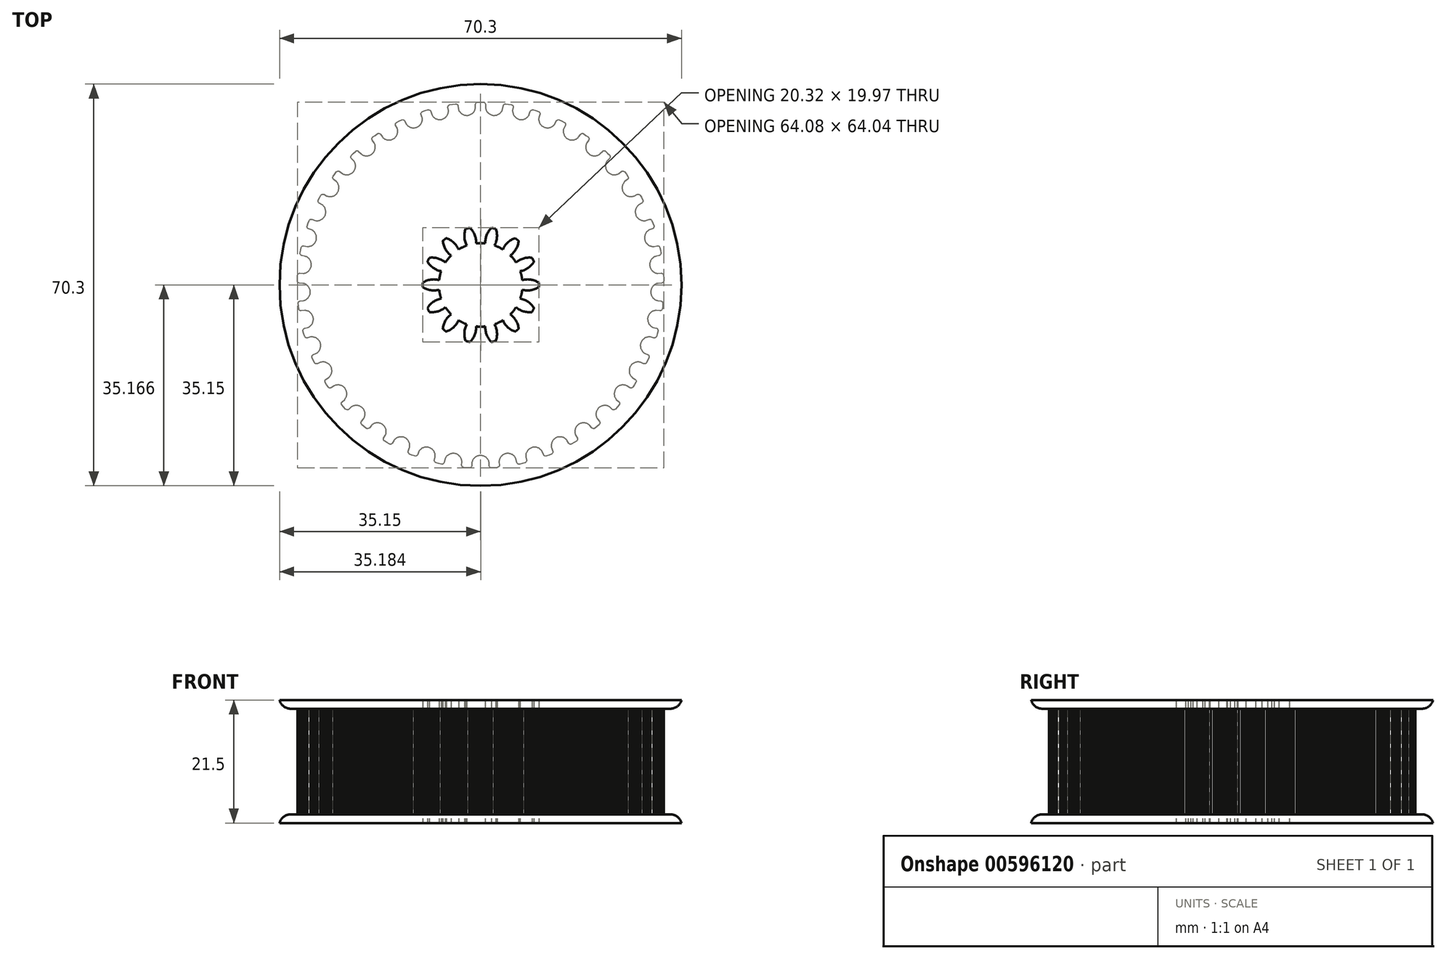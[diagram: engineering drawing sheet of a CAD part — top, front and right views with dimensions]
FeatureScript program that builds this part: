
annotation { "Feature Type Name" : "Feature", "Feature Type Description" : "" }
export const myFeature = defineFeature(function(context is Context, id is Id, definition is map)
    precondition{}
    {
        {
            assignVariable(context, id + "F0", {"name" : "totalThick", "anyValue" : 21.5});
        }
        {
            assignVariable(context, id + "F1", {"name" : "idlerThick", "anyValue" : 1.5});
        }
        {
            assignVariable(context, id + "F2", {"name" : "filletSize", "anyValue" : 2});
        }
        {
            var Q0;
            Q0=qCreatedBy(makeId("Top.planeOp"),FACE);
            var sketch = newSketch(context, id + "F3", { "sketchPlane" : qUnion([Q0])});
            skLineSegment(sketch, "E0", {"start": v(2.45, -32) * mm, "end": v(2.94, -31.95) * mm});
            skLineSegment(sketch, "E1", {"start": v(2.94, -31.95) * mm, "end": v(3.07, -31.9) * mm});
            skLineSegment(sketch, "E2", {"start": v(3.07, -31.9) * mm, "end": v(3.19, -31.81) * mm});
            skLineSegment(sketch, "E3", {"start": v(3.19, -31.81) * mm, "end": v(3.27, -31.68) * mm});
            skLineSegment(sketch, "E4", {"start": v(3.27, -31.68) * mm, "end": v(3.3, -31.54) * mm});
            skLineSegment(sketch, "E5", {"start": v(3.3, -31.54) * mm, "end": v(3.25, -30.93) * mm});
            skLineSegment(sketch, "E6", {"start": v(3.25, -30.93) * mm, "end": v(3.26, -30.8) * mm});
            skLineSegment(sketch, "E7", {"start": v(3.26, -30.8) * mm, "end": v(3.28, -30.67) * mm});
            skLineSegment(sketch, "E8", {"start": v(3.28, -30.67) * mm, "end": v(3.32, -30.55) * mm});
            skLineSegment(sketch, "E9", {"start": v(3.32, -30.55) * mm, "end": v(3.36, -30.42) * mm});
            skLineSegment(sketch, "E10", {"start": v(3.36, -30.42) * mm, "end": v(3.41, -30.3) * mm});
            skLineSegment(sketch, "E11", {"start": v(3.41, -30.3) * mm, "end": v(3.48, -30.2) * mm});
            skLineSegment(sketch, "E12", {"start": v(3.48, -30.2) * mm, "end": v(3.55, -30.09) * mm});
            skLineSegment(sketch, "E13", {"start": v(3.55, -30.09) * mm, "end": v(3.63, -30) * mm});
            skLineSegment(sketch, "E14", {"start": v(3.63, -30) * mm, "end": v(3.72, -29.9) * mm});
            skLineSegment(sketch, "E15", {"start": v(3.72, -29.9) * mm, "end": v(3.82, -29.81) * mm});
            skLineSegment(sketch, "E16", {"start": v(3.82, -29.81) * mm, "end": v(3.93, -29.73) * mm});
            skLineSegment(sketch, "E17", {"start": v(3.93, -29.73) * mm, "end": v(4.04, -29.66) * mm});
            skLineSegment(sketch, "E18", {"start": v(4.04, -29.66) * mm, "end": v(4.16, -29.6) * mm});
            skLineSegment(sketch, "E19", {"start": v(4.16, -29.6) * mm, "end": v(4.28, -29.55) * mm});
            skLineSegment(sketch, "E20", {"start": v(4.28, -29.55) * mm, "end": v(4.41, -29.5) * mm});
            skLineSegment(sketch, "E21", {"start": v(4.41, -29.5) * mm, "end": v(4.55, -29.48) * mm});
            skLineSegment(sketch, "E22", {"start": v(4.55, -29.48) * mm, "end": v(4.69, -29.47) * mm});
            skLineSegment(sketch, "E23", {"start": v(4.69, -29.47) * mm, "end": v(4.82, -29.47) * mm});
            skLineSegment(sketch, "E24", {"start": v(4.82, -29.47) * mm, "end": v(4.96, -29.48) * mm});
            skLineSegment(sketch, "E25", {"start": v(4.96, -29.48) * mm, "end": v(5.09, -29.5) * mm});
            skLineSegment(sketch, "E26", {"start": v(5.09, -29.5) * mm, "end": v(5.22, -29.53) * mm});
            skLineSegment(sketch, "E27", {"start": v(5.22, -29.53) * mm, "end": v(5.34, -29.58) * mm});
            skLineSegment(sketch, "E28", {"start": v(5.34, -29.58) * mm, "end": v(5.46, -29.63) * mm});
            skLineSegment(sketch, "E29", {"start": v(5.46, -29.63) * mm, "end": v(5.57, -29.7) * mm});
            skLineSegment(sketch, "E30", {"start": v(5.57, -29.7) * mm, "end": v(5.68, -29.76) * mm});
            skLineSegment(sketch, "E31", {"start": v(5.68, -29.76) * mm, "end": v(5.78, -29.84) * mm});
            skLineSegment(sketch, "E32", {"start": v(5.78, -29.84) * mm, "end": v(5.88, -29.93) * mm});
            skLineSegment(sketch, "E33", {"start": v(5.88, -29.93) * mm, "end": v(5.97, -30.02) * mm});
            skLineSegment(sketch, "E34", {"start": v(5.97, -30.02) * mm, "end": v(6.04, -30.12) * mm});
            skLineSegment(sketch, "E35", {"start": v(6.04, -30.12) * mm, "end": v(6.11, -30.23) * mm});
            skLineSegment(sketch, "E36", {"start": v(6.11, -30.23) * mm, "end": v(6.17, -30.35) * mm});
            skLineSegment(sketch, "E37", {"start": v(6.17, -30.35) * mm, "end": v(6.22, -30.47) * mm});
            skLineSegment(sketch, "E38", {"start": v(6.22, -30.47) * mm, "end": v(6.36, -31.06) * mm});
            skLineSegment(sketch, "E39", {"start": v(6.36, -31.06) * mm, "end": v(6.43, -31.2) * mm});
            skLineSegment(sketch, "E40", {"start": v(6.43, -31.2) * mm, "end": v(6.55, -31.3) * mm});
            skLineSegment(sketch, "E41", {"start": v(6.55, -31.3) * mm, "end": v(6.7, -31.35) * mm});
            skLineSegment(sketch, "E42", {"start": v(6.7, -31.35) * mm, "end": v(6.83, -31.35) * mm});
            skLineSegment(sketch, "E43", {"start": v(6.83, -31.35) * mm, "end": v(7.3, -31.25) * mm});
            skLineSegment(sketch, "E44", {"start": v(7.3, -31.25) * mm, "end": v(7.78, -31.12) * mm});
            skLineSegment(sketch, "E45", {"start": v(7.78, -31.12) * mm, "end": v(7.9, -31.06) * mm});
            skLineSegment(sketch, "E46", {"start": v(7.9, -31.06) * mm, "end": v(8, -30.95) * mm});
            skLineSegment(sketch, "E47", {"start": v(8, -30.95) * mm, "end": v(8.06, -30.81) * mm});
            skLineSegment(sketch, "E48", {"start": v(8.06, -30.81) * mm, "end": v(8.07, -30.66) * mm});
            skLineSegment(sketch, "E49", {"start": v(8.07, -30.66) * mm, "end": v(7.93, -30.07) * mm});
            skLineSegment(sketch, "E50", {"start": v(7.93, -30.07) * mm, "end": v(7.92, -29.94) * mm});
            skLineSegment(sketch, "E51", {"start": v(7.92, -29.94) * mm, "end": v(7.92, -29.81) * mm});
            skLineSegment(sketch, "E52", {"start": v(7.92, -29.81) * mm, "end": v(7.94, -29.68) * mm});
            skLineSegment(sketch, "E53", {"start": v(7.94, -29.68) * mm, "end": v(7.96, -29.55) * mm});
            skLineSegment(sketch, "E54", {"start": v(7.96, -29.55) * mm, "end": v(8, -29.43) * mm});
            skLineSegment(sketch, "E55", {"start": v(8, -29.43) * mm, "end": v(8.04, -29.31) * mm});
            skLineSegment(sketch, "E56", {"start": v(8.04, -29.31) * mm, "end": v(8.1, -29.2) * mm});
            skLineSegment(sketch, "E57", {"start": v(8.1, -29.2) * mm, "end": v(8.16, -29.08) * mm});
            skLineSegment(sketch, "E58", {"start": v(8.16, -29.08) * mm, "end": v(8.24, -28.98) * mm});
            skLineSegment(sketch, "E59", {"start": v(8.24, -28.98) * mm, "end": v(8.32, -28.88) * mm});
            skLineSegment(sketch, "E60", {"start": v(8.32, -28.88) * mm, "end": v(8.41, -28.79) * mm});
            skLineSegment(sketch, "E61", {"start": v(8.41, -28.79) * mm, "end": v(8.52, -28.7) * mm});
            skLineSegment(sketch, "E62", {"start": v(8.52, -28.7) * mm, "end": v(8.62, -28.62) * mm});
            skLineSegment(sketch, "E63", {"start": v(8.62, -28.62) * mm, "end": v(8.74, -28.55) * mm});
            skLineSegment(sketch, "E64", {"start": v(8.74, -28.55) * mm, "end": v(8.86, -28.5) * mm});
            skLineSegment(sketch, "E65", {"start": v(8.86, -28.5) * mm, "end": v(8.99, -28.44) * mm});
            skLineSegment(sketch, "E66", {"start": v(8.99, -28.44) * mm, "end": v(9.12, -28.4) * mm});
            skLineSegment(sketch, "E67", {"start": v(9.12, -28.4) * mm, "end": v(9.26, -28.39) * mm});
            skLineSegment(sketch, "E68", {"start": v(9.26, -28.39) * mm, "end": v(9.4, -28.38) * mm});
            skLineSegment(sketch, "E69", {"start": v(9.4, -28.38) * mm, "end": v(9.53, -28.38) * mm});
            skLineSegment(sketch, "E70", {"start": v(9.53, -28.38) * mm, "end": v(9.66, -28.4) * mm});
            skLineSegment(sketch, "E71", {"start": v(9.66, -28.4) * mm, "end": v(9.79, -28.41) * mm});
            skLineSegment(sketch, "E72", {"start": v(9.79, -28.41) * mm, "end": v(9.91, -28.45) * mm});
            skLineSegment(sketch, "E73", {"start": v(9.91, -28.45) * mm, "end": v(10.04, -28.5) * mm});
            skLineSegment(sketch, "E74", {"start": v(10.04, -28.5) * mm, "end": v(10.15, -28.54) * mm});
            skLineSegment(sketch, "E75", {"start": v(10.15, -28.54) * mm, "end": v(10.27, -28.6) * mm});
            skLineSegment(sketch, "E76", {"start": v(10.27, -28.6) * mm, "end": v(10.37, -28.68) * mm});
            skLineSegment(sketch, "E77", {"start": v(10.37, -28.68) * mm, "end": v(10.47, -28.76) * mm});
            skLineSegment(sketch, "E78", {"start": v(10.47, -28.76) * mm, "end": v(10.57, -28.85) * mm});
            skLineSegment(sketch, "E79", {"start": v(10.57, -28.85) * mm, "end": v(10.65, -28.95) * mm});
            skLineSegment(sketch, "E80", {"start": v(10.65, -28.95) * mm, "end": v(10.73, -29.05) * mm});
            skLineSegment(sketch, "E81", {"start": v(10.73, -29.05) * mm, "end": v(10.8, -29.17) * mm});
            skLineSegment(sketch, "E82", {"start": v(10.8, -29.17) * mm, "end": v(11.02, -29.73) * mm});
            skLineSegment(sketch, "E83", {"start": v(11.02, -29.73) * mm, "end": v(11.11, -29.85) * mm});
            skLineSegment(sketch, "E84", {"start": v(11.11, -29.85) * mm, "end": v(11.24, -29.93) * mm});
            skLineSegment(sketch, "E85", {"start": v(11.24, -29.93) * mm, "end": v(11.4, -29.96) * mm});
            skLineSegment(sketch, "E86", {"start": v(11.4, -29.96) * mm, "end": v(11.53, -29.94) * mm});
            skLineSegment(sketch, "E87", {"start": v(11.53, -29.94) * mm, "end": v(11.98, -29.76) * mm});
            skLineSegment(sketch, "E88", {"start": v(11.98, -29.76) * mm, "end": v(12.43, -29.57) * mm});
            skLineSegment(sketch, "E89", {"start": v(12.43, -29.57) * mm, "end": v(12.54, -29.5) * mm});
            skLineSegment(sketch, "E90", {"start": v(12.54, -29.5) * mm, "end": v(12.63, -29.37) * mm});
            skLineSegment(sketch, "E91", {"start": v(12.63, -29.37) * mm, "end": v(12.67, -29.22) * mm});
            skLineSegment(sketch, "E92", {"start": v(12.67, -29.22) * mm, "end": v(12.65, -29.07) * mm});
            skLineSegment(sketch, "E93", {"start": v(12.65, -29.07) * mm, "end": v(12.42, -28.5) * mm});
            skLineSegment(sketch, "E94", {"start": v(12.42, -28.5) * mm, "end": v(12.4, -28.38) * mm});
            skLineSegment(sketch, "E95", {"start": v(12.4, -28.38) * mm, "end": v(12.37, -28.25) * mm});
            skLineSegment(sketch, "E96", {"start": v(12.37, -28.25) * mm, "end": v(12.37, -28.12) * mm});
            skLineSegment(sketch, "E97", {"start": v(12.37, -28.12) * mm, "end": v(12.37, -28) * mm});
            skLineSegment(sketch, "E98", {"start": v(12.37, -28) * mm, "end": v(12.4, -27.87) * mm});
            skLineSegment(sketch, "E99", {"start": v(12.4, -27.87) * mm, "end": v(12.42, -27.74) * mm});
            skLineSegment(sketch, "E100", {"start": v(12.42, -27.74) * mm, "end": v(12.45, -27.62) * mm});
            skLineSegment(sketch, "E101", {"start": v(12.45, -27.62) * mm, "end": v(12.5, -27.5) * mm});
            skLineSegment(sketch, "E102", {"start": v(12.5, -27.5) * mm, "end": v(12.56, -27.38) * mm});
            skLineSegment(sketch, "E103", {"start": v(12.56, -27.38) * mm, "end": v(12.63, -27.27) * mm});
            skLineSegment(sketch, "E104", {"start": v(12.63, -27.27) * mm, "end": v(12.7, -27.16) * mm});
            skLineSegment(sketch, "E105", {"start": v(12.7, -27.16) * mm, "end": v(12.8, -27.06) * mm});
            skLineSegment(sketch, "E106", {"start": v(12.8, -27.06) * mm, "end": v(12.89, -26.97) * mm});
            skLineSegment(sketch, "E107", {"start": v(12.89, -26.97) * mm, "end": v(12.99, -26.88) * mm});
            skLineSegment(sketch, "E108", {"start": v(12.99, -26.88) * mm, "end": v(13.1, -26.8) * mm});
            skLineSegment(sketch, "E109", {"start": v(13.1, -26.8) * mm, "end": v(13.22, -26.73) * mm});
            skLineSegment(sketch, "E110", {"start": v(13.22, -26.73) * mm, "end": v(13.35, -26.68) * mm});
            skLineSegment(sketch, "E111", {"start": v(13.35, -26.68) * mm, "end": v(13.48, -26.64) * mm});
            skLineSegment(sketch, "E112", {"start": v(13.48, -26.64) * mm, "end": v(13.61, -26.61) * mm});
            skLineSegment(sketch, "E113", {"start": v(13.61, -26.61) * mm, "end": v(13.74, -26.6) * mm});
            skLineSegment(sketch, "E114", {"start": v(13.74, -26.6) * mm, "end": v(13.88, -26.58) * mm});
            skLineSegment(sketch, "E115", {"start": v(13.88, -26.58) * mm, "end": v(14, -26.59) * mm});
            skLineSegment(sketch, "E116", {"start": v(14, -26.59) * mm, "end": v(14.14, -26.6) * mm});
            skLineSegment(sketch, "E117", {"start": v(14.14, -26.6) * mm, "end": v(14.26, -26.63) * mm});
            skLineSegment(sketch, "E118", {"start": v(14.26, -26.63) * mm, "end": v(14.39, -26.66) * mm});
            skLineSegment(sketch, "E119", {"start": v(14.39, -26.66) * mm, "end": v(14.5, -26.7) * mm});
            skLineSegment(sketch, "E120", {"start": v(14.5, -26.7) * mm, "end": v(14.62, -26.76) * mm});
            skLineSegment(sketch, "E121", {"start": v(14.62, -26.76) * mm, "end": v(14.74, -26.82) * mm});
            skLineSegment(sketch, "E122", {"start": v(14.74, -26.82) * mm, "end": v(14.84, -26.9) * mm});
            skLineSegment(sketch, "E123", {"start": v(14.84, -26.9) * mm, "end": v(14.94, -26.98) * mm});
            skLineSegment(sketch, "E124", {"start": v(14.94, -26.98) * mm, "end": v(15.03, -27.07) * mm});
            skLineSegment(sketch, "E125", {"start": v(15.03, -27.07) * mm, "end": v(15.12, -27.18) * mm});
            skLineSegment(sketch, "E126", {"start": v(15.12, -27.18) * mm, "end": v(15.42, -27.7) * mm});
            skLineSegment(sketch, "E127", {"start": v(15.42, -27.7) * mm, "end": v(15.53, -27.8) * mm});
            skLineSegment(sketch, "E128", {"start": v(15.53, -27.8) * mm, "end": v(15.67, -27.86) * mm});
            skLineSegment(sketch, "E129", {"start": v(15.67, -27.86) * mm, "end": v(15.83, -27.87) * mm});
            skLineSegment(sketch, "E130", {"start": v(15.83, -27.87) * mm, "end": v(15.96, -27.83) * mm});
            skLineSegment(sketch, "E131", {"start": v(15.96, -27.83) * mm, "end": v(16.38, -27.59) * mm});
            skLineSegment(sketch, "E132", {"start": v(16.38, -27.59) * mm, "end": v(16.8, -27.33) * mm});
            skLineSegment(sketch, "E133", {"start": v(16.8, -27.33) * mm, "end": v(16.9, -27.23) * mm});
            skLineSegment(sketch, "E134", {"start": v(16.9, -27.23) * mm, "end": v(16.96, -27.1) * mm});
            skLineSegment(sketch, "E135", {"start": v(16.96, -27.1) * mm, "end": v(16.98, -26.95) * mm});
            skLineSegment(sketch, "E136", {"start": v(16.98, -26.95) * mm, "end": v(16.94, -26.8) * mm});
            skLineSegment(sketch, "E137", {"start": v(16.94, -26.8) * mm, "end": v(16.62, -26.28) * mm});
            skLineSegment(sketch, "E138", {"start": v(16.62, -26.28) * mm, "end": v(16.58, -26.16) * mm});
            skLineSegment(sketch, "E139", {"start": v(16.58, -26.16) * mm, "end": v(16.54, -26.03) * mm});
            skLineSegment(sketch, "E140", {"start": v(16.54, -26.03) * mm, "end": v(16.51, -25.9) * mm});
            skLineSegment(sketch, "E141", {"start": v(16.51, -25.9) * mm, "end": v(16.5, -25.78) * mm});
            skLineSegment(sketch, "E142", {"start": v(16.5, -25.78) * mm, "end": v(16.5, -25.65) * mm});
            skLineSegment(sketch, "E143", {"start": v(16.5, -25.65) * mm, "end": v(16.5, -25.52) * mm});
            skLineSegment(sketch, "E144", {"start": v(16.5, -25.52) * mm, "end": v(16.52, -25.4) * mm});
            skLineSegment(sketch, "E145", {"start": v(16.52, -25.4) * mm, "end": v(16.55, -25.27) * mm});
            skLineSegment(sketch, "E146", {"start": v(16.55, -25.27) * mm, "end": v(16.59, -25.14) * mm});
            skLineSegment(sketch, "E147", {"start": v(16.59, -25.14) * mm, "end": v(16.64, -25.02) * mm});
            skLineSegment(sketch, "E148", {"start": v(16.64, -25.02) * mm, "end": v(16.7, -24.9) * mm});
            skLineSegment(sketch, "E149", {"start": v(16.7, -24.9) * mm, "end": v(16.77, -24.8) * mm});
            skLineSegment(sketch, "E150", {"start": v(16.77, -24.8) * mm, "end": v(16.85, -24.69) * mm});
            skLineSegment(sketch, "E151", {"start": v(16.85, -24.69) * mm, "end": v(16.94, -24.59) * mm});
            skLineSegment(sketch, "E152", {"start": v(16.94, -24.59) * mm, "end": v(17.03, -24.5) * mm});
            skLineSegment(sketch, "E153", {"start": v(17.03, -24.5) * mm, "end": v(17.14, -24.4) * mm});
            skLineSegment(sketch, "E154", {"start": v(17.14, -24.4) * mm, "end": v(17.26, -24.33) * mm});
            skLineSegment(sketch, "E155", {"start": v(17.26, -24.33) * mm, "end": v(17.38, -24.27) * mm});
            skLineSegment(sketch, "E156", {"start": v(17.38, -24.27) * mm, "end": v(17.5, -24.22) * mm});
            skLineSegment(sketch, "E157", {"start": v(17.5, -24.22) * mm, "end": v(17.64, -24.18) * mm});
            skLineSegment(sketch, "E158", {"start": v(17.64, -24.18) * mm, "end": v(17.77, -24.16) * mm});
            skLineSegment(sketch, "E159", {"start": v(17.77, -24.16) * mm, "end": v(17.9, -24.14) * mm});
            skLineSegment(sketch, "E160", {"start": v(17.9, -24.14) * mm, "end": v(18.03, -24.13) * mm});
            skLineSegment(sketch, "E161", {"start": v(18.03, -24.13) * mm, "end": v(18.16, -24.14) * mm});
            skLineSegment(sketch, "E162", {"start": v(18.16, -24.14) * mm, "end": v(18.28, -24.15) * mm});
            skLineSegment(sketch, "E163", {"start": v(18.28, -24.15) * mm, "end": v(18.4, -24.18) * mm});
            skLineSegment(sketch, "E164", {"start": v(18.4, -24.18) * mm, "end": v(18.53, -24.21) * mm});
            skLineSegment(sketch, "E165", {"start": v(18.53, -24.21) * mm, "end": v(18.65, -24.26) * mm});
            skLineSegment(sketch, "E166", {"start": v(18.65, -24.26) * mm, "end": v(18.77, -24.32) * mm});
            skLineSegment(sketch, "E167", {"start": v(18.77, -24.32) * mm, "end": v(18.88, -24.39) * mm});
            skLineSegment(sketch, "E168", {"start": v(18.88, -24.39) * mm, "end": v(18.98, -24.46) * mm});
            skLineSegment(sketch, "E169", {"start": v(18.98, -24.46) * mm, "end": v(19.08, -24.55) * mm});
            skLineSegment(sketch, "E170", {"start": v(19.08, -24.55) * mm, "end": v(19.47, -25.02) * mm});
            skLineSegment(sketch, "E171", {"start": v(19.47, -25.02) * mm, "end": v(19.6, -25.1) * mm});
            skLineSegment(sketch, "E172", {"start": v(19.6, -25.1) * mm, "end": v(19.74, -25.14) * mm});
            skLineSegment(sketch, "E173", {"start": v(19.74, -25.14) * mm, "end": v(19.9, -25.12) * mm});
            skLineSegment(sketch, "E174", {"start": v(19.9, -25.12) * mm, "end": v(20.01, -25.07) * mm});
            skLineSegment(sketch, "E175", {"start": v(20.01, -25.07) * mm, "end": v(20.4, -24.76) * mm});
            skLineSegment(sketch, "E176", {"start": v(20.4, -24.76) * mm, "end": v(20.77, -24.45) * mm});
            skLineSegment(sketch, "E177", {"start": v(20.77, -24.45) * mm, "end": v(20.85, -24.34) * mm});
            skLineSegment(sketch, "E178", {"start": v(20.85, -24.34) * mm, "end": v(20.9, -24.2) * mm});
            skLineSegment(sketch, "E179", {"start": v(20.9, -24.2) * mm, "end": v(20.88, -24.04) * mm});
            skLineSegment(sketch, "E180", {"start": v(20.88, -24.04) * mm, "end": v(20.83, -23.9) * mm});
            skLineSegment(sketch, "E181", {"start": v(20.83, -23.9) * mm, "end": v(20.44, -23.43) * mm});
            skLineSegment(sketch, "E182", {"start": v(20.44, -23.43) * mm, "end": v(20.37, -23.32) * mm});
            skLineSegment(sketch, "E183", {"start": v(20.37, -23.32) * mm, "end": v(20.31, -23.2) * mm});
            skLineSegment(sketch, "E184", {"start": v(20.31, -23.2) * mm, "end": v(20.27, -23.08) * mm});
            skLineSegment(sketch, "E185", {"start": v(20.27, -23.08) * mm, "end": v(20.23, -22.96) * mm});
            skLineSegment(sketch, "E186", {"start": v(20.23, -22.96) * mm, "end": v(20.21, -22.83) * mm});
            skLineSegment(sketch, "E187", {"start": v(20.21, -22.83) * mm, "end": v(20.2, -22.7) * mm});
            skLineSegment(sketch, "E188", {"start": v(20.2, -22.7) * mm, "end": v(20.2, -22.57) * mm});
            skLineSegment(sketch, "E189", {"start": v(20.2, -22.57) * mm, "end": v(20.2, -22.45) * mm});
            skLineSegment(sketch, "E190", {"start": v(20.2, -22.45) * mm, "end": v(20.23, -22.32) * mm});
            skLineSegment(sketch, "E191", {"start": v(20.23, -22.32) * mm, "end": v(20.26, -22.2) * mm});
            skLineSegment(sketch, "E192", {"start": v(20.26, -22.2) * mm, "end": v(20.3, -22.07) * mm});
            skLineSegment(sketch, "E193", {"start": v(20.3, -22.07) * mm, "end": v(20.35, -21.94) * mm});
            skLineSegment(sketch, "E194", {"start": v(20.35, -21.94) * mm, "end": v(20.41, -21.83) * mm});
            skLineSegment(sketch, "E195", {"start": v(20.41, -21.83) * mm, "end": v(20.49, -21.71) * mm});
            skLineSegment(sketch, "E196", {"start": v(20.49, -21.71) * mm, "end": v(20.57, -21.6) * mm});
            skLineSegment(sketch, "E197", {"start": v(20.57, -21.6) * mm, "end": v(20.66, -21.5) * mm});
            skLineSegment(sketch, "E198", {"start": v(20.66, -21.5) * mm, "end": v(20.77, -21.41) * mm});
            skLineSegment(sketch, "E199", {"start": v(20.77, -21.41) * mm, "end": v(20.88, -21.33) * mm});
            skLineSegment(sketch, "E200", {"start": v(20.88, -21.33) * mm, "end": v(21, -21.27) * mm});
            skLineSegment(sketch, "E201", {"start": v(21, -21.27) * mm, "end": v(21.12, -21.2) * mm});
            skLineSegment(sketch, "E202", {"start": v(21.12, -21.2) * mm, "end": v(21.24, -21.16) * mm});
            skLineSegment(sketch, "E203", {"start": v(21.24, -21.16) * mm, "end": v(21.37, -21.12) * mm});
            skLineSegment(sketch, "E204", {"start": v(21.37, -21.12) * mm, "end": v(21.5, -21.1) * mm});
            skLineSegment(sketch, "E205", {"start": v(21.5, -21.1) * mm, "end": v(21.62, -21.08) * mm});
            skLineSegment(sketch, "E206", {"start": v(21.62, -21.08) * mm, "end": v(21.75, -21.08) * mm});
            skLineSegment(sketch, "E207", {"start": v(21.75, -21.08) * mm, "end": v(21.88, -21.08) * mm});
            skLineSegment(sketch, "E208", {"start": v(21.88, -21.08) * mm, "end": v(22, -21.1) * mm});
            skLineSegment(sketch, "E209", {"start": v(22, -21.1) * mm, "end": v(22.13, -21.13) * mm});
            skLineSegment(sketch, "E210", {"start": v(22.13, -21.13) * mm, "end": v(22.26, -21.17) * mm});
            skLineSegment(sketch, "E211", {"start": v(22.26, -21.17) * mm, "end": v(22.38, -21.22) * mm});
            skLineSegment(sketch, "E212", {"start": v(22.38, -21.22) * mm, "end": v(22.5, -21.28) * mm});
            skLineSegment(sketch, "E213", {"start": v(22.5, -21.28) * mm, "end": v(22.6, -21.35) * mm});
            skLineSegment(sketch, "E214", {"start": v(22.6, -21.35) * mm, "end": v(23.05, -21.76) * mm});
            skLineSegment(sketch, "E215", {"start": v(23.05, -21.76) * mm, "end": v(23.19, -21.82) * mm});
            skLineSegment(sketch, "E216", {"start": v(23.19, -21.82) * mm, "end": v(23.34, -21.83) * mm});
            skLineSegment(sketch, "E217", {"start": v(23.34, -21.83) * mm, "end": v(23.49, -21.8) * mm});
            skLineSegment(sketch, "E218", {"start": v(23.49, -21.8) * mm, "end": v(23.6, -21.72) * mm});
            skLineSegment(sketch, "E219", {"start": v(23.6, -21.72) * mm, "end": v(23.93, -21.36) * mm});
            skLineSegment(sketch, "E220", {"start": v(23.93, -21.36) * mm, "end": v(24.25, -20.99) * mm});
            skLineSegment(sketch, "E221", {"start": v(24.25, -20.99) * mm, "end": v(24.31, -20.87) * mm});
            skLineSegment(sketch, "E222", {"start": v(24.31, -20.87) * mm, "end": v(24.33, -20.72) * mm});
            skLineSegment(sketch, "E223", {"start": v(24.33, -20.72) * mm, "end": v(24.3, -20.57) * mm});
            skLineSegment(sketch, "E224", {"start": v(24.3, -20.57) * mm, "end": v(24.22, -20.44) * mm});
            skLineSegment(sketch, "E225", {"start": v(24.22, -20.44) * mm, "end": v(23.77, -20.04) * mm});
            skLineSegment(sketch, "E226", {"start": v(23.77, -20.04) * mm, "end": v(23.68, -19.94) * mm});
            skLineSegment(sketch, "E227", {"start": v(23.68, -19.94) * mm, "end": v(23.61, -19.83) * mm});
            skLineSegment(sketch, "E228", {"start": v(23.61, -19.83) * mm, "end": v(23.55, -19.72) * mm});
            skLineSegment(sketch, "E229", {"start": v(23.55, -19.72) * mm, "end": v(23.5, -19.6) * mm});
            skLineSegment(sketch, "E230", {"start": v(23.5, -19.6) * mm, "end": v(23.45, -19.48) * mm});
            skLineSegment(sketch, "E231", {"start": v(23.45, -19.48) * mm, "end": v(23.42, -19.35) * mm});
            skLineSegment(sketch, "E232", {"start": v(23.42, -19.35) * mm, "end": v(23.4, -19.23) * mm});
            skLineSegment(sketch, "E233", {"start": v(23.4, -19.23) * mm, "end": v(23.4, -19.1) * mm});
            skLineSegment(sketch, "E234", {"start": v(23.4, -19.1) * mm, "end": v(23.4, -18.97) * mm});
            skLineSegment(sketch, "E235", {"start": v(23.4, -18.97) * mm, "end": v(23.4, -18.84) * mm});
            skLineSegment(sketch, "E236", {"start": v(23.4, -18.84) * mm, "end": v(23.42, -18.7) * mm});
            skLineSegment(sketch, "E237", {"start": v(23.42, -18.7) * mm, "end": v(23.46, -18.58) * mm});
            skLineSegment(sketch, "E238", {"start": v(23.46, -18.58) * mm, "end": v(23.5, -18.46) * mm});
            skLineSegment(sketch, "E239", {"start": v(23.5, -18.46) * mm, "end": v(23.55, -18.33) * mm});
            skLineSegment(sketch, "E240", {"start": v(23.55, -18.33) * mm, "end": v(23.62, -18.21) * mm});
            skLineSegment(sketch, "E241", {"start": v(23.62, -18.21) * mm, "end": v(23.7, -18.1) * mm});
            skLineSegment(sketch, "E242", {"start": v(23.7, -18.1) * mm, "end": v(23.79, -18) * mm});
            skLineSegment(sketch, "E243", {"start": v(23.79, -18) * mm, "end": v(23.89, -17.9) * mm});
            skLineSegment(sketch, "E244", {"start": v(23.89, -17.9) * mm, "end": v(24, -17.81) * mm});
            skLineSegment(sketch, "E245", {"start": v(24, -17.81) * mm, "end": v(24.1, -17.74) * mm});
            skLineSegment(sketch, "E246", {"start": v(24.1, -17.74) * mm, "end": v(24.22, -17.67) * mm});
            skLineSegment(sketch, "E247", {"start": v(24.22, -17.67) * mm, "end": v(24.33, -17.62) * mm});
            skLineSegment(sketch, "E248", {"start": v(24.33, -17.62) * mm, "end": v(24.46, -17.57) * mm});
            skLineSegment(sketch, "E249", {"start": v(24.46, -17.57) * mm, "end": v(24.58, -17.54) * mm});
            skLineSegment(sketch, "E250", {"start": v(24.58, -17.54) * mm, "end": v(24.7, -17.51) * mm});
            skLineSegment(sketch, "E251", {"start": v(24.7, -17.51) * mm, "end": v(24.84, -17.5) * mm});
            skLineSegment(sketch, "E252", {"start": v(24.84, -17.5) * mm, "end": v(24.97, -17.5) * mm});
            skLineSegment(sketch, "E253", {"start": v(24.97, -17.5) * mm, "end": v(25.1, -17.5) * mm});
            skLineSegment(sketch, "E254", {"start": v(25.1, -17.5) * mm, "end": v(25.22, -17.52) * mm});
            skLineSegment(sketch, "E255", {"start": v(25.22, -17.52) * mm, "end": v(25.35, -17.55) * mm});
            skLineSegment(sketch, "E256", {"start": v(25.35, -17.55) * mm, "end": v(25.47, -17.6) * mm});
            skLineSegment(sketch, "E257", {"start": v(25.47, -17.6) * mm, "end": v(25.6, -17.65) * mm});
            skLineSegment(sketch, "E258", {"start": v(25.6, -17.65) * mm, "end": v(26.1, -17.98) * mm});
            skLineSegment(sketch, "E259", {"start": v(26.1, -17.98) * mm, "end": v(26.24, -18.03) * mm});
            skLineSegment(sketch, "E260", {"start": v(26.24, -18.03) * mm, "end": v(26.4, -18.02) * mm});
            skLineSegment(sketch, "E261", {"start": v(26.4, -18.02) * mm, "end": v(26.53, -17.95) * mm});
            skLineSegment(sketch, "E262", {"start": v(26.53, -17.95) * mm, "end": v(26.63, -17.86) * mm});
            skLineSegment(sketch, "E263", {"start": v(26.63, -17.86) * mm, "end": v(26.9, -17.46) * mm});
            skLineSegment(sketch, "E264", {"start": v(26.9, -17.46) * mm, "end": v(27.16, -17.04) * mm});
            skLineSegment(sketch, "E265", {"start": v(27.16, -17.04) * mm, "end": v(27.2, -16.91) * mm});
            skLineSegment(sketch, "E266", {"start": v(27.2, -16.91) * mm, "end": v(27.2, -16.76) * mm});
            skLineSegment(sketch, "E267", {"start": v(27.2, -16.76) * mm, "end": v(27.16, -16.62) * mm});
            skLineSegment(sketch, "E268", {"start": v(27.16, -16.62) * mm, "end": v(27.06, -16.5) * mm});
            skLineSegment(sketch, "E269", {"start": v(27.06, -16.5) * mm, "end": v(26.54, -16.18) * mm});
            skLineSegment(sketch, "E270", {"start": v(26.54, -16.18) * mm, "end": v(26.45, -16.09) * mm});
            skLineSegment(sketch, "E271", {"start": v(26.45, -16.09) * mm, "end": v(26.36, -16) * mm});
            skLineSegment(sketch, "E272", {"start": v(26.36, -16) * mm, "end": v(26.28, -15.9) * mm});
            skLineSegment(sketch, "E273", {"start": v(26.28, -15.9) * mm, "end": v(26.2, -15.78) * mm});
            skLineSegment(sketch, "E274", {"start": v(26.2, -15.78) * mm, "end": v(26.15, -15.67) * mm});
            skLineSegment(sketch, "E275", {"start": v(26.15, -15.67) * mm, "end": v(26.1, -15.55) * mm});
            skLineSegment(sketch, "E276", {"start": v(26.1, -15.55) * mm, "end": v(26.06, -15.43) * mm});
            skLineSegment(sketch, "E277", {"start": v(26.06, -15.43) * mm, "end": v(26.03, -15.3) * mm});
            skLineSegment(sketch, "E278", {"start": v(26.03, -15.3) * mm, "end": v(26, -15.18) * mm});
            skLineSegment(sketch, "E279", {"start": v(26, -15.18) * mm, "end": v(26, -15.05) * mm});
            skLineSegment(sketch, "E280", {"start": v(26, -15.05) * mm, "end": v(26, -14.91) * mm});
            skLineSegment(sketch, "E281", {"start": v(26, -14.91) * mm, "end": v(26.01, -14.78) * mm});
            skLineSegment(sketch, "E282", {"start": v(26.01, -14.78) * mm, "end": v(26.04, -14.65) * mm});
            skLineSegment(sketch, "E283", {"start": v(26.04, -14.65) * mm, "end": v(26.07, -14.52) * mm});
            skLineSegment(sketch, "E284", {"start": v(26.07, -14.52) * mm, "end": v(26.12, -14.4) * mm});
            skLineSegment(sketch, "E285", {"start": v(26.12, -14.4) * mm, "end": v(26.18, -14.27) * mm});
            skLineSegment(sketch, "E286", {"start": v(26.18, -14.27) * mm, "end": v(26.25, -14.15) * mm});
            skLineSegment(sketch, "E287", {"start": v(26.25, -14.15) * mm, "end": v(26.33, -14.04) * mm});
            skLineSegment(sketch, "E288", {"start": v(26.33, -14.04) * mm, "end": v(26.42, -13.94) * mm});
            skLineSegment(sketch, "E289", {"start": v(26.42, -13.94) * mm, "end": v(26.52, -13.85) * mm});
            skLineSegment(sketch, "E290", {"start": v(26.52, -13.85) * mm, "end": v(26.62, -13.77) * mm});
            skLineSegment(sketch, "E291", {"start": v(26.62, -13.77) * mm, "end": v(26.73, -13.7) * mm});
            skLineSegment(sketch, "E292", {"start": v(26.73, -13.7) * mm, "end": v(26.85, -13.63) * mm});
            skLineSegment(sketch, "E293", {"start": v(26.85, -13.63) * mm, "end": v(26.97, -13.58) * mm});
            skLineSegment(sketch, "E294", {"start": v(26.97, -13.58) * mm, "end": v(27.09, -13.53) * mm});
            skLineSegment(sketch, "E295", {"start": v(27.09, -13.53) * mm, "end": v(27.21, -13.5) * mm});
            skLineSegment(sketch, "E296", {"start": v(27.21, -13.5) * mm, "end": v(27.34, -13.48) * mm});
            skLineSegment(sketch, "E297", {"start": v(27.34, -13.48) * mm, "end": v(27.47, -13.47) * mm});
            skLineSegment(sketch, "E298", {"start": v(27.47, -13.47) * mm, "end": v(27.6, -13.47) * mm});
            skLineSegment(sketch, "E299", {"start": v(27.6, -13.47) * mm, "end": v(27.72, -13.48) * mm});
            skLineSegment(sketch, "E300", {"start": v(27.72, -13.48) * mm, "end": v(27.85, -13.5) * mm});
            skLineSegment(sketch, "E301", {"start": v(27.85, -13.5) * mm, "end": v(27.98, -13.54) * mm});
            skLineSegment(sketch, "E302", {"start": v(27.98, -13.54) * mm, "end": v(28.53, -13.8) * mm});
            skLineSegment(sketch, "E303", {"start": v(28.53, -13.8) * mm, "end": v(28.68, -13.8) * mm});
            skLineSegment(sketch, "E304", {"start": v(28.68, -13.8) * mm, "end": v(28.83, -13.78) * mm});
            skLineSegment(sketch, "E305", {"start": v(28.83, -13.78) * mm, "end": v(28.96, -13.7) * mm});
            skLineSegment(sketch, "E306", {"start": v(28.96, -13.7) * mm, "end": v(29.04, -13.59) * mm});
            skLineSegment(sketch, "E307", {"start": v(29.04, -13.59) * mm, "end": v(29.25, -13.15) * mm});
            skLineSegment(sketch, "E308", {"start": v(29.25, -13.15) * mm, "end": v(29.44, -12.7) * mm});
            skLineSegment(sketch, "E309", {"start": v(29.44, -12.7) * mm, "end": v(29.47, -12.56) * mm});
            skLineSegment(sketch, "E310", {"start": v(29.47, -12.56) * mm, "end": v(29.44, -12.41) * mm});
            skLineSegment(sketch, "E311", {"start": v(29.44, -12.41) * mm, "end": v(29.37, -12.28) * mm});
            skLineSegment(sketch, "E312", {"start": v(29.37, -12.28) * mm, "end": v(29.25, -12.18) * mm});
            skLineSegment(sketch, "E313", {"start": v(29.25, -12.18) * mm, "end": v(28.7, -11.94) * mm});
            skLineSegment(sketch, "E314", {"start": v(28.7, -11.94) * mm, "end": v(28.59, -11.86) * mm});
            skLineSegment(sketch, "E315", {"start": v(28.59, -11.86) * mm, "end": v(28.48, -11.78) * mm});
            skLineSegment(sketch, "E316", {"start": v(28.48, -11.78) * mm, "end": v(28.4, -11.7) * mm});
            skLineSegment(sketch, "E317", {"start": v(28.4, -11.7) * mm, "end": v(28.3, -11.6) * mm});
            skLineSegment(sketch, "E318", {"start": v(28.3, -11.6) * mm, "end": v(28.23, -11.5) * mm});
            skLineSegment(sketch, "E319", {"start": v(28.23, -11.5) * mm, "end": v(28.16, -11.39) * mm});
            skLineSegment(sketch, "E320", {"start": v(28.16, -11.39) * mm, "end": v(28.1, -11.27) * mm});
            skLineSegment(sketch, "E321", {"start": v(28.1, -11.27) * mm, "end": v(28.05, -11.15) * mm});
            skLineSegment(sketch, "E322", {"start": v(28.05, -11.15) * mm, "end": v(28.01, -11.03) * mm});
            skLineSegment(sketch, "E323", {"start": v(28.01, -11.03) * mm, "end": v(27.99, -10.9) * mm});
            skLineSegment(sketch, "E324", {"start": v(27.99, -10.9) * mm, "end": v(27.97, -10.77) * mm});
            skLineSegment(sketch, "E325", {"start": v(27.97, -10.77) * mm, "end": v(27.96, -10.64) * mm});
            skLineSegment(sketch, "E326", {"start": v(27.96, -10.64) * mm, "end": v(27.96, -10.5) * mm});
            skLineSegment(sketch, "E327", {"start": v(27.96, -10.5) * mm, "end": v(27.98, -10.37) * mm});
            skLineSegment(sketch, "E328", {"start": v(27.98, -10.37) * mm, "end": v(28, -10.24) * mm});
            skLineSegment(sketch, "E329", {"start": v(28, -10.24) * mm, "end": v(28.04, -10.1) * mm});
            skLineSegment(sketch, "E330", {"start": v(28.04, -10.1) * mm, "end": v(28.1, -9.98) * mm});
            skLineSegment(sketch, "E331", {"start": v(28.1, -9.98) * mm, "end": v(28.16, -9.86) * mm});
            skLineSegment(sketch, "E332", {"start": v(28.16, -9.86) * mm, "end": v(28.24, -9.74) * mm});
            skLineSegment(sketch, "E333", {"start": v(28.24, -9.74) * mm, "end": v(28.32, -9.64) * mm});
            skLineSegment(sketch, "E334", {"start": v(28.32, -9.64) * mm, "end": v(28.4, -9.54) * mm});
            skLineSegment(sketch, "E335", {"start": v(28.4, -9.54) * mm, "end": v(28.5, -9.45) * mm});
            skLineSegment(sketch, "E336", {"start": v(28.5, -9.45) * mm, "end": v(28.6, -9.37) * mm});
            skLineSegment(sketch, "E337", {"start": v(28.6, -9.37) * mm, "end": v(28.72, -9.3) * mm});
            skLineSegment(sketch, "E338", {"start": v(28.72, -9.3) * mm, "end": v(28.83, -9.24) * mm});
            skLineSegment(sketch, "E339", {"start": v(28.83, -9.24) * mm, "end": v(28.95, -9.2) * mm});
            skLineSegment(sketch, "E340", {"start": v(28.95, -9.2) * mm, "end": v(29.07, -9.15) * mm});
            skLineSegment(sketch, "E341", {"start": v(29.07, -9.15) * mm, "end": v(29.2, -9.12) * mm});
            skLineSegment(sketch, "E342", {"start": v(29.2, -9.12) * mm, "end": v(29.32, -9.1) * mm});
            skLineSegment(sketch, "E343", {"start": v(29.32, -9.1) * mm, "end": v(29.45, -9.09) * mm});
            skLineSegment(sketch, "E344", {"start": v(29.45, -9.09) * mm, "end": v(29.58, -9.1) * mm});
            skLineSegment(sketch, "E345", {"start": v(29.58, -9.1) * mm, "end": v(29.71, -9.1) * mm});
            skLineSegment(sketch, "E346", {"start": v(29.71, -9.1) * mm, "end": v(30.3, -9.27) * mm});
            skLineSegment(sketch, "E347", {"start": v(30.3, -9.27) * mm, "end": v(30.45, -9.27) * mm});
            skLineSegment(sketch, "E348", {"start": v(30.45, -9.27) * mm, "end": v(30.59, -9.21) * mm});
            skLineSegment(sketch, "E349", {"start": v(30.59, -9.21) * mm, "end": v(30.7, -9.11) * mm});
            skLineSegment(sketch, "E350", {"start": v(30.7, -9.11) * mm, "end": v(30.77, -9) * mm});
            skLineSegment(sketch, "E351", {"start": v(30.77, -9) * mm, "end": v(30.9, -8.53) * mm});
            skLineSegment(sketch, "E352", {"start": v(30.9, -8.53) * mm, "end": v(31.03, -8.05) * mm});
            skLineSegment(sketch, "E353", {"start": v(31.03, -8.05) * mm, "end": v(31.03, -7.92) * mm});
            skLineSegment(sketch, "E354", {"start": v(31.03, -7.92) * mm, "end": v(30.99, -7.77) * mm});
            skLineSegment(sketch, "E355", {"start": v(30.99, -7.77) * mm, "end": v(30.9, -7.65) * mm});
            skLineSegment(sketch, "E356", {"start": v(30.9, -7.65) * mm, "end": v(30.77, -7.57) * mm});
            skLineSegment(sketch, "E357", {"start": v(30.77, -7.57) * mm, "end": v(30.18, -7.42) * mm});
            skLineSegment(sketch, "E358", {"start": v(30.18, -7.42) * mm, "end": v(30.06, -7.36) * mm});
            skLineSegment(sketch, "E359", {"start": v(30.06, -7.36) * mm, "end": v(29.94, -7.3) * mm});
            skLineSegment(sketch, "E360", {"start": v(29.94, -7.3) * mm, "end": v(29.84, -7.22) * mm});
            skLineSegment(sketch, "E361", {"start": v(29.84, -7.22) * mm, "end": v(29.74, -7.14) * mm});
            skLineSegment(sketch, "E362", {"start": v(29.74, -7.14) * mm, "end": v(29.65, -7.05) * mm});
            skLineSegment(sketch, "E363", {"start": v(29.65, -7.05) * mm, "end": v(29.56, -6.95) * mm});
            skLineSegment(sketch, "E364", {"start": v(29.56, -6.95) * mm, "end": v(29.49, -6.85) * mm});
            skLineSegment(sketch, "E365", {"start": v(29.49, -6.85) * mm, "end": v(29.42, -6.74) * mm});
            skLineSegment(sketch, "E366", {"start": v(29.42, -6.74) * mm, "end": v(29.36, -6.62) * mm});
            skLineSegment(sketch, "E367", {"start": v(29.36, -6.62) * mm, "end": v(29.32, -6.5) * mm});
            skLineSegment(sketch, "E368", {"start": v(29.32, -6.5) * mm, "end": v(29.28, -6.38) * mm});
            skLineSegment(sketch, "E369", {"start": v(29.28, -6.38) * mm, "end": v(29.25, -6.25) * mm});
            skLineSegment(sketch, "E370", {"start": v(29.25, -6.25) * mm, "end": v(29.23, -6.11) * mm});
            skLineSegment(sketch, "E371", {"start": v(29.23, -6.11) * mm, "end": v(29.23, -5.98) * mm});
            skLineSegment(sketch, "E372", {"start": v(29.23, -5.98) * mm, "end": v(29.23, -5.84) * mm});
            skLineSegment(sketch, "E373", {"start": v(29.23, -5.84) * mm, "end": v(29.25, -5.7) * mm});
            skLineSegment(sketch, "E374", {"start": v(29.25, -5.7) * mm, "end": v(29.29, -5.57) * mm});
            skLineSegment(sketch, "E375", {"start": v(29.29, -5.57) * mm, "end": v(29.33, -5.44) * mm});
            skLineSegment(sketch, "E376", {"start": v(29.33, -5.44) * mm, "end": v(29.39, -5.32) * mm});
            skLineSegment(sketch, "E377", {"start": v(29.39, -5.32) * mm, "end": v(29.45, -5.2) * mm});
            skLineSegment(sketch, "E378", {"start": v(29.45, -5.2) * mm, "end": v(29.53, -5.1) * mm});
            skLineSegment(sketch, "E379", {"start": v(29.53, -5.1) * mm, "end": v(29.6, -5) * mm});
            skLineSegment(sketch, "E380", {"start": v(29.6, -5) * mm, "end": v(29.7, -4.9) * mm});
            skLineSegment(sketch, "E381", {"start": v(29.7, -4.9) * mm, "end": v(29.8, -4.81) * mm});
            skLineSegment(sketch, "E382", {"start": v(29.8, -4.81) * mm, "end": v(29.9, -4.73) * mm});
            skLineSegment(sketch, "E383", {"start": v(29.9, -4.73) * mm, "end": v(30, -4.66) * mm});
            skLineSegment(sketch, "E384", {"start": v(30, -4.66) * mm, "end": v(30.12, -4.6) * mm});
            skLineSegment(sketch, "E385", {"start": v(30.12, -4.6) * mm, "end": v(30.24, -4.56) * mm});
            skLineSegment(sketch, "E386", {"start": v(30.24, -4.56) * mm, "end": v(30.36, -4.52) * mm});
            skLineSegment(sketch, "E387", {"start": v(30.36, -4.52) * mm, "end": v(30.49, -4.49) * mm});
            skLineSegment(sketch, "E388", {"start": v(30.49, -4.49) * mm, "end": v(30.62, -4.47) * mm});
            skLineSegment(sketch, "E389", {"start": v(30.62, -4.47) * mm, "end": v(30.75, -4.47) * mm});
            skLineSegment(sketch, "E390", {"start": v(30.75, -4.47) * mm, "end": v(31.35, -4.54) * mm});
            skLineSegment(sketch, "E391", {"start": v(31.35, -4.54) * mm, "end": v(31.5, -4.51) * mm});
            skLineSegment(sketch, "E392", {"start": v(31.5, -4.51) * mm, "end": v(31.63, -4.44) * mm});
            skLineSegment(sketch, "E393", {"start": v(31.63, -4.44) * mm, "end": v(31.73, -4.32) * mm});
            skLineSegment(sketch, "E394", {"start": v(31.73, -4.32) * mm, "end": v(31.78, -4.2) * mm});
            skLineSegment(sketch, "E395", {"start": v(31.78, -4.2) * mm, "end": v(31.84, -3.7) * mm});
            skLineSegment(sketch, "E396", {"start": v(31.84, -3.7) * mm, "end": v(31.9, -3.22) * mm});
            skLineSegment(sketch, "E397", {"start": v(31.9, -3.22) * mm, "end": v(31.87, -3.09) * mm});
            skLineSegment(sketch, "E398", {"start": v(31.87, -3.09) * mm, "end": v(31.8, -2.95) * mm});
            skLineSegment(sketch, "E399", {"start": v(31.8, -2.95) * mm, "end": v(31.7, -2.85) * mm});
            skLineSegment(sketch, "E400", {"start": v(31.7, -2.85) * mm, "end": v(31.56, -2.79) * mm});
            skLineSegment(sketch, "E401", {"start": v(31.56, -2.79) * mm, "end": v(30.95, -2.72) * mm});
            skLineSegment(sketch, "E402", {"start": v(30.95, -2.72) * mm, "end": v(30.82, -2.69) * mm});
            skLineSegment(sketch, "E403", {"start": v(30.82, -2.69) * mm, "end": v(30.7, -2.64) * mm});
            skLineSegment(sketch, "E404", {"start": v(30.7, -2.64) * mm, "end": v(30.59, -2.59) * mm});
            skLineSegment(sketch, "E405", {"start": v(30.59, -2.59) * mm, "end": v(30.48, -2.52) * mm});
            skLineSegment(sketch, "E406", {"start": v(30.48, -2.52) * mm, "end": v(30.37, -2.44) * mm});
            skLineSegment(sketch, "E407", {"start": v(30.37, -2.44) * mm, "end": v(30.27, -2.36) * mm});
            skLineSegment(sketch, "E408", {"start": v(30.27, -2.36) * mm, "end": v(30.18, -2.27) * mm});
            skLineSegment(sketch, "E409", {"start": v(30.18, -2.27) * mm, "end": v(30.1, -2.17) * mm});
            skLineSegment(sketch, "E410", {"start": v(30.1, -2.17) * mm, "end": v(30.03, -2.06) * mm});
            skLineSegment(sketch, "E411", {"start": v(30.03, -2.06) * mm, "end": v(29.96, -1.95) * mm});
            skLineSegment(sketch, "E412", {"start": v(29.96, -1.95) * mm, "end": v(29.9, -1.83) * mm});
            skLineSegment(sketch, "E413", {"start": v(29.9, -1.83) * mm, "end": v(29.86, -1.7) * mm});
            skLineSegment(sketch, "E414", {"start": v(29.86, -1.7) * mm, "end": v(29.82, -1.58) * mm});
            skLineSegment(sketch, "E415", {"start": v(29.82, -1.58) * mm, "end": v(29.8, -1.45) * mm});
            skLineSegment(sketch, "E416", {"start": v(29.8, -1.45) * mm, "end": v(29.78, -1.31) * mm});
            skLineSegment(sketch, "E417", {"start": v(29.78, -1.31) * mm, "end": v(29.77, -1.17) * mm});
            skLineSegment(sketch, "E418", {"start": v(29.77, -1.17) * mm, "end": v(29.79, -1.04) * mm});
            skLineSegment(sketch, "E419", {"start": v(29.79, -1.04) * mm, "end": v(29.81, -0.9) * mm});
            skLineSegment(sketch, "E420", {"start": v(29.81, -0.9) * mm, "end": v(29.85, -0.77) * mm});
            skLineSegment(sketch, "E421", {"start": v(29.85, -0.77) * mm, "end": v(29.9, -0.65) * mm});
            skLineSegment(sketch, "E422", {"start": v(29.9, -0.65) * mm, "end": v(29.95, -0.53) * mm});
            skLineSegment(sketch, "E423", {"start": v(29.95, -0.53) * mm, "end": v(30.02, -0.41) * mm});
            skLineSegment(sketch, "E424", {"start": v(30.02, -0.41) * mm, "end": v(30.1, -0.3) * mm});
            skLineSegment(sketch, "E425", {"start": v(30.1, -0.3) * mm, "end": v(30.18, -0.2) * mm});
            skLineSegment(sketch, "E426", {"start": v(30.18, -0.2) * mm, "end": v(30.27, -0.11) * mm});
            skLineSegment(sketch, "E427", {"start": v(30.27, -0.11) * mm, "end": v(30.36, -0.03) * mm});
            skLineSegment(sketch, "E428", {"start": v(30.36, -0.03) * mm, "end": v(30.47, 0.05) * mm});
            skLineSegment(sketch, "E429", {"start": v(30.47, 0.05) * mm, "end": v(30.58, 0.11) * mm});
            skLineSegment(sketch, "E430", {"start": v(30.58, 0.11) * mm, "end": v(30.7, 0.17) * mm});
            skLineSegment(sketch, "E431", {"start": v(30.7, 0.17) * mm, "end": v(30.81, 0.22) * mm});
            skLineSegment(sketch, "E432", {"start": v(30.81, 0.22) * mm, "end": v(30.94, 0.25) * mm});
            skLineSegment(sketch, "E433", {"start": v(30.94, 0.25) * mm, "end": v(31.07, 0.28) * mm});
            skLineSegment(sketch, "E434", {"start": v(31.07, 0.28) * mm, "end": v(31.67, 0.3) * mm});
            skLineSegment(sketch, "E435", {"start": v(31.67, 0.3) * mm, "end": v(31.82, 0.35) * mm});
            skLineSegment(sketch, "E436", {"start": v(31.82, 0.35) * mm, "end": v(31.93, 0.44) * mm});
            skLineSegment(sketch, "E437", {"start": v(31.93, 0.44) * mm, "end": v(32.01, 0.57) * mm});
            skLineSegment(sketch, "E438", {"start": v(32.01, 0.57) * mm, "end": v(32.04, 0.7) * mm});
            skLineSegment(sketch, "E439", {"start": v(32.04, 0.7) * mm, "end": v(32.03, 1.2) * mm});
            skLineSegment(sketch, "E440", {"start": v(32.03, 1.2) * mm, "end": v(32, 1.68) * mm});
            skLineSegment(sketch, "E441", {"start": v(32, 1.68) * mm, "end": v(31.97, 1.81) * mm});
            skLineSegment(sketch, "E442", {"start": v(31.97, 1.81) * mm, "end": v(31.88, 1.94) * mm});
            skLineSegment(sketch, "E443", {"start": v(31.88, 1.94) * mm, "end": v(31.75, 2.02) * mm});
            skLineSegment(sketch, "E444", {"start": v(31.75, 2.02) * mm, "end": v(31.6, 2.06) * mm});
            skLineSegment(sketch, "E445", {"start": v(31.6, 2.06) * mm, "end": v(31, 2.03) * mm});
            skLineSegment(sketch, "E446", {"start": v(31, 2.03) * mm, "end": v(30.87, 2.05) * mm});
            skLineSegment(sketch, "E447", {"start": v(30.87, 2.05) * mm, "end": v(30.74, 2.08) * mm});
            skLineSegment(sketch, "E448", {"start": v(30.74, 2.08) * mm, "end": v(30.62, 2.11) * mm});
            skLineSegment(sketch, "E449", {"start": v(30.62, 2.11) * mm, "end": v(30.5, 2.16) * mm});
            skLineSegment(sketch, "E450", {"start": v(30.5, 2.16) * mm, "end": v(30.38, 2.22) * mm});
            skLineSegment(sketch, "E451", {"start": v(30.38, 2.22) * mm, "end": v(30.27, 2.29) * mm});
            skLineSegment(sketch, "E452", {"start": v(30.27, 2.29) * mm, "end": v(30.17, 2.36) * mm});
            skLineSegment(sketch, "E453", {"start": v(30.17, 2.36) * mm, "end": v(30.07, 2.45) * mm});
            skLineSegment(sketch, "E454", {"start": v(30.07, 2.45) * mm, "end": v(29.98, 2.54) * mm});
            skLineSegment(sketch, "E455", {"start": v(29.98, 2.54) * mm, "end": v(29.9, 2.65) * mm});
            skLineSegment(sketch, "E456", {"start": v(29.9, 2.65) * mm, "end": v(29.83, 2.75) * mm});
            skLineSegment(sketch, "E457", {"start": v(29.83, 2.75) * mm, "end": v(29.76, 2.87) * mm});
            skLineSegment(sketch, "E458", {"start": v(29.76, 2.87) * mm, "end": v(29.7, 2.99) * mm});
            skLineSegment(sketch, "E459", {"start": v(29.7, 2.99) * mm, "end": v(29.66, 3.12) * mm});
            skLineSegment(sketch, "E460", {"start": v(29.66, 3.12) * mm, "end": v(29.62, 3.25) * mm});
            skLineSegment(sketch, "E461", {"start": v(29.62, 3.25) * mm, "end": v(29.6, 3.38) * mm});
            skLineSegment(sketch, "E462", {"start": v(29.6, 3.38) * mm, "end": v(29.6, 3.52) * mm});
            skLineSegment(sketch, "E463", {"start": v(29.6, 3.52) * mm, "end": v(29.6, 3.66) * mm});
            skLineSegment(sketch, "E464", {"start": v(29.6, 3.66) * mm, "end": v(29.61, 3.8) * mm});
            skLineSegment(sketch, "E465", {"start": v(29.61, 3.8) * mm, "end": v(29.64, 3.92) * mm});
            skLineSegment(sketch, "E466", {"start": v(29.64, 3.92) * mm, "end": v(29.68, 4.05) * mm});
            skLineSegment(sketch, "E467", {"start": v(29.68, 4.05) * mm, "end": v(29.73, 4.17) * mm});
            skLineSegment(sketch, "E468", {"start": v(29.73, 4.17) * mm, "end": v(29.78, 4.3) * mm});
            skLineSegment(sketch, "E469", {"start": v(29.78, 4.3) * mm, "end": v(29.85, 4.4) * mm});
            skLineSegment(sketch, "E470", {"start": v(29.85, 4.4) * mm, "end": v(29.92, 4.5) * mm});
            skLineSegment(sketch, "E471", {"start": v(29.92, 4.5) * mm, "end": v(30, 4.6) * mm});
            skLineSegment(sketch, "E472", {"start": v(30, 4.6) * mm, "end": v(30.1, 4.7) * mm});
            skLineSegment(sketch, "E473", {"start": v(30.1, 4.7) * mm, "end": v(30.2, 4.78) * mm});
            skLineSegment(sketch, "E474", {"start": v(30.2, 4.78) * mm, "end": v(30.3, 4.85) * mm});
            skLineSegment(sketch, "E475", {"start": v(30.3, 4.85) * mm, "end": v(30.41, 4.92) * mm});
            skLineSegment(sketch, "E476", {"start": v(30.41, 4.92) * mm, "end": v(30.53, 4.97) * mm});
            skLineSegment(sketch, "E477", {"start": v(30.53, 4.97) * mm, "end": v(30.66, 5.02) * mm});
            skLineSegment(sketch, "E478", {"start": v(30.66, 5.02) * mm, "end": v(31.25, 5.13) * mm});
            skLineSegment(sketch, "E479", {"start": v(31.25, 5.13) * mm, "end": v(31.39, 5.2) * mm});
            skLineSegment(sketch, "E480", {"start": v(31.39, 5.2) * mm, "end": v(31.49, 5.31) * mm});
            skLineSegment(sketch, "E481", {"start": v(31.49, 5.31) * mm, "end": v(31.55, 5.45) * mm});
            skLineSegment(sketch, "E482", {"start": v(31.55, 5.45) * mm, "end": v(31.55, 5.59) * mm});
            skLineSegment(sketch, "E483", {"start": v(31.55, 5.59) * mm, "end": v(31.47, 6.07) * mm});
            skLineSegment(sketch, "E484", {"start": v(31.47, 6.07) * mm, "end": v(31.37, 6.55) * mm});
            skLineSegment(sketch, "E485", {"start": v(31.37, 6.55) * mm, "end": v(31.3, 6.67) * mm});
            skLineSegment(sketch, "E486", {"start": v(31.3, 6.67) * mm, "end": v(31.2, 6.78) * mm});
            skLineSegment(sketch, "E487", {"start": v(31.2, 6.78) * mm, "end": v(31.07, 6.85) * mm});
            skLineSegment(sketch, "E488", {"start": v(31.07, 6.85) * mm, "end": v(30.92, 6.86) * mm});
            skLineSegment(sketch, "E489", {"start": v(30.92, 6.86) * mm, "end": v(30.32, 6.74) * mm});
            skLineSegment(sketch, "E490", {"start": v(30.32, 6.74) * mm, "end": v(30.19, 6.74) * mm});
            skLineSegment(sketch, "E491", {"start": v(30.19, 6.74) * mm, "end": v(30.06, 6.74) * mm});
            skLineSegment(sketch, "E492", {"start": v(30.06, 6.74) * mm, "end": v(29.93, 6.76) * mm});
            skLineSegment(sketch, "E493", {"start": v(29.93, 6.76) * mm, "end": v(29.8, 6.8) * mm});
            skLineSegment(sketch, "E494", {"start": v(29.8, 6.8) * mm, "end": v(29.68, 6.83) * mm});
            skLineSegment(sketch, "E495", {"start": v(29.68, 6.83) * mm, "end": v(29.56, 6.88) * mm});
            skLineSegment(sketch, "E496", {"start": v(29.56, 6.88) * mm, "end": v(29.45, 6.94) * mm});
            skLineSegment(sketch, "E497", {"start": v(29.45, 6.94) * mm, "end": v(29.34, 7.01) * mm});
            skLineSegment(sketch, "E498", {"start": v(29.34, 7.01) * mm, "end": v(29.24, 7.1) * mm});
            skLineSegment(sketch, "E499", {"start": v(29.24, 7.1) * mm, "end": v(29.14, 7.18) * mm});
            skLineSegment(sketch, "E500", {"start": v(29.14, 7.18) * mm, "end": v(29.05, 7.27) * mm});
            skLineSegment(sketch, "E501", {"start": v(29.05, 7.27) * mm, "end": v(28.97, 7.38) * mm});
            skLineSegment(sketch, "E502", {"start": v(28.97, 7.38) * mm, "end": v(28.9, 7.49) * mm});
            skLineSegment(sketch, "E503", {"start": v(28.9, 7.49) * mm, "end": v(28.83, 7.6) * mm});
            skLineSegment(sketch, "E504", {"start": v(28.83, 7.6) * mm, "end": v(28.78, 7.73) * mm});
            skLineSegment(sketch, "E505", {"start": v(28.78, 7.73) * mm, "end": v(28.73, 7.86) * mm});
            skLineSegment(sketch, "E506", {"start": v(28.73, 7.86) * mm, "end": v(28.7, 8) * mm});
            skLineSegment(sketch, "E507", {"start": v(28.7, 8) * mm, "end": v(28.69, 8.13) * mm});
            skLineSegment(sketch, "E508", {"start": v(28.69, 8.13) * mm, "end": v(28.68, 8.27) * mm});
            skLineSegment(sketch, "E509", {"start": v(28.68, 8.27) * mm, "end": v(28.7, 8.4) * mm});
            skLineSegment(sketch, "E510", {"start": v(28.7, 8.4) * mm, "end": v(28.7, 8.53) * mm});
            skLineSegment(sketch, "E511", {"start": v(28.7, 8.53) * mm, "end": v(28.74, 8.66) * mm});
            skLineSegment(sketch, "E512", {"start": v(28.74, 8.66) * mm, "end": v(28.77, 8.79) * mm});
            skLineSegment(sketch, "E513", {"start": v(28.77, 8.79) * mm, "end": v(28.82, 8.9) * mm});
            skLineSegment(sketch, "E514", {"start": v(28.82, 8.9) * mm, "end": v(28.88, 9.02) * mm});
            skLineSegment(sketch, "E515", {"start": v(28.88, 9.02) * mm, "end": v(28.95, 9.13) * mm});
            skLineSegment(sketch, "E516", {"start": v(28.95, 9.13) * mm, "end": v(29.02, 9.24) * mm});
            skLineSegment(sketch, "E517", {"start": v(29.02, 9.24) * mm, "end": v(29.1, 9.33) * mm});
            skLineSegment(sketch, "E518", {"start": v(29.1, 9.33) * mm, "end": v(29.2, 9.42) * mm});
            skLineSegment(sketch, "E519", {"start": v(29.2, 9.42) * mm, "end": v(29.3, 9.5) * mm});
            skLineSegment(sketch, "E520", {"start": v(29.3, 9.5) * mm, "end": v(29.4, 9.58) * mm});
            skLineSegment(sketch, "E521", {"start": v(29.4, 9.58) * mm, "end": v(29.52, 9.64) * mm});
            skLineSegment(sketch, "E522", {"start": v(29.52, 9.64) * mm, "end": v(30.1, 9.84) * mm});
            skLineSegment(sketch, "E523", {"start": v(30.1, 9.84) * mm, "end": v(30.22, 9.93) * mm});
            skLineSegment(sketch, "E524", {"start": v(30.22, 9.93) * mm, "end": v(30.3, 10.06) * mm});
            skLineSegment(sketch, "E525", {"start": v(30.3, 10.06) * mm, "end": v(30.34, 10.2) * mm});
            skLineSegment(sketch, "E526", {"start": v(30.34, 10.2) * mm, "end": v(30.32, 10.34) * mm});
            skLineSegment(sketch, "E527", {"start": v(30.32, 10.34) * mm, "end": v(30.17, 10.8) * mm});
            skLineSegment(sketch, "E528", {"start": v(30.17, 10.8) * mm, "end": v(30, 11.26) * mm});
            skLineSegment(sketch, "E529", {"start": v(30, 11.26) * mm, "end": v(29.92, 11.37) * mm});
            skLineSegment(sketch, "E530", {"start": v(29.92, 11.37) * mm, "end": v(29.8, 11.46) * mm});
            skLineSegment(sketch, "E531", {"start": v(29.8, 11.46) * mm, "end": v(29.65, 11.5) * mm});
            skLineSegment(sketch, "E532", {"start": v(29.65, 11.5) * mm, "end": v(29.5, 11.5) * mm});
            skLineSegment(sketch, "E533", {"start": v(29.5, 11.5) * mm, "end": v(28.93, 11.3) * mm});
            skLineSegment(sketch, "E534", {"start": v(28.93, 11.3) * mm, "end": v(28.8, 11.27) * mm});
            skLineSegment(sketch, "E535", {"start": v(28.8, 11.27) * mm, "end": v(28.67, 11.25) * mm});
            skLineSegment(sketch, "E536", {"start": v(28.67, 11.25) * mm, "end": v(28.54, 11.25) * mm});
            skLineSegment(sketch, "E537", {"start": v(28.54, 11.25) * mm, "end": v(28.41, 11.26) * mm});
            skLineSegment(sketch, "E538", {"start": v(28.41, 11.26) * mm, "end": v(28.29, 11.28) * mm});
            skLineSegment(sketch, "E539", {"start": v(28.29, 11.28) * mm, "end": v(28.16, 11.31) * mm});
            skLineSegment(sketch, "E540", {"start": v(28.16, 11.31) * mm, "end": v(28.04, 11.36) * mm});
            skLineSegment(sketch, "E541", {"start": v(28.04, 11.36) * mm, "end": v(27.92, 11.4) * mm});
            skLineSegment(sketch, "E542", {"start": v(27.92, 11.4) * mm, "end": v(27.8, 11.47) * mm});
            skLineSegment(sketch, "E543", {"start": v(27.8, 11.47) * mm, "end": v(27.7, 11.54) * mm});
            skLineSegment(sketch, "E544", {"start": v(27.7, 11.54) * mm, "end": v(27.6, 11.62) * mm});
            skLineSegment(sketch, "E545", {"start": v(27.6, 11.62) * mm, "end": v(27.5, 11.71) * mm});
            skLineSegment(sketch, "E546", {"start": v(27.5, 11.71) * mm, "end": v(27.41, 11.81) * mm});
            skLineSegment(sketch, "E547", {"start": v(27.41, 11.81) * mm, "end": v(27.33, 11.92) * mm});
            skLineSegment(sketch, "E548", {"start": v(27.33, 11.92) * mm, "end": v(27.25, 12.03) * mm});
            skLineSegment(sketch, "E549", {"start": v(27.25, 12.03) * mm, "end": v(27.19, 12.16) * mm});
            skLineSegment(sketch, "E550", {"start": v(27.19, 12.16) * mm, "end": v(27.14, 12.29) * mm});
            skLineSegment(sketch, "E551", {"start": v(27.14, 12.29) * mm, "end": v(27.1, 12.42) * mm});
            skLineSegment(sketch, "E552", {"start": v(27.1, 12.42) * mm, "end": v(27.08, 12.55) * mm});
            skLineSegment(sketch, "E553", {"start": v(27.08, 12.55) * mm, "end": v(27.07, 12.68) * mm});
            skLineSegment(sketch, "E554", {"start": v(27.07, 12.68) * mm, "end": v(27.06, 12.82) * mm});
            skLineSegment(sketch, "E555", {"start": v(27.06, 12.82) * mm, "end": v(27.07, 12.95) * mm});
            skLineSegment(sketch, "E556", {"start": v(27.07, 12.95) * mm, "end": v(27.1, 13.07) * mm});
            skLineSegment(sketch, "E557", {"start": v(27.1, 13.07) * mm, "end": v(27.12, 13.2) * mm});
            skLineSegment(sketch, "E558", {"start": v(27.12, 13.2) * mm, "end": v(27.16, 13.32) * mm});
            skLineSegment(sketch, "E559", {"start": v(27.16, 13.32) * mm, "end": v(27.2, 13.44) * mm});
            skLineSegment(sketch, "E560", {"start": v(27.2, 13.44) * mm, "end": v(27.27, 13.56) * mm});
            skLineSegment(sketch, "E561", {"start": v(27.27, 13.56) * mm, "end": v(27.34, 13.67) * mm});
            skLineSegment(sketch, "E562", {"start": v(27.34, 13.67) * mm, "end": v(27.41, 13.77) * mm});
            skLineSegment(sketch, "E563", {"start": v(27.41, 13.77) * mm, "end": v(27.5, 13.86) * mm});
            skLineSegment(sketch, "E564", {"start": v(27.5, 13.86) * mm, "end": v(27.6, 13.95) * mm});
            skLineSegment(sketch, "E565", {"start": v(27.6, 13.95) * mm, "end": v(27.7, 14.03) * mm});
            skLineSegment(sketch, "E566", {"start": v(27.7, 14.03) * mm, "end": v(28.24, 14.32) * mm});
            skLineSegment(sketch, "E567", {"start": v(28.24, 14.32) * mm, "end": v(28.35, 14.43) * mm});
            skLineSegment(sketch, "E568", {"start": v(28.35, 14.43) * mm, "end": v(28.4, 14.56) * mm});
            skLineSegment(sketch, "E569", {"start": v(28.4, 14.56) * mm, "end": v(28.42, 14.72) * mm});
            skLineSegment(sketch, "E570", {"start": v(28.42, 14.72) * mm, "end": v(28.39, 14.85) * mm});
            skLineSegment(sketch, "E571", {"start": v(28.39, 14.85) * mm, "end": v(28.16, 15.28) * mm});
            skLineSegment(sketch, "E572", {"start": v(28.16, 15.28) * mm, "end": v(27.92, 15.7) * mm});
            skLineSegment(sketch, "E573", {"start": v(27.92, 15.7) * mm, "end": v(27.83, 15.8) * mm});
            skLineSegment(sketch, "E574", {"start": v(27.83, 15.8) * mm, "end": v(27.7, 15.88) * mm});
            skLineSegment(sketch, "E575", {"start": v(27.7, 15.88) * mm, "end": v(27.54, 15.9) * mm});
            skLineSegment(sketch, "E576", {"start": v(27.54, 15.9) * mm, "end": v(27.4, 15.87) * mm});
            skLineSegment(sketch, "E577", {"start": v(27.4, 15.87) * mm, "end": v(26.86, 15.57) * mm});
            skLineSegment(sketch, "E578", {"start": v(26.86, 15.57) * mm, "end": v(26.74, 15.53) * mm});
            skLineSegment(sketch, "E579", {"start": v(26.74, 15.53) * mm, "end": v(26.61, 15.5) * mm});
            skLineSegment(sketch, "E580", {"start": v(26.61, 15.5) * mm, "end": v(26.49, 15.48) * mm});
            skLineSegment(sketch, "E581", {"start": v(26.49, 15.48) * mm, "end": v(26.36, 15.47) * mm});
            skLineSegment(sketch, "E582", {"start": v(26.36, 15.47) * mm, "end": v(26.23, 15.47) * mm});
            skLineSegment(sketch, "E583", {"start": v(26.23, 15.47) * mm, "end": v(26.1, 15.48) * mm});
            skLineSegment(sketch, "E584", {"start": v(26.1, 15.48) * mm, "end": v(25.97, 15.5) * mm});
            skLineSegment(sketch, "E585", {"start": v(25.97, 15.5) * mm, "end": v(25.85, 15.54) * mm});
            skLineSegment(sketch, "E586", {"start": v(25.85, 15.54) * mm, "end": v(25.73, 15.58) * mm});
            skLineSegment(sketch, "E587", {"start": v(25.73, 15.58) * mm, "end": v(25.6, 15.64) * mm});
            skLineSegment(sketch, "E588", {"start": v(25.6, 15.64) * mm, "end": v(25.5, 15.7) * mm});
            skLineSegment(sketch, "E589", {"start": v(25.5, 15.7) * mm, "end": v(25.39, 15.77) * mm});
            skLineSegment(sketch, "E590", {"start": v(25.39, 15.77) * mm, "end": v(25.28, 15.86) * mm});
            skLineSegment(sketch, "E591", {"start": v(25.28, 15.86) * mm, "end": v(25.18, 15.95) * mm});
            skLineSegment(sketch, "E592", {"start": v(25.18, 15.95) * mm, "end": v(25.1, 16.05) * mm});
            skLineSegment(sketch, "E593", {"start": v(25.1, 16.05) * mm, "end": v(25, 16.16) * mm});
            skLineSegment(sketch, "E594", {"start": v(25, 16.16) * mm, "end": v(24.94, 16.28) * mm});
            skLineSegment(sketch, "E595", {"start": v(24.94, 16.28) * mm, "end": v(24.89, 16.4) * mm});
            skLineSegment(sketch, "E596", {"start": v(24.89, 16.4) * mm, "end": v(24.84, 16.54) * mm});
            skLineSegment(sketch, "E597", {"start": v(24.84, 16.54) * mm, "end": v(24.8, 16.67) * mm});
            skLineSegment(sketch, "E598", {"start": v(24.8, 16.67) * mm, "end": v(24.79, 16.8) * mm});
            skLineSegment(sketch, "E599", {"start": v(24.79, 16.8) * mm, "end": v(24.77, 16.93) * mm});
            skLineSegment(sketch, "E600", {"start": v(24.77, 16.93) * mm, "end": v(24.77, 17.06) * mm});
            skLineSegment(sketch, "E601", {"start": v(24.77, 17.06) * mm, "end": v(24.78, 17.19) * mm});
            skLineSegment(sketch, "E602", {"start": v(24.78, 17.19) * mm, "end": v(24.8, 17.31) * mm});
            skLineSegment(sketch, "E603", {"start": v(24.8, 17.31) * mm, "end": v(24.83, 17.44) * mm});
            skLineSegment(sketch, "E604", {"start": v(24.83, 17.44) * mm, "end": v(24.87, 17.56) * mm});
            skLineSegment(sketch, "E605", {"start": v(24.87, 17.56) * mm, "end": v(24.92, 17.68) * mm});
            skLineSegment(sketch, "E606", {"start": v(24.92, 17.68) * mm, "end": v(24.99, 17.8) * mm});
            skLineSegment(sketch, "E607", {"start": v(24.99, 17.8) * mm, "end": v(25.06, 17.9) * mm});
            skLineSegment(sketch, "E608", {"start": v(25.06, 17.9) * mm, "end": v(25.14, 18) * mm});
            skLineSegment(sketch, "E609", {"start": v(25.14, 18) * mm, "end": v(25.23, 18.1) * mm});
            skLineSegment(sketch, "E610", {"start": v(25.23, 18.1) * mm, "end": v(25.72, 18.46) * mm});
            skLineSegment(sketch, "E611", {"start": v(25.72, 18.46) * mm, "end": v(25.8, 18.58) * mm});
            skLineSegment(sketch, "E612", {"start": v(25.8, 18.58) * mm, "end": v(25.85, 18.73) * mm});
            skLineSegment(sketch, "E613", {"start": v(25.85, 18.73) * mm, "end": v(25.84, 18.88) * mm});
            skLineSegment(sketch, "E614", {"start": v(25.84, 18.88) * mm, "end": v(25.78, 19) * mm});
            skLineSegment(sketch, "E615", {"start": v(25.78, 19) * mm, "end": v(25.5, 19.4) * mm});
            skLineSegment(sketch, "E616", {"start": v(25.5, 19.4) * mm, "end": v(25.19, 19.78) * mm});
            skLineSegment(sketch, "E617", {"start": v(25.19, 19.78) * mm, "end": v(25.08, 19.87) * mm});
            skLineSegment(sketch, "E618", {"start": v(25.08, 19.87) * mm, "end": v(24.94, 19.92) * mm});
            skLineSegment(sketch, "E619", {"start": v(24.94, 19.92) * mm, "end": v(24.79, 19.92) * mm});
            skLineSegment(sketch, "E620", {"start": v(24.79, 19.92) * mm, "end": v(24.65, 19.86) * mm});
            skLineSegment(sketch, "E621", {"start": v(24.65, 19.86) * mm, "end": v(24.17, 19.5) * mm});
            skLineSegment(sketch, "E622", {"start": v(24.17, 19.5) * mm, "end": v(24.05, 19.43) * mm});
            skLineSegment(sketch, "E623", {"start": v(24.05, 19.43) * mm, "end": v(23.93, 19.38) * mm});
            skLineSegment(sketch, "E624", {"start": v(23.93, 19.38) * mm, "end": v(23.8, 19.34) * mm});
            skLineSegment(sketch, "E625", {"start": v(23.8, 19.34) * mm, "end": v(23.68, 19.3) * mm});
            skLineSegment(sketch, "E626", {"start": v(23.68, 19.3) * mm, "end": v(23.56, 19.29) * mm});
            skLineSegment(sketch, "E627", {"start": v(23.56, 19.29) * mm, "end": v(23.43, 19.28) * mm});
            skLineSegment(sketch, "E628", {"start": v(23.43, 19.28) * mm, "end": v(23.3, 19.29) * mm});
            skLineSegment(sketch, "E629", {"start": v(23.3, 19.29) * mm, "end": v(23.17, 19.3) * mm});
            skLineSegment(sketch, "E630", {"start": v(23.17, 19.3) * mm, "end": v(23.04, 19.33) * mm});
            skLineSegment(sketch, "E631", {"start": v(23.04, 19.33) * mm, "end": v(22.92, 19.36) * mm});
            skLineSegment(sketch, "E632", {"start": v(22.92, 19.36) * mm, "end": v(22.8, 19.4) * mm});
            skLineSegment(sketch, "E633", {"start": v(22.8, 19.4) * mm, "end": v(22.68, 19.46) * mm});
            skLineSegment(sketch, "E634", {"start": v(22.68, 19.46) * mm, "end": v(22.56, 19.53) * mm});
            skLineSegment(sketch, "E635", {"start": v(22.56, 19.53) * mm, "end": v(22.45, 19.6) * mm});
            skLineSegment(sketch, "E636", {"start": v(22.45, 19.6) * mm, "end": v(22.34, 19.7) * mm});
            skLineSegment(sketch, "E637", {"start": v(22.34, 19.7) * mm, "end": v(22.24, 19.8) * mm});
            skLineSegment(sketch, "E638", {"start": v(22.24, 19.8) * mm, "end": v(22.16, 19.9) * mm});
            skLineSegment(sketch, "E639", {"start": v(22.16, 19.9) * mm, "end": v(22.08, 20.01) * mm});
            skLineSegment(sketch, "E640", {"start": v(22.08, 20.01) * mm, "end": v(22.02, 20.13) * mm});
            skLineSegment(sketch, "E641", {"start": v(22.02, 20.13) * mm, "end": v(21.97, 20.26) * mm});
            skLineSegment(sketch, "E642", {"start": v(21.97, 20.26) * mm, "end": v(21.93, 20.38) * mm});
            skLineSegment(sketch, "E643", {"start": v(21.93, 20.38) * mm, "end": v(21.9, 20.5) * mm});
            skLineSegment(sketch, "E644", {"start": v(21.9, 20.5) * mm, "end": v(21.87, 20.64) * mm});
            skLineSegment(sketch, "E645", {"start": v(21.87, 20.64) * mm, "end": v(21.86, 20.77) * mm});
            skLineSegment(sketch, "E646", {"start": v(21.86, 20.77) * mm, "end": v(21.86, 20.9) * mm});
            skLineSegment(sketch, "E647", {"start": v(21.86, 20.9) * mm, "end": v(21.87, 21.02) * mm});
            skLineSegment(sketch, "E648", {"start": v(21.87, 21.02) * mm, "end": v(21.9, 21.15) * mm});
            skLineSegment(sketch, "E649", {"start": v(21.9, 21.15) * mm, "end": v(21.93, 21.28) * mm});
            skLineSegment(sketch, "E650", {"start": v(21.93, 21.28) * mm, "end": v(21.97, 21.4) * mm});
            skLineSegment(sketch, "E651", {"start": v(21.97, 21.4) * mm, "end": v(22.03, 21.51) * mm});
            skLineSegment(sketch, "E652", {"start": v(22.03, 21.51) * mm, "end": v(22.1, 21.63) * mm});
            skLineSegment(sketch, "E653", {"start": v(22.1, 21.63) * mm, "end": v(22.17, 21.74) * mm});
            skLineSegment(sketch, "E654", {"start": v(22.17, 21.74) * mm, "end": v(22.6, 22.17) * mm});
            skLineSegment(sketch, "E655", {"start": v(22.6, 22.17) * mm, "end": v(22.66, 22.3) * mm});
            skLineSegment(sketch, "E656", {"start": v(22.66, 22.3) * mm, "end": v(22.68, 22.45) * mm});
            skLineSegment(sketch, "E657", {"start": v(22.68, 22.45) * mm, "end": v(22.65, 22.6) * mm});
            skLineSegment(sketch, "E658", {"start": v(22.65, 22.6) * mm, "end": v(22.57, 22.72) * mm});
            skLineSegment(sketch, "E659", {"start": v(22.57, 22.72) * mm, "end": v(22.23, 23.06) * mm});
            skLineSegment(sketch, "E660", {"start": v(22.23, 23.06) * mm, "end": v(21.87, 23.4) * mm});
            skLineSegment(sketch, "E661", {"start": v(21.87, 23.4) * mm, "end": v(21.75, 23.46) * mm});
            skLineSegment(sketch, "E662", {"start": v(21.75, 23.46) * mm, "end": v(21.6, 23.5) * mm});
            skLineSegment(sketch, "E663", {"start": v(21.6, 23.5) * mm, "end": v(21.45, 23.47) * mm});
            skLineSegment(sketch, "E664", {"start": v(21.45, 23.47) * mm, "end": v(21.32, 23.4) * mm});
            skLineSegment(sketch, "E665", {"start": v(21.32, 23.4) * mm, "end": v(20.9, 22.95) * mm});
            skLineSegment(sketch, "E666", {"start": v(20.9, 22.95) * mm, "end": v(20.8, 22.87) * mm});
            skLineSegment(sketch, "E667", {"start": v(20.8, 22.87) * mm, "end": v(20.69, 22.8) * mm});
            skLineSegment(sketch, "E668", {"start": v(20.69, 22.8) * mm, "end": v(20.57, 22.74) * mm});
            skLineSegment(sketch, "E669", {"start": v(20.57, 22.74) * mm, "end": v(20.45, 22.7) * mm});
            skLineSegment(sketch, "E670", {"start": v(20.45, 22.7) * mm, "end": v(20.33, 22.66) * mm});
            skLineSegment(sketch, "E671", {"start": v(20.33, 22.66) * mm, "end": v(20.2, 22.63) * mm});
            skLineSegment(sketch, "E672", {"start": v(20.2, 22.63) * mm, "end": v(20.08, 22.62) * mm});
            skLineSegment(sketch, "E673", {"start": v(20.08, 22.62) * mm, "end": v(19.95, 22.61) * mm});
            skLineSegment(sketch, "E674", {"start": v(19.95, 22.61) * mm, "end": v(19.82, 22.62) * mm});
            skLineSegment(sketch, "E675", {"start": v(19.82, 22.62) * mm, "end": v(19.69, 22.63) * mm});
            skLineSegment(sketch, "E676", {"start": v(19.69, 22.63) * mm, "end": v(19.56, 22.66) * mm});
            skLineSegment(sketch, "E677", {"start": v(19.56, 22.66) * mm, "end": v(19.43, 22.7) * mm});
            skLineSegment(sketch, "E678", {"start": v(19.43, 22.7) * mm, "end": v(19.3, 22.74) * mm});
            skLineSegment(sketch, "E679", {"start": v(19.3, 22.74) * mm, "end": v(19.19, 22.8) * mm});
            skLineSegment(sketch, "E680", {"start": v(19.19, 22.8) * mm, "end": v(19.07, 22.87) * mm});
            skLineSegment(sketch, "E681", {"start": v(19.07, 22.87) * mm, "end": v(18.96, 22.95) * mm});
            skLineSegment(sketch, "E682", {"start": v(18.96, 22.95) * mm, "end": v(18.86, 23.05) * mm});
            skLineSegment(sketch, "E683", {"start": v(18.86, 23.05) * mm, "end": v(18.77, 23.15) * mm});
            skLineSegment(sketch, "E684", {"start": v(18.77, 23.15) * mm, "end": v(18.68, 23.26) * mm});
            skLineSegment(sketch, "E685", {"start": v(18.68, 23.26) * mm, "end": v(18.61, 23.37) * mm});
            skLineSegment(sketch, "E686", {"start": v(18.61, 23.37) * mm, "end": v(18.55, 23.49) * mm});
            skLineSegment(sketch, "E687", {"start": v(18.55, 23.49) * mm, "end": v(18.5, 23.61) * mm});
            skLineSegment(sketch, "E688", {"start": v(18.5, 23.61) * mm, "end": v(18.46, 23.73) * mm});
            skLineSegment(sketch, "E689", {"start": v(18.46, 23.73) * mm, "end": v(18.43, 23.86) * mm});
            skLineSegment(sketch, "E690", {"start": v(18.43, 23.86) * mm, "end": v(18.41, 23.99) * mm});
            skLineSegment(sketch, "E691", {"start": v(18.41, 23.99) * mm, "end": v(18.4, 24.12) * mm});
            skLineSegment(sketch, "E692", {"start": v(18.4, 24.12) * mm, "end": v(18.4, 24.24) * mm});
            skLineSegment(sketch, "E693", {"start": v(18.4, 24.24) * mm, "end": v(18.42, 24.37) * mm});
            skLineSegment(sketch, "E694", {"start": v(18.42, 24.37) * mm, "end": v(18.44, 24.5) * mm});
            skLineSegment(sketch, "E695", {"start": v(18.44, 24.5) * mm, "end": v(18.48, 24.62) * mm});
            skLineSegment(sketch, "E696", {"start": v(18.48, 24.62) * mm, "end": v(18.53, 24.75) * mm});
            skLineSegment(sketch, "E697", {"start": v(18.53, 24.75) * mm, "end": v(18.58, 24.86) * mm});
            skLineSegment(sketch, "E698", {"start": v(18.58, 24.86) * mm, "end": v(18.94, 25.36) * mm});
            skLineSegment(sketch, "E699", {"start": v(18.94, 25.36) * mm, "end": v(18.99, 25.5) * mm});
            skLineSegment(sketch, "E700", {"start": v(18.99, 25.5) * mm, "end": v(18.98, 25.65) * mm});
            skLineSegment(sketch, "E701", {"start": v(18.98, 25.65) * mm, "end": v(18.92, 25.8) * mm});
            skLineSegment(sketch, "E702", {"start": v(18.92, 25.8) * mm, "end": v(18.84, 25.9) * mm});
            skLineSegment(sketch, "E703", {"start": v(18.84, 25.9) * mm, "end": v(18.44, 26.19) * mm});
            skLineSegment(sketch, "E704", {"start": v(18.44, 26.19) * mm, "end": v(18.04, 26.46) * mm});
            skLineSegment(sketch, "E705", {"start": v(18.04, 26.46) * mm, "end": v(17.91, 26.5) * mm});
            skLineSegment(sketch, "E706", {"start": v(17.91, 26.5) * mm, "end": v(17.76, 26.51) * mm});
            skLineSegment(sketch, "E707", {"start": v(17.76, 26.51) * mm, "end": v(17.61, 26.47) * mm});
            skLineSegment(sketch, "E708", {"start": v(17.61, 26.47) * mm, "end": v(17.5, 26.37) * mm});
            skLineSegment(sketch, "E709", {"start": v(17.5, 26.37) * mm, "end": v(17.15, 25.87) * mm});
            skLineSegment(sketch, "E710", {"start": v(17.15, 25.87) * mm, "end": v(17.06, 25.78) * mm});
            skLineSegment(sketch, "E711", {"start": v(17.06, 25.78) * mm, "end": v(16.96, 25.7) * mm});
            skLineSegment(sketch, "E712", {"start": v(16.96, 25.7) * mm, "end": v(16.85, 25.62) * mm});
            skLineSegment(sketch, "E713", {"start": v(16.85, 25.62) * mm, "end": v(16.74, 25.55) * mm});
            skLineSegment(sketch, "E714", {"start": v(16.74, 25.55) * mm, "end": v(16.63, 25.5) * mm});
            skLineSegment(sketch, "E715", {"start": v(16.63, 25.5) * mm, "end": v(16.5, 25.45) * mm});
            skLineSegment(sketch, "E716", {"start": v(16.5, 25.45) * mm, "end": v(16.38, 25.42) * mm});
            skLineSegment(sketch, "E717", {"start": v(16.38, 25.42) * mm, "end": v(16.26, 25.4) * mm});
            skLineSegment(sketch, "E718", {"start": v(16.26, 25.4) * mm, "end": v(16.13, 25.38) * mm});
            skLineSegment(sketch, "E719", {"start": v(16.13, 25.38) * mm, "end": v(16, 25.37) * mm});
            skLineSegment(sketch, "E720", {"start": v(16, 25.37) * mm, "end": v(15.87, 25.38) * mm});
            skLineSegment(sketch, "E721", {"start": v(15.87, 25.38) * mm, "end": v(15.74, 25.4) * mm});
            skLineSegment(sketch, "E722", {"start": v(15.74, 25.4) * mm, "end": v(15.6, 25.43) * mm});
            skLineSegment(sketch, "E723", {"start": v(15.6, 25.43) * mm, "end": v(15.48, 25.46) * mm});
            skLineSegment(sketch, "E724", {"start": v(15.48, 25.46) * mm, "end": v(15.35, 25.52) * mm});
            skLineSegment(sketch, "E725", {"start": v(15.35, 25.52) * mm, "end": v(15.23, 25.58) * mm});
            skLineSegment(sketch, "E726", {"start": v(15.23, 25.58) * mm, "end": v(15.11, 25.66) * mm});
            skLineSegment(sketch, "E727", {"start": v(15.11, 25.66) * mm, "end": v(15, 25.74) * mm});
            skLineSegment(sketch, "E728", {"start": v(15, 25.74) * mm, "end": v(14.91, 25.84) * mm});
            skLineSegment(sketch, "E729", {"start": v(14.91, 25.84) * mm, "end": v(14.82, 25.94) * mm});
            skLineSegment(sketch, "E730", {"start": v(14.82, 25.94) * mm, "end": v(14.74, 26.05) * mm});
            skLineSegment(sketch, "E731", {"start": v(14.74, 26.05) * mm, "end": v(14.68, 26.16) * mm});
            skLineSegment(sketch, "E732", {"start": v(14.68, 26.16) * mm, "end": v(14.62, 26.27) * mm});
            skLineSegment(sketch, "E733", {"start": v(14.62, 26.27) * mm, "end": v(14.57, 26.4) * mm});
            skLineSegment(sketch, "E734", {"start": v(14.57, 26.4) * mm, "end": v(14.53, 26.52) * mm});
            skLineSegment(sketch, "E735", {"start": v(14.53, 26.52) * mm, "end": v(14.5, 26.64) * mm});
            skLineSegment(sketch, "E736", {"start": v(14.5, 26.64) * mm, "end": v(14.48, 26.77) * mm});
            skLineSegment(sketch, "E737", {"start": v(14.48, 26.77) * mm, "end": v(14.48, 26.9) * mm});
            skLineSegment(sketch, "E738", {"start": v(14.48, 26.9) * mm, "end": v(14.48, 27.03) * mm});
            skLineSegment(sketch, "E739", {"start": v(14.48, 27.03) * mm, "end": v(14.5, 27.16) * mm});
            skLineSegment(sketch, "E740", {"start": v(14.5, 27.16) * mm, "end": v(14.53, 27.28) * mm});
            skLineSegment(sketch, "E741", {"start": v(14.53, 27.28) * mm, "end": v(14.57, 27.4) * mm});
            skLineSegment(sketch, "E742", {"start": v(14.57, 27.4) * mm, "end": v(14.84, 27.95) * mm});
            skLineSegment(sketch, "E743", {"start": v(14.84, 27.95) * mm, "end": v(14.87, 28.1) * mm});
            skLineSegment(sketch, "E744", {"start": v(14.87, 28.1) * mm, "end": v(14.84, 28.25) * mm});
            skLineSegment(sketch, "E745", {"start": v(14.84, 28.25) * mm, "end": v(14.76, 28.38) * mm});
            skLineSegment(sketch, "E746", {"start": v(14.76, 28.38) * mm, "end": v(14.66, 28.47) * mm});
            skLineSegment(sketch, "E747", {"start": v(14.66, 28.47) * mm, "end": v(14.22, 28.7) * mm});
            skLineSegment(sketch, "E748", {"start": v(14.22, 28.7) * mm, "end": v(13.78, 28.9) * mm});
            skLineSegment(sketch, "E749", {"start": v(13.78, 28.9) * mm, "end": v(13.65, 28.93) * mm});
            skLineSegment(sketch, "E750", {"start": v(13.65, 28.93) * mm, "end": v(13.5, 28.91) * mm});
            skLineSegment(sketch, "E751", {"start": v(13.5, 28.91) * mm, "end": v(13.36, 28.85) * mm});
            skLineSegment(sketch, "E752", {"start": v(13.36, 28.85) * mm, "end": v(13.26, 28.73) * mm});
            skLineSegment(sketch, "E753", {"start": v(13.26, 28.73) * mm, "end": v(13, 28.19) * mm});
            skLineSegment(sketch, "E754", {"start": v(13, 28.19) * mm, "end": v(12.92, 28.08) * mm});
            skLineSegment(sketch, "E755", {"start": v(12.92, 28.08) * mm, "end": v(12.83, 27.98) * mm});
            skLineSegment(sketch, "E756", {"start": v(12.83, 27.98) * mm, "end": v(12.74, 27.89) * mm});
            skLineSegment(sketch, "E757", {"start": v(12.74, 27.89) * mm, "end": v(12.64, 27.8) * mm});
            skLineSegment(sketch, "E758", {"start": v(12.64, 27.8) * mm, "end": v(12.54, 27.73) * mm});
            skLineSegment(sketch, "E759", {"start": v(12.54, 27.73) * mm, "end": v(12.42, 27.67) * mm});
            skLineSegment(sketch, "E760", {"start": v(12.42, 27.67) * mm, "end": v(12.3, 27.62) * mm});
            skLineSegment(sketch, "E761", {"start": v(12.3, 27.62) * mm, "end": v(12.19, 27.57) * mm});
            skLineSegment(sketch, "E762", {"start": v(12.19, 27.57) * mm, "end": v(12.06, 27.54) * mm});
            skLineSegment(sketch, "E763", {"start": v(12.06, 27.54) * mm, "end": v(11.93, 27.52) * mm});
            skLineSegment(sketch, "E764", {"start": v(11.93, 27.52) * mm, "end": v(11.8, 27.5) * mm});
            skLineSegment(sketch, "E765", {"start": v(11.8, 27.5) * mm, "end": v(11.67, 27.5) * mm});
            skLineSegment(sketch, "E766", {"start": v(11.67, 27.5) * mm, "end": v(11.54, 27.5) * mm});
            skLineSegment(sketch, "E767", {"start": v(11.54, 27.5) * mm, "end": v(11.4, 27.53) * mm});
            skLineSegment(sketch, "E768", {"start": v(11.4, 27.53) * mm, "end": v(11.27, 27.56) * mm});
            skLineSegment(sketch, "E769", {"start": v(11.27, 27.56) * mm, "end": v(11.14, 27.6) * mm});
            skLineSegment(sketch, "E770", {"start": v(11.14, 27.6) * mm, "end": v(11.01, 27.66) * mm});
            skLineSegment(sketch, "E771", {"start": v(11.01, 27.66) * mm, "end": v(10.9, 27.73) * mm});
            skLineSegment(sketch, "E772", {"start": v(10.9, 27.73) * mm, "end": v(10.79, 27.81) * mm});
            skLineSegment(sketch, "E773", {"start": v(10.79, 27.81) * mm, "end": v(10.68, 27.9) * mm});
            skLineSegment(sketch, "E774", {"start": v(10.68, 27.9) * mm, "end": v(10.6, 28) * mm});
            skLineSegment(sketch, "E775", {"start": v(10.6, 28) * mm, "end": v(10.5, 28.1) * mm});
            skLineSegment(sketch, "E776", {"start": v(10.5, 28.1) * mm, "end": v(10.43, 28.2) * mm});
            skLineSegment(sketch, "E777", {"start": v(10.43, 28.2) * mm, "end": v(10.36, 28.3) * mm});
            skLineSegment(sketch, "E778", {"start": v(10.36, 28.3) * mm, "end": v(10.3, 28.42) * mm});
            skLineSegment(sketch, "E779", {"start": v(10.3, 28.42) * mm, "end": v(10.26, 28.54) * mm});
            skLineSegment(sketch, "E780", {"start": v(10.26, 28.54) * mm, "end": v(10.22, 28.67) * mm});
            skLineSegment(sketch, "E781", {"start": v(10.22, 28.67) * mm, "end": v(10.2, 28.8) * mm});
            skLineSegment(sketch, "E782", {"start": v(10.2, 28.8) * mm, "end": v(10.18, 28.92) * mm});
            skLineSegment(sketch, "E783", {"start": v(10.18, 28.92) * mm, "end": v(10.18, 29.05) * mm});
            skLineSegment(sketch, "E784", {"start": v(10.18, 29.05) * mm, "end": v(10.19, 29.18) * mm});
            skLineSegment(sketch, "E785", {"start": v(10.19, 29.18) * mm, "end": v(10.2, 29.31) * mm});
            skLineSegment(sketch, "E786", {"start": v(10.2, 29.31) * mm, "end": v(10.4, 29.89) * mm});
            skLineSegment(sketch, "E787", {"start": v(10.4, 29.89) * mm, "end": v(10.4, 30.04) * mm});
            skLineSegment(sketch, "E788", {"start": v(10.4, 30.04) * mm, "end": v(10.35, 30.18) * mm});
            skLineSegment(sketch, "E789", {"start": v(10.35, 30.18) * mm, "end": v(10.25, 30.3) * mm});
            skLineSegment(sketch, "E790", {"start": v(10.25, 30.3) * mm, "end": v(10.13, 30.37) * mm});
            skLineSegment(sketch, "E791", {"start": v(10.13, 30.37) * mm, "end": v(9.67, 30.53) * mm});
            skLineSegment(sketch, "E792", {"start": v(9.67, 30.53) * mm, "end": v(9.2, 30.67) * mm});
            skLineSegment(sketch, "E793", {"start": v(9.2, 30.67) * mm, "end": v(9.07, 30.68) * mm});
            skLineSegment(sketch, "E794", {"start": v(9.07, 30.68) * mm, "end": v(8.92, 30.63) * mm});
            skLineSegment(sketch, "E795", {"start": v(8.92, 30.63) * mm, "end": v(8.8, 30.55) * mm});
            skLineSegment(sketch, "E796", {"start": v(8.8, 30.55) * mm, "end": v(8.71, 30.42) * mm});
            skLineSegment(sketch, "E797", {"start": v(8.71, 30.42) * mm, "end": v(8.53, 29.84) * mm});
            skLineSegment(sketch, "E798", {"start": v(8.53, 29.84) * mm, "end": v(8.48, 29.72) * mm});
            skLineSegment(sketch, "E799", {"start": v(8.48, 29.72) * mm, "end": v(8.4, 29.61) * mm});
            skLineSegment(sketch, "E800", {"start": v(8.4, 29.61) * mm, "end": v(8.33, 29.5) * mm});
            skLineSegment(sketch, "E801", {"start": v(8.33, 29.5) * mm, "end": v(8.24, 29.41) * mm});
            skLineSegment(sketch, "E802", {"start": v(8.24, 29.41) * mm, "end": v(8.15, 29.32) * mm});
            skLineSegment(sketch, "E803", {"start": v(8.15, 29.32) * mm, "end": v(8.05, 29.24) * mm});
            skLineSegment(sketch, "E804", {"start": v(8.05, 29.24) * mm, "end": v(7.94, 29.17) * mm});
            skLineSegment(sketch, "E805", {"start": v(7.94, 29.17) * mm, "end": v(7.83, 29.11) * mm});
            skLineSegment(sketch, "E806", {"start": v(7.83, 29.11) * mm, "end": v(7.71, 29.06) * mm});
            skLineSegment(sketch, "E807", {"start": v(7.71, 29.06) * mm, "end": v(7.59, 29.02) * mm});
            skLineSegment(sketch, "E808", {"start": v(7.59, 29.02) * mm, "end": v(7.46, 28.98) * mm});
            skLineSegment(sketch, "E809", {"start": v(7.46, 28.98) * mm, "end": v(7.33, 28.96) * mm});
            skLineSegment(sketch, "E810", {"start": v(7.33, 28.96) * mm, "end": v(7.2, 28.95) * mm});
            skLineSegment(sketch, "E811", {"start": v(7.2, 28.95) * mm, "end": v(7.06, 28.95) * mm});
            skLineSegment(sketch, "E812", {"start": v(7.06, 28.95) * mm, "end": v(6.93, 28.96) * mm});
            skLineSegment(sketch, "E813", {"start": v(6.93, 28.96) * mm, "end": v(6.79, 28.98) * mm});
            skLineSegment(sketch, "E814", {"start": v(6.79, 28.98) * mm, "end": v(6.66, 29.02) * mm});
            skLineSegment(sketch, "E815", {"start": v(6.66, 29.02) * mm, "end": v(6.53, 29.07) * mm});
            skLineSegment(sketch, "E816", {"start": v(6.53, 29.07) * mm, "end": v(6.4, 29.13) * mm});
            skLineSegment(sketch, "E817", {"start": v(6.4, 29.13) * mm, "end": v(6.3, 29.2) * mm});
            skLineSegment(sketch, "E818", {"start": v(6.3, 29.2) * mm, "end": v(6.19, 29.28) * mm});
            skLineSegment(sketch, "E819", {"start": v(6.19, 29.28) * mm, "end": v(6.09, 29.37) * mm});
            skLineSegment(sketch, "E820", {"start": v(6.09, 29.37) * mm, "end": v(6, 29.46) * mm});
            skLineSegment(sketch, "E821", {"start": v(6, 29.46) * mm, "end": v(5.92, 29.56) * mm});
            skLineSegment(sketch, "E822", {"start": v(5.92, 29.56) * mm, "end": v(5.84, 29.66) * mm});
            skLineSegment(sketch, "E823", {"start": v(5.84, 29.66) * mm, "end": v(5.78, 29.77) * mm});
            skLineSegment(sketch, "E824", {"start": v(5.78, 29.77) * mm, "end": v(5.72, 29.9) * mm});
            skLineSegment(sketch, "E825", {"start": v(5.72, 29.9) * mm, "end": v(5.68, 30.01) * mm});
            skLineSegment(sketch, "E826", {"start": v(5.68, 30.01) * mm, "end": v(5.64, 30.14) * mm});
            skLineSegment(sketch, "E827", {"start": v(5.64, 30.14) * mm, "end": v(5.62, 30.26) * mm});
            skLineSegment(sketch, "E828", {"start": v(5.62, 30.26) * mm, "end": v(5.6, 30.4) * mm});
            skLineSegment(sketch, "E829", {"start": v(5.6, 30.4) * mm, "end": v(5.6, 30.53) * mm});
            skLineSegment(sketch, "E830", {"start": v(5.6, 30.53) * mm, "end": v(5.7, 31.12) * mm});
            skLineSegment(sketch, "E831", {"start": v(5.7, 31.12) * mm, "end": v(5.68, 31.28) * mm});
            skLineSegment(sketch, "E832", {"start": v(5.68, 31.28) * mm, "end": v(5.61, 31.4) * mm});
            skLineSegment(sketch, "E833", {"start": v(5.61, 31.4) * mm, "end": v(5.5, 31.51) * mm});
            skLineSegment(sketch, "E834", {"start": v(5.5, 31.51) * mm, "end": v(5.37, 31.56) * mm});
            skLineSegment(sketch, "E835", {"start": v(5.37, 31.56) * mm, "end": v(4.9, 31.65) * mm});
            skLineSegment(sketch, "E836", {"start": v(4.9, 31.65) * mm, "end": v(4.4, 31.71) * mm});
            skLineSegment(sketch, "E837", {"start": v(4.4, 31.71) * mm, "end": v(4.27, 31.7) * mm});
            skLineSegment(sketch, "E838", {"start": v(4.27, 31.7) * mm, "end": v(4.14, 31.64) * mm});
            skLineSegment(sketch, "E839", {"start": v(4.14, 31.64) * mm, "end": v(4.03, 31.53) * mm});
            skLineSegment(sketch, "E840", {"start": v(4.03, 31.53) * mm, "end": v(3.96, 31.4) * mm});
            skLineSegment(sketch, "E841", {"start": v(3.96, 31.4) * mm, "end": v(3.87, 30.8) * mm});
            skLineSegment(sketch, "E842", {"start": v(3.87, 30.8) * mm, "end": v(3.83, 30.67) * mm});
            skLineSegment(sketch, "E843", {"start": v(3.83, 30.67) * mm, "end": v(3.78, 30.55) * mm});
            skLineSegment(sketch, "E844", {"start": v(3.78, 30.55) * mm, "end": v(3.72, 30.43) * mm});
            skLineSegment(sketch, "E845", {"start": v(3.72, 30.43) * mm, "end": v(3.65, 30.32) * mm});
            skLineSegment(sketch, "E846", {"start": v(3.65, 30.32) * mm, "end": v(3.57, 30.22) * mm});
            skLineSegment(sketch, "E847", {"start": v(3.57, 30.22) * mm, "end": v(3.49, 30.13) * mm});
            skLineSegment(sketch, "E848", {"start": v(3.49, 30.13) * mm, "end": v(3.4, 30.04) * mm});
            skLineSegment(sketch, "E849", {"start": v(3.4, 30.04) * mm, "end": v(3.29, 29.96) * mm});
            skLineSegment(sketch, "E850", {"start": v(3.29, 29.96) * mm, "end": v(3.18, 29.9) * mm});
            skLineSegment(sketch, "E851", {"start": v(3.18, 29.9) * mm, "end": v(3.06, 29.83) * mm});
            skLineSegment(sketch, "E852", {"start": v(3.06, 29.83) * mm, "end": v(2.94, 29.78) * mm});
            skLineSegment(sketch, "E853", {"start": v(2.94, 29.78) * mm, "end": v(2.82, 29.74) * mm});
            skLineSegment(sketch, "E854", {"start": v(2.82, 29.74) * mm, "end": v(2.69, 29.7) * mm});
            skLineSegment(sketch, "E855", {"start": v(2.69, 29.7) * mm, "end": v(2.56, 29.68) * mm});
            skLineSegment(sketch, "E856", {"start": v(2.56, 29.68) * mm, "end": v(2.42, 29.67) * mm});
            skLineSegment(sketch, "E857", {"start": v(2.42, 29.67) * mm, "end": v(2.28, 29.67) * mm});
            skLineSegment(sketch, "E858", {"start": v(2.28, 29.67) * mm, "end": v(2.14, 29.7) * mm});
            skLineSegment(sketch, "E859", {"start": v(2.14, 29.7) * mm, "end": v(2.01, 29.73) * mm});
            skLineSegment(sketch, "E860", {"start": v(2.01, 29.73) * mm, "end": v(1.88, 29.77) * mm});
            skLineSegment(sketch, "E861", {"start": v(1.88, 29.77) * mm, "end": v(1.76, 29.82) * mm});
            skLineSegment(sketch, "E862", {"start": v(1.76, 29.82) * mm, "end": v(1.64, 29.88) * mm});
            skLineSegment(sketch, "E863", {"start": v(1.64, 29.88) * mm, "end": v(1.53, 29.95) * mm});
            skLineSegment(sketch, "E864", {"start": v(1.53, 29.95) * mm, "end": v(1.43, 30.03) * mm});
            skLineSegment(sketch, "E865", {"start": v(1.43, 30.03) * mm, "end": v(1.33, 30.11) * mm});
            skLineSegment(sketch, "E866", {"start": v(1.33, 30.11) * mm, "end": v(1.24, 30.2) * mm});
            skLineSegment(sketch, "E867", {"start": v(1.24, 30.2) * mm, "end": v(1.16, 30.3) * mm});
            skLineSegment(sketch, "E868", {"start": v(1.16, 30.3) * mm, "end": v(1.09, 30.41) * mm});
            skLineSegment(sketch, "E869", {"start": v(1.09, 30.41) * mm, "end": v(1.02, 30.53) * mm});
            skLineSegment(sketch, "E870", {"start": v(1.02, 30.53) * mm, "end": v(0.97, 30.64) * mm});
            skLineSegment(sketch, "E871", {"start": v(0.97, 30.64) * mm, "end": v(0.93, 30.77) * mm});
            skLineSegment(sketch, "E872", {"start": v(0.93, 30.77) * mm, "end": v(0.9, 30.9) * mm});
            skLineSegment(sketch, "E873", {"start": v(0.9, 30.9) * mm, "end": v(0.88, 31.02) * mm});
            skLineSegment(sketch, "E874", {"start": v(0.88, 31.02) * mm, "end": v(0.88, 31.63) * mm});
            skLineSegment(sketch, "E875", {"start": v(0.88, 31.63) * mm, "end": v(0.84, 31.78) * mm});
            skLineSegment(sketch, "E876", {"start": v(0.84, 31.78) * mm, "end": v(0.75, 31.9) * mm});
            skLineSegment(sketch, "E877", {"start": v(0.75, 31.9) * mm, "end": v(0.62, 31.98) * mm});
            skLineSegment(sketch, "E878", {"start": v(0.62, 31.98) * mm, "end": v(0.49, 32.01) * mm});
            skLineSegment(sketch, "E879", {"start": v(0.49, 32.01) * mm, "end": v(0, 32.02) * mm});
            skLineSegment(sketch, "E880", {"start": v(0, 32.02) * mm, "end": v(-0.49, 32.01) * mm});
            skLineSegment(sketch, "E881", {"start": v(-0.49, 32.01) * mm, "end": v(-0.62, 31.98) * mm});
            skLineSegment(sketch, "E882", {"start": v(-0.62, 31.98) * mm, "end": v(-0.75, 31.9) * mm});
            skLineSegment(sketch, "E883", {"start": v(-0.75, 31.9) * mm, "end": v(-0.84, 31.78) * mm});
            skLineSegment(sketch, "E884", {"start": v(-0.84, 31.78) * mm, "end": v(-0.88, 31.63) * mm});
            skLineSegment(sketch, "E885", {"start": v(-0.88, 31.63) * mm, "end": v(-0.88, 31.02) * mm});
            skLineSegment(sketch, "E886", {"start": v(-0.88, 31.02) * mm, "end": v(-0.9, 30.9) * mm});
            skLineSegment(sketch, "E887", {"start": v(-0.9, 30.9) * mm, "end": v(-0.93, 30.77) * mm});
            skLineSegment(sketch, "E888", {"start": v(-0.93, 30.77) * mm, "end": v(-0.97, 30.64) * mm});
            skLineSegment(sketch, "E889", {"start": v(-0.97, 30.64) * mm, "end": v(-1.02, 30.53) * mm});
            skLineSegment(sketch, "E890", {"start": v(-1.02, 30.53) * mm, "end": v(-1.09, 30.41) * mm});
            skLineSegment(sketch, "E891", {"start": v(-1.09, 30.41) * mm, "end": v(-1.16, 30.3) * mm});
            skLineSegment(sketch, "E892", {"start": v(-1.16, 30.3) * mm, "end": v(-1.24, 30.2) * mm});
            skLineSegment(sketch, "E893", {"start": v(-1.24, 30.2) * mm, "end": v(-1.33, 30.11) * mm});
            skLineSegment(sketch, "E894", {"start": v(-1.33, 30.11) * mm, "end": v(-1.43, 30.03) * mm});
            skLineSegment(sketch, "E895", {"start": v(-1.43, 30.03) * mm, "end": v(-1.53, 29.95) * mm});
            skLineSegment(sketch, "E896", {"start": v(-1.53, 29.95) * mm, "end": v(-1.64, 29.88) * mm});
            skLineSegment(sketch, "E897", {"start": v(-1.64, 29.88) * mm, "end": v(-1.76, 29.82) * mm});
            skLineSegment(sketch, "E898", {"start": v(-1.76, 29.82) * mm, "end": v(-1.88, 29.77) * mm});
            skLineSegment(sketch, "E899", {"start": v(-1.88, 29.77) * mm, "end": v(-2.01, 29.73) * mm});
            skLineSegment(sketch, "E900", {"start": v(-2.01, 29.73) * mm, "end": v(-2.14, 29.7) * mm});
            skLineSegment(sketch, "E901", {"start": v(-2.14, 29.7) * mm, "end": v(-2.28, 29.67) * mm});
            skLineSegment(sketch, "E902", {"start": v(-2.28, 29.67) * mm, "end": v(-2.42, 29.67) * mm});
            skLineSegment(sketch, "E903", {"start": v(-2.42, 29.67) * mm, "end": v(-2.56, 29.68) * mm});
            skLineSegment(sketch, "E904", {"start": v(-2.56, 29.68) * mm, "end": v(-2.69, 29.7) * mm});
            skLineSegment(sketch, "E905", {"start": v(-2.69, 29.7) * mm, "end": v(-2.82, 29.74) * mm});
            skLineSegment(sketch, "E906", {"start": v(-2.82, 29.74) * mm, "end": v(-2.94, 29.78) * mm});
            skLineSegment(sketch, "E907", {"start": v(-2.94, 29.78) * mm, "end": v(-3.06, 29.83) * mm});
            skLineSegment(sketch, "E908", {"start": v(-3.06, 29.83) * mm, "end": v(-3.18, 29.9) * mm});
            skLineSegment(sketch, "E909", {"start": v(-3.18, 29.9) * mm, "end": v(-3.29, 29.96) * mm});
            skLineSegment(sketch, "E910", {"start": v(-3.29, 29.96) * mm, "end": v(-3.4, 30.04) * mm});
            skLineSegment(sketch, "E911", {"start": v(-3.4, 30.04) * mm, "end": v(-3.49, 30.13) * mm});
            skLineSegment(sketch, "E912", {"start": v(-3.49, 30.13) * mm, "end": v(-3.57, 30.22) * mm});
            skLineSegment(sketch, "E913", {"start": v(-3.57, 30.22) * mm, "end": v(-3.65, 30.32) * mm});
            skLineSegment(sketch, "E914", {"start": v(-3.65, 30.32) * mm, "end": v(-3.72, 30.43) * mm});
            skLineSegment(sketch, "E915", {"start": v(-3.72, 30.43) * mm, "end": v(-3.78, 30.55) * mm});
            skLineSegment(sketch, "E916", {"start": v(-3.78, 30.55) * mm, "end": v(-3.83, 30.67) * mm});
            skLineSegment(sketch, "E917", {"start": v(-3.83, 30.67) * mm, "end": v(-3.87, 30.8) * mm});
            skLineSegment(sketch, "E918", {"start": v(-3.87, 30.8) * mm, "end": v(-3.96, 31.4) * mm});
            skLineSegment(sketch, "E919", {"start": v(-3.96, 31.4) * mm, "end": v(-4.03, 31.53) * mm});
            skLineSegment(sketch, "E920", {"start": v(-4.03, 31.53) * mm, "end": v(-4.14, 31.64) * mm});
            skLineSegment(sketch, "E921", {"start": v(-4.14, 31.64) * mm, "end": v(-4.27, 31.7) * mm});
            skLineSegment(sketch, "E922", {"start": v(-4.27, 31.7) * mm, "end": v(-4.4, 31.71) * mm});
            skLineSegment(sketch, "E923", {"start": v(-4.4, 31.71) * mm, "end": v(-4.9, 31.65) * mm});
            skLineSegment(sketch, "E924", {"start": v(-4.9, 31.65) * mm, "end": v(-5.37, 31.56) * mm});
            skLineSegment(sketch, "E925", {"start": v(-5.37, 31.56) * mm, "end": v(-5.5, 31.51) * mm});
            skLineSegment(sketch, "E926", {"start": v(-5.5, 31.51) * mm, "end": v(-5.61, 31.4) * mm});
            skLineSegment(sketch, "E927", {"start": v(-5.61, 31.4) * mm, "end": v(-5.68, 31.28) * mm});
            skLineSegment(sketch, "E928", {"start": v(-5.68, 31.28) * mm, "end": v(-5.7, 31.12) * mm});
            skLineSegment(sketch, "E929", {"start": v(-5.7, 31.12) * mm, "end": v(-5.6, 30.53) * mm});
            skLineSegment(sketch, "E930", {"start": v(-5.6, 30.53) * mm, "end": v(-5.6, 30.4) * mm});
            skLineSegment(sketch, "E931", {"start": v(-5.6, 30.4) * mm, "end": v(-5.62, 30.26) * mm});
            skLineSegment(sketch, "E932", {"start": v(-5.62, 30.26) * mm, "end": v(-5.64, 30.14) * mm});
            skLineSegment(sketch, "E933", {"start": v(-5.64, 30.14) * mm, "end": v(-5.68, 30.01) * mm});
            skLineSegment(sketch, "E934", {"start": v(-5.68, 30.01) * mm, "end": v(-5.72, 29.9) * mm});
            skLineSegment(sketch, "E935", {"start": v(-5.72, 29.9) * mm, "end": v(-5.78, 29.78) * mm});
            skLineSegment(sketch, "E936", {"start": v(-5.78, 29.78) * mm, "end": v(-5.84, 29.66) * mm});
            skLineSegment(sketch, "E937", {"start": v(-5.84, 29.66) * mm, "end": v(-5.92, 29.56) * mm});
            skLineSegment(sketch, "E938", {"start": v(-5.92, 29.56) * mm, "end": v(-6, 29.46) * mm});
            skLineSegment(sketch, "E939", {"start": v(-6, 29.46) * mm, "end": v(-6.09, 29.37) * mm});
            skLineSegment(sketch, "E940", {"start": v(-6.09, 29.37) * mm, "end": v(-6.19, 29.28) * mm});
            skLineSegment(sketch, "E941", {"start": v(-6.19, 29.28) * mm, "end": v(-6.3, 29.2) * mm});
            skLineSegment(sketch, "E942", {"start": v(-6.3, 29.2) * mm, "end": v(-6.4, 29.13) * mm});
            skLineSegment(sketch, "E943", {"start": v(-6.4, 29.13) * mm, "end": v(-6.53, 29.07) * mm});
            skLineSegment(sketch, "E944", {"start": v(-6.53, 29.07) * mm, "end": v(-6.66, 29.02) * mm});
            skLineSegment(sketch, "E945", {"start": v(-6.66, 29.02) * mm, "end": v(-6.79, 28.98) * mm});
            skLineSegment(sketch, "E946", {"start": v(-6.79, 28.98) * mm, "end": v(-6.93, 28.96) * mm});
            skLineSegment(sketch, "E947", {"start": v(-6.93, 28.96) * mm, "end": v(-7.06, 28.95) * mm});
            skLineSegment(sketch, "E948", {"start": v(-7.06, 28.95) * mm, "end": v(-7.2, 28.95) * mm});
            skLineSegment(sketch, "E949", {"start": v(-7.2, 28.95) * mm, "end": v(-7.33, 28.96) * mm});
            skLineSegment(sketch, "E950", {"start": v(-7.33, 28.96) * mm, "end": v(-7.46, 28.98) * mm});
            skLineSegment(sketch, "E951", {"start": v(-7.46, 28.98) * mm, "end": v(-7.59, 29.01) * mm});
            skLineSegment(sketch, "E952", {"start": v(-7.59, 29.01) * mm, "end": v(-7.71, 29.06) * mm});
            skLineSegment(sketch, "E953", {"start": v(-7.71, 29.06) * mm, "end": v(-7.83, 29.11) * mm});
            skLineSegment(sketch, "E954", {"start": v(-7.83, 29.11) * mm, "end": v(-7.94, 29.17) * mm});
            skLineSegment(sketch, "E955", {"start": v(-7.94, 29.17) * mm, "end": v(-8.05, 29.24) * mm});
            skLineSegment(sketch, "E956", {"start": v(-8.05, 29.24) * mm, "end": v(-8.15, 29.32) * mm});
            skLineSegment(sketch, "E957", {"start": v(-8.15, 29.32) * mm, "end": v(-8.24, 29.41) * mm});
            skLineSegment(sketch, "E958", {"start": v(-8.24, 29.41) * mm, "end": v(-8.33, 29.5) * mm});
            skLineSegment(sketch, "E959", {"start": v(-8.33, 29.5) * mm, "end": v(-8.4, 29.61) * mm});
            skLineSegment(sketch, "E960", {"start": v(-8.4, 29.61) * mm, "end": v(-8.48, 29.72) * mm});
            skLineSegment(sketch, "E961", {"start": v(-8.48, 29.72) * mm, "end": v(-8.53, 29.84) * mm});
            skLineSegment(sketch, "E962", {"start": v(-8.53, 29.84) * mm, "end": v(-8.71, 30.42) * mm});
            skLineSegment(sketch, "E963", {"start": v(-8.71, 30.42) * mm, "end": v(-8.8, 30.55) * mm});
            skLineSegment(sketch, "E964", {"start": v(-8.8, 30.55) * mm, "end": v(-8.92, 30.63) * mm});
            skLineSegment(sketch, "E965", {"start": v(-8.92, 30.63) * mm, "end": v(-9.07, 30.68) * mm});
            skLineSegment(sketch, "E966", {"start": v(-9.07, 30.68) * mm, "end": v(-9.2, 30.67) * mm});
            skLineSegment(sketch, "E967", {"start": v(-9.2, 30.67) * mm, "end": v(-9.67, 30.53) * mm});
            skLineSegment(sketch, "E968", {"start": v(-9.67, 30.53) * mm, "end": v(-10.13, 30.37) * mm});
            skLineSegment(sketch, "E969", {"start": v(-10.13, 30.37) * mm, "end": v(-10.25, 30.3) * mm});
            skLineSegment(sketch, "E970", {"start": v(-10.25, 30.3) * mm, "end": v(-10.35, 30.18) * mm});
            skLineSegment(sketch, "E971", {"start": v(-10.35, 30.18) * mm, "end": v(-10.4, 30.04) * mm});
            skLineSegment(sketch, "E972", {"start": v(-10.4, 30.04) * mm, "end": v(-10.4, 29.89) * mm});
            skLineSegment(sketch, "E973", {"start": v(-10.4, 29.89) * mm, "end": v(-10.2, 29.31) * mm});
            skLineSegment(sketch, "E974", {"start": v(-10.2, 29.31) * mm, "end": v(-10.19, 29.18) * mm});
            skLineSegment(sketch, "E975", {"start": v(-10.19, 29.18) * mm, "end": v(-10.18, 29.05) * mm});
            skLineSegment(sketch, "E976", {"start": v(-10.18, 29.05) * mm, "end": v(-10.18, 28.92) * mm});
            skLineSegment(sketch, "E977", {"start": v(-10.18, 28.92) * mm, "end": v(-10.2, 28.8) * mm});
            skLineSegment(sketch, "E978", {"start": v(-10.2, 28.8) * mm, "end": v(-10.22, 28.67) * mm});
            skLineSegment(sketch, "E979", {"start": v(-10.22, 28.67) * mm, "end": v(-10.26, 28.54) * mm});
            skLineSegment(sketch, "E980", {"start": v(-10.26, 28.54) * mm, "end": v(-10.3, 28.42) * mm});
            skLineSegment(sketch, "E981", {"start": v(-10.3, 28.42) * mm, "end": v(-10.36, 28.3) * mm});
            skLineSegment(sketch, "E982", {"start": v(-10.36, 28.3) * mm, "end": v(-10.43, 28.2) * mm});
            skLineSegment(sketch, "E983", {"start": v(-10.43, 28.2) * mm, "end": v(-10.5, 28.1) * mm});
            skLineSegment(sketch, "E984", {"start": v(-10.5, 28.1) * mm, "end": v(-10.6, 28) * mm});
            skLineSegment(sketch, "E985", {"start": v(-10.6, 28) * mm, "end": v(-10.68, 27.9) * mm});
            skLineSegment(sketch, "E986", {"start": v(-10.68, 27.9) * mm, "end": v(-10.79, 27.81) * mm});
            skLineSegment(sketch, "E987", {"start": v(-10.79, 27.81) * mm, "end": v(-10.9, 27.73) * mm});
            skLineSegment(sketch, "E988", {"start": v(-10.9, 27.73) * mm, "end": v(-11.01, 27.66) * mm});
            skLineSegment(sketch, "E989", {"start": v(-11.01, 27.66) * mm, "end": v(-11.14, 27.6) * mm});
            skLineSegment(sketch, "E990", {"start": v(-11.14, 27.6) * mm, "end": v(-11.27, 27.56) * mm});
            skLineSegment(sketch, "E991", {"start": v(-11.27, 27.56) * mm, "end": v(-11.4, 27.53) * mm});
            skLineSegment(sketch, "E992", {"start": v(-11.4, 27.53) * mm, "end": v(-11.54, 27.5) * mm});
            skLineSegment(sketch, "E993", {"start": v(-11.54, 27.5) * mm, "end": v(-11.67, 27.5) * mm});
            skLineSegment(sketch, "E994", {"start": v(-11.67, 27.5) * mm, "end": v(-11.8, 27.5) * mm});
            skLineSegment(sketch, "E995", {"start": v(-11.8, 27.5) * mm, "end": v(-11.93, 27.52) * mm});
            skLineSegment(sketch, "E996", {"start": v(-11.93, 27.52) * mm, "end": v(-12.06, 27.54) * mm});
            skLineSegment(sketch, "E997", {"start": v(-12.06, 27.54) * mm, "end": v(-12.19, 27.57) * mm});
            skLineSegment(sketch, "E998", {"start": v(-12.19, 27.57) * mm, "end": v(-12.3, 27.62) * mm});
            skLineSegment(sketch, "E999", {"start": v(-12.3, 27.62) * mm, "end": v(-12.42, 27.67) * mm});
            skLineSegment(sketch, "E1000", {"start": v(-12.42, 27.67) * mm, "end": v(-12.54, 27.73) * mm});
            skLineSegment(sketch, "E1001", {"start": v(-12.54, 27.73) * mm, "end": v(-12.64, 27.8) * mm});
            skLineSegment(sketch, "E1002", {"start": v(-12.64, 27.8) * mm, "end": v(-12.74, 27.89) * mm});
            skLineSegment(sketch, "E1003", {"start": v(-12.74, 27.89) * mm, "end": v(-12.83, 27.98) * mm});
            skLineSegment(sketch, "E1004", {"start": v(-12.83, 27.98) * mm, "end": v(-12.92, 28.08) * mm});
            skLineSegment(sketch, "E1005", {"start": v(-12.92, 28.08) * mm, "end": v(-13, 28.19) * mm});
            skLineSegment(sketch, "E1006", {"start": v(-13, 28.19) * mm, "end": v(-13.26, 28.73) * mm});
            skLineSegment(sketch, "E1007", {"start": v(-13.26, 28.73) * mm, "end": v(-13.36, 28.85) * mm});
            skLineSegment(sketch, "E1008", {"start": v(-13.36, 28.85) * mm, "end": v(-13.5, 28.91) * mm});
            skLineSegment(sketch, "E1009", {"start": v(-13.5, 28.91) * mm, "end": v(-13.65, 28.93) * mm});
            skLineSegment(sketch, "E1010", {"start": v(-13.65, 28.93) * mm, "end": v(-13.78, 28.9) * mm});
            skLineSegment(sketch, "E1011", {"start": v(-13.78, 28.9) * mm, "end": v(-14.22, 28.7) * mm});
            skLineSegment(sketch, "E1012", {"start": v(-14.22, 28.7) * mm, "end": v(-14.66, 28.47) * mm});
            skLineSegment(sketch, "E1013", {"start": v(-14.66, 28.47) * mm, "end": v(-14.76, 28.38) * mm});
            skLineSegment(sketch, "E1014", {"start": v(-14.76, 28.38) * mm, "end": v(-14.84, 28.25) * mm});
            skLineSegment(sketch, "E1015", {"start": v(-14.84, 28.25) * mm, "end": v(-14.87, 28.1) * mm});
            skLineSegment(sketch, "E1016", {"start": v(-14.87, 28.1) * mm, "end": v(-14.84, 27.95) * mm});
            skLineSegment(sketch, "E1017", {"start": v(-14.84, 27.95) * mm, "end": v(-14.57, 27.4) * mm});
            skLineSegment(sketch, "E1018", {"start": v(-14.57, 27.4) * mm, "end": v(-14.53, 27.28) * mm});
            skLineSegment(sketch, "E1019", {"start": v(-14.53, 27.28) * mm, "end": v(-14.5, 27.16) * mm});
            skLineSegment(sketch, "E1020", {"start": v(-14.5, 27.16) * mm, "end": v(-14.48, 27.03) * mm});
            skLineSegment(sketch, "E1021", {"start": v(-14.48, 27.03) * mm, "end": v(-14.48, 26.9) * mm});
            skLineSegment(sketch, "E1022", {"start": v(-14.48, 26.9) * mm, "end": v(-14.48, 26.77) * mm});
            skLineSegment(sketch, "E1023", {"start": v(-14.48, 26.77) * mm, "end": v(-14.5, 26.64) * mm});
            skLineSegment(sketch, "E1024", {"start": v(-14.5, 26.64) * mm, "end": v(-14.53, 26.52) * mm});
            skLineSegment(sketch, "E1025", {"start": v(-14.53, 26.52) * mm, "end": v(-14.57, 26.4) * mm});
            skLineSegment(sketch, "E1026", {"start": v(-14.57, 26.4) * mm, "end": v(-14.62, 26.27) * mm});
            skLineSegment(sketch, "E1027", {"start": v(-14.62, 26.27) * mm, "end": v(-14.68, 26.16) * mm});
            skLineSegment(sketch, "E1028", {"start": v(-14.68, 26.16) * mm, "end": v(-14.74, 26.05) * mm});
            skLineSegment(sketch, "E1029", {"start": v(-14.74, 26.05) * mm, "end": v(-14.82, 25.94) * mm});
            skLineSegment(sketch, "E1030", {"start": v(-14.82, 25.94) * mm, "end": v(-14.91, 25.84) * mm});
            skLineSegment(sketch, "E1031", {"start": v(-14.91, 25.84) * mm, "end": v(-15, 25.74) * mm});
            skLineSegment(sketch, "E1032", {"start": v(-15, 25.74) * mm, "end": v(-15.11, 25.66) * mm});
            skLineSegment(sketch, "E1033", {"start": v(-15.11, 25.66) * mm, "end": v(-15.23, 25.58) * mm});
            skLineSegment(sketch, "E1034", {"start": v(-15.23, 25.58) * mm, "end": v(-15.35, 25.52) * mm});
            skLineSegment(sketch, "E1035", {"start": v(-15.35, 25.52) * mm, "end": v(-15.48, 25.46) * mm});
            skLineSegment(sketch, "E1036", {"start": v(-15.48, 25.46) * mm, "end": v(-15.6, 25.43) * mm});
            skLineSegment(sketch, "E1037", {"start": v(-15.6, 25.43) * mm, "end": v(-15.74, 25.4) * mm});
            skLineSegment(sketch, "E1038", {"start": v(-15.74, 25.4) * mm, "end": v(-15.87, 25.38) * mm});
            skLineSegment(sketch, "E1039", {"start": v(-15.87, 25.38) * mm, "end": v(-16, 25.37) * mm});
            skLineSegment(sketch, "E1040", {"start": v(-16, 25.37) * mm, "end": v(-16.13, 25.38) * mm});
            skLineSegment(sketch, "E1041", {"start": v(-16.13, 25.38) * mm, "end": v(-16.26, 25.39) * mm});
            skLineSegment(sketch, "E1042", {"start": v(-16.26, 25.39) * mm, "end": v(-16.38, 25.41) * mm});
            skLineSegment(sketch, "E1043", {"start": v(-16.38, 25.41) * mm, "end": v(-16.5, 25.45) * mm});
            skLineSegment(sketch, "E1044", {"start": v(-16.5, 25.45) * mm, "end": v(-16.63, 25.5) * mm});
            skLineSegment(sketch, "E1045", {"start": v(-16.63, 25.5) * mm, "end": v(-16.74, 25.55) * mm});
            skLineSegment(sketch, "E1046", {"start": v(-16.74, 25.55) * mm, "end": v(-16.85, 25.62) * mm});
            skLineSegment(sketch, "E1047", {"start": v(-16.85, 25.62) * mm, "end": v(-16.96, 25.7) * mm});
            skLineSegment(sketch, "E1048", {"start": v(-16.96, 25.7) * mm, "end": v(-17.06, 25.78) * mm});
            skLineSegment(sketch, "E1049", {"start": v(-17.06, 25.78) * mm, "end": v(-17.15, 25.87) * mm});
            skLineSegment(sketch, "E1050", {"start": v(-17.15, 25.87) * mm, "end": v(-17.5, 26.37) * mm});
            skLineSegment(sketch, "E1051", {"start": v(-17.5, 26.37) * mm, "end": v(-17.61, 26.47) * mm});
            skLineSegment(sketch, "E1052", {"start": v(-17.61, 26.47) * mm, "end": v(-17.76, 26.51) * mm});
            skLineSegment(sketch, "E1053", {"start": v(-17.76, 26.51) * mm, "end": v(-17.91, 26.5) * mm});
            skLineSegment(sketch, "E1054", {"start": v(-17.91, 26.5) * mm, "end": v(-18.04, 26.46) * mm});
            skLineSegment(sketch, "E1055", {"start": v(-18.04, 26.46) * mm, "end": v(-18.44, 26.19) * mm});
            skLineSegment(sketch, "E1056", {"start": v(-18.44, 26.19) * mm, "end": v(-18.84, 25.9) * mm});
            skLineSegment(sketch, "E1057", {"start": v(-18.84, 25.9) * mm, "end": v(-18.92, 25.8) * mm});
            skLineSegment(sketch, "E1058", {"start": v(-18.92, 25.8) * mm, "end": v(-18.98, 25.65) * mm});
            skLineSegment(sketch, "E1059", {"start": v(-18.98, 25.65) * mm, "end": v(-18.99, 25.5) * mm});
            skLineSegment(sketch, "E1060", {"start": v(-18.99, 25.5) * mm, "end": v(-18.94, 25.36) * mm});
            skLineSegment(sketch, "E1061", {"start": v(-18.94, 25.36) * mm, "end": v(-18.58, 24.86) * mm});
            skLineSegment(sketch, "E1062", {"start": v(-18.58, 24.86) * mm, "end": v(-18.53, 24.75) * mm});
            skLineSegment(sketch, "E1063", {"start": v(-18.53, 24.75) * mm, "end": v(-18.48, 24.62) * mm});
            skLineSegment(sketch, "E1064", {"start": v(-18.48, 24.62) * mm, "end": v(-18.44, 24.5) * mm});
            skLineSegment(sketch, "E1065", {"start": v(-18.44, 24.5) * mm, "end": v(-18.42, 24.37) * mm});
            skLineSegment(sketch, "E1066", {"start": v(-18.42, 24.37) * mm, "end": v(-18.4, 24.24) * mm});
            skLineSegment(sketch, "E1067", {"start": v(-18.4, 24.24) * mm, "end": v(-18.4, 24.12) * mm});
            skLineSegment(sketch, "E1068", {"start": v(-18.4, 24.12) * mm, "end": v(-18.41, 23.99) * mm});
            skLineSegment(sketch, "E1069", {"start": v(-18.41, 23.99) * mm, "end": v(-18.43, 23.86) * mm});
            skLineSegment(sketch, "E1070", {"start": v(-18.43, 23.86) * mm, "end": v(-18.46, 23.73) * mm});
            skLineSegment(sketch, "E1071", {"start": v(-18.46, 23.73) * mm, "end": v(-18.5, 23.61) * mm});
            skLineSegment(sketch, "E1072", {"start": v(-18.5, 23.61) * mm, "end": v(-18.55, 23.49) * mm});
            skLineSegment(sketch, "E1073", {"start": v(-18.55, 23.49) * mm, "end": v(-18.61, 23.37) * mm});
            skLineSegment(sketch, "E1074", {"start": v(-18.61, 23.37) * mm, "end": v(-18.68, 23.26) * mm});
            skLineSegment(sketch, "E1075", {"start": v(-18.68, 23.26) * mm, "end": v(-18.77, 23.15) * mm});
            skLineSegment(sketch, "E1076", {"start": v(-18.77, 23.15) * mm, "end": v(-18.86, 23.05) * mm});
            skLineSegment(sketch, "E1077", {"start": v(-18.86, 23.05) * mm, "end": v(-18.96, 22.95) * mm});
            skLineSegment(sketch, "E1078", {"start": v(-18.96, 22.95) * mm, "end": v(-19.07, 22.87) * mm});
            skLineSegment(sketch, "E1079", {"start": v(-19.07, 22.87) * mm, "end": v(-19.19, 22.8) * mm});
            skLineSegment(sketch, "E1080", {"start": v(-19.19, 22.8) * mm, "end": v(-19.3, 22.74) * mm});
            skLineSegment(sketch, "E1081", {"start": v(-19.3, 22.74) * mm, "end": v(-19.43, 22.7) * mm});
            skLineSegment(sketch, "E1082", {"start": v(-19.43, 22.7) * mm, "end": v(-19.56, 22.66) * mm});
            skLineSegment(sketch, "E1083", {"start": v(-19.56, 22.66) * mm, "end": v(-19.69, 22.63) * mm});
            skLineSegment(sketch, "E1084", {"start": v(-19.69, 22.63) * mm, "end": v(-19.82, 22.62) * mm});
            skLineSegment(sketch, "E1085", {"start": v(-19.82, 22.62) * mm, "end": v(-19.95, 22.61) * mm});
            skLineSegment(sketch, "E1086", {"start": v(-19.95, 22.61) * mm, "end": v(-20.08, 22.62) * mm});
            skLineSegment(sketch, "E1087", {"start": v(-20.08, 22.62) * mm, "end": v(-20.2, 22.63) * mm});
            skLineSegment(sketch, "E1088", {"start": v(-20.2, 22.63) * mm, "end": v(-20.33, 22.66) * mm});
            skLineSegment(sketch, "E1089", {"start": v(-20.33, 22.66) * mm, "end": v(-20.45, 22.7) * mm});
            skLineSegment(sketch, "E1090", {"start": v(-20.45, 22.7) * mm, "end": v(-20.57, 22.74) * mm});
            skLineSegment(sketch, "E1091", {"start": v(-20.57, 22.74) * mm, "end": v(-20.69, 22.8) * mm});
            skLineSegment(sketch, "E1092", {"start": v(-20.69, 22.8) * mm, "end": v(-20.8, 22.87) * mm});
            skLineSegment(sketch, "E1093", {"start": v(-20.8, 22.87) * mm, "end": v(-20.9, 22.95) * mm});
            skLineSegment(sketch, "E1094", {"start": v(-20.9, 22.95) * mm, "end": v(-21.32, 23.4) * mm});
            skLineSegment(sketch, "E1095", {"start": v(-21.32, 23.4) * mm, "end": v(-21.45, 23.47) * mm});
            skLineSegment(sketch, "E1096", {"start": v(-21.45, 23.47) * mm, "end": v(-21.6, 23.5) * mm});
            skLineSegment(sketch, "E1097", {"start": v(-21.6, 23.5) * mm, "end": v(-21.75, 23.46) * mm});
            skLineSegment(sketch, "E1098", {"start": v(-21.75, 23.46) * mm, "end": v(-21.87, 23.4) * mm});
            skLineSegment(sketch, "E1099", {"start": v(-21.87, 23.4) * mm, "end": v(-22.23, 23.06) * mm});
            skLineSegment(sketch, "E1100", {"start": v(-22.23, 23.06) * mm, "end": v(-22.57, 22.72) * mm});
            skLineSegment(sketch, "E1101", {"start": v(-22.57, 22.72) * mm, "end": v(-22.65, 22.6) * mm});
            skLineSegment(sketch, "E1102", {"start": v(-22.65, 22.6) * mm, "end": v(-22.68, 22.45) * mm});
            skLineSegment(sketch, "E1103", {"start": v(-22.68, 22.45) * mm, "end": v(-22.66, 22.3) * mm});
            skLineSegment(sketch, "E1104", {"start": v(-22.66, 22.3) * mm, "end": v(-22.6, 22.17) * mm});
            skLineSegment(sketch, "E1105", {"start": v(-22.6, 22.17) * mm, "end": v(-22.17, 21.74) * mm});
            skLineSegment(sketch, "E1106", {"start": v(-22.17, 21.74) * mm, "end": v(-22.1, 21.63) * mm});
            skLineSegment(sketch, "E1107", {"start": v(-22.1, 21.63) * mm, "end": v(-22.03, 21.51) * mm});
            skLineSegment(sketch, "E1108", {"start": v(-22.03, 21.51) * mm, "end": v(-21.97, 21.4) * mm});
            skLineSegment(sketch, "E1109", {"start": v(-21.97, 21.4) * mm, "end": v(-21.93, 21.28) * mm});
            skLineSegment(sketch, "E1110", {"start": v(-21.93, 21.28) * mm, "end": v(-21.9, 21.15) * mm});
            skLineSegment(sketch, "E1111", {"start": v(-21.9, 21.15) * mm, "end": v(-21.87, 21.02) * mm});
            skLineSegment(sketch, "E1112", {"start": v(-21.87, 21.02) * mm, "end": v(-21.86, 20.9) * mm});
            skLineSegment(sketch, "E1113", {"start": v(-21.86, 20.9) * mm, "end": v(-21.86, 20.77) * mm});
            skLineSegment(sketch, "E1114", {"start": v(-21.86, 20.77) * mm, "end": v(-21.87, 20.64) * mm});
            skLineSegment(sketch, "E1115", {"start": v(-21.87, 20.64) * mm, "end": v(-21.9, 20.5) * mm});
            skLineSegment(sketch, "E1116", {"start": v(-21.9, 20.5) * mm, "end": v(-21.93, 20.38) * mm});
            skLineSegment(sketch, "E1117", {"start": v(-21.93, 20.38) * mm, "end": v(-21.97, 20.26) * mm});
            skLineSegment(sketch, "E1118", {"start": v(-21.97, 20.26) * mm, "end": v(-22.02, 20.13) * mm});
            skLineSegment(sketch, "E1119", {"start": v(-22.02, 20.13) * mm, "end": v(-22.08, 20.02) * mm});
            skLineSegment(sketch, "E1120", {"start": v(-22.08, 20.02) * mm, "end": v(-22.16, 19.9) * mm});
            skLineSegment(sketch, "E1121", {"start": v(-22.16, 19.9) * mm, "end": v(-22.24, 19.8) * mm});
            skLineSegment(sketch, "E1122", {"start": v(-22.24, 19.8) * mm, "end": v(-22.34, 19.7) * mm});
            skLineSegment(sketch, "E1123", {"start": v(-22.34, 19.7) * mm, "end": v(-22.45, 19.6) * mm});
            skLineSegment(sketch, "E1124", {"start": v(-22.45, 19.6) * mm, "end": v(-22.56, 19.53) * mm});
            skLineSegment(sketch, "E1125", {"start": v(-22.56, 19.53) * mm, "end": v(-22.68, 19.46) * mm});
            skLineSegment(sketch, "E1126", {"start": v(-22.68, 19.46) * mm, "end": v(-22.8, 19.4) * mm});
            skLineSegment(sketch, "E1127", {"start": v(-22.8, 19.4) * mm, "end": v(-22.92, 19.36) * mm});
            skLineSegment(sketch, "E1128", {"start": v(-22.92, 19.36) * mm, "end": v(-23.04, 19.33) * mm});
            skLineSegment(sketch, "E1129", {"start": v(-23.04, 19.33) * mm, "end": v(-23.17, 19.3) * mm});
            skLineSegment(sketch, "E1130", {"start": v(-23.17, 19.3) * mm, "end": v(-23.3, 19.29) * mm});
            skLineSegment(sketch, "E1131", {"start": v(-23.3, 19.29) * mm, "end": v(-23.43, 19.28) * mm});
            skLineSegment(sketch, "E1132", {"start": v(-23.43, 19.28) * mm, "end": v(-23.56, 19.29) * mm});
            skLineSegment(sketch, "E1133", {"start": v(-23.56, 19.29) * mm, "end": v(-23.68, 19.3) * mm});
            skLineSegment(sketch, "E1134", {"start": v(-23.68, 19.3) * mm, "end": v(-23.8, 19.34) * mm});
            skLineSegment(sketch, "E1135", {"start": v(-23.8, 19.34) * mm, "end": v(-23.93, 19.38) * mm});
            skLineSegment(sketch, "E1136", {"start": v(-23.93, 19.38) * mm, "end": v(-24.05, 19.43) * mm});
            skLineSegment(sketch, "E1137", {"start": v(-24.05, 19.43) * mm, "end": v(-24.17, 19.5) * mm});
            skLineSegment(sketch, "E1138", {"start": v(-24.17, 19.5) * mm, "end": v(-24.65, 19.86) * mm});
            skLineSegment(sketch, "E1139", {"start": v(-24.65, 19.86) * mm, "end": v(-24.79, 19.92) * mm});
            skLineSegment(sketch, "E1140", {"start": v(-24.79, 19.92) * mm, "end": v(-24.94, 19.92) * mm});
            skLineSegment(sketch, "E1141", {"start": v(-24.94, 19.92) * mm, "end": v(-25.08, 19.87) * mm});
            skLineSegment(sketch, "E1142", {"start": v(-25.08, 19.87) * mm, "end": v(-25.19, 19.78) * mm});
            skLineSegment(sketch, "E1143", {"start": v(-25.19, 19.78) * mm, "end": v(-25.5, 19.4) * mm});
            skLineSegment(sketch, "E1144", {"start": v(-25.5, 19.4) * mm, "end": v(-25.78, 19) * mm});
            skLineSegment(sketch, "E1145", {"start": v(-25.78, 19) * mm, "end": v(-25.84, 18.88) * mm});
            skLineSegment(sketch, "E1146", {"start": v(-25.84, 18.88) * mm, "end": v(-25.85, 18.73) * mm});
            skLineSegment(sketch, "E1147", {"start": v(-25.85, 18.73) * mm, "end": v(-25.8, 18.58) * mm});
            skLineSegment(sketch, "E1148", {"start": v(-25.8, 18.58) * mm, "end": v(-25.72, 18.46) * mm});
            skLineSegment(sketch, "E1149", {"start": v(-25.72, 18.46) * mm, "end": v(-25.23, 18.1) * mm});
            skLineSegment(sketch, "E1150", {"start": v(-25.23, 18.1) * mm, "end": v(-25.14, 18) * mm});
            skLineSegment(sketch, "E1151", {"start": v(-25.14, 18) * mm, "end": v(-25.06, 17.9) * mm});
            skLineSegment(sketch, "E1152", {"start": v(-25.06, 17.9) * mm, "end": v(-24.99, 17.8) * mm});
            skLineSegment(sketch, "E1153", {"start": v(-24.99, 17.8) * mm, "end": v(-24.92, 17.68) * mm});
            skLineSegment(sketch, "E1154", {"start": v(-24.92, 17.68) * mm, "end": v(-24.87, 17.56) * mm});
            skLineSegment(sketch, "E1155", {"start": v(-24.87, 17.56) * mm, "end": v(-24.83, 17.44) * mm});
            skLineSegment(sketch, "E1156", {"start": v(-24.83, 17.44) * mm, "end": v(-24.8, 17.31) * mm});
            skLineSegment(sketch, "E1157", {"start": v(-24.8, 17.31) * mm, "end": v(-24.78, 17.19) * mm});
            skLineSegment(sketch, "E1158", {"start": v(-24.78, 17.19) * mm, "end": v(-24.77, 17.06) * mm});
            skLineSegment(sketch, "E1159", {"start": v(-24.77, 17.06) * mm, "end": v(-24.77, 16.93) * mm});
            skLineSegment(sketch, "E1160", {"start": v(-24.77, 16.93) * mm, "end": v(-24.79, 16.8) * mm});
            skLineSegment(sketch, "E1161", {"start": v(-24.79, 16.8) * mm, "end": v(-24.8, 16.67) * mm});
            skLineSegment(sketch, "E1162", {"start": v(-24.8, 16.67) * mm, "end": v(-24.84, 16.54) * mm});
            skLineSegment(sketch, "E1163", {"start": v(-24.84, 16.54) * mm, "end": v(-24.89, 16.4) * mm});
            skLineSegment(sketch, "E1164", {"start": v(-24.89, 16.4) * mm, "end": v(-24.94, 16.28) * mm});
            skLineSegment(sketch, "E1165", {"start": v(-24.94, 16.28) * mm, "end": v(-25, 16.16) * mm});
            skLineSegment(sketch, "E1166", {"start": v(-25, 16.16) * mm, "end": v(-25.1, 16.05) * mm});
            skLineSegment(sketch, "E1167", {"start": v(-25.1, 16.05) * mm, "end": v(-25.18, 15.95) * mm});
            skLineSegment(sketch, "E1168", {"start": v(-25.18, 15.95) * mm, "end": v(-25.28, 15.86) * mm});
            skLineSegment(sketch, "E1169", {"start": v(-25.28, 15.86) * mm, "end": v(-25.39, 15.77) * mm});
            skLineSegment(sketch, "E1170", {"start": v(-25.39, 15.77) * mm, "end": v(-25.5, 15.7) * mm});
            skLineSegment(sketch, "E1171", {"start": v(-25.5, 15.7) * mm, "end": v(-25.6, 15.64) * mm});
            skLineSegment(sketch, "E1172", {"start": v(-25.6, 15.64) * mm, "end": v(-25.73, 15.58) * mm});
            skLineSegment(sketch, "E1173", {"start": v(-25.73, 15.58) * mm, "end": v(-25.85, 15.54) * mm});
            skLineSegment(sketch, "E1174", {"start": v(-25.85, 15.54) * mm, "end": v(-25.97, 15.5) * mm});
            skLineSegment(sketch, "E1175", {"start": v(-25.97, 15.5) * mm, "end": v(-26.1, 15.48) * mm});
            skLineSegment(sketch, "E1176", {"start": v(-26.1, 15.48) * mm, "end": v(-26.23, 15.47) * mm});
            skLineSegment(sketch, "E1177", {"start": v(-26.23, 15.47) * mm, "end": v(-26.36, 15.47) * mm});
            skLineSegment(sketch, "E1178", {"start": v(-26.36, 15.47) * mm, "end": v(-26.49, 15.48) * mm});
            skLineSegment(sketch, "E1179", {"start": v(-26.49, 15.48) * mm, "end": v(-26.61, 15.5) * mm});
            skLineSegment(sketch, "E1180", {"start": v(-26.61, 15.5) * mm, "end": v(-26.74, 15.53) * mm});
            skLineSegment(sketch, "E1181", {"start": v(-26.74, 15.53) * mm, "end": v(-26.86, 15.57) * mm});
            skLineSegment(sketch, "E1182", {"start": v(-26.86, 15.57) * mm, "end": v(-27.4, 15.87) * mm});
            skLineSegment(sketch, "E1183", {"start": v(-27.4, 15.87) * mm, "end": v(-27.54, 15.9) * mm});
            skLineSegment(sketch, "E1184", {"start": v(-27.54, 15.9) * mm, "end": v(-27.7, 15.88) * mm});
            skLineSegment(sketch, "E1185", {"start": v(-27.7, 15.88) * mm, "end": v(-27.83, 15.8) * mm});
            skLineSegment(sketch, "E1186", {"start": v(-27.83, 15.8) * mm, "end": v(-27.92, 15.7) * mm});
            skLineSegment(sketch, "E1187", {"start": v(-27.92, 15.7) * mm, "end": v(-28.16, 15.28) * mm});
            skLineSegment(sketch, "E1188", {"start": v(-28.16, 15.28) * mm, "end": v(-28.39, 14.85) * mm});
            skLineSegment(sketch, "E1189", {"start": v(-28.39, 14.85) * mm, "end": v(-28.42, 14.72) * mm});
            skLineSegment(sketch, "E1190", {"start": v(-28.42, 14.72) * mm, "end": v(-28.4, 14.56) * mm});
            skLineSegment(sketch, "E1191", {"start": v(-28.4, 14.56) * mm, "end": v(-28.35, 14.43) * mm});
            skLineSegment(sketch, "E1192", {"start": v(-28.35, 14.43) * mm, "end": v(-28.24, 14.32) * mm});
            skLineSegment(sketch, "E1193", {"start": v(-28.24, 14.32) * mm, "end": v(-27.7, 14.03) * mm});
            skLineSegment(sketch, "E1194", {"start": v(-27.7, 14.03) * mm, "end": v(-27.6, 13.95) * mm});
            skLineSegment(sketch, "E1195", {"start": v(-27.6, 13.95) * mm, "end": v(-27.5, 13.86) * mm});
            skLineSegment(sketch, "E1196", {"start": v(-27.5, 13.86) * mm, "end": v(-27.41, 13.77) * mm});
            skLineSegment(sketch, "E1197", {"start": v(-27.41, 13.77) * mm, "end": v(-27.34, 13.67) * mm});
            skLineSegment(sketch, "E1198", {"start": v(-27.34, 13.67) * mm, "end": v(-27.27, 13.56) * mm});
            skLineSegment(sketch, "E1199", {"start": v(-27.27, 13.56) * mm, "end": v(-27.2, 13.44) * mm});
            skLineSegment(sketch, "E1200", {"start": v(-27.2, 13.44) * mm, "end": v(-27.16, 13.32) * mm});
            skLineSegment(sketch, "E1201", {"start": v(-27.16, 13.32) * mm, "end": v(-27.12, 13.2) * mm});
            skLineSegment(sketch, "E1202", {"start": v(-27.12, 13.2) * mm, "end": v(-27.1, 13.07) * mm});
            skLineSegment(sketch, "E1203", {"start": v(-27.1, 13.07) * mm, "end": v(-27.07, 12.95) * mm});
            skLineSegment(sketch, "E1204", {"start": v(-27.07, 12.95) * mm, "end": v(-27.06, 12.82) * mm});
            skLineSegment(sketch, "E1205", {"start": v(-27.06, 12.82) * mm, "end": v(-27.07, 12.68) * mm});
            skLineSegment(sketch, "E1206", {"start": v(-27.07, 12.68) * mm, "end": v(-27.08, 12.55) * mm});
            skLineSegment(sketch, "E1207", {"start": v(-27.08, 12.55) * mm, "end": v(-27.1, 12.42) * mm});
            skLineSegment(sketch, "E1208", {"start": v(-27.1, 12.42) * mm, "end": v(-27.14, 12.29) * mm});
            skLineSegment(sketch, "E1209", {"start": v(-27.14, 12.29) * mm, "end": v(-27.19, 12.16) * mm});
            skLineSegment(sketch, "E1210", {"start": v(-27.19, 12.16) * mm, "end": v(-27.25, 12.03) * mm});
            skLineSegment(sketch, "E1211", {"start": v(-27.25, 12.03) * mm, "end": v(-27.33, 11.92) * mm});
            skLineSegment(sketch, "E1212", {"start": v(-27.33, 11.92) * mm, "end": v(-27.41, 11.81) * mm});
            skLineSegment(sketch, "E1213", {"start": v(-27.41, 11.81) * mm, "end": v(-27.5, 11.71) * mm});
            skLineSegment(sketch, "E1214", {"start": v(-27.5, 11.71) * mm, "end": v(-27.6, 11.62) * mm});
            skLineSegment(sketch, "E1215", {"start": v(-27.6, 11.62) * mm, "end": v(-27.7, 11.54) * mm});
            skLineSegment(sketch, "E1216", {"start": v(-27.7, 11.54) * mm, "end": v(-27.8, 11.47) * mm});
            skLineSegment(sketch, "E1217", {"start": v(-27.8, 11.47) * mm, "end": v(-27.92, 11.4) * mm});
            skLineSegment(sketch, "E1218", {"start": v(-27.92, 11.4) * mm, "end": v(-28.04, 11.36) * mm});
            skLineSegment(sketch, "E1219", {"start": v(-28.04, 11.36) * mm, "end": v(-28.16, 11.31) * mm});
            skLineSegment(sketch, "E1220", {"start": v(-28.16, 11.31) * mm, "end": v(-28.29, 11.28) * mm});
            skLineSegment(sketch, "E1221", {"start": v(-28.29, 11.28) * mm, "end": v(-28.41, 11.26) * mm});
            skLineSegment(sketch, "E1222", {"start": v(-28.41, 11.26) * mm, "end": v(-28.54, 11.25) * mm});
            skLineSegment(sketch, "E1223", {"start": v(-28.54, 11.25) * mm, "end": v(-28.67, 11.25) * mm});
            skLineSegment(sketch, "E1224", {"start": v(-28.67, 11.25) * mm, "end": v(-28.8, 11.27) * mm});
            skLineSegment(sketch, "E1225", {"start": v(-28.8, 11.27) * mm, "end": v(-28.93, 11.3) * mm});
            skLineSegment(sketch, "E1226", {"start": v(-28.93, 11.3) * mm, "end": v(-29.5, 11.5) * mm});
            skLineSegment(sketch, "E1227", {"start": v(-29.5, 11.5) * mm, "end": v(-29.65, 11.5) * mm});
            skLineSegment(sketch, "E1228", {"start": v(-29.65, 11.5) * mm, "end": v(-29.8, 11.46) * mm});
            skLineSegment(sketch, "E1229", {"start": v(-29.8, 11.46) * mm, "end": v(-29.92, 11.37) * mm});
            skLineSegment(sketch, "E1230", {"start": v(-29.92, 11.37) * mm, "end": v(-30, 11.26) * mm});
            skLineSegment(sketch, "E1231", {"start": v(-30, 11.26) * mm, "end": v(-30.17, 10.8) * mm});
            skLineSegment(sketch, "E1232", {"start": v(-30.17, 10.8) * mm, "end": v(-30.32, 10.34) * mm});
            skLineSegment(sketch, "E1233", {"start": v(-30.32, 10.34) * mm, "end": v(-30.34, 10.2) * mm});
            skLineSegment(sketch, "E1234", {"start": v(-30.34, 10.2) * mm, "end": v(-30.3, 10.06) * mm});
            skLineSegment(sketch, "E1235", {"start": v(-30.3, 10.06) * mm, "end": v(-30.22, 9.93) * mm});
            skLineSegment(sketch, "E1236", {"start": v(-30.22, 9.93) * mm, "end": v(-30.1, 9.84) * mm});
            skLineSegment(sketch, "E1237", {"start": v(-30.1, 9.84) * mm, "end": v(-29.52, 9.64) * mm});
            skLineSegment(sketch, "E1238", {"start": v(-29.52, 9.64) * mm, "end": v(-29.4, 9.58) * mm});
            skLineSegment(sketch, "E1239", {"start": v(-29.4, 9.58) * mm, "end": v(-29.3, 9.5) * mm});
            skLineSegment(sketch, "E1240", {"start": v(-29.3, 9.5) * mm, "end": v(-29.2, 9.42) * mm});
            skLineSegment(sketch, "E1241", {"start": v(-29.2, 9.42) * mm, "end": v(-29.1, 9.33) * mm});
            skLineSegment(sketch, "E1242", {"start": v(-29.1, 9.33) * mm, "end": v(-29.02, 9.24) * mm});
            skLineSegment(sketch, "E1243", {"start": v(-29.02, 9.24) * mm, "end": v(-28.95, 9.13) * mm});
            skLineSegment(sketch, "E1244", {"start": v(-28.95, 9.13) * mm, "end": v(-28.88, 9.02) * mm});
            skLineSegment(sketch, "E1245", {"start": v(-28.88, 9.02) * mm, "end": v(-28.82, 8.9) * mm});
            skLineSegment(sketch, "E1246", {"start": v(-28.82, 8.9) * mm, "end": v(-28.77, 8.79) * mm});
            skLineSegment(sketch, "E1247", {"start": v(-28.77, 8.79) * mm, "end": v(-28.74, 8.66) * mm});
            skLineSegment(sketch, "E1248", {"start": v(-28.74, 8.66) * mm, "end": v(-28.7, 8.53) * mm});
            skLineSegment(sketch, "E1249", {"start": v(-28.7, 8.53) * mm, "end": v(-28.7, 8.4) * mm});
            skLineSegment(sketch, "E1250", {"start": v(-28.7, 8.4) * mm, "end": v(-28.68, 8.27) * mm});
            skLineSegment(sketch, "E1251", {"start": v(-28.68, 8.27) * mm, "end": v(-28.69, 8.13) * mm});
            skLineSegment(sketch, "E1252", {"start": v(-28.69, 8.13) * mm, "end": v(-28.7, 8) * mm});
            skLineSegment(sketch, "E1253", {"start": v(-28.7, 8) * mm, "end": v(-28.73, 7.86) * mm});
            skLineSegment(sketch, "E1254", {"start": v(-28.73, 7.86) * mm, "end": v(-28.78, 7.73) * mm});
            skLineSegment(sketch, "E1255", {"start": v(-28.78, 7.73) * mm, "end": v(-28.83, 7.6) * mm});
            skLineSegment(sketch, "E1256", {"start": v(-28.83, 7.6) * mm, "end": v(-28.9, 7.49) * mm});
            skLineSegment(sketch, "E1257", {"start": v(-28.9, 7.49) * mm, "end": v(-28.97, 7.38) * mm});
            skLineSegment(sketch, "E1258", {"start": v(-28.97, 7.38) * mm, "end": v(-29.05, 7.27) * mm});
            skLineSegment(sketch, "E1259", {"start": v(-29.05, 7.27) * mm, "end": v(-29.14, 7.18) * mm});
            skLineSegment(sketch, "E1260", {"start": v(-29.14, 7.18) * mm, "end": v(-29.24, 7.1) * mm});
            skLineSegment(sketch, "E1261", {"start": v(-29.24, 7.1) * mm, "end": v(-29.34, 7.01) * mm});
            skLineSegment(sketch, "E1262", {"start": v(-29.34, 7.01) * mm, "end": v(-29.45, 6.94) * mm});
            skLineSegment(sketch, "E1263", {"start": v(-29.45, 6.94) * mm, "end": v(-29.56, 6.88) * mm});
            skLineSegment(sketch, "E1264", {"start": v(-29.56, 6.88) * mm, "end": v(-29.68, 6.83) * mm});
            skLineSegment(sketch, "E1265", {"start": v(-29.68, 6.83) * mm, "end": v(-29.8, 6.8) * mm});
            skLineSegment(sketch, "E1266", {"start": v(-29.8, 6.8) * mm, "end": v(-29.93, 6.76) * mm});
            skLineSegment(sketch, "E1267", {"start": v(-29.93, 6.76) * mm, "end": v(-30.06, 6.74) * mm});
            skLineSegment(sketch, "E1268", {"start": v(-30.06, 6.74) * mm, "end": v(-30.19, 6.74) * mm});
            skLineSegment(sketch, "E1269", {"start": v(-30.19, 6.74) * mm, "end": v(-30.32, 6.74) * mm});
            skLineSegment(sketch, "E1270", {"start": v(-30.32, 6.74) * mm, "end": v(-30.92, 6.86) * mm});
            skLineSegment(sketch, "E1271", {"start": v(-30.92, 6.86) * mm, "end": v(-31.07, 6.85) * mm});
            skLineSegment(sketch, "E1272", {"start": v(-31.07, 6.85) * mm, "end": v(-31.2, 6.78) * mm});
            skLineSegment(sketch, "E1273", {"start": v(-31.2, 6.78) * mm, "end": v(-31.3, 6.67) * mm});
            skLineSegment(sketch, "E1274", {"start": v(-31.3, 6.67) * mm, "end": v(-31.37, 6.55) * mm});
            skLineSegment(sketch, "E1275", {"start": v(-31.37, 6.55) * mm, "end": v(-31.47, 6.07) * mm});
            skLineSegment(sketch, "E1276", {"start": v(-31.47, 6.07) * mm, "end": v(-31.55, 5.59) * mm});
            skLineSegment(sketch, "E1277", {"start": v(-31.55, 5.59) * mm, "end": v(-31.55, 5.45) * mm});
            skLineSegment(sketch, "E1278", {"start": v(-31.55, 5.45) * mm, "end": v(-31.49, 5.31) * mm});
            skLineSegment(sketch, "E1279", {"start": v(-31.49, 5.31) * mm, "end": v(-31.39, 5.2) * mm});
            skLineSegment(sketch, "E1280", {"start": v(-31.39, 5.2) * mm, "end": v(-31.25, 5.13) * mm});
            skLineSegment(sketch, "E1281", {"start": v(-31.25, 5.13) * mm, "end": v(-30.66, 5.02) * mm});
            skLineSegment(sketch, "E1282", {"start": v(-30.66, 5.02) * mm, "end": v(-30.53, 4.97) * mm});
            skLineSegment(sketch, "E1283", {"start": v(-30.53, 4.97) * mm, "end": v(-30.41, 4.92) * mm});
            skLineSegment(sketch, "E1284", {"start": v(-30.41, 4.92) * mm, "end": v(-30.3, 4.85) * mm});
            skLineSegment(sketch, "E1285", {"start": v(-30.3, 4.85) * mm, "end": v(-30.2, 4.78) * mm});
            skLineSegment(sketch, "E1286", {"start": v(-30.2, 4.78) * mm, "end": v(-30.1, 4.7) * mm});
            skLineSegment(sketch, "E1287", {"start": v(-30.1, 4.7) * mm, "end": v(-30, 4.6) * mm});
            skLineSegment(sketch, "E1288", {"start": v(-30, 4.6) * mm, "end": v(-29.92, 4.5) * mm});
            skLineSegment(sketch, "E1289", {"start": v(-29.92, 4.5) * mm, "end": v(-29.85, 4.4) * mm});
            skLineSegment(sketch, "E1290", {"start": v(-29.85, 4.4) * mm, "end": v(-29.78, 4.3) * mm});
            skLineSegment(sketch, "E1291", {"start": v(-29.78, 4.3) * mm, "end": v(-29.73, 4.17) * mm});
            skLineSegment(sketch, "E1292", {"start": v(-29.73, 4.17) * mm, "end": v(-29.68, 4.05) * mm});
            skLineSegment(sketch, "E1293", {"start": v(-29.68, 4.05) * mm, "end": v(-29.64, 3.92) * mm});
            skLineSegment(sketch, "E1294", {"start": v(-29.64, 3.92) * mm, "end": v(-29.61, 3.8) * mm});
            skLineSegment(sketch, "E1295", {"start": v(-29.61, 3.8) * mm, "end": v(-29.6, 3.66) * mm});
            skLineSegment(sketch, "E1296", {"start": v(-29.6, 3.66) * mm, "end": v(-29.6, 3.52) * mm});
            skLineSegment(sketch, "E1297", {"start": v(-29.6, 3.52) * mm, "end": v(-29.6, 3.38) * mm});
            skLineSegment(sketch, "E1298", {"start": v(-29.6, 3.38) * mm, "end": v(-29.62, 3.25) * mm});
            skLineSegment(sketch, "E1299", {"start": v(-29.62, 3.25) * mm, "end": v(-29.66, 3.12) * mm});
            skLineSegment(sketch, "E1300", {"start": v(-29.66, 3.12) * mm, "end": v(-29.7, 2.99) * mm});
            skLineSegment(sketch, "E1301", {"start": v(-29.7, 2.99) * mm, "end": v(-29.76, 2.87) * mm});
            skLineSegment(sketch, "E1302", {"start": v(-29.76, 2.87) * mm, "end": v(-29.83, 2.75) * mm});
            skLineSegment(sketch, "E1303", {"start": v(-29.83, 2.75) * mm, "end": v(-29.9, 2.64) * mm});
            skLineSegment(sketch, "E1304", {"start": v(-29.9, 2.64) * mm, "end": v(-29.98, 2.54) * mm});
            skLineSegment(sketch, "E1305", {"start": v(-29.98, 2.54) * mm, "end": v(-30.07, 2.45) * mm});
            skLineSegment(sketch, "E1306", {"start": v(-30.07, 2.45) * mm, "end": v(-30.17, 2.36) * mm});
            skLineSegment(sketch, "E1307", {"start": v(-30.17, 2.36) * mm, "end": v(-30.27, 2.29) * mm});
            skLineSegment(sketch, "E1308", {"start": v(-30.27, 2.29) * mm, "end": v(-30.38, 2.22) * mm});
            skLineSegment(sketch, "E1309", {"start": v(-30.38, 2.22) * mm, "end": v(-30.5, 2.16) * mm});
            skLineSegment(sketch, "E1310", {"start": v(-30.5, 2.16) * mm, "end": v(-30.62, 2.11) * mm});
            skLineSegment(sketch, "E1311", {"start": v(-30.62, 2.11) * mm, "end": v(-30.74, 2.07) * mm});
            skLineSegment(sketch, "E1312", {"start": v(-30.74, 2.07) * mm, "end": v(-30.87, 2.05) * mm});
            skLineSegment(sketch, "E1313", {"start": v(-30.87, 2.05) * mm, "end": v(-31, 2.03) * mm});
            skLineSegment(sketch, "E1314", {"start": v(-31, 2.03) * mm, "end": v(-31.6, 2.06) * mm});
            skLineSegment(sketch, "E1315", {"start": v(-31.6, 2.06) * mm, "end": v(-31.75, 2.02) * mm});
            skLineSegment(sketch, "E1316", {"start": v(-31.75, 2.02) * mm, "end": v(-31.88, 1.94) * mm});
            skLineSegment(sketch, "E1317", {"start": v(-31.88, 1.94) * mm, "end": v(-31.97, 1.81) * mm});
            skLineSegment(sketch, "E1318", {"start": v(-31.97, 1.81) * mm, "end": v(-32, 1.68) * mm});
            skLineSegment(sketch, "E1319", {"start": v(-32, 1.68) * mm, "end": v(-32.03, 1.2) * mm});
            skLineSegment(sketch, "E1320", {"start": v(-32.03, 1.2) * mm, "end": v(-32.04, 0.7) * mm});
            skLineSegment(sketch, "E1321", {"start": v(-32.04, 0.7) * mm, "end": v(-32.01, 0.57) * mm});
            skLineSegment(sketch, "E1322", {"start": v(-32.01, 0.57) * mm, "end": v(-31.93, 0.44) * mm});
            skLineSegment(sketch, "E1323", {"start": v(-31.93, 0.44) * mm, "end": v(-31.82, 0.35) * mm});
            skLineSegment(sketch, "E1324", {"start": v(-31.82, 0.35) * mm, "end": v(-31.67, 0.3) * mm});
            skLineSegment(sketch, "E1325", {"start": v(-31.67, 0.3) * mm, "end": v(-31.07, 0.28) * mm});
            skLineSegment(sketch, "E1326", {"start": v(-31.07, 0.28) * mm, "end": v(-30.94, 0.25) * mm});
            skLineSegment(sketch, "E1327", {"start": v(-30.94, 0.25) * mm, "end": v(-30.81, 0.22) * mm});
            skLineSegment(sketch, "E1328", {"start": v(-30.81, 0.22) * mm, "end": v(-30.7, 0.17) * mm});
            skLineSegment(sketch, "E1329", {"start": v(-30.7, 0.17) * mm, "end": v(-30.58, 0.11) * mm});
            skLineSegment(sketch, "E1330", {"start": v(-30.58, 0.11) * mm, "end": v(-30.47, 0.05) * mm});
            skLineSegment(sketch, "E1331", {"start": v(-30.47, 0.05) * mm, "end": v(-30.36, -0.03) * mm});
            skLineSegment(sketch, "E1332", {"start": v(-30.36, -0.03) * mm, "end": v(-30.27, -0.11) * mm});
            skLineSegment(sketch, "E1333", {"start": v(-30.27, -0.11) * mm, "end": v(-30.18, -0.2) * mm});
            skLineSegment(sketch, "E1334", {"start": v(-30.18, -0.2) * mm, "end": v(-30.1, -0.3) * mm});
            skLineSegment(sketch, "E1335", {"start": v(-30.1, -0.3) * mm, "end": v(-30.02, -0.41) * mm});
            skLineSegment(sketch, "E1336", {"start": v(-30.02, -0.41) * mm, "end": v(-29.95, -0.53) * mm});
            skLineSegment(sketch, "E1337", {"start": v(-29.95, -0.53) * mm, "end": v(-29.9, -0.65) * mm});
            skLineSegment(sketch, "E1338", {"start": v(-29.9, -0.65) * mm, "end": v(-29.85, -0.77) * mm});
            skLineSegment(sketch, "E1339", {"start": v(-29.85, -0.77) * mm, "end": v(-29.81, -0.9) * mm});
            skLineSegment(sketch, "E1340", {"start": v(-29.81, -0.9) * mm, "end": v(-29.79, -1.04) * mm});
            skLineSegment(sketch, "E1341", {"start": v(-29.79, -1.04) * mm, "end": v(-29.77, -1.17) * mm});
            skLineSegment(sketch, "E1342", {"start": v(-29.77, -1.17) * mm, "end": v(-29.78, -1.31) * mm});
            skLineSegment(sketch, "E1343", {"start": v(-29.78, -1.31) * mm, "end": v(-29.8, -1.45) * mm});
            skLineSegment(sketch, "E1344", {"start": v(-29.8, -1.45) * mm, "end": v(-29.82, -1.58) * mm});
            skLineSegment(sketch, "E1345", {"start": v(-29.82, -1.58) * mm, "end": v(-29.86, -1.7) * mm});
            skLineSegment(sketch, "E1346", {"start": v(-29.86, -1.7) * mm, "end": v(-29.9, -1.83) * mm});
            skLineSegment(sketch, "E1347", {"start": v(-29.9, -1.83) * mm, "end": v(-29.96, -1.95) * mm});
            skLineSegment(sketch, "E1348", {"start": v(-29.96, -1.95) * mm, "end": v(-30.03, -2.06) * mm});
            skLineSegment(sketch, "E1349", {"start": v(-30.03, -2.06) * mm, "end": v(-30.1, -2.17) * mm});
            skLineSegment(sketch, "E1350", {"start": v(-30.1, -2.17) * mm, "end": v(-30.18, -2.27) * mm});
            skLineSegment(sketch, "E1351", {"start": v(-30.18, -2.27) * mm, "end": v(-30.27, -2.36) * mm});
            skLineSegment(sketch, "E1352", {"start": v(-30.27, -2.36) * mm, "end": v(-30.37, -2.44) * mm});
            skLineSegment(sketch, "E1353", {"start": v(-30.37, -2.44) * mm, "end": v(-30.47, -2.52) * mm});
            skLineSegment(sketch, "E1354", {"start": v(-30.47, -2.52) * mm, "end": v(-30.59, -2.59) * mm});
            skLineSegment(sketch, "E1355", {"start": v(-30.59, -2.59) * mm, "end": v(-30.7, -2.64) * mm});
            skLineSegment(sketch, "E1356", {"start": v(-30.7, -2.64) * mm, "end": v(-30.82, -2.69) * mm});
            skLineSegment(sketch, "E1357", {"start": v(-30.82, -2.69) * mm, "end": v(-30.95, -2.72) * mm});
            skLineSegment(sketch, "E1358", {"start": v(-30.95, -2.72) * mm, "end": v(-31.56, -2.79) * mm});
            skLineSegment(sketch, "E1359", {"start": v(-31.56, -2.79) * mm, "end": v(-31.7, -2.85) * mm});
            skLineSegment(sketch, "E1360", {"start": v(-31.7, -2.85) * mm, "end": v(-31.8, -2.95) * mm});
            skLineSegment(sketch, "E1361", {"start": v(-31.8, -2.95) * mm, "end": v(-31.87, -3.09) * mm});
            skLineSegment(sketch, "E1362", {"start": v(-31.87, -3.09) * mm, "end": v(-31.9, -3.22) * mm});
            skLineSegment(sketch, "E1363", {"start": v(-31.9, -3.22) * mm, "end": v(-31.84, -3.7) * mm});
            skLineSegment(sketch, "E1364", {"start": v(-31.84, -3.7) * mm, "end": v(-31.78, -4.2) * mm});
            skLineSegment(sketch, "E1365", {"start": v(-31.78, -4.2) * mm, "end": v(-31.73, -4.32) * mm});
            skLineSegment(sketch, "E1366", {"start": v(-31.73, -4.32) * mm, "end": v(-31.63, -4.44) * mm});
            skLineSegment(sketch, "E1367", {"start": v(-31.63, -4.44) * mm, "end": v(-31.5, -4.51) * mm});
            skLineSegment(sketch, "E1368", {"start": v(-31.5, -4.51) * mm, "end": v(-31.35, -4.54) * mm});
            skLineSegment(sketch, "E1369", {"start": v(-31.35, -4.54) * mm, "end": v(-30.75, -4.47) * mm});
            skLineSegment(sketch, "E1370", {"start": v(-30.75, -4.47) * mm, "end": v(-30.62, -4.47) * mm});
            skLineSegment(sketch, "E1371", {"start": v(-30.62, -4.47) * mm, "end": v(-30.49, -4.49) * mm});
            skLineSegment(sketch, "E1372", {"start": v(-30.49, -4.49) * mm, "end": v(-30.36, -4.52) * mm});
            skLineSegment(sketch, "E1373", {"start": v(-30.36, -4.52) * mm, "end": v(-30.24, -4.56) * mm});
            skLineSegment(sketch, "E1374", {"start": v(-30.24, -4.56) * mm, "end": v(-30.12, -4.6) * mm});
            skLineSegment(sketch, "E1375", {"start": v(-30.12, -4.6) * mm, "end": v(-30, -4.66) * mm});
            skLineSegment(sketch, "E1376", {"start": v(-30, -4.66) * mm, "end": v(-29.9, -4.73) * mm});
            skLineSegment(sketch, "E1377", {"start": v(-29.9, -4.73) * mm, "end": v(-29.8, -4.81) * mm});
            skLineSegment(sketch, "E1378", {"start": v(-29.8, -4.81) * mm, "end": v(-29.7, -4.9) * mm});
            skLineSegment(sketch, "E1379", {"start": v(-29.7, -4.9) * mm, "end": v(-29.61, -5) * mm});
            skLineSegment(sketch, "E1380", {"start": v(-29.61, -5) * mm, "end": v(-29.53, -5.1) * mm});
            skLineSegment(sketch, "E1381", {"start": v(-29.53, -5.1) * mm, "end": v(-29.45, -5.2) * mm});
            skLineSegment(sketch, "E1382", {"start": v(-29.45, -5.2) * mm, "end": v(-29.39, -5.32) * mm});
            skLineSegment(sketch, "E1383", {"start": v(-29.39, -5.32) * mm, "end": v(-29.33, -5.44) * mm});
            skLineSegment(sketch, "E1384", {"start": v(-29.33, -5.44) * mm, "end": v(-29.29, -5.57) * mm});
            skLineSegment(sketch, "E1385", {"start": v(-29.29, -5.57) * mm, "end": v(-29.25, -5.7) * mm});
            skLineSegment(sketch, "E1386", {"start": v(-29.25, -5.7) * mm, "end": v(-29.23, -5.84) * mm});
            skLineSegment(sketch, "E1387", {"start": v(-29.23, -5.84) * mm, "end": v(-29.23, -5.98) * mm});
            skLineSegment(sketch, "E1388", {"start": v(-29.23, -5.98) * mm, "end": v(-29.23, -6.11) * mm});
            skLineSegment(sketch, "E1389", {"start": v(-29.23, -6.11) * mm, "end": v(-29.25, -6.25) * mm});
            skLineSegment(sketch, "E1390", {"start": v(-29.25, -6.25) * mm, "end": v(-29.28, -6.38) * mm});
            skLineSegment(sketch, "E1391", {"start": v(-29.28, -6.38) * mm, "end": v(-29.32, -6.5) * mm});
            skLineSegment(sketch, "E1392", {"start": v(-29.32, -6.5) * mm, "end": v(-29.36, -6.62) * mm});
            skLineSegment(sketch, "E1393", {"start": v(-29.36, -6.62) * mm, "end": v(-29.42, -6.74) * mm});
            skLineSegment(sketch, "E1394", {"start": v(-29.42, -6.74) * mm, "end": v(-29.49, -6.85) * mm});
            skLineSegment(sketch, "E1395", {"start": v(-29.49, -6.85) * mm, "end": v(-29.56, -6.96) * mm});
            skLineSegment(sketch, "E1396", {"start": v(-29.56, -6.96) * mm, "end": v(-29.65, -7.05) * mm});
            skLineSegment(sketch, "E1397", {"start": v(-29.65, -7.05) * mm, "end": v(-29.74, -7.14) * mm});
            skLineSegment(sketch, "E1398", {"start": v(-29.74, -7.14) * mm, "end": v(-29.84, -7.23) * mm});
            skLineSegment(sketch, "E1399", {"start": v(-29.84, -7.23) * mm, "end": v(-29.94, -7.3) * mm});
            skLineSegment(sketch, "E1400", {"start": v(-29.94, -7.3) * mm, "end": v(-30.06, -7.36) * mm});
            skLineSegment(sketch, "E1401", {"start": v(-30.06, -7.36) * mm, "end": v(-30.18, -7.42) * mm});
            skLineSegment(sketch, "E1402", {"start": v(-30.18, -7.42) * mm, "end": v(-30.77, -7.57) * mm});
            skLineSegment(sketch, "E1403", {"start": v(-30.77, -7.57) * mm, "end": v(-30.9, -7.65) * mm});
            skLineSegment(sketch, "E1404", {"start": v(-30.9, -7.65) * mm, "end": v(-30.99, -7.77) * mm});
            skLineSegment(sketch, "E1405", {"start": v(-30.99, -7.77) * mm, "end": v(-31.03, -7.92) * mm});
            skLineSegment(sketch, "E1406", {"start": v(-31.03, -7.92) * mm, "end": v(-31.03, -8.05) * mm});
            skLineSegment(sketch, "E1407", {"start": v(-31.03, -8.05) * mm, "end": v(-30.9, -8.53) * mm});
            skLineSegment(sketch, "E1408", {"start": v(-30.9, -8.53) * mm, "end": v(-30.77, -9) * mm});
            skLineSegment(sketch, "E1409", {"start": v(-30.77, -9) * mm, "end": v(-30.7, -9.11) * mm});
            skLineSegment(sketch, "E1410", {"start": v(-30.7, -9.11) * mm, "end": v(-30.59, -9.21) * mm});
            skLineSegment(sketch, "E1411", {"start": v(-30.59, -9.21) * mm, "end": v(-30.45, -9.27) * mm});
            skLineSegment(sketch, "E1412", {"start": v(-30.45, -9.27) * mm, "end": v(-30.3, -9.27) * mm});
            skLineSegment(sketch, "E1413", {"start": v(-30.3, -9.27) * mm, "end": v(-29.71, -9.1) * mm});
            skLineSegment(sketch, "E1414", {"start": v(-29.71, -9.1) * mm, "end": v(-29.58, -9.1) * mm});
            skLineSegment(sketch, "E1415", {"start": v(-29.58, -9.1) * mm, "end": v(-29.45, -9.1) * mm});
            skLineSegment(sketch, "E1416", {"start": v(-29.45, -9.1) * mm, "end": v(-29.32, -9.1) * mm});
            skLineSegment(sketch, "E1417", {"start": v(-29.32, -9.1) * mm, "end": v(-29.2, -9.12) * mm});
            skLineSegment(sketch, "E1418", {"start": v(-29.2, -9.12) * mm, "end": v(-29.07, -9.15) * mm});
            skLineSegment(sketch, "E1419", {"start": v(-29.07, -9.15) * mm, "end": v(-28.95, -9.2) * mm});
            skLineSegment(sketch, "E1420", {"start": v(-28.95, -9.2) * mm, "end": v(-28.83, -9.24) * mm});
            skLineSegment(sketch, "E1421", {"start": v(-28.83, -9.24) * mm, "end": v(-28.72, -9.3) * mm});
            skLineSegment(sketch, "E1422", {"start": v(-28.72, -9.3) * mm, "end": v(-28.6, -9.37) * mm});
            skLineSegment(sketch, "E1423", {"start": v(-28.6, -9.37) * mm, "end": v(-28.5, -9.45) * mm});
            skLineSegment(sketch, "E1424", {"start": v(-28.5, -9.45) * mm, "end": v(-28.4, -9.54) * mm});
            skLineSegment(sketch, "E1425", {"start": v(-28.4, -9.54) * mm, "end": v(-28.32, -9.64) * mm});
            skLineSegment(sketch, "E1426", {"start": v(-28.32, -9.64) * mm, "end": v(-28.24, -9.74) * mm});
            skLineSegment(sketch, "E1427", {"start": v(-28.24, -9.74) * mm, "end": v(-28.16, -9.86) * mm});
            skLineSegment(sketch, "E1428", {"start": v(-28.16, -9.86) * mm, "end": v(-28.1, -9.98) * mm});
            skLineSegment(sketch, "E1429", {"start": v(-28.1, -9.98) * mm, "end": v(-28.04, -10.1) * mm});
            skLineSegment(sketch, "E1430", {"start": v(-28.04, -10.1) * mm, "end": v(-28, -10.24) * mm});
            skLineSegment(sketch, "E1431", {"start": v(-28, -10.24) * mm, "end": v(-27.98, -10.37) * mm});
            skLineSegment(sketch, "E1432", {"start": v(-27.98, -10.37) * mm, "end": v(-27.96, -10.5) * mm});
            skLineSegment(sketch, "E1433", {"start": v(-27.96, -10.5) * mm, "end": v(-27.96, -10.64) * mm});
            skLineSegment(sketch, "E1434", {"start": v(-27.96, -10.64) * mm, "end": v(-27.97, -10.77) * mm});
            skLineSegment(sketch, "E1435", {"start": v(-27.97, -10.77) * mm, "end": v(-27.99, -10.9) * mm});
            skLineSegment(sketch, "E1436", {"start": v(-27.99, -10.9) * mm, "end": v(-28.01, -11.03) * mm});
            skLineSegment(sketch, "E1437", {"start": v(-28.01, -11.03) * mm, "end": v(-28.05, -11.15) * mm});
            skLineSegment(sketch, "E1438", {"start": v(-28.05, -11.15) * mm, "end": v(-28.1, -11.27) * mm});
            skLineSegment(sketch, "E1439", {"start": v(-28.1, -11.27) * mm, "end": v(-28.16, -11.39) * mm});
            skLineSegment(sketch, "E1440", {"start": v(-28.16, -11.39) * mm, "end": v(-28.23, -11.5) * mm});
            skLineSegment(sketch, "E1441", {"start": v(-28.23, -11.5) * mm, "end": v(-28.3, -11.6) * mm});
            skLineSegment(sketch, "E1442", {"start": v(-28.3, -11.6) * mm, "end": v(-28.39, -11.7) * mm});
            skLineSegment(sketch, "E1443", {"start": v(-28.39, -11.7) * mm, "end": v(-28.48, -11.78) * mm});
            skLineSegment(sketch, "E1444", {"start": v(-28.48, -11.78) * mm, "end": v(-28.59, -11.86) * mm});
            skLineSegment(sketch, "E1445", {"start": v(-28.59, -11.86) * mm, "end": v(-28.7, -11.94) * mm});
            skLineSegment(sketch, "E1446", {"start": v(-28.7, -11.94) * mm, "end": v(-29.25, -12.18) * mm});
            skLineSegment(sketch, "E1447", {"start": v(-29.25, -12.18) * mm, "end": v(-29.37, -12.28) * mm});
            skLineSegment(sketch, "E1448", {"start": v(-29.37, -12.28) * mm, "end": v(-29.44, -12.41) * mm});
            skLineSegment(sketch, "E1449", {"start": v(-29.44, -12.41) * mm, "end": v(-29.47, -12.56) * mm});
            skLineSegment(sketch, "E1450", {"start": v(-29.47, -12.56) * mm, "end": v(-29.44, -12.7) * mm});
            skLineSegment(sketch, "E1451", {"start": v(-29.44, -12.7) * mm, "end": v(-29.25, -13.15) * mm});
            skLineSegment(sketch, "E1452", {"start": v(-29.25, -13.15) * mm, "end": v(-29.04, -13.59) * mm});
            skLineSegment(sketch, "E1453", {"start": v(-29.04, -13.59) * mm, "end": v(-28.96, -13.7) * mm});
            skLineSegment(sketch, "E1454", {"start": v(-28.96, -13.7) * mm, "end": v(-28.83, -13.78) * mm});
            skLineSegment(sketch, "E1455", {"start": v(-28.83, -13.78) * mm, "end": v(-28.68, -13.8) * mm});
            skLineSegment(sketch, "E1456", {"start": v(-28.68, -13.8) * mm, "end": v(-28.53, -13.8) * mm});
            skLineSegment(sketch, "E1457", {"start": v(-28.53, -13.8) * mm, "end": v(-27.98, -13.54) * mm});
            skLineSegment(sketch, "E1458", {"start": v(-27.98, -13.54) * mm, "end": v(-27.85, -13.5) * mm});
            skLineSegment(sketch, "E1459", {"start": v(-27.85, -13.5) * mm, "end": v(-27.72, -13.48) * mm});
            skLineSegment(sketch, "E1460", {"start": v(-27.72, -13.48) * mm, "end": v(-27.6, -13.47) * mm});
            skLineSegment(sketch, "E1461", {"start": v(-27.6, -13.47) * mm, "end": v(-27.47, -13.47) * mm});
            skLineSegment(sketch, "E1462", {"start": v(-27.47, -13.47) * mm, "end": v(-27.34, -13.48) * mm});
            skLineSegment(sketch, "E1463", {"start": v(-27.34, -13.48) * mm, "end": v(-27.21, -13.5) * mm});
            skLineSegment(sketch, "E1464", {"start": v(-27.21, -13.5) * mm, "end": v(-27.09, -13.54) * mm});
            skLineSegment(sketch, "E1465", {"start": v(-27.09, -13.54) * mm, "end": v(-26.97, -13.58) * mm});
            skLineSegment(sketch, "E1466", {"start": v(-26.97, -13.58) * mm, "end": v(-26.85, -13.63) * mm});
            skLineSegment(sketch, "E1467", {"start": v(-26.85, -13.63) * mm, "end": v(-26.73, -13.7) * mm});
            skLineSegment(sketch, "E1468", {"start": v(-26.73, -13.7) * mm, "end": v(-26.62, -13.77) * mm});
            skLineSegment(sketch, "E1469", {"start": v(-26.62, -13.77) * mm, "end": v(-26.52, -13.85) * mm});
            skLineSegment(sketch, "E1470", {"start": v(-26.52, -13.85) * mm, "end": v(-26.42, -13.94) * mm});
            skLineSegment(sketch, "E1471", {"start": v(-26.42, -13.94) * mm, "end": v(-26.33, -14.04) * mm});
            skLineSegment(sketch, "E1472", {"start": v(-26.33, -14.04) * mm, "end": v(-26.25, -14.15) * mm});
            skLineSegment(sketch, "E1473", {"start": v(-26.25, -14.15) * mm, "end": v(-26.18, -14.27) * mm});
            skLineSegment(sketch, "E1474", {"start": v(-26.18, -14.27) * mm, "end": v(-26.12, -14.4) * mm});
            skLineSegment(sketch, "E1475", {"start": v(-26.12, -14.4) * mm, "end": v(-26.07, -14.52) * mm});
            skLineSegment(sketch, "E1476", {"start": v(-26.07, -14.52) * mm, "end": v(-26.04, -14.65) * mm});
            skLineSegment(sketch, "E1477", {"start": v(-26.04, -14.65) * mm, "end": v(-26.01, -14.78) * mm});
            skLineSegment(sketch, "E1478", {"start": v(-26.01, -14.78) * mm, "end": v(-26, -14.91) * mm});
            skLineSegment(sketch, "E1479", {"start": v(-26, -14.91) * mm, "end": v(-26, -15.05) * mm});
            skLineSegment(sketch, "E1480", {"start": v(-26, -15.05) * mm, "end": v(-26, -15.18) * mm});
            skLineSegment(sketch, "E1481", {"start": v(-26, -15.18) * mm, "end": v(-26.03, -15.3) * mm});
            skLineSegment(sketch, "E1482", {"start": v(-26.03, -15.3) * mm, "end": v(-26.06, -15.43) * mm});
            skLineSegment(sketch, "E1483", {"start": v(-26.06, -15.43) * mm, "end": v(-26.1, -15.55) * mm});
            skLineSegment(sketch, "E1484", {"start": v(-26.1, -15.55) * mm, "end": v(-26.15, -15.67) * mm});
            skLineSegment(sketch, "E1485", {"start": v(-26.15, -15.67) * mm, "end": v(-26.2, -15.78) * mm});
            skLineSegment(sketch, "E1486", {"start": v(-26.2, -15.78) * mm, "end": v(-26.28, -15.9) * mm});
            skLineSegment(sketch, "E1487", {"start": v(-26.28, -15.9) * mm, "end": v(-26.36, -16) * mm});
            skLineSegment(sketch, "E1488", {"start": v(-26.36, -16) * mm, "end": v(-26.45, -16.09) * mm});
            skLineSegment(sketch, "E1489", {"start": v(-26.45, -16.09) * mm, "end": v(-26.54, -16.18) * mm});
            skLineSegment(sketch, "E1490", {"start": v(-26.54, -16.18) * mm, "end": v(-27.06, -16.5) * mm});
            skLineSegment(sketch, "E1491", {"start": v(-27.06, -16.5) * mm, "end": v(-27.16, -16.62) * mm});
            skLineSegment(sketch, "E1492", {"start": v(-27.16, -16.62) * mm, "end": v(-27.2, -16.76) * mm});
            skLineSegment(sketch, "E1493", {"start": v(-27.2, -16.76) * mm, "end": v(-27.2, -16.91) * mm});
            skLineSegment(sketch, "E1494", {"start": v(-27.2, -16.91) * mm, "end": v(-27.16, -17.04) * mm});
            skLineSegment(sketch, "E1495", {"start": v(-27.16, -17.04) * mm, "end": v(-26.9, -17.46) * mm});
            skLineSegment(sketch, "E1496", {"start": v(-26.9, -17.46) * mm, "end": v(-26.63, -17.86) * mm});
            skLineSegment(sketch, "E1497", {"start": v(-26.63, -17.86) * mm, "end": v(-26.53, -17.95) * mm});
            skLineSegment(sketch, "E1498", {"start": v(-26.53, -17.95) * mm, "end": v(-26.4, -18.02) * mm});
            skLineSegment(sketch, "E1499", {"start": v(-26.4, -18.02) * mm, "end": v(-26.24, -18.03) * mm});
            skLineSegment(sketch, "E1500", {"start": v(-26.24, -18.03) * mm, "end": v(-26.1, -17.98) * mm});
            skLineSegment(sketch, "E1501", {"start": v(-26.1, -17.98) * mm, "end": v(-25.6, -17.65) * mm});
            skLineSegment(sketch, "E1502", {"start": v(-25.6, -17.65) * mm, "end": v(-25.47, -17.6) * mm});
            skLineSegment(sketch, "E1503", {"start": v(-25.47, -17.6) * mm, "end": v(-25.35, -17.55) * mm});
            skLineSegment(sketch, "E1504", {"start": v(-25.35, -17.55) * mm, "end": v(-25.22, -17.52) * mm});
            skLineSegment(sketch, "E1505", {"start": v(-25.22, -17.52) * mm, "end": v(-25.1, -17.5) * mm});
            skLineSegment(sketch, "E1506", {"start": v(-25.1, -17.5) * mm, "end": v(-24.97, -17.5) * mm});
            skLineSegment(sketch, "E1507", {"start": v(-24.97, -17.5) * mm, "end": v(-24.84, -17.5) * mm});
            skLineSegment(sketch, "E1508", {"start": v(-24.84, -17.5) * mm, "end": v(-24.7, -17.51) * mm});
            skLineSegment(sketch, "E1509", {"start": v(-24.7, -17.51) * mm, "end": v(-24.58, -17.54) * mm});
            skLineSegment(sketch, "E1510", {"start": v(-24.58, -17.54) * mm, "end": v(-24.46, -17.57) * mm});
            skLineSegment(sketch, "E1511", {"start": v(-24.46, -17.57) * mm, "end": v(-24.34, -17.62) * mm});
            skLineSegment(sketch, "E1512", {"start": v(-24.34, -17.62) * mm, "end": v(-24.22, -17.67) * mm});
            skLineSegment(sketch, "E1513", {"start": v(-24.22, -17.67) * mm, "end": v(-24.1, -17.74) * mm});
            skLineSegment(sketch, "E1514", {"start": v(-24.1, -17.74) * mm, "end": v(-24, -17.81) * mm});
            skLineSegment(sketch, "E1515", {"start": v(-24, -17.81) * mm, "end": v(-23.89, -17.9) * mm});
            skLineSegment(sketch, "E1516", {"start": v(-23.89, -17.9) * mm, "end": v(-23.79, -18) * mm});
            skLineSegment(sketch, "E1517", {"start": v(-23.79, -18) * mm, "end": v(-23.7, -18.1) * mm});
            skLineSegment(sketch, "E1518", {"start": v(-23.7, -18.1) * mm, "end": v(-23.62, -18.21) * mm});
            skLineSegment(sketch, "E1519", {"start": v(-23.62, -18.21) * mm, "end": v(-23.55, -18.33) * mm});
            skLineSegment(sketch, "E1520", {"start": v(-23.55, -18.33) * mm, "end": v(-23.5, -18.46) * mm});
            skLineSegment(sketch, "E1521", {"start": v(-23.5, -18.46) * mm, "end": v(-23.46, -18.58) * mm});
            skLineSegment(sketch, "E1522", {"start": v(-23.46, -18.58) * mm, "end": v(-23.42, -18.7) * mm});
            skLineSegment(sketch, "E1523", {"start": v(-23.42, -18.7) * mm, "end": v(-23.4, -18.84) * mm});
            skLineSegment(sketch, "E1524", {"start": v(-23.4, -18.84) * mm, "end": v(-23.4, -18.97) * mm});
            skLineSegment(sketch, "E1525", {"start": v(-23.4, -18.97) * mm, "end": v(-23.4, -19.1) * mm});
            skLineSegment(sketch, "E1526", {"start": v(-23.4, -19.1) * mm, "end": v(-23.4, -19.23) * mm});
            skLineSegment(sketch, "E1527", {"start": v(-23.4, -19.23) * mm, "end": v(-23.42, -19.35) * mm});
            skLineSegment(sketch, "E1528", {"start": v(-23.42, -19.35) * mm, "end": v(-23.45, -19.48) * mm});
            skLineSegment(sketch, "E1529", {"start": v(-23.45, -19.48) * mm, "end": v(-23.5, -19.6) * mm});
            skLineSegment(sketch, "E1530", {"start": v(-23.5, -19.6) * mm, "end": v(-23.55, -19.72) * mm});
            skLineSegment(sketch, "E1531", {"start": v(-23.55, -19.72) * mm, "end": v(-23.61, -19.83) * mm});
            skLineSegment(sketch, "E1532", {"start": v(-23.61, -19.83) * mm, "end": v(-23.68, -19.94) * mm});
            skLineSegment(sketch, "E1533", {"start": v(-23.68, -19.94) * mm, "end": v(-23.77, -20.04) * mm});
            skLineSegment(sketch, "E1534", {"start": v(-23.77, -20.04) * mm, "end": v(-24.22, -20.44) * mm});
            skLineSegment(sketch, "E1535", {"start": v(-24.22, -20.44) * mm, "end": v(-24.3, -20.57) * mm});
            skLineSegment(sketch, "E1536", {"start": v(-24.3, -20.57) * mm, "end": v(-24.33, -20.72) * mm});
            skLineSegment(sketch, "E1537", {"start": v(-24.33, -20.72) * mm, "end": v(-24.31, -20.87) * mm});
            skLineSegment(sketch, "E1538", {"start": v(-24.31, -20.87) * mm, "end": v(-24.25, -20.99) * mm});
            skLineSegment(sketch, "E1539", {"start": v(-24.25, -20.99) * mm, "end": v(-23.93, -21.36) * mm});
            skLineSegment(sketch, "E1540", {"start": v(-23.93, -21.36) * mm, "end": v(-23.6, -21.72) * mm});
            skLineSegment(sketch, "E1541", {"start": v(-23.6, -21.72) * mm, "end": v(-23.49, -21.8) * mm});
            skLineSegment(sketch, "E1542", {"start": v(-23.49, -21.8) * mm, "end": v(-23.34, -21.83) * mm});
            skLineSegment(sketch, "E1543", {"start": v(-23.34, -21.83) * mm, "end": v(-23.19, -21.82) * mm});
            skLineSegment(sketch, "E1544", {"start": v(-23.19, -21.82) * mm, "end": v(-23.05, -21.76) * mm});
            skLineSegment(sketch, "E1545", {"start": v(-23.05, -21.76) * mm, "end": v(-22.6, -21.35) * mm});
            skLineSegment(sketch, "E1546", {"start": v(-22.6, -21.35) * mm, "end": v(-22.5, -21.28) * mm});
            skLineSegment(sketch, "E1547", {"start": v(-22.5, -21.28) * mm, "end": v(-22.38, -21.22) * mm});
            skLineSegment(sketch, "E1548", {"start": v(-22.38, -21.22) * mm, "end": v(-22.26, -21.17) * mm});
            skLineSegment(sketch, "E1549", {"start": v(-22.26, -21.17) * mm, "end": v(-22.13, -21.13) * mm});
            skLineSegment(sketch, "E1550", {"start": v(-22.13, -21.13) * mm, "end": v(-22, -21.1) * mm});
            skLineSegment(sketch, "E1551", {"start": v(-22, -21.1) * mm, "end": v(-21.88, -21.08) * mm});
            skLineSegment(sketch, "E1552", {"start": v(-21.88, -21.08) * mm, "end": v(-21.75, -21.08) * mm});
            skLineSegment(sketch, "E1553", {"start": v(-21.75, -21.08) * mm, "end": v(-21.62, -21.08) * mm});
            skLineSegment(sketch, "E1554", {"start": v(-21.62, -21.08) * mm, "end": v(-21.5, -21.1) * mm});
            skLineSegment(sketch, "E1555", {"start": v(-21.5, -21.1) * mm, "end": v(-21.37, -21.12) * mm});
            skLineSegment(sketch, "E1556", {"start": v(-21.37, -21.12) * mm, "end": v(-21.24, -21.16) * mm});
            skLineSegment(sketch, "E1557", {"start": v(-21.24, -21.16) * mm, "end": v(-21.12, -21.2) * mm});
            skLineSegment(sketch, "E1558", {"start": v(-21.12, -21.2) * mm, "end": v(-21, -21.27) * mm});
            skLineSegment(sketch, "E1559", {"start": v(-21, -21.27) * mm, "end": v(-20.88, -21.33) * mm});
            skLineSegment(sketch, "E1560", {"start": v(-20.88, -21.33) * mm, "end": v(-20.77, -21.41) * mm});
            skLineSegment(sketch, "E1561", {"start": v(-20.77, -21.41) * mm, "end": v(-20.66, -21.5) * mm});
            skLineSegment(sketch, "E1562", {"start": v(-20.66, -21.5) * mm, "end": v(-20.57, -21.6) * mm});
            skLineSegment(sketch, "E1563", {"start": v(-20.57, -21.6) * mm, "end": v(-20.49, -21.71) * mm});
            skLineSegment(sketch, "E1564", {"start": v(-20.49, -21.71) * mm, "end": v(-20.41, -21.83) * mm});
            skLineSegment(sketch, "E1565", {"start": v(-20.41, -21.83) * mm, "end": v(-20.35, -21.94) * mm});
            skLineSegment(sketch, "E1566", {"start": v(-20.35, -21.94) * mm, "end": v(-20.3, -22.07) * mm});
            skLineSegment(sketch, "E1567", {"start": v(-20.3, -22.07) * mm, "end": v(-20.26, -22.2) * mm});
            skLineSegment(sketch, "E1568", {"start": v(-20.26, -22.2) * mm, "end": v(-20.23, -22.32) * mm});
            skLineSegment(sketch, "E1569", {"start": v(-20.23, -22.32) * mm, "end": v(-20.2, -22.45) * mm});
            skLineSegment(sketch, "E1570", {"start": v(-20.2, -22.45) * mm, "end": v(-20.2, -22.57) * mm});
            skLineSegment(sketch, "E1571", {"start": v(-20.2, -22.57) * mm, "end": v(-20.2, -22.7) * mm});
            skLineSegment(sketch, "E1572", {"start": v(-20.2, -22.7) * mm, "end": v(-20.21, -22.83) * mm});
            skLineSegment(sketch, "E1573", {"start": v(-20.21, -22.83) * mm, "end": v(-20.23, -22.96) * mm});
            skLineSegment(sketch, "E1574", {"start": v(-20.23, -22.96) * mm, "end": v(-20.27, -23.08) * mm});
            skLineSegment(sketch, "E1575", {"start": v(-20.27, -23.08) * mm, "end": v(-20.31, -23.2) * mm});
            skLineSegment(sketch, "E1576", {"start": v(-20.31, -23.2) * mm, "end": v(-20.37, -23.32) * mm});
            skLineSegment(sketch, "E1577", {"start": v(-20.37, -23.32) * mm, "end": v(-20.44, -23.43) * mm});
            skLineSegment(sketch, "E1578", {"start": v(-20.44, -23.43) * mm, "end": v(-20.83, -23.9) * mm});
            skLineSegment(sketch, "E1579", {"start": v(-20.83, -23.9) * mm, "end": v(-20.88, -24.04) * mm});
            skLineSegment(sketch, "E1580", {"start": v(-20.88, -24.04) * mm, "end": v(-20.9, -24.2) * mm});
            skLineSegment(sketch, "E1581", {"start": v(-20.9, -24.2) * mm, "end": v(-20.85, -24.34) * mm});
            skLineSegment(sketch, "E1582", {"start": v(-20.85, -24.34) * mm, "end": v(-20.77, -24.45) * mm});
            skLineSegment(sketch, "E1583", {"start": v(-20.77, -24.45) * mm, "end": v(-20.4, -24.76) * mm});
            skLineSegment(sketch, "E1584", {"start": v(-20.4, -24.76) * mm, "end": v(-20.01, -25.07) * mm});
            skLineSegment(sketch, "E1585", {"start": v(-20.01, -25.07) * mm, "end": v(-19.9, -25.12) * mm});
            skLineSegment(sketch, "E1586", {"start": v(-19.9, -25.12) * mm, "end": v(-19.74, -25.14) * mm});
            skLineSegment(sketch, "E1587", {"start": v(-19.74, -25.14) * mm, "end": v(-19.6, -25.1) * mm});
            skLineSegment(sketch, "E1588", {"start": v(-19.6, -25.1) * mm, "end": v(-19.47, -25.02) * mm});
            skLineSegment(sketch, "E1589", {"start": v(-19.47, -25.02) * mm, "end": v(-19.08, -24.55) * mm});
            skLineSegment(sketch, "E1590", {"start": v(-19.08, -24.55) * mm, "end": v(-18.98, -24.46) * mm});
            skLineSegment(sketch, "E1591", {"start": v(-18.98, -24.46) * mm, "end": v(-18.88, -24.39) * mm});
            skLineSegment(sketch, "E1592", {"start": v(-18.88, -24.39) * mm, "end": v(-18.77, -24.32) * mm});
            skLineSegment(sketch, "E1593", {"start": v(-18.77, -24.32) * mm, "end": v(-18.65, -24.26) * mm});
            skLineSegment(sketch, "E1594", {"start": v(-18.65, -24.26) * mm, "end": v(-18.53, -24.21) * mm});
            skLineSegment(sketch, "E1595", {"start": v(-18.53, -24.21) * mm, "end": v(-18.4, -24.18) * mm});
            skLineSegment(sketch, "E1596", {"start": v(-18.4, -24.18) * mm, "end": v(-18.28, -24.15) * mm});
            skLineSegment(sketch, "E1597", {"start": v(-18.28, -24.15) * mm, "end": v(-18.16, -24.14) * mm});
            skLineSegment(sketch, "E1598", {"start": v(-18.16, -24.14) * mm, "end": v(-18.03, -24.13) * mm});
            skLineSegment(sketch, "E1599", {"start": v(-18.03, -24.13) * mm, "end": v(-17.9, -24.14) * mm});
            skLineSegment(sketch, "E1600", {"start": v(-17.9, -24.14) * mm, "end": v(-17.77, -24.16) * mm});
            skLineSegment(sketch, "E1601", {"start": v(-17.77, -24.16) * mm, "end": v(-17.64, -24.18) * mm});
            skLineSegment(sketch, "E1602", {"start": v(-17.64, -24.18) * mm, "end": v(-17.5, -24.22) * mm});
            skLineSegment(sketch, "E1603", {"start": v(-17.5, -24.22) * mm, "end": v(-17.38, -24.27) * mm});
            skLineSegment(sketch, "E1604", {"start": v(-17.38, -24.27) * mm, "end": v(-17.26, -24.33) * mm});
            skLineSegment(sketch, "E1605", {"start": v(-17.26, -24.33) * mm, "end": v(-17.14, -24.4) * mm});
            skLineSegment(sketch, "E1606", {"start": v(-17.14, -24.4) * mm, "end": v(-17.03, -24.5) * mm});
            skLineSegment(sketch, "E1607", {"start": v(-17.03, -24.5) * mm, "end": v(-16.94, -24.59) * mm});
            skLineSegment(sketch, "E1608", {"start": v(-16.94, -24.59) * mm, "end": v(-16.85, -24.69) * mm});
            skLineSegment(sketch, "E1609", {"start": v(-16.85, -24.69) * mm, "end": v(-16.77, -24.8) * mm});
            skLineSegment(sketch, "E1610", {"start": v(-16.77, -24.8) * mm, "end": v(-16.7, -24.9) * mm});
            skLineSegment(sketch, "E1611", {"start": v(-16.7, -24.9) * mm, "end": v(-16.64, -25.02) * mm});
            skLineSegment(sketch, "E1612", {"start": v(-16.64, -25.02) * mm, "end": v(-16.59, -25.14) * mm});
            skLineSegment(sketch, "E1613", {"start": v(-16.59, -25.14) * mm, "end": v(-16.55, -25.27) * mm});
            skLineSegment(sketch, "E1614", {"start": v(-16.55, -25.27) * mm, "end": v(-16.52, -25.4) * mm});
            skLineSegment(sketch, "E1615", {"start": v(-16.52, -25.4) * mm, "end": v(-16.5, -25.52) * mm});
            skLineSegment(sketch, "E1616", {"start": v(-16.5, -25.52) * mm, "end": v(-16.5, -25.65) * mm});
            skLineSegment(sketch, "E1617", {"start": v(-16.5, -25.65) * mm, "end": v(-16.5, -25.78) * mm});
            skLineSegment(sketch, "E1618", {"start": v(-16.5, -25.78) * mm, "end": v(-16.51, -25.9) * mm});
            skLineSegment(sketch, "E1619", {"start": v(-16.51, -25.9) * mm, "end": v(-16.54, -26.03) * mm});
            skLineSegment(sketch, "E1620", {"start": v(-16.54, -26.03) * mm, "end": v(-16.57, -26.16) * mm});
            skLineSegment(sketch, "E1621", {"start": v(-16.57, -26.16) * mm, "end": v(-16.62, -26.28) * mm});
            skLineSegment(sketch, "E1622", {"start": v(-16.62, -26.28) * mm, "end": v(-16.94, -26.8) * mm});
            skLineSegment(sketch, "E1623", {"start": v(-16.94, -26.8) * mm, "end": v(-16.98, -26.95) * mm});
            skLineSegment(sketch, "E1624", {"start": v(-16.98, -26.95) * mm, "end": v(-16.96, -27.1) * mm});
            skLineSegment(sketch, "E1625", {"start": v(-16.96, -27.1) * mm, "end": v(-16.9, -27.23) * mm});
            skLineSegment(sketch, "E1626", {"start": v(-16.9, -27.23) * mm, "end": v(-16.8, -27.33) * mm});
            skLineSegment(sketch, "E1627", {"start": v(-16.8, -27.33) * mm, "end": v(-16.38, -27.59) * mm});
            skLineSegment(sketch, "E1628", {"start": v(-16.38, -27.59) * mm, "end": v(-15.96, -27.83) * mm});
            skLineSegment(sketch, "E1629", {"start": v(-15.96, -27.83) * mm, "end": v(-15.83, -27.87) * mm});
            skLineSegment(sketch, "E1630", {"start": v(-15.83, -27.87) * mm, "end": v(-15.67, -27.86) * mm});
            skLineSegment(sketch, "E1631", {"start": v(-15.67, -27.86) * mm, "end": v(-15.53, -27.8) * mm});
            skLineSegment(sketch, "E1632", {"start": v(-15.53, -27.8) * mm, "end": v(-15.42, -27.7) * mm});
            skLineSegment(sketch, "E1633", {"start": v(-15.42, -27.7) * mm, "end": v(-15.12, -27.18) * mm});
            skLineSegment(sketch, "E1634", {"start": v(-15.12, -27.18) * mm, "end": v(-15.03, -27.07) * mm});
            skLineSegment(sketch, "E1635", {"start": v(-15.03, -27.07) * mm, "end": v(-14.94, -26.98) * mm});
            skLineSegment(sketch, "E1636", {"start": v(-14.94, -26.98) * mm, "end": v(-14.84, -26.9) * mm});
            skLineSegment(sketch, "E1637", {"start": v(-14.84, -26.9) * mm, "end": v(-14.74, -26.82) * mm});
            skLineSegment(sketch, "E1638", {"start": v(-14.74, -26.82) * mm, "end": v(-14.62, -26.76) * mm});
            skLineSegment(sketch, "E1639", {"start": v(-14.62, -26.76) * mm, "end": v(-14.5, -26.7) * mm});
            skLineSegment(sketch, "E1640", {"start": v(-14.5, -26.7) * mm, "end": v(-14.39, -26.66) * mm});
            skLineSegment(sketch, "E1641", {"start": v(-14.39, -26.66) * mm, "end": v(-14.26, -26.63) * mm});
            skLineSegment(sketch, "E1642", {"start": v(-14.26, -26.63) * mm, "end": v(-14.14, -26.6) * mm});
            skLineSegment(sketch, "E1643", {"start": v(-14.14, -26.6) * mm, "end": v(-14, -26.59) * mm});
            skLineSegment(sketch, "E1644", {"start": v(-14, -26.59) * mm, "end": v(-13.88, -26.59) * mm});
            skLineSegment(sketch, "E1645", {"start": v(-13.88, -26.59) * mm, "end": v(-13.74, -26.6) * mm});
            skLineSegment(sketch, "E1646", {"start": v(-13.74, -26.6) * mm, "end": v(-13.61, -26.61) * mm});
            skLineSegment(sketch, "E1647", {"start": v(-13.61, -26.61) * mm, "end": v(-13.48, -26.64) * mm});
            skLineSegment(sketch, "E1648", {"start": v(-13.48, -26.64) * mm, "end": v(-13.35, -26.68) * mm});
            skLineSegment(sketch, "E1649", {"start": v(-13.35, -26.68) * mm, "end": v(-13.22, -26.73) * mm});
            skLineSegment(sketch, "E1650", {"start": v(-13.22, -26.73) * mm, "end": v(-13.1, -26.8) * mm});
            skLineSegment(sketch, "E1651", {"start": v(-13.1, -26.8) * mm, "end": v(-12.99, -26.88) * mm});
            skLineSegment(sketch, "E1652", {"start": v(-12.99, -26.88) * mm, "end": v(-12.89, -26.97) * mm});
            skLineSegment(sketch, "E1653", {"start": v(-12.89, -26.97) * mm, "end": v(-12.8, -27.06) * mm});
            skLineSegment(sketch, "E1654", {"start": v(-12.8, -27.06) * mm, "end": v(-12.7, -27.16) * mm});
            skLineSegment(sketch, "E1655", {"start": v(-12.7, -27.16) * mm, "end": v(-12.63, -27.27) * mm});
            skLineSegment(sketch, "E1656", {"start": v(-12.63, -27.27) * mm, "end": v(-12.56, -27.38) * mm});
            skLineSegment(sketch, "E1657", {"start": v(-12.56, -27.38) * mm, "end": v(-12.5, -27.5) * mm});
            skLineSegment(sketch, "E1658", {"start": v(-12.5, -27.5) * mm, "end": v(-12.45, -27.62) * mm});
            skLineSegment(sketch, "E1659", {"start": v(-12.45, -27.62) * mm, "end": v(-12.42, -27.74) * mm});
            skLineSegment(sketch, "E1660", {"start": v(-12.42, -27.74) * mm, "end": v(-12.39, -27.87) * mm});
            skLineSegment(sketch, "E1661", {"start": v(-12.39, -27.87) * mm, "end": v(-12.37, -28) * mm});
            skLineSegment(sketch, "E1662", {"start": v(-12.37, -28) * mm, "end": v(-12.37, -28.12) * mm});
            skLineSegment(sketch, "E1663", {"start": v(-12.37, -28.12) * mm, "end": v(-12.37, -28.25) * mm});
            skLineSegment(sketch, "E1664", {"start": v(-12.37, -28.25) * mm, "end": v(-12.4, -28.38) * mm});
            skLineSegment(sketch, "E1665", {"start": v(-12.4, -28.38) * mm, "end": v(-12.42, -28.5) * mm});
            skLineSegment(sketch, "E1666", {"start": v(-12.42, -28.5) * mm, "end": v(-12.65, -29.07) * mm});
            skLineSegment(sketch, "E1667", {"start": v(-12.65, -29.07) * mm, "end": v(-12.67, -29.22) * mm});
            skLineSegment(sketch, "E1668", {"start": v(-12.67, -29.22) * mm, "end": v(-12.63, -29.37) * mm});
            skLineSegment(sketch, "E1669", {"start": v(-12.63, -29.37) * mm, "end": v(-12.54, -29.5) * mm});
            skLineSegment(sketch, "E1670", {"start": v(-12.54, -29.5) * mm, "end": v(-12.43, -29.57) * mm});
            skLineSegment(sketch, "E1671", {"start": v(-12.43, -29.57) * mm, "end": v(-11.98, -29.76) * mm});
            skLineSegment(sketch, "E1672", {"start": v(-11.98, -29.76) * mm, "end": v(-11.53, -29.94) * mm});
            skLineSegment(sketch, "E1673", {"start": v(-11.53, -29.94) * mm, "end": v(-11.4, -29.96) * mm});
            skLineSegment(sketch, "E1674", {"start": v(-11.4, -29.96) * mm, "end": v(-11.24, -29.93) * mm});
            skLineSegment(sketch, "E1675", {"start": v(-11.24, -29.93) * mm, "end": v(-11.11, -29.85) * mm});
            skLineSegment(sketch, "E1676", {"start": v(-11.11, -29.85) * mm, "end": v(-11.02, -29.73) * mm});
            skLineSegment(sketch, "E1677", {"start": v(-11.02, -29.73) * mm, "end": v(-10.8, -29.17) * mm});
            skLineSegment(sketch, "E1678", {"start": v(-10.8, -29.17) * mm, "end": v(-10.73, -29.05) * mm});
            skLineSegment(sketch, "E1679", {"start": v(-10.73, -29.05) * mm, "end": v(-10.65, -28.95) * mm});
            skLineSegment(sketch, "E1680", {"start": v(-10.65, -28.95) * mm, "end": v(-10.57, -28.85) * mm});
            skLineSegment(sketch, "E1681", {"start": v(-10.57, -28.85) * mm, "end": v(-10.47, -28.76) * mm});
            skLineSegment(sketch, "E1682", {"start": v(-10.47, -28.76) * mm, "end": v(-10.37, -28.68) * mm});
            skLineSegment(sketch, "E1683", {"start": v(-10.37, -28.68) * mm, "end": v(-10.27, -28.6) * mm});
            skLineSegment(sketch, "E1684", {"start": v(-10.27, -28.6) * mm, "end": v(-10.15, -28.54) * mm});
            skLineSegment(sketch, "E1685", {"start": v(-10.15, -28.54) * mm, "end": v(-10.04, -28.5) * mm});
            skLineSegment(sketch, "E1686", {"start": v(-10.04, -28.5) * mm, "end": v(-9.91, -28.45) * mm});
            skLineSegment(sketch, "E1687", {"start": v(-9.91, -28.45) * mm, "end": v(-9.79, -28.42) * mm});
            skLineSegment(sketch, "E1688", {"start": v(-9.79, -28.42) * mm, "end": v(-9.66, -28.4) * mm});
            skLineSegment(sketch, "E1689", {"start": v(-9.66, -28.4) * mm, "end": v(-9.53, -28.38) * mm});
            skLineSegment(sketch, "E1690", {"start": v(-9.53, -28.38) * mm, "end": v(-9.4, -28.38) * mm});
            skLineSegment(sketch, "E1691", {"start": v(-9.4, -28.38) * mm, "end": v(-9.26, -28.39) * mm});
            skLineSegment(sketch, "E1692", {"start": v(-9.26, -28.39) * mm, "end": v(-9.12, -28.4) * mm});
            skLineSegment(sketch, "E1693", {"start": v(-9.12, -28.4) * mm, "end": v(-8.99, -28.44) * mm});
            skLineSegment(sketch, "E1694", {"start": v(-8.99, -28.44) * mm, "end": v(-8.86, -28.5) * mm});
            skLineSegment(sketch, "E1695", {"start": v(-8.86, -28.5) * mm, "end": v(-8.74, -28.55) * mm});
            skLineSegment(sketch, "E1696", {"start": v(-8.74, -28.55) * mm, "end": v(-8.62, -28.62) * mm});
            skLineSegment(sketch, "E1697", {"start": v(-8.62, -28.62) * mm, "end": v(-8.51, -28.7) * mm});
            skLineSegment(sketch, "E1698", {"start": v(-8.51, -28.7) * mm, "end": v(-8.41, -28.79) * mm});
            skLineSegment(sketch, "E1699", {"start": v(-8.41, -28.79) * mm, "end": v(-8.32, -28.88) * mm});
            skLineSegment(sketch, "E1700", {"start": v(-8.32, -28.88) * mm, "end": v(-8.24, -28.98) * mm});
            skLineSegment(sketch, "E1701", {"start": v(-8.24, -28.98) * mm, "end": v(-8.16, -29.08) * mm});
            skLineSegment(sketch, "E1702", {"start": v(-8.16, -29.08) * mm, "end": v(-8.1, -29.2) * mm});
            skLineSegment(sketch, "E1703", {"start": v(-8.1, -29.2) * mm, "end": v(-8.04, -29.31) * mm});
            skLineSegment(sketch, "E1704", {"start": v(-8.04, -29.31) * mm, "end": v(-8, -29.43) * mm});
            skLineSegment(sketch, "E1705", {"start": v(-8, -29.43) * mm, "end": v(-7.96, -29.55) * mm});
            skLineSegment(sketch, "E1706", {"start": v(-7.96, -29.55) * mm, "end": v(-7.94, -29.68) * mm});
            skLineSegment(sketch, "E1707", {"start": v(-7.94, -29.68) * mm, "end": v(-7.92, -29.81) * mm});
            skLineSegment(sketch, "E1708", {"start": v(-7.92, -29.81) * mm, "end": v(-7.92, -29.94) * mm});
            skLineSegment(sketch, "E1709", {"start": v(-7.92, -29.94) * mm, "end": v(-7.93, -30.07) * mm});
            skLineSegment(sketch, "E1710", {"start": v(-7.93, -30.07) * mm, "end": v(-8.07, -30.66) * mm});
            skLineSegment(sketch, "E1711", {"start": v(-8.07, -30.66) * mm, "end": v(-8.06, -30.81) * mm});
            skLineSegment(sketch, "E1712", {"start": v(-8.06, -30.81) * mm, "end": v(-8, -30.95) * mm});
            skLineSegment(sketch, "E1713", {"start": v(-8, -30.95) * mm, "end": v(-7.9, -31.06) * mm});
            skLineSegment(sketch, "E1714", {"start": v(-7.9, -31.06) * mm, "end": v(-7.78, -31.12) * mm});
            skLineSegment(sketch, "E1715", {"start": v(-7.78, -31.12) * mm, "end": v(-7.3, -31.25) * mm});
            skLineSegment(sketch, "E1716", {"start": v(-7.3, -31.25) * mm, "end": v(-6.83, -31.35) * mm});
            skLineSegment(sketch, "E1717", {"start": v(-6.83, -31.35) * mm, "end": v(-6.7, -31.35) * mm});
            skLineSegment(sketch, "E1718", {"start": v(-6.7, -31.35) * mm, "end": v(-6.55, -31.3) * mm});
            skLineSegment(sketch, "E1719", {"start": v(-6.55, -31.3) * mm, "end": v(-6.43, -31.2) * mm});
            skLineSegment(sketch, "E1720", {"start": v(-6.43, -31.2) * mm, "end": v(-6.36, -31.06) * mm});
            skLineSegment(sketch, "E1721", {"start": v(-6.36, -31.06) * mm, "end": v(-6.22, -30.47) * mm});
            skLineSegment(sketch, "E1722", {"start": v(-6.22, -30.47) * mm, "end": v(-6.17, -30.35) * mm});
            skLineSegment(sketch, "E1723", {"start": v(-6.17, -30.35) * mm, "end": v(-6.11, -30.23) * mm});
            skLineSegment(sketch, "E1724", {"start": v(-6.11, -30.23) * mm, "end": v(-6.04, -30.12) * mm});
            skLineSegment(sketch, "E1725", {"start": v(-6.04, -30.12) * mm, "end": v(-5.97, -30.02) * mm});
            skLineSegment(sketch, "E1726", {"start": v(-5.97, -30.02) * mm, "end": v(-5.88, -29.93) * mm});
            skLineSegment(sketch, "E1727", {"start": v(-5.88, -29.93) * mm, "end": v(-5.78, -29.84) * mm});
            skLineSegment(sketch, "E1728", {"start": v(-5.78, -29.84) * mm, "end": v(-5.68, -29.76) * mm});
            skLineSegment(sketch, "E1729", {"start": v(-5.68, -29.76) * mm, "end": v(-5.57, -29.7) * mm});
            skLineSegment(sketch, "E1730", {"start": v(-5.57, -29.7) * mm, "end": v(-5.46, -29.63) * mm});
            skLineSegment(sketch, "E1731", {"start": v(-5.46, -29.63) * mm, "end": v(-5.34, -29.58) * mm});
            skLineSegment(sketch, "E1732", {"start": v(-5.34, -29.58) * mm, "end": v(-5.22, -29.53) * mm});
            skLineSegment(sketch, "E1733", {"start": v(-5.22, -29.53) * mm, "end": v(-5.09, -29.5) * mm});
            skLineSegment(sketch, "E1734", {"start": v(-5.09, -29.5) * mm, "end": v(-4.96, -29.48) * mm});
            skLineSegment(sketch, "E1735", {"start": v(-4.96, -29.48) * mm, "end": v(-4.82, -29.47) * mm});
            skLineSegment(sketch, "E1736", {"start": v(-4.82, -29.47) * mm, "end": v(-4.69, -29.47) * mm});
            skLineSegment(sketch, "E1737", {"start": v(-4.69, -29.47) * mm, "end": v(-4.55, -29.48) * mm});
            skLineSegment(sketch, "E1738", {"start": v(-4.55, -29.48) * mm, "end": v(-4.41, -29.5) * mm});
            skLineSegment(sketch, "E1739", {"start": v(-4.41, -29.5) * mm, "end": v(-4.28, -29.55) * mm});
            skLineSegment(sketch, "E1740", {"start": v(-4.28, -29.55) * mm, "end": v(-4.16, -29.6) * mm});
            skLineSegment(sketch, "E1741", {"start": v(-4.16, -29.6) * mm, "end": v(-4.04, -29.66) * mm});
            skLineSegment(sketch, "E1742", {"start": v(-4.04, -29.66) * mm, "end": v(-3.93, -29.73) * mm});
            skLineSegment(sketch, "E1743", {"start": v(-3.93, -29.73) * mm, "end": v(-3.82, -29.81) * mm});
            skLineSegment(sketch, "E1744", {"start": v(-3.82, -29.81) * mm, "end": v(-3.72, -29.9) * mm});
            skLineSegment(sketch, "E1745", {"start": v(-3.72, -29.9) * mm, "end": v(-3.63, -30) * mm});
            skLineSegment(sketch, "E1746", {"start": v(-3.63, -30) * mm, "end": v(-3.55, -30.09) * mm});
            skLineSegment(sketch, "E1747", {"start": v(-3.55, -30.09) * mm, "end": v(-3.48, -30.2) * mm});
            skLineSegment(sketch, "E1748", {"start": v(-3.48, -30.2) * mm, "end": v(-3.41, -30.3) * mm});
            skLineSegment(sketch, "E1749", {"start": v(-3.41, -30.3) * mm, "end": v(-3.36, -30.42) * mm});
            skLineSegment(sketch, "E1750", {"start": v(-3.36, -30.42) * mm, "end": v(-3.32, -30.55) * mm});
            skLineSegment(sketch, "E1751", {"start": v(-3.32, -30.55) * mm, "end": v(-3.28, -30.67) * mm});
            skLineSegment(sketch, "E1752", {"start": v(-3.28, -30.67) * mm, "end": v(-3.26, -30.8) * mm});
            skLineSegment(sketch, "E1753", {"start": v(-3.26, -30.8) * mm, "end": v(-3.25, -30.93) * mm});
            skLineSegment(sketch, "E1754", {"start": v(-3.25, -30.93) * mm, "end": v(-3.3, -31.54) * mm});
            skLineSegment(sketch, "E1755", {"start": v(-3.3, -31.54) * mm, "end": v(-3.27, -31.68) * mm});
            skLineSegment(sketch, "E1756", {"start": v(-3.27, -31.68) * mm, "end": v(-3.19, -31.81) * mm});
            skLineSegment(sketch, "E1757", {"start": v(-3.19, -31.81) * mm, "end": v(-3.07, -31.9) * mm});
            skLineSegment(sketch, "E1758", {"start": v(-3.07, -31.9) * mm, "end": v(-2.94, -31.95) * mm});
            skLineSegment(sketch, "E1759", {"start": v(-2.94, -31.95) * mm, "end": v(-2.45, -32) * mm});
            skLineSegment(sketch, "E1760", {"start": v(-2.45, -32) * mm, "end": v(-1.97, -32.02) * mm});
            skLineSegment(sketch, "E1761", {"start": v(-1.97, -32.02) * mm, "end": v(-1.83, -32) * mm});
            skLineSegment(sketch, "E1762", {"start": v(-1.83, -32) * mm, "end": v(-1.7, -31.93) * mm});
            skLineSegment(sketch, "E1763", {"start": v(-1.7, -31.93) * mm, "end": v(-1.6, -31.81) * mm});
            skLineSegment(sketch, "E1764", {"start": v(-1.6, -31.81) * mm, "end": v(-1.54, -31.67) * mm});
            skLineSegment(sketch, "E1765", {"start": v(-1.54, -31.67) * mm, "end": v(-1.5, -31.07) * mm});
            skLineSegment(sketch, "E1766", {"start": v(-1.5, -31.07) * mm, "end": v(-1.47, -30.94) * mm});
            skLineSegment(sketch, "E1767", {"start": v(-1.47, -30.94) * mm, "end": v(-1.43, -30.81) * mm});
            skLineSegment(sketch, "E1768", {"start": v(-1.43, -30.81) * mm, "end": v(-1.38, -30.7) * mm});
            skLineSegment(sketch, "E1769", {"start": v(-1.38, -30.7) * mm, "end": v(-1.32, -30.58) * mm});
            skLineSegment(sketch, "E1770", {"start": v(-1.32, -30.58) * mm, "end": v(-1.25, -30.47) * mm});
            skLineSegment(sketch, "E1771", {"start": v(-1.25, -30.47) * mm, "end": v(-1.17, -30.37) * mm});
            skLineSegment(sketch, "E1772", {"start": v(-1.17, -30.37) * mm, "end": v(-1.08, -30.28) * mm});
            skLineSegment(sketch, "E1773", {"start": v(-1.08, -30.28) * mm, "end": v(-0.98, -30.2) * mm});
            skLineSegment(sketch, "E1774", {"start": v(-0.98, -30.2) * mm, "end": v(-0.88, -30.12) * mm});
            skLineSegment(sketch, "E1775", {"start": v(-0.88, -30.12) * mm, "end": v(-0.77, -30.05) * mm});
            skLineSegment(sketch, "E1776", {"start": v(-0.77, -30.05) * mm, "end": v(-0.65, -29.98) * mm});
            skLineSegment(sketch, "E1777", {"start": v(-0.65, -29.98) * mm, "end": v(-0.53, -29.93) * mm});
            skLineSegment(sketch, "E1778", {"start": v(-0.53, -29.93) * mm, "end": v(-0.4, -29.9) * mm});
            skLineSegment(sketch, "E1779", {"start": v(-0.4, -29.9) * mm, "end": v(-0.27, -29.86) * mm});
            skLineSegment(sketch, "E1780", {"start": v(-0.27, -29.86) * mm, "end": v(-0.14, -29.84) * mm});
            skLineSegment(sketch, "E1781", {"start": v(-0.14, -29.84) * mm, "end": v(0, -29.83) * mm});
            skLineSegment(sketch, "E1782", {"start": v(0, -29.83) * mm, "end": v(0.14, -29.84) * mm});
            skLineSegment(sketch, "E1783", {"start": v(0.14, -29.84) * mm, "end": v(0.27, -29.86) * mm});
            skLineSegment(sketch, "E1784", {"start": v(0.27, -29.86) * mm, "end": v(0.4, -29.9) * mm});
            skLineSegment(sketch, "E1785", {"start": v(0.4, -29.9) * mm, "end": v(0.53, -29.93) * mm});
            skLineSegment(sketch, "E1786", {"start": v(0.53, -29.93) * mm, "end": v(0.65, -29.98) * mm});
            skLineSegment(sketch, "E1787", {"start": v(0.65, -29.98) * mm, "end": v(0.77, -30.05) * mm});
            skLineSegment(sketch, "E1788", {"start": v(0.77, -30.05) * mm, "end": v(0.88, -30.12) * mm});
            skLineSegment(sketch, "E1789", {"start": v(0.88, -30.12) * mm, "end": v(0.98, -30.2) * mm});
            skLineSegment(sketch, "E1790", {"start": v(0.98, -30.2) * mm, "end": v(1.08, -30.28) * mm});
            skLineSegment(sketch, "E1791", {"start": v(1.08, -30.28) * mm, "end": v(1.17, -30.37) * mm});
            skLineSegment(sketch, "E1792", {"start": v(1.17, -30.37) * mm, "end": v(1.25, -30.47) * mm});
            skLineSegment(sketch, "E1793", {"start": v(1.25, -30.47) * mm, "end": v(1.32, -30.58) * mm});
            skLineSegment(sketch, "E1794", {"start": v(1.32, -30.58) * mm, "end": v(1.38, -30.7) * mm});
            skLineSegment(sketch, "E1795", {"start": v(1.38, -30.7) * mm, "end": v(1.43, -30.81) * mm});
            skLineSegment(sketch, "E1796", {"start": v(1.43, -30.81) * mm, "end": v(1.47, -30.94) * mm});
            skLineSegment(sketch, "E1797", {"start": v(1.47, -30.94) * mm, "end": v(1.5, -31.07) * mm});
            skLineSegment(sketch, "E1798", {"start": v(1.5, -31.07) * mm, "end": v(1.54, -31.67) * mm});
            skLineSegment(sketch, "E1799", {"start": v(1.54, -31.67) * mm, "end": v(1.6, -31.81) * mm});
            skLineSegment(sketch, "E1800", {"start": v(1.6, -31.81) * mm, "end": v(1.7, -31.93) * mm});
            skLineSegment(sketch, "E1801", {"start": v(1.7, -31.93) * mm, "end": v(1.83, -32) * mm});
            skLineSegment(sketch, "E1802", {"start": v(1.83, -32) * mm, "end": v(1.97, -32.02) * mm});
            skLineSegment(sketch, "E1803", {"start": v(1.97, -32.02) * mm, "end": v(2.45, -32) * mm});
            skLineSegment(sketch, "E1804", {"start": v(-0.8, -2.5) * mm, "end": v(-1.53, -2.14) * mm});
            skLineSegment(sketch, "E1805", {"start": v(-1.53, -2.14) * mm, "end": v(-2.1, -1.56) * mm});
            skLineSegment(sketch, "E1806", {"start": v(-2.1, -1.56) * mm, "end": v(-2.47, -0.84) * mm});
            skLineSegment(sketch, "E1807", {"start": v(-2.47, -0.84) * mm, "end": v(-2.6, -0.03) * mm});
            skLineSegment(sketch, "E1808", {"start": v(-2.6, -0.03) * mm, "end": v(-2.47, 0.77) * mm});
            skLineSegment(sketch, "E1809", {"start": v(-2.47, 0.77) * mm, "end": v(-2.1, 1.5) * mm});
            skLineSegment(sketch, "E1810", {"start": v(-2.1, 1.5) * mm, "end": v(-1.53, 2.07) * mm});
            skLineSegment(sketch, "E1811", {"start": v(-1.53, 2.07) * mm, "end": v(-0.8, 2.44) * mm});
            skLineSegment(sketch, "E1812", {"start": v(-0.8, 2.44) * mm, "end": v(0, 2.57) * mm});
            skLineSegment(sketch, "E1813", {"start": v(0, 2.57) * mm, "end": v(0.8, 2.44) * mm});
            skLineSegment(sketch, "E1814", {"start": v(0.8, 2.44) * mm, "end": v(1.53, 2.07) * mm});
            skLineSegment(sketch, "E1815", {"start": v(1.53, 2.07) * mm, "end": v(2.1, 1.5) * mm});
            skLineSegment(sketch, "E1816", {"start": v(2.1, 1.5) * mm, "end": v(2.47, 0.77) * mm});
            skLineSegment(sketch, "E1817", {"start": v(2.47, 0.77) * mm, "end": v(2.6, -0.03) * mm});
            skLineSegment(sketch, "E1818", {"start": v(2.6, -0.03) * mm, "end": v(2.47, -0.84) * mm});
            skLineSegment(sketch, "E1819", {"start": v(2.47, -0.84) * mm, "end": v(2.1, -1.56) * mm});
            skLineSegment(sketch, "E1820", {"start": v(2.1, -1.56) * mm, "end": v(1.53, -2.14) * mm});
            skLineSegment(sketch, "E1821", {"start": v(1.53, -2.14) * mm, "end": v(0.8, -2.5) * mm});
            skLineSegment(sketch, "E1822", {"start": v(0.8, -2.5) * mm, "end": v(0, -2.63) * mm});
            skLineSegment(sketch, "E1823", {"start": v(0, -2.63) * mm, "end": v(-0.8, -2.5) * mm});
            skArc(sketch, "E1824.0.0", {"start": v(3.91, 6.22) * mm, "mid": v(4.77, 7.44) * mm, "end": v(6.06, 8.2) * mm});
            skArc(sketch, "E1824.0.1", {"start": v(6.06, 8.2) * mm, "mid": v(6.37, 7.96) * mm, "end": v(6.66, 7.71) * mm});
            skArc(sketch, "E1824.0.2", {"start": v(6.66, 7.71) * mm, "mid": v(6.21, 6.29) * mm, "end": v(5.22, 5.18) * mm});
            skArc(sketch, "E1824.0.3", {"start": v(5.22, 5.18) * mm, "mid": v(5.75, 4.58) * mm, "end": v(6.22, 3.92) * mm});
            skArc(sketch, "E1824.0.4", {"start": v(6.22, 3.92) * mm, "mid": v(7.53, 4.65) * mm, "end": v(9.01, 4.77) * mm});
            skArc(sketch, "E1824.0.5", {"start": v(9.01, 4.77) * mm, "mid": v(9.19, 4.42) * mm, "end": v(9.35, 4.07) * mm});
            skArc(sketch, "E1824.0.6", {"start": v(9.35, 4.07) * mm, "mid": v(8.32, 2.99) * mm, "end": v(6.94, 2.41) * mm});
            skArc(sketch, "E1824.0.7", {"start": v(6.94, 2.41) * mm, "mid": v(7.17, 1.64) * mm, "end": v(7.3, 0.85) * mm});
            skArc(sketch, "E1824.0.8", {"start": v(7.3, 0.85) * mm, "mid": v(8.8, 0.94) * mm, "end": v(10.19, 0.4) * mm});
            skArc(sketch, "E1824.0.9", {"start": v(10.19, 0.4) * mm, "mid": v(10.2, 0.02) * mm, "end": v(10.19, -0.37) * mm});
            skArc(sketch, "E1824.0.10", {"start": v(10.19, -0.37) * mm, "mid": v(8.8, -0.9) * mm, "end": v(7.3, -0.82) * mm});
            skArc(sketch, "E1824.0.11", {"start": v(7.3, -0.82) * mm, "mid": v(7.17, -1.61) * mm, "end": v(6.94, -2.38) * mm});
            skArc(sketch, "E1824.0.12", {"start": v(6.94, -2.38) * mm, "mid": v(8.32, -2.95) * mm, "end": v(9.35, -4.04) * mm});
            skArc(sketch, "E1824.0.13", {"start": v(9.35, -4.04) * mm, "mid": v(9.19, -4.4) * mm, "end": v(9.01, -4.74) * mm});
            skArc(sketch, "E1824.0.14", {"start": v(9.01, -4.74) * mm, "mid": v(7.53, -4.61) * mm, "end": v(6.22, -3.9) * mm});
            skArc(sketch, "E1824.0.15", {"start": v(6.22, -3.9) * mm, "mid": v(5.75, -4.55) * mm, "end": v(5.22, -5.14) * mm});
            skArc(sketch, "E1824.0.16", {"start": v(5.22, -5.14) * mm, "mid": v(6.21, -6.26) * mm, "end": v(6.66, -7.68) * mm});
            skArc(sketch, "E1824.0.17", {"start": v(6.66, -7.68) * mm, "mid": v(6.37, -7.93) * mm, "end": v(6.06, -8.16) * mm});
            skArc(sketch, "E1824.0.18", {"start": v(6.06, -8.16) * mm, "mid": v(4.77, -7.4) * mm, "end": v(3.91, -6.19) * mm});
            skArc(sketch, "E1824.0.19", {"start": v(3.91, -6.19) * mm, "mid": v(3.2, -6.58) * mm, "end": v(2.47, -6.88) * mm});
            skArc(sketch, "E1824.0.20", {"start": v(2.47, -6.88) * mm, "mid": v(2.88, -8.32) * mm, "end": v(2.67, -9.8) * mm});
            skArc(sketch, "E1824.0.21", {"start": v(2.67, -9.8) * mm, "mid": v(2.3, -9.89) * mm, "end": v(1.92, -9.97) * mm});
            skArc(sketch, "E1824.0.22", {"start": v(1.92, -9.97) * mm, "mid": v(1.08, -8.73) * mm, "end": v(0.83, -7.26) * mm});
            skArc(sketch, "E1824.0.23", {"start": v(0.83, -7.26) * mm, "mid": v(0.03, -7.3) * mm, "end": v(-0.77, -7.26) * mm});
            skArc(sketch, "E1824.0.24", {"start": v(-0.77, -7.26) * mm, "mid": v(-1.02, -8.73) * mm, "end": v(-1.85, -9.97) * mm});
            skArc(sketch, "E1824.0.25", {"start": v(-1.85, -9.97) * mm, "mid": v(-2.23, -9.89) * mm, "end": v(-2.6, -9.8) * mm});
            skArc(sketch, "E1824.0.26", {"start": v(-2.6, -9.8) * mm, "mid": v(-2.81, -8.32) * mm, "end": v(-2.4, -6.88) * mm});
            skArc(sketch, "E1824.0.27", {"start": v(-2.4, -6.88) * mm, "mid": v(-3.14, -6.58) * mm, "end": v(-3.84, -6.19) * mm});
            skArc(sketch, "E1824.0.28", {"start": v(-3.84, -6.19) * mm, "mid": v(-4.7, -7.4) * mm, "end": v(-6, -8.16) * mm});
            skArc(sketch, "E1824.0.29", {"start": v(-6, -8.16) * mm, "mid": v(-6.3, -7.93) * mm, "end": v(-6.6, -7.68) * mm});
            skArc(sketch, "E1824.0.30", {"start": v(-6.6, -7.68) * mm, "mid": v(-6.15, -6.26) * mm, "end": v(-5.15, -5.14) * mm});
            skArc(sketch, "E1824.0.31", {"start": v(-5.15, -5.14) * mm, "mid": v(-5.69, -4.55) * mm, "end": v(-6.15, -3.9) * mm});
            skArc(sketch, "E1824.0.32", {"start": v(-6.15, -3.9) * mm, "mid": v(-7.46, -4.61) * mm, "end": v(-8.95, -4.74) * mm});
            skArc(sketch, "E1824.0.33", {"start": v(-8.95, -4.74) * mm, "mid": v(-9.12, -4.4) * mm, "end": v(-9.28, -4.04) * mm});
            skArc(sketch, "E1824.0.34", {"start": v(-9.28, -4.04) * mm, "mid": v(-8.26, -2.95) * mm, "end": v(-6.88, -2.38) * mm});
            skArc(sketch, "E1824.0.35", {"start": v(-6.88, -2.38) * mm, "mid": v(-7.1, -1.61) * mm, "end": v(-7.23, -0.82) * mm});
            skArc(sketch, "E1824.0.36", {"start": v(-7.23, -0.82) * mm, "mid": v(-8.72, -0.9) * mm, "end": v(-10.12, -0.37) * mm});
            skArc(sketch, "E1824.0.37", {"start": v(-10.12, -0.37) * mm, "mid": v(-10.13, 0.02) * mm, "end": v(-10.12, 0.4) * mm});
            skArc(sketch, "E1824.0.38", {"start": v(-10.12, 0.4) * mm, "mid": v(-8.72, 0.94) * mm, "end": v(-7.23, 0.85) * mm});
            skArc(sketch, "E1824.0.39", {"start": v(-7.23, 0.85) * mm, "mid": v(-7.1, 1.64) * mm, "end": v(-6.88, 2.41) * mm});
            skArc(sketch, "E1824.0.40", {"start": v(-6.88, 2.41) * mm, "mid": v(-8.26, 2.99) * mm, "end": v(-9.28, 4.07) * mm});
            skArc(sketch, "E1824.0.41", {"start": v(-9.28, 4.07) * mm, "mid": v(-9.12, 4.42) * mm, "end": v(-8.95, 4.77) * mm});
            skArc(sketch, "E1824.0.42", {"start": v(-8.95, 4.77) * mm, "mid": v(-7.46, 4.65) * mm, "end": v(-6.15, 3.92) * mm});
            skArc(sketch, "E1824.0.43", {"start": v(-6.15, 3.92) * mm, "mid": v(-5.69, 4.58) * mm, "end": v(-5.15, 5.18) * mm});
            skArc(sketch, "E1824.0.44", {"start": v(-5.15, 5.18) * mm, "mid": v(-6.15, 6.29) * mm, "end": v(-6.6, 7.71) * mm});
            skArc(sketch, "E1824.0.45", {"start": v(-6.6, 7.71) * mm, "mid": v(-6.3, 7.96) * mm, "end": v(-6, 8.2) * mm});
            skArc(sketch, "E1824.0.46", {"start": v(-6, 8.2) * mm, "mid": v(-4.7, 7.44) * mm, "end": v(-3.84, 6.22) * mm});
            skArc(sketch, "E1824.0.47", {"start": v(-3.84, 6.22) * mm, "mid": v(-3.14, 6.6) * mm, "end": v(-2.4, 6.91) * mm});
            skArc(sketch, "E1824.0.48", {"start": v(-2.4, 6.91) * mm, "mid": v(-2.81, 8.35) * mm, "end": v(-2.6, 9.83) * mm});
            skArc(sketch, "E1824.0.49", {"start": v(-2.6, 9.83) * mm, "mid": v(-2.23, 9.92) * mm, "end": v(-1.85, 10) * mm});
            skArc(sketch, "E1824.0.50", {"start": v(-1.85, 10) * mm, "mid": v(-1.02, 8.76) * mm, "end": v(-0.77, 7.29) * mm});
            skArc(sketch, "E1824.0.51", {"start": v(-0.77, 7.29) * mm, "mid": v(0.03, 7.33) * mm, "end": v(0.83, 7.29) * mm});
            skArc(sketch, "E1824.0.52", {"start": v(0.83, 7.29) * mm, "mid": v(1.08, 8.76) * mm, "end": v(1.92, 10) * mm});
            skArc(sketch, "E1824.0.53", {"start": v(1.92, 10) * mm, "mid": v(2.3, 9.92) * mm, "end": v(2.67, 9.83) * mm});
            skArc(sketch, "E1824.0.54", {"start": v(2.67, 9.83) * mm, "mid": v(2.88, 8.35) * mm, "end": v(2.47, 6.91) * mm});
            skArc(sketch, "E1824.0.55", {"start": v(2.47, 6.91) * mm, "mid": v(3.2, 6.6) * mm, "end": v(3.91, 6.22) * mm});
            skSolve(sketch);
        }
        {
            var Q0;
            Q0=makeQuery(id+"F3.imprint","IMPRINT",FACE,{"disambiguationData":[TD([[makeQuery(id+"F3.imprint","IMPRINT",EDGE,{"derivedFrom":sQuery(id+"F3.wireOp",EDGE,"E0")}),1.0]])]});
            extrude(context, id + "F4", {"entities" : qUnion([Q0]), "depth" : (getVariable(context, 'totalThick')) * mm, "offsetDistance" : 25 * mm});
        }
        {
            var Q0;
            Q0=makeQuery(id+"F4.opExtrude","CAP_FACE",FACE,{"disambiguationData":[OSD([sQuery(id+"F3.wireOp",EDGE,"E0"),sQuery(id+"F3.wireOp",EDGE,"E1"),sQuery(id+"F3.wireOp",EDGE,"E2"),sQuery(id+"F3.wireOp",EDGE,"E3"),sQuery(id+"F3.wireOp",EDGE,"E4"),sQuery(id+"F3.wireOp",EDGE,"E5"),sQuery(id+"F3.wireOp",EDGE,"E6"),sQuery(id+"F3.wireOp",EDGE,"E7"),sQuery(id+"F3.wireOp",EDGE,"E8"),sQuery(id+"F3.wireOp",EDGE,"E9"),sQuery(id+"F3.wireOp",EDGE,"E10"),sQuery(id+"F3.wireOp",EDGE,"E11"),sQuery(id+"F3.wireOp",EDGE,"E12"),sQuery(id+"F3.wireOp",EDGE,"E13"),sQuery(id+"F3.wireOp",EDGE,"E14"),sQuery(id+"F3.wireOp",EDGE,"E15"),sQuery(id+"F3.wireOp",EDGE,"E16"),sQuery(id+"F3.wireOp",EDGE,"E17"),sQuery(id+"F3.wireOp",EDGE,"E18"),sQuery(id+"F3.wireOp",EDGE,"E19"),sQuery(id+"F3.wireOp",EDGE,"E20"),sQuery(id+"F3.wireOp",EDGE,"E21"),sQuery(id+"F3.wireOp",EDGE,"E22"),sQuery(id+"F3.wireOp",EDGE,"E23"),sQuery(id+"F3.wireOp",EDGE,"E24"),sQuery(id+"F3.wireOp",EDGE,"E25"),sQuery(id+"F3.wireOp",EDGE,"E26"),sQuery(id+"F3.wireOp",EDGE,"E27"),sQuery(id+"F3.wireOp",EDGE,"E28"),sQuery(id+"F3.wireOp",EDGE,"E29"),sQuery(id+"F3.wireOp",EDGE,"E30"),sQuery(id+"F3.wireOp",EDGE,"E31"),sQuery(id+"F3.wireOp",EDGE,"E32"),sQuery(id+"F3.wireOp",EDGE,"E33"),sQuery(id+"F3.wireOp",EDGE,"E34"),sQuery(id+"F3.wireOp",EDGE,"E35"),sQuery(id+"F3.wireOp",EDGE,"E36"),sQuery(id+"F3.wireOp",EDGE,"E37"),sQuery(id+"F3.wireOp",EDGE,"E38"),sQuery(id+"F3.wireOp",EDGE,"E39"),sQuery(id+"F3.wireOp",EDGE,"E40"),sQuery(id+"F3.wireOp",EDGE,"E41"),sQuery(id+"F3.wireOp",EDGE,"E42"),sQuery(id+"F3.wireOp",EDGE,"E43"),sQuery(id+"F3.wireOp",EDGE,"E44"),sQuery(id+"F3.wireOp",EDGE,"E45"),sQuery(id+"F3.wireOp",EDGE,"E46"),sQuery(id+"F3.wireOp",EDGE,"E47"),sQuery(id+"F3.wireOp",EDGE,"E48"),sQuery(id+"F3.wireOp",EDGE,"E49"),sQuery(id+"F3.wireOp",EDGE,"E50"),sQuery(id+"F3.wireOp",EDGE,"E51"),sQuery(id+"F3.wireOp",EDGE,"E52"),sQuery(id+"F3.wireOp",EDGE,"E53"),sQuery(id+"F3.wireOp",EDGE,"E54"),sQuery(id+"F3.wireOp",EDGE,"E55"),sQuery(id+"F3.wireOp",EDGE,"E56"),sQuery(id+"F3.wireOp",EDGE,"E57"),sQuery(id+"F3.wireOp",EDGE,"E58"),sQuery(id+"F3.wireOp",EDGE,"E59"),sQuery(id+"F3.wireOp",EDGE,"E60"),sQuery(id+"F3.wireOp",EDGE,"E61"),sQuery(id+"F3.wireOp",EDGE,"E62"),sQuery(id+"F3.wireOp",EDGE,"E63"),sQuery(id+"F3.wireOp",EDGE,"E64"),sQuery(id+"F3.wireOp",EDGE,"E65"),sQuery(id+"F3.wireOp",EDGE,"E66"),sQuery(id+"F3.wireOp",EDGE,"E67"),sQuery(id+"F3.wireOp",EDGE,"E68"),sQuery(id+"F3.wireOp",EDGE,"E69"),sQuery(id+"F3.wireOp",EDGE,"E70"),sQuery(id+"F3.wireOp",EDGE,"E71"),sQuery(id+"F3.wireOp",EDGE,"E72"),sQuery(id+"F3.wireOp",EDGE,"E73"),sQuery(id+"F3.wireOp",EDGE,"E74"),sQuery(id+"F3.wireOp",EDGE,"E75"),sQuery(id+"F3.wireOp",EDGE,"E76"),sQuery(id+"F3.wireOp",EDGE,"E77"),sQuery(id+"F3.wireOp",EDGE,"E78"),sQuery(id+"F3.wireOp",EDGE,"E79"),sQuery(id+"F3.wireOp",EDGE,"E80"),sQuery(id+"F3.wireOp",EDGE,"E81"),sQuery(id+"F3.wireOp",EDGE,"E82"),sQuery(id+"F3.wireOp",EDGE,"E83"),sQuery(id+"F3.wireOp",EDGE,"E84"),sQuery(id+"F3.wireOp",EDGE,"E85"),sQuery(id+"F3.wireOp",EDGE,"E86"),sQuery(id+"F3.wireOp",EDGE,"E87"),sQuery(id+"F3.wireOp",EDGE,"E88"),sQuery(id+"F3.wireOp",EDGE,"E89"),sQuery(id+"F3.wireOp",EDGE,"E90"),sQuery(id+"F3.wireOp",EDGE,"E91"),sQuery(id+"F3.wireOp",EDGE,"E92"),sQuery(id+"F3.wireOp",EDGE,"E93"),sQuery(id+"F3.wireOp",EDGE,"E94"),sQuery(id+"F3.wireOp",EDGE,"E95"),sQuery(id+"F3.wireOp",EDGE,"E96"),sQuery(id+"F3.wireOp",EDGE,"E97"),sQuery(id+"F3.wireOp",EDGE,"E98"),sQuery(id+"F3.wireOp",EDGE,"E99"),sQuery(id+"F3.wireOp",EDGE,"E100"),sQuery(id+"F3.wireOp",EDGE,"E101"),sQuery(id+"F3.wireOp",EDGE,"E102"),sQuery(id+"F3.wireOp",EDGE,"E103"),sQuery(id+"F3.wireOp",EDGE,"E104"),sQuery(id+"F3.wireOp",EDGE,"E105"),sQuery(id+"F3.wireOp",EDGE,"E106"),sQuery(id+"F3.wireOp",EDGE,"E107"),sQuery(id+"F3.wireOp",EDGE,"E108"),sQuery(id+"F3.wireOp",EDGE,"E109"),sQuery(id+"F3.wireOp",EDGE,"E110"),sQuery(id+"F3.wireOp",EDGE,"E111"),sQuery(id+"F3.wireOp",EDGE,"E112"),sQuery(id+"F3.wireOp",EDGE,"E113"),sQuery(id+"F3.wireOp",EDGE,"E114"),sQuery(id+"F3.wireOp",EDGE,"E115"),sQuery(id+"F3.wireOp",EDGE,"E116"),sQuery(id+"F3.wireOp",EDGE,"E117"),sQuery(id+"F3.wireOp",EDGE,"E118"),sQuery(id+"F3.wireOp",EDGE,"E119"),sQuery(id+"F3.wireOp",EDGE,"E120"),sQuery(id+"F3.wireOp",EDGE,"E121"),sQuery(id+"F3.wireOp",EDGE,"E122"),sQuery(id+"F3.wireOp",EDGE,"E123"),sQuery(id+"F3.wireOp",EDGE,"E124"),sQuery(id+"F3.wireOp",EDGE,"E125"),sQuery(id+"F3.wireOp",EDGE,"E126"),sQuery(id+"F3.wireOp",EDGE,"E127"),sQuery(id+"F3.wireOp",EDGE,"E128"),sQuery(id+"F3.wireOp",EDGE,"E129"),sQuery(id+"F3.wireOp",EDGE,"E130"),sQuery(id+"F3.wireOp",EDGE,"E131"),sQuery(id+"F3.wireOp",EDGE,"E132"),sQuery(id+"F3.wireOp",EDGE,"E133"),sQuery(id+"F3.wireOp",EDGE,"E134"),sQuery(id+"F3.wireOp",EDGE,"E135"),sQuery(id+"F3.wireOp",EDGE,"E136"),sQuery(id+"F3.wireOp",EDGE,"E137"),sQuery(id+"F3.wireOp",EDGE,"E138"),sQuery(id+"F3.wireOp",EDGE,"E139"),sQuery(id+"F3.wireOp",EDGE,"E140"),sQuery(id+"F3.wireOp",EDGE,"E141"),sQuery(id+"F3.wireOp",EDGE,"E142"),sQuery(id+"F3.wireOp",EDGE,"E143"),sQuery(id+"F3.wireOp",EDGE,"E144"),sQuery(id+"F3.wireOp",EDGE,"E145"),sQuery(id+"F3.wireOp",EDGE,"E146"),sQuery(id+"F3.wireOp",EDGE,"E147"),sQuery(id+"F3.wireOp",EDGE,"E148"),sQuery(id+"F3.wireOp",EDGE,"E149"),sQuery(id+"F3.wireOp",EDGE,"E150"),sQuery(id+"F3.wireOp",EDGE,"E151"),sQuery(id+"F3.wireOp",EDGE,"E152"),sQuery(id+"F3.wireOp",EDGE,"E153"),sQuery(id+"F3.wireOp",EDGE,"E154"),sQuery(id+"F3.wireOp",EDGE,"E155"),sQuery(id+"F3.wireOp",EDGE,"E156"),sQuery(id+"F3.wireOp",EDGE,"E157"),sQuery(id+"F3.wireOp",EDGE,"E158"),sQuery(id+"F3.wireOp",EDGE,"E159"),sQuery(id+"F3.wireOp",EDGE,"E160"),sQuery(id+"F3.wireOp",EDGE,"E161"),sQuery(id+"F3.wireOp",EDGE,"E162"),sQuery(id+"F3.wireOp",EDGE,"E163"),sQuery(id+"F3.wireOp",EDGE,"E164"),sQuery(id+"F3.wireOp",EDGE,"E165"),sQuery(id+"F3.wireOp",EDGE,"E166"),sQuery(id+"F3.wireOp",EDGE,"E167"),sQuery(id+"F3.wireOp",EDGE,"E168"),sQuery(id+"F3.wireOp",EDGE,"E169"),sQuery(id+"F3.wireOp",EDGE,"E170"),sQuery(id+"F3.wireOp",EDGE,"E171"),sQuery(id+"F3.wireOp",EDGE,"E172"),sQuery(id+"F3.wireOp",EDGE,"E173"),sQuery(id+"F3.wireOp",EDGE,"E174"),sQuery(id+"F3.wireOp",EDGE,"E175"),sQuery(id+"F3.wireOp",EDGE,"E176"),sQuery(id+"F3.wireOp",EDGE,"E177"),sQuery(id+"F3.wireOp",EDGE,"E178"),sQuery(id+"F3.wireOp",EDGE,"E179"),sQuery(id+"F3.wireOp",EDGE,"E180"),sQuery(id+"F3.wireOp",EDGE,"E181"),sQuery(id+"F3.wireOp",EDGE,"E182"),sQuery(id+"F3.wireOp",EDGE,"E183"),sQuery(id+"F3.wireOp",EDGE,"E184"),sQuery(id+"F3.wireOp",EDGE,"E185"),sQuery(id+"F3.wireOp",EDGE,"E186"),sQuery(id+"F3.wireOp",EDGE,"E187"),sQuery(id+"F3.wireOp",EDGE,"E188"),sQuery(id+"F3.wireOp",EDGE,"E189"),sQuery(id+"F3.wireOp",EDGE,"E190"),sQuery(id+"F3.wireOp",EDGE,"E191"),sQuery(id+"F3.wireOp",EDGE,"E192"),sQuery(id+"F3.wireOp",EDGE,"E193"),sQuery(id+"F3.wireOp",EDGE,"E194"),sQuery(id+"F3.wireOp",EDGE,"E195"),sQuery(id+"F3.wireOp",EDGE,"E196"),sQuery(id+"F3.wireOp",EDGE,"E197"),sQuery(id+"F3.wireOp",EDGE,"E198"),sQuery(id+"F3.wireOp",EDGE,"E199"),sQuery(id+"F3.wireOp",EDGE,"E200"),sQuery(id+"F3.wireOp",EDGE,"E201"),sQuery(id+"F3.wireOp",EDGE,"E202"),sQuery(id+"F3.wireOp",EDGE,"E203"),sQuery(id+"F3.wireOp",EDGE,"E204"),sQuery(id+"F3.wireOp",EDGE,"E205"),sQuery(id+"F3.wireOp",EDGE,"E206"),sQuery(id+"F3.wireOp",EDGE,"E207"),sQuery(id+"F3.wireOp",EDGE,"E208"),sQuery(id+"F3.wireOp",EDGE,"E209"),sQuery(id+"F3.wireOp",EDGE,"E210"),sQuery(id+"F3.wireOp",EDGE,"E211"),sQuery(id+"F3.wireOp",EDGE,"E212"),sQuery(id+"F3.wireOp",EDGE,"E213"),sQuery(id+"F3.wireOp",EDGE,"E214"),sQuery(id+"F3.wireOp",EDGE,"E215"),sQuery(id+"F3.wireOp",EDGE,"E216"),sQuery(id+"F3.wireOp",EDGE,"E217"),sQuery(id+"F3.wireOp",EDGE,"E218"),sQuery(id+"F3.wireOp",EDGE,"E219"),sQuery(id+"F3.wireOp",EDGE,"E220"),sQuery(id+"F3.wireOp",EDGE,"E221"),sQuery(id+"F3.wireOp",EDGE,"E222"),sQuery(id+"F3.wireOp",EDGE,"E223"),sQuery(id+"F3.wireOp",EDGE,"E224"),sQuery(id+"F3.wireOp",EDGE,"E225"),sQuery(id+"F3.wireOp",EDGE,"E226"),sQuery(id+"F3.wireOp",EDGE,"E227"),sQuery(id+"F3.wireOp",EDGE,"E228"),sQuery(id+"F3.wireOp",EDGE,"E229"),sQuery(id+"F3.wireOp",EDGE,"E230"),sQuery(id+"F3.wireOp",EDGE,"E231"),sQuery(id+"F3.wireOp",EDGE,"E232"),sQuery(id+"F3.wireOp",EDGE,"E233"),sQuery(id+"F3.wireOp",EDGE,"E234"),sQuery(id+"F3.wireOp",EDGE,"E235"),sQuery(id+"F3.wireOp",EDGE,"E236"),sQuery(id+"F3.wireOp",EDGE,"E237"),sQuery(id+"F3.wireOp",EDGE,"E238"),sQuery(id+"F3.wireOp",EDGE,"E239"),sQuery(id+"F3.wireOp",EDGE,"E240"),sQuery(id+"F3.wireOp",EDGE,"E241"),sQuery(id+"F3.wireOp",EDGE,"E242"),sQuery(id+"F3.wireOp",EDGE,"E243"),sQuery(id+"F3.wireOp",EDGE,"E244"),sQuery(id+"F3.wireOp",EDGE,"E245"),sQuery(id+"F3.wireOp",EDGE,"E246"),sQuery(id+"F3.wireOp",EDGE,"E247"),sQuery(id+"F3.wireOp",EDGE,"E248"),sQuery(id+"F3.wireOp",EDGE,"E249"),sQuery(id+"F3.wireOp",EDGE,"E250"),sQuery(id+"F3.wireOp",EDGE,"E251"),sQuery(id+"F3.wireOp",EDGE,"E252"),sQuery(id+"F3.wireOp",EDGE,"E253"),sQuery(id+"F3.wireOp",EDGE,"E254"),sQuery(id+"F3.wireOp",EDGE,"E255"),sQuery(id+"F3.wireOp",EDGE,"E256"),sQuery(id+"F3.wireOp",EDGE,"E257"),sQuery(id+"F3.wireOp",EDGE,"E258"),sQuery(id+"F3.wireOp",EDGE,"E259"),sQuery(id+"F3.wireOp",EDGE,"E260"),sQuery(id+"F3.wireOp",EDGE,"E261"),sQuery(id+"F3.wireOp",EDGE,"E262"),sQuery(id+"F3.wireOp",EDGE,"E263"),sQuery(id+"F3.wireOp",EDGE,"E264"),sQuery(id+"F3.wireOp",EDGE,"E265"),sQuery(id+"F3.wireOp",EDGE,"E266"),sQuery(id+"F3.wireOp",EDGE,"E267"),sQuery(id+"F3.wireOp",EDGE,"E268"),sQuery(id+"F3.wireOp",EDGE,"E269"),sQuery(id+"F3.wireOp",EDGE,"E270"),sQuery(id+"F3.wireOp",EDGE,"E271"),sQuery(id+"F3.wireOp",EDGE,"E272"),sQuery(id+"F3.wireOp",EDGE,"E273"),sQuery(id+"F3.wireOp",EDGE,"E274"),sQuery(id+"F3.wireOp",EDGE,"E275"),sQuery(id+"F3.wireOp",EDGE,"E276"),sQuery(id+"F3.wireOp",EDGE,"E277"),sQuery(id+"F3.wireOp",EDGE,"E278"),sQuery(id+"F3.wireOp",EDGE,"E279"),sQuery(id+"F3.wireOp",EDGE,"E280"),sQuery(id+"F3.wireOp",EDGE,"E281"),sQuery(id+"F3.wireOp",EDGE,"E282"),sQuery(id+"F3.wireOp",EDGE,"E283"),sQuery(id+"F3.wireOp",EDGE,"E284"),sQuery(id+"F3.wireOp",EDGE,"E285"),sQuery(id+"F3.wireOp",EDGE,"E286"),sQuery(id+"F3.wireOp",EDGE,"E287"),sQuery(id+"F3.wireOp",EDGE,"E288"),sQuery(id+"F3.wireOp",EDGE,"E289"),sQuery(id+"F3.wireOp",EDGE,"E290"),sQuery(id+"F3.wireOp",EDGE,"E291"),sQuery(id+"F3.wireOp",EDGE,"E292"),sQuery(id+"F3.wireOp",EDGE,"E293"),sQuery(id+"F3.wireOp",EDGE,"E294"),sQuery(id+"F3.wireOp",EDGE,"E295"),sQuery(id+"F3.wireOp",EDGE,"E296"),sQuery(id+"F3.wireOp",EDGE,"E297"),sQuery(id+"F3.wireOp",EDGE,"E298"),sQuery(id+"F3.wireOp",EDGE,"E299"),sQuery(id+"F3.wireOp",EDGE,"E300"),sQuery(id+"F3.wireOp",EDGE,"E301"),sQuery(id+"F3.wireOp",EDGE,"E302"),sQuery(id+"F3.wireOp",EDGE,"E303"),sQuery(id+"F3.wireOp",EDGE,"E304"),sQuery(id+"F3.wireOp",EDGE,"E305"),sQuery(id+"F3.wireOp",EDGE,"E306"),sQuery(id+"F3.wireOp",EDGE,"E307"),sQuery(id+"F3.wireOp",EDGE,"E308"),sQuery(id+"F3.wireOp",EDGE,"E309"),sQuery(id+"F3.wireOp",EDGE,"E310"),sQuery(id+"F3.wireOp",EDGE,"E311"),sQuery(id+"F3.wireOp",EDGE,"E312"),sQuery(id+"F3.wireOp",EDGE,"E313"),sQuery(id+"F3.wireOp",EDGE,"E314"),sQuery(id+"F3.wireOp",EDGE,"E315"),sQuery(id+"F3.wireOp",EDGE,"E316"),sQuery(id+"F3.wireOp",EDGE,"E317"),sQuery(id+"F3.wireOp",EDGE,"E318"),sQuery(id+"F3.wireOp",EDGE,"E319"),sQuery(id+"F3.wireOp",EDGE,"E320"),sQuery(id+"F3.wireOp",EDGE,"E321"),sQuery(id+"F3.wireOp",EDGE,"E322"),sQuery(id+"F3.wireOp",EDGE,"E323"),sQuery(id+"F3.wireOp",EDGE,"E324"),sQuery(id+"F3.wireOp",EDGE,"E325"),sQuery(id+"F3.wireOp",EDGE,"E326"),sQuery(id+"F3.wireOp",EDGE,"E327"),sQuery(id+"F3.wireOp",EDGE,"E328"),sQuery(id+"F3.wireOp",EDGE,"E329"),sQuery(id+"F3.wireOp",EDGE,"E330"),sQuery(id+"F3.wireOp",EDGE,"E331"),sQuery(id+"F3.wireOp",EDGE,"E332"),sQuery(id+"F3.wireOp",EDGE,"E333"),sQuery(id+"F3.wireOp",EDGE,"E334"),sQuery(id+"F3.wireOp",EDGE,"E335"),sQuery(id+"F3.wireOp",EDGE,"E336"),sQuery(id+"F3.wireOp",EDGE,"E337"),sQuery(id+"F3.wireOp",EDGE,"E338"),sQuery(id+"F3.wireOp",EDGE,"E339"),sQuery(id+"F3.wireOp",EDGE,"E340"),sQuery(id+"F3.wireOp",EDGE,"E341"),sQuery(id+"F3.wireOp",EDGE,"E342"),sQuery(id+"F3.wireOp",EDGE,"E343"),sQuery(id+"F3.wireOp",EDGE,"E344"),sQuery(id+"F3.wireOp",EDGE,"E345"),sQuery(id+"F3.wireOp",EDGE,"E346"),sQuery(id+"F3.wireOp",EDGE,"E347"),sQuery(id+"F3.wireOp",EDGE,"E348"),sQuery(id+"F3.wireOp",EDGE,"E349"),sQuery(id+"F3.wireOp",EDGE,"E350"),sQuery(id+"F3.wireOp",EDGE,"E351"),sQuery(id+"F3.wireOp",EDGE,"E352"),sQuery(id+"F3.wireOp",EDGE,"E353"),sQuery(id+"F3.wireOp",EDGE,"E354"),sQuery(id+"F3.wireOp",EDGE,"E355"),sQuery(id+"F3.wireOp",EDGE,"E356"),sQuery(id+"F3.wireOp",EDGE,"E357"),sQuery(id+"F3.wireOp",EDGE,"E358"),sQuery(id+"F3.wireOp",EDGE,"E359"),sQuery(id+"F3.wireOp",EDGE,"E360"),sQuery(id+"F3.wireOp",EDGE,"E361"),sQuery(id+"F3.wireOp",EDGE,"E362"),sQuery(id+"F3.wireOp",EDGE,"E363"),sQuery(id+"F3.wireOp",EDGE,"E364"),sQuery(id+"F3.wireOp",EDGE,"E365"),sQuery(id+"F3.wireOp",EDGE,"E366"),sQuery(id+"F3.wireOp",EDGE,"E367"),sQuery(id+"F3.wireOp",EDGE,"E368"),sQuery(id+"F3.wireOp",EDGE,"E369"),sQuery(id+"F3.wireOp",EDGE,"E370"),sQuery(id+"F3.wireOp",EDGE,"E371"),sQuery(id+"F3.wireOp",EDGE,"E372"),sQuery(id+"F3.wireOp",EDGE,"E373"),sQuery(id+"F3.wireOp",EDGE,"E374"),sQuery(id+"F3.wireOp",EDGE,"E375"),sQuery(id+"F3.wireOp",EDGE,"E376"),sQuery(id+"F3.wireOp",EDGE,"E377"),sQuery(id+"F3.wireOp",EDGE,"E378"),sQuery(id+"F3.wireOp",EDGE,"E379"),sQuery(id+"F3.wireOp",EDGE,"E380"),sQuery(id+"F3.wireOp",EDGE,"E381"),sQuery(id+"F3.wireOp",EDGE,"E382"),sQuery(id+"F3.wireOp",EDGE,"E383"),sQuery(id+"F3.wireOp",EDGE,"E384"),sQuery(id+"F3.wireOp",EDGE,"E385"),sQuery(id+"F3.wireOp",EDGE,"E386"),sQuery(id+"F3.wireOp",EDGE,"E387"),sQuery(id+"F3.wireOp",EDGE,"E388"),sQuery(id+"F3.wireOp",EDGE,"E389"),sQuery(id+"F3.wireOp",EDGE,"E390"),sQuery(id+"F3.wireOp",EDGE,"E391"),sQuery(id+"F3.wireOp",EDGE,"E392"),sQuery(id+"F3.wireOp",EDGE,"E393"),sQuery(id+"F3.wireOp",EDGE,"E394"),sQuery(id+"F3.wireOp",EDGE,"E395"),sQuery(id+"F3.wireOp",EDGE,"E396"),sQuery(id+"F3.wireOp",EDGE,"E397"),sQuery(id+"F3.wireOp",EDGE,"E398"),sQuery(id+"F3.wireOp",EDGE,"E399"),sQuery(id+"F3.wireOp",EDGE,"E400"),sQuery(id+"F3.wireOp",EDGE,"E401"),sQuery(id+"F3.wireOp",EDGE,"E402"),sQuery(id+"F3.wireOp",EDGE,"E403"),sQuery(id+"F3.wireOp",EDGE,"E404"),sQuery(id+"F3.wireOp",EDGE,"E405"),sQuery(id+"F3.wireOp",EDGE,"E406"),sQuery(id+"F3.wireOp",EDGE,"E407"),sQuery(id+"F3.wireOp",EDGE,"E408"),sQuery(id+"F3.wireOp",EDGE,"E409"),sQuery(id+"F3.wireOp",EDGE,"E410"),sQuery(id+"F3.wireOp",EDGE,"E411"),sQuery(id+"F3.wireOp",EDGE,"E412"),sQuery(id+"F3.wireOp",EDGE,"E413"),sQuery(id+"F3.wireOp",EDGE,"E414"),sQuery(id+"F3.wireOp",EDGE,"E415"),sQuery(id+"F3.wireOp",EDGE,"E416"),sQuery(id+"F3.wireOp",EDGE,"E417"),sQuery(id+"F3.wireOp",EDGE,"E418"),sQuery(id+"F3.wireOp",EDGE,"E419"),sQuery(id+"F3.wireOp",EDGE,"E420"),sQuery(id+"F3.wireOp",EDGE,"E421"),sQuery(id+"F3.wireOp",EDGE,"E422"),sQuery(id+"F3.wireOp",EDGE,"E423"),sQuery(id+"F3.wireOp",EDGE,"E424"),sQuery(id+"F3.wireOp",EDGE,"E425"),sQuery(id+"F3.wireOp",EDGE,"E426"),sQuery(id+"F3.wireOp",EDGE,"E427"),sQuery(id+"F3.wireOp",EDGE,"E428"),sQuery(id+"F3.wireOp",EDGE,"E429"),sQuery(id+"F3.wireOp",EDGE,"E430"),sQuery(id+"F3.wireOp",EDGE,"E431"),sQuery(id+"F3.wireOp",EDGE,"E432"),sQuery(id+"F3.wireOp",EDGE,"E433"),sQuery(id+"F3.wireOp",EDGE,"E434"),sQuery(id+"F3.wireOp",EDGE,"E435"),sQuery(id+"F3.wireOp",EDGE,"E436"),sQuery(id+"F3.wireOp",EDGE,"E437"),sQuery(id+"F3.wireOp",EDGE,"E438"),sQuery(id+"F3.wireOp",EDGE,"E439"),sQuery(id+"F3.wireOp",EDGE,"E440"),sQuery(id+"F3.wireOp",EDGE,"E441"),sQuery(id+"F3.wireOp",EDGE,"E442"),sQuery(id+"F3.wireOp",EDGE,"E443"),sQuery(id+"F3.wireOp",EDGE,"E444"),sQuery(id+"F3.wireOp",EDGE,"E445"),sQuery(id+"F3.wireOp",EDGE,"E446"),sQuery(id+"F3.wireOp",EDGE,"E447"),sQuery(id+"F3.wireOp",EDGE,"E448"),sQuery(id+"F3.wireOp",EDGE,"E449"),sQuery(id+"F3.wireOp",EDGE,"E450"),sQuery(id+"F3.wireOp",EDGE,"E451"),sQuery(id+"F3.wireOp",EDGE,"E452"),sQuery(id+"F3.wireOp",EDGE,"E453"),sQuery(id+"F3.wireOp",EDGE,"E454"),sQuery(id+"F3.wireOp",EDGE,"E455"),sQuery(id+"F3.wireOp",EDGE,"E456"),sQuery(id+"F3.wireOp",EDGE,"E457"),sQuery(id+"F3.wireOp",EDGE,"E458"),sQuery(id+"F3.wireOp",EDGE,"E459"),sQuery(id+"F3.wireOp",EDGE,"E460"),sQuery(id+"F3.wireOp",EDGE,"E461"),sQuery(id+"F3.wireOp",EDGE,"E462"),sQuery(id+"F3.wireOp",EDGE,"E463"),sQuery(id+"F3.wireOp",EDGE,"E464"),sQuery(id+"F3.wireOp",EDGE,"E465"),sQuery(id+"F3.wireOp",EDGE,"E466"),sQuery(id+"F3.wireOp",EDGE,"E467"),sQuery(id+"F3.wireOp",EDGE,"E468"),sQuery(id+"F3.wireOp",EDGE,"E469"),sQuery(id+"F3.wireOp",EDGE,"E470"),sQuery(id+"F3.wireOp",EDGE,"E471"),sQuery(id+"F3.wireOp",EDGE,"E472"),sQuery(id+"F3.wireOp",EDGE,"E473"),sQuery(id+"F3.wireOp",EDGE,"E474"),sQuery(id+"F3.wireOp",EDGE,"E475"),sQuery(id+"F3.wireOp",EDGE,"E476"),sQuery(id+"F3.wireOp",EDGE,"E477"),sQuery(id+"F3.wireOp",EDGE,"E478"),sQuery(id+"F3.wireOp",EDGE,"E479"),sQuery(id+"F3.wireOp",EDGE,"E480"),sQuery(id+"F3.wireOp",EDGE,"E481"),sQuery(id+"F3.wireOp",EDGE,"E482"),sQuery(id+"F3.wireOp",EDGE,"E483"),sQuery(id+"F3.wireOp",EDGE,"E484"),sQuery(id+"F3.wireOp",EDGE,"E485"),sQuery(id+"F3.wireOp",EDGE,"E486"),sQuery(id+"F3.wireOp",EDGE,"E487"),sQuery(id+"F3.wireOp",EDGE,"E488"),sQuery(id+"F3.wireOp",EDGE,"E489"),sQuery(id+"F3.wireOp",EDGE,"E490"),sQuery(id+"F3.wireOp",EDGE,"E491"),sQuery(id+"F3.wireOp",EDGE,"E492"),sQuery(id+"F3.wireOp",EDGE,"E493"),sQuery(id+"F3.wireOp",EDGE,"E494"),sQuery(id+"F3.wireOp",EDGE,"E495"),sQuery(id+"F3.wireOp",EDGE,"E496"),sQuery(id+"F3.wireOp",EDGE,"E497"),sQuery(id+"F3.wireOp",EDGE,"E498"),sQuery(id+"F3.wireOp",EDGE,"E499"),sQuery(id+"F3.wireOp",EDGE,"E500"),sQuery(id+"F3.wireOp",EDGE,"E501"),sQuery(id+"F3.wireOp",EDGE,"E502"),sQuery(id+"F3.wireOp",EDGE,"E503"),sQuery(id+"F3.wireOp",EDGE,"E504"),sQuery(id+"F3.wireOp",EDGE,"E505"),sQuery(id+"F3.wireOp",EDGE,"E506"),sQuery(id+"F3.wireOp",EDGE,"E507"),sQuery(id+"F3.wireOp",EDGE,"E508"),sQuery(id+"F3.wireOp",EDGE,"E509"),sQuery(id+"F3.wireOp",EDGE,"E510"),sQuery(id+"F3.wireOp",EDGE,"E511"),sQuery(id+"F3.wireOp",EDGE,"E512"),sQuery(id+"F3.wireOp",EDGE,"E513"),sQuery(id+"F3.wireOp",EDGE,"E514"),sQuery(id+"F3.wireOp",EDGE,"E515"),sQuery(id+"F3.wireOp",EDGE,"E516"),sQuery(id+"F3.wireOp",EDGE,"E517"),sQuery(id+"F3.wireOp",EDGE,"E518"),sQuery(id+"F3.wireOp",EDGE,"E519"),sQuery(id+"F3.wireOp",EDGE,"E520"),sQuery(id+"F3.wireOp",EDGE,"E521"),sQuery(id+"F3.wireOp",EDGE,"E522"),sQuery(id+"F3.wireOp",EDGE,"E523"),sQuery(id+"F3.wireOp",EDGE,"E524"),sQuery(id+"F3.wireOp",EDGE,"E525"),sQuery(id+"F3.wireOp",EDGE,"E526"),sQuery(id+"F3.wireOp",EDGE,"E527"),sQuery(id+"F3.wireOp",EDGE,"E528"),sQuery(id+"F3.wireOp",EDGE,"E529"),sQuery(id+"F3.wireOp",EDGE,"E530"),sQuery(id+"F3.wireOp",EDGE,"E531"),sQuery(id+"F3.wireOp",EDGE,"E532"),sQuery(id+"F3.wireOp",EDGE,"E533"),sQuery(id+"F3.wireOp",EDGE,"E534"),sQuery(id+"F3.wireOp",EDGE,"E535"),sQuery(id+"F3.wireOp",EDGE,"E536"),sQuery(id+"F3.wireOp",EDGE,"E537"),sQuery(id+"F3.wireOp",EDGE,"E538"),sQuery(id+"F3.wireOp",EDGE,"E539"),sQuery(id+"F3.wireOp",EDGE,"E540"),sQuery(id+"F3.wireOp",EDGE,"E541"),sQuery(id+"F3.wireOp",EDGE,"E542"),sQuery(id+"F3.wireOp",EDGE,"E543"),sQuery(id+"F3.wireOp",EDGE,"E544"),sQuery(id+"F3.wireOp",EDGE,"E545"),sQuery(id+"F3.wireOp",EDGE,"E546"),sQuery(id+"F3.wireOp",EDGE,"E547"),sQuery(id+"F3.wireOp",EDGE,"E548"),sQuery(id+"F3.wireOp",EDGE,"E549"),sQuery(id+"F3.wireOp",EDGE,"E550"),sQuery(id+"F3.wireOp",EDGE,"E551"),sQuery(id+"F3.wireOp",EDGE,"E552"),sQuery(id+"F3.wireOp",EDGE,"E553"),sQuery(id+"F3.wireOp",EDGE,"E554"),sQuery(id+"F3.wireOp",EDGE,"E555"),sQuery(id+"F3.wireOp",EDGE,"E556"),sQuery(id+"F3.wireOp",EDGE,"E557"),sQuery(id+"F3.wireOp",EDGE,"E558"),sQuery(id+"F3.wireOp",EDGE,"E559"),sQuery(id+"F3.wireOp",EDGE,"E560"),sQuery(id+"F3.wireOp",EDGE,"E561"),sQuery(id+"F3.wireOp",EDGE,"E562"),sQuery(id+"F3.wireOp",EDGE,"E563"),sQuery(id+"F3.wireOp",EDGE,"E564"),sQuery(id+"F3.wireOp",EDGE,"E565"),sQuery(id+"F3.wireOp",EDGE,"E566"),sQuery(id+"F3.wireOp",EDGE,"E567"),sQuery(id+"F3.wireOp",EDGE,"E568"),sQuery(id+"F3.wireOp",EDGE,"E569"),sQuery(id+"F3.wireOp",EDGE,"E570"),sQuery(id+"F3.wireOp",EDGE,"E571"),sQuery(id+"F3.wireOp",EDGE,"E572"),sQuery(id+"F3.wireOp",EDGE,"E573"),sQuery(id+"F3.wireOp",EDGE,"E574"),sQuery(id+"F3.wireOp",EDGE,"E575"),sQuery(id+"F3.wireOp",EDGE,"E576"),sQuery(id+"F3.wireOp",EDGE,"E577"),sQuery(id+"F3.wireOp",EDGE,"E578"),sQuery(id+"F3.wireOp",EDGE,"E579"),sQuery(id+"F3.wireOp",EDGE,"E580"),sQuery(id+"F3.wireOp",EDGE,"E581"),sQuery(id+"F3.wireOp",EDGE,"E582"),sQuery(id+"F3.wireOp",EDGE,"E583"),sQuery(id+"F3.wireOp",EDGE,"E584"),sQuery(id+"F3.wireOp",EDGE,"E585"),sQuery(id+"F3.wireOp",EDGE,"E586"),sQuery(id+"F3.wireOp",EDGE,"E587"),sQuery(id+"F3.wireOp",EDGE,"E588"),sQuery(id+"F3.wireOp",EDGE,"E589"),sQuery(id+"F3.wireOp",EDGE,"E590"),sQuery(id+"F3.wireOp",EDGE,"E591"),sQuery(id+"F3.wireOp",EDGE,"E592"),sQuery(id+"F3.wireOp",EDGE,"E593"),sQuery(id+"F3.wireOp",EDGE,"E594"),sQuery(id+"F3.wireOp",EDGE,"E595"),sQuery(id+"F3.wireOp",EDGE,"E596"),sQuery(id+"F3.wireOp",EDGE,"E597"),sQuery(id+"F3.wireOp",EDGE,"E598"),sQuery(id+"F3.wireOp",EDGE,"E599"),sQuery(id+"F3.wireOp",EDGE,"E600"),sQuery(id+"F3.wireOp",EDGE,"E601"),sQuery(id+"F3.wireOp",EDGE,"E602"),sQuery(id+"F3.wireOp",EDGE,"E603"),sQuery(id+"F3.wireOp",EDGE,"E604"),sQuery(id+"F3.wireOp",EDGE,"E605"),sQuery(id+"F3.wireOp",EDGE,"E606"),sQuery(id+"F3.wireOp",EDGE,"E607"),sQuery(id+"F3.wireOp",EDGE,"E608"),sQuery(id+"F3.wireOp",EDGE,"E609"),sQuery(id+"F3.wireOp",EDGE,"E610"),sQuery(id+"F3.wireOp",EDGE,"E611"),sQuery(id+"F3.wireOp",EDGE,"E612"),sQuery(id+"F3.wireOp",EDGE,"E613"),sQuery(id+"F3.wireOp",EDGE,"E614"),sQuery(id+"F3.wireOp",EDGE,"E615"),sQuery(id+"F3.wireOp",EDGE,"E616"),sQuery(id+"F3.wireOp",EDGE,"E617"),sQuery(id+"F3.wireOp",EDGE,"E618"),sQuery(id+"F3.wireOp",EDGE,"E619"),sQuery(id+"F3.wireOp",EDGE,"E620"),sQuery(id+"F3.wireOp",EDGE,"E621"),sQuery(id+"F3.wireOp",EDGE,"E622"),sQuery(id+"F3.wireOp",EDGE,"E623"),sQuery(id+"F3.wireOp",EDGE,"E624"),sQuery(id+"F3.wireOp",EDGE,"E625"),sQuery(id+"F3.wireOp",EDGE,"E626"),sQuery(id+"F3.wireOp",EDGE,"E627"),sQuery(id+"F3.wireOp",EDGE,"E628"),sQuery(id+"F3.wireOp",EDGE,"E629"),sQuery(id+"F3.wireOp",EDGE,"E630"),sQuery(id+"F3.wireOp",EDGE,"E631"),sQuery(id+"F3.wireOp",EDGE,"E632"),sQuery(id+"F3.wireOp",EDGE,"E633"),sQuery(id+"F3.wireOp",EDGE,"E634"),sQuery(id+"F3.wireOp",EDGE,"E635"),sQuery(id+"F3.wireOp",EDGE,"E636"),sQuery(id+"F3.wireOp",EDGE,"E637"),sQuery(id+"F3.wireOp",EDGE,"E638"),sQuery(id+"F3.wireOp",EDGE,"E639"),sQuery(id+"F3.wireOp",EDGE,"E640"),sQuery(id+"F3.wireOp",EDGE,"E641"),sQuery(id+"F3.wireOp",EDGE,"E642"),sQuery(id+"F3.wireOp",EDGE,"E643"),sQuery(id+"F3.wireOp",EDGE,"E644"),sQuery(id+"F3.wireOp",EDGE,"E645"),sQuery(id+"F3.wireOp",EDGE,"E646"),sQuery(id+"F3.wireOp",EDGE,"E647"),sQuery(id+"F3.wireOp",EDGE,"E648"),sQuery(id+"F3.wireOp",EDGE,"E649"),sQuery(id+"F3.wireOp",EDGE,"E650"),sQuery(id+"F3.wireOp",EDGE,"E651"),sQuery(id+"F3.wireOp",EDGE,"E652"),sQuery(id+"F3.wireOp",EDGE,"E653"),sQuery(id+"F3.wireOp",EDGE,"E654"),sQuery(id+"F3.wireOp",EDGE,"E655"),sQuery(id+"F3.wireOp",EDGE,"E656"),sQuery(id+"F3.wireOp",EDGE,"E657"),sQuery(id+"F3.wireOp",EDGE,"E658"),sQuery(id+"F3.wireOp",EDGE,"E659"),sQuery(id+"F3.wireOp",EDGE,"E660"),sQuery(id+"F3.wireOp",EDGE,"E661"),sQuery(id+"F3.wireOp",EDGE,"E662"),sQuery(id+"F3.wireOp",EDGE,"E663"),sQuery(id+"F3.wireOp",EDGE,"E664"),sQuery(id+"F3.wireOp",EDGE,"E665"),sQuery(id+"F3.wireOp",EDGE,"E666"),sQuery(id+"F3.wireOp",EDGE,"E667"),sQuery(id+"F3.wireOp",EDGE,"E668"),sQuery(id+"F3.wireOp",EDGE,"E669"),sQuery(id+"F3.wireOp",EDGE,"E670"),sQuery(id+"F3.wireOp",EDGE,"E671"),sQuery(id+"F3.wireOp",EDGE,"E672"),sQuery(id+"F3.wireOp",EDGE,"E673"),sQuery(id+"F3.wireOp",EDGE,"E674"),sQuery(id+"F3.wireOp",EDGE,"E675"),sQuery(id+"F3.wireOp",EDGE,"E676"),sQuery(id+"F3.wireOp",EDGE,"E677"),sQuery(id+"F3.wireOp",EDGE,"E678"),sQuery(id+"F3.wireOp",EDGE,"E679"),sQuery(id+"F3.wireOp",EDGE,"E680"),sQuery(id+"F3.wireOp",EDGE,"E681"),sQuery(id+"F3.wireOp",EDGE,"E682"),sQuery(id+"F3.wireOp",EDGE,"E683"),sQuery(id+"F3.wireOp",EDGE,"E684"),sQuery(id+"F3.wireOp",EDGE,"E685"),sQuery(id+"F3.wireOp",EDGE,"E686"),sQuery(id+"F3.wireOp",EDGE,"E687"),sQuery(id+"F3.wireOp",EDGE,"E688"),sQuery(id+"F3.wireOp",EDGE,"E689"),sQuery(id+"F3.wireOp",EDGE,"E690"),sQuery(id+"F3.wireOp",EDGE,"E691"),sQuery(id+"F3.wireOp",EDGE,"E692"),sQuery(id+"F3.wireOp",EDGE,"E693"),sQuery(id+"F3.wireOp",EDGE,"E694"),sQuery(id+"F3.wireOp",EDGE,"E695"),sQuery(id+"F3.wireOp",EDGE,"E696"),sQuery(id+"F3.wireOp",EDGE,"E697"),sQuery(id+"F3.wireOp",EDGE,"E698"),sQuery(id+"F3.wireOp",EDGE,"E699"),sQuery(id+"F3.wireOp",EDGE,"E700"),sQuery(id+"F3.wireOp",EDGE,"E701"),sQuery(id+"F3.wireOp",EDGE,"E702"),sQuery(id+"F3.wireOp",EDGE,"E703"),sQuery(id+"F3.wireOp",EDGE,"E704"),sQuery(id+"F3.wireOp",EDGE,"E705"),sQuery(id+"F3.wireOp",EDGE,"E706"),sQuery(id+"F3.wireOp",EDGE,"E707"),sQuery(id+"F3.wireOp",EDGE,"E708"),sQuery(id+"F3.wireOp",EDGE,"E709"),sQuery(id+"F3.wireOp",EDGE,"E710"),sQuery(id+"F3.wireOp",EDGE,"E711"),sQuery(id+"F3.wireOp",EDGE,"E712"),sQuery(id+"F3.wireOp",EDGE,"E713"),sQuery(id+"F3.wireOp",EDGE,"E714"),sQuery(id+"F3.wireOp",EDGE,"E715"),sQuery(id+"F3.wireOp",EDGE,"E716"),sQuery(id+"F3.wireOp",EDGE,"E717"),sQuery(id+"F3.wireOp",EDGE,"E718"),sQuery(id+"F3.wireOp",EDGE,"E719"),sQuery(id+"F3.wireOp",EDGE,"E720"),sQuery(id+"F3.wireOp",EDGE,"E721"),sQuery(id+"F3.wireOp",EDGE,"E722"),sQuery(id+"F3.wireOp",EDGE,"E723"),sQuery(id+"F3.wireOp",EDGE,"E724"),sQuery(id+"F3.wireOp",EDGE,"E725"),sQuery(id+"F3.wireOp",EDGE,"E726"),sQuery(id+"F3.wireOp",EDGE,"E727"),sQuery(id+"F3.wireOp",EDGE,"E728"),sQuery(id+"F3.wireOp",EDGE,"E729"),sQuery(id+"F3.wireOp",EDGE,"E730"),sQuery(id+"F3.wireOp",EDGE,"E731"),sQuery(id+"F3.wireOp",EDGE,"E732"),sQuery(id+"F3.wireOp",EDGE,"E733"),sQuery(id+"F3.wireOp",EDGE,"E734"),sQuery(id+"F3.wireOp",EDGE,"E735"),sQuery(id+"F3.wireOp",EDGE,"E736"),sQuery(id+"F3.wireOp",EDGE,"E737"),sQuery(id+"F3.wireOp",EDGE,"E738"),sQuery(id+"F3.wireOp",EDGE,"E739"),sQuery(id+"F3.wireOp",EDGE,"E740"),sQuery(id+"F3.wireOp",EDGE,"E741"),sQuery(id+"F3.wireOp",EDGE,"E742"),sQuery(id+"F3.wireOp",EDGE,"E743"),sQuery(id+"F3.wireOp",EDGE,"E744"),sQuery(id+"F3.wireOp",EDGE,"E745"),sQuery(id+"F3.wireOp",EDGE,"E746"),sQuery(id+"F3.wireOp",EDGE,"E747"),sQuery(id+"F3.wireOp",EDGE,"E748"),sQuery(id+"F3.wireOp",EDGE,"E749"),sQuery(id+"F3.wireOp",EDGE,"E750"),sQuery(id+"F3.wireOp",EDGE,"E751"),sQuery(id+"F3.wireOp",EDGE,"E752"),sQuery(id+"F3.wireOp",EDGE,"E753"),sQuery(id+"F3.wireOp",EDGE,"E754"),sQuery(id+"F3.wireOp",EDGE,"E755"),sQuery(id+"F3.wireOp",EDGE,"E756"),sQuery(id+"F3.wireOp",EDGE,"E757"),sQuery(id+"F3.wireOp",EDGE,"E758"),sQuery(id+"F3.wireOp",EDGE,"E759"),sQuery(id+"F3.wireOp",EDGE,"E760"),sQuery(id+"F3.wireOp",EDGE,"E761"),sQuery(id+"F3.wireOp",EDGE,"E762"),sQuery(id+"F3.wireOp",EDGE,"E763"),sQuery(id+"F3.wireOp",EDGE,"E764"),sQuery(id+"F3.wireOp",EDGE,"E765"),sQuery(id+"F3.wireOp",EDGE,"E766"),sQuery(id+"F3.wireOp",EDGE,"E767"),sQuery(id+"F3.wireOp",EDGE,"E768"),sQuery(id+"F3.wireOp",EDGE,"E769"),sQuery(id+"F3.wireOp",EDGE,"E770"),sQuery(id+"F3.wireOp",EDGE,"E771"),sQuery(id+"F3.wireOp",EDGE,"E772"),sQuery(id+"F3.wireOp",EDGE,"E773"),sQuery(id+"F3.wireOp",EDGE,"E774"),sQuery(id+"F3.wireOp",EDGE,"E775"),sQuery(id+"F3.wireOp",EDGE,"E776"),sQuery(id+"F3.wireOp",EDGE,"E777"),sQuery(id+"F3.wireOp",EDGE,"E778"),sQuery(id+"F3.wireOp",EDGE,"E779"),sQuery(id+"F3.wireOp",EDGE,"E780"),sQuery(id+"F3.wireOp",EDGE,"E781"),sQuery(id+"F3.wireOp",EDGE,"E782"),sQuery(id+"F3.wireOp",EDGE,"E783"),sQuery(id+"F3.wireOp",EDGE,"E784"),sQuery(id+"F3.wireOp",EDGE,"E785"),sQuery(id+"F3.wireOp",EDGE,"E786"),sQuery(id+"F3.wireOp",EDGE,"E787"),sQuery(id+"F3.wireOp",EDGE,"E788"),sQuery(id+"F3.wireOp",EDGE,"E789"),sQuery(id+"F3.wireOp",EDGE,"E790"),sQuery(id+"F3.wireOp",EDGE,"E791"),sQuery(id+"F3.wireOp",EDGE,"E792"),sQuery(id+"F3.wireOp",EDGE,"E793"),sQuery(id+"F3.wireOp",EDGE,"E794"),sQuery(id+"F3.wireOp",EDGE,"E795"),sQuery(id+"F3.wireOp",EDGE,"E796"),sQuery(id+"F3.wireOp",EDGE,"E797"),sQuery(id+"F3.wireOp",EDGE,"E798"),sQuery(id+"F3.wireOp",EDGE,"E799"),sQuery(id+"F3.wireOp",EDGE,"E800"),sQuery(id+"F3.wireOp",EDGE,"E801"),sQuery(id+"F3.wireOp",EDGE,"E802"),sQuery(id+"F3.wireOp",EDGE,"E803"),sQuery(id+"F3.wireOp",EDGE,"E804"),sQuery(id+"F3.wireOp",EDGE,"E805"),sQuery(id+"F3.wireOp",EDGE,"E806"),sQuery(id+"F3.wireOp",EDGE,"E807"),sQuery(id+"F3.wireOp",EDGE,"E808"),sQuery(id+"F3.wireOp",EDGE,"E809"),sQuery(id+"F3.wireOp",EDGE,"E810"),sQuery(id+"F3.wireOp",EDGE,"E811"),sQuery(id+"F3.wireOp",EDGE,"E812"),sQuery(id+"F3.wireOp",EDGE,"E813"),sQuery(id+"F3.wireOp",EDGE,"E814"),sQuery(id+"F3.wireOp",EDGE,"E815"),sQuery(id+"F3.wireOp",EDGE,"E816"),sQuery(id+"F3.wireOp",EDGE,"E817"),sQuery(id+"F3.wireOp",EDGE,"E818"),sQuery(id+"F3.wireOp",EDGE,"E819"),sQuery(id+"F3.wireOp",EDGE,"E820"),sQuery(id+"F3.wireOp",EDGE,"E821"),sQuery(id+"F3.wireOp",EDGE,"E822"),sQuery(id+"F3.wireOp",EDGE,"E823"),sQuery(id+"F3.wireOp",EDGE,"E824"),sQuery(id+"F3.wireOp",EDGE,"E825"),sQuery(id+"F3.wireOp",EDGE,"E826"),sQuery(id+"F3.wireOp",EDGE,"E827"),sQuery(id+"F3.wireOp",EDGE,"E828"),sQuery(id+"F3.wireOp",EDGE,"E829"),sQuery(id+"F3.wireOp",EDGE,"E830"),sQuery(id+"F3.wireOp",EDGE,"E831"),sQuery(id+"F3.wireOp",EDGE,"E832"),sQuery(id+"F3.wireOp",EDGE,"E833"),sQuery(id+"F3.wireOp",EDGE,"E834"),sQuery(id+"F3.wireOp",EDGE,"E835"),sQuery(id+"F3.wireOp",EDGE,"E836"),sQuery(id+"F3.wireOp",EDGE,"E837"),sQuery(id+"F3.wireOp",EDGE,"E838"),sQuery(id+"F3.wireOp",EDGE,"E839"),sQuery(id+"F3.wireOp",EDGE,"E840"),sQuery(id+"F3.wireOp",EDGE,"E841"),sQuery(id+"F3.wireOp",EDGE,"E842"),sQuery(id+"F3.wireOp",EDGE,"E843"),sQuery(id+"F3.wireOp",EDGE,"E844"),sQuery(id+"F3.wireOp",EDGE,"E845"),sQuery(id+"F3.wireOp",EDGE,"E846"),sQuery(id+"F3.wireOp",EDGE,"E847"),sQuery(id+"F3.wireOp",EDGE,"E848"),sQuery(id+"F3.wireOp",EDGE,"E849"),sQuery(id+"F3.wireOp",EDGE,"E850"),sQuery(id+"F3.wireOp",EDGE,"E851"),sQuery(id+"F3.wireOp",EDGE,"E852"),sQuery(id+"F3.wireOp",EDGE,"E853"),sQuery(id+"F3.wireOp",EDGE,"E854"),sQuery(id+"F3.wireOp",EDGE,"E855"),sQuery(id+"F3.wireOp",EDGE,"E856"),sQuery(id+"F3.wireOp",EDGE,"E857"),sQuery(id+"F3.wireOp",EDGE,"E858"),sQuery(id+"F3.wireOp",EDGE,"E859"),sQuery(id+"F3.wireOp",EDGE,"E860"),sQuery(id+"F3.wireOp",EDGE,"E861"),sQuery(id+"F3.wireOp",EDGE,"E862"),sQuery(id+"F3.wireOp",EDGE,"E863"),sQuery(id+"F3.wireOp",EDGE,"E864"),sQuery(id+"F3.wireOp",EDGE,"E865"),sQuery(id+"F3.wireOp",EDGE,"E866"),sQuery(id+"F3.wireOp",EDGE,"E867"),sQuery(id+"F3.wireOp",EDGE,"E868"),sQuery(id+"F3.wireOp",EDGE,"E869"),sQuery(id+"F3.wireOp",EDGE,"E870"),sQuery(id+"F3.wireOp",EDGE,"E871"),sQuery(id+"F3.wireOp",EDGE,"E872"),sQuery(id+"F3.wireOp",EDGE,"E873"),sQuery(id+"F3.wireOp",EDGE,"E874"),sQuery(id+"F3.wireOp",EDGE,"E875"),sQuery(id+"F3.wireOp",EDGE,"E876"),sQuery(id+"F3.wireOp",EDGE,"E877"),sQuery(id+"F3.wireOp",EDGE,"E878"),sQuery(id+"F3.wireOp",EDGE,"E879"),sQuery(id+"F3.wireOp",EDGE,"E880"),sQuery(id+"F3.wireOp",EDGE,"E881"),sQuery(id+"F3.wireOp",EDGE,"E882"),sQuery(id+"F3.wireOp",EDGE,"E883"),sQuery(id+"F3.wireOp",EDGE,"E884"),sQuery(id+"F3.wireOp",EDGE,"E885"),sQuery(id+"F3.wireOp",EDGE,"E886"),sQuery(id+"F3.wireOp",EDGE,"E887"),sQuery(id+"F3.wireOp",EDGE,"E888"),sQuery(id+"F3.wireOp",EDGE,"E889"),sQuery(id+"F3.wireOp",EDGE,"E890"),sQuery(id+"F3.wireOp",EDGE,"E891"),sQuery(id+"F3.wireOp",EDGE,"E892"),sQuery(id+"F3.wireOp",EDGE,"E893"),sQuery(id+"F3.wireOp",EDGE,"E894"),sQuery(id+"F3.wireOp",EDGE,"E895"),sQuery(id+"F3.wireOp",EDGE,"E896"),sQuery(id+"F3.wireOp",EDGE,"E897"),sQuery(id+"F3.wireOp",EDGE,"E898"),sQuery(id+"F3.wireOp",EDGE,"E899"),sQuery(id+"F3.wireOp",EDGE,"E900"),sQuery(id+"F3.wireOp",EDGE,"E901"),sQuery(id+"F3.wireOp",EDGE,"E902"),sQuery(id+"F3.wireOp",EDGE,"E903"),sQuery(id+"F3.wireOp",EDGE,"E904"),sQuery(id+"F3.wireOp",EDGE,"E905"),sQuery(id+"F3.wireOp",EDGE,"E906"),sQuery(id+"F3.wireOp",EDGE,"E907"),sQuery(id+"F3.wireOp",EDGE,"E908"),sQuery(id+"F3.wireOp",EDGE,"E909"),sQuery(id+"F3.wireOp",EDGE,"E910"),sQuery(id+"F3.wireOp",EDGE,"E911"),sQuery(id+"F3.wireOp",EDGE,"E912"),sQuery(id+"F3.wireOp",EDGE,"E913"),sQuery(id+"F3.wireOp",EDGE,"E914"),sQuery(id+"F3.wireOp",EDGE,"E915"),sQuery(id+"F3.wireOp",EDGE,"E916"),sQuery(id+"F3.wireOp",EDGE,"E917"),sQuery(id+"F3.wireOp",EDGE,"E918"),sQuery(id+"F3.wireOp",EDGE,"E919"),sQuery(id+"F3.wireOp",EDGE,"E920"),sQuery(id+"F3.wireOp",EDGE,"E921"),sQuery(id+"F3.wireOp",EDGE,"E922"),sQuery(id+"F3.wireOp",EDGE,"E923"),sQuery(id+"F3.wireOp",EDGE,"E924"),sQuery(id+"F3.wireOp",EDGE,"E925"),sQuery(id+"F3.wireOp",EDGE,"E926"),sQuery(id+"F3.wireOp",EDGE,"E927"),sQuery(id+"F3.wireOp",EDGE,"E928"),sQuery(id+"F3.wireOp",EDGE,"E929"),sQuery(id+"F3.wireOp",EDGE,"E930"),sQuery(id+"F3.wireOp",EDGE,"E931"),sQuery(id+"F3.wireOp",EDGE,"E932"),sQuery(id+"F3.wireOp",EDGE,"E933"),sQuery(id+"F3.wireOp",EDGE,"E934"),sQuery(id+"F3.wireOp",EDGE,"E935"),sQuery(id+"F3.wireOp",EDGE,"E936"),sQuery(id+"F3.wireOp",EDGE,"E937"),sQuery(id+"F3.wireOp",EDGE,"E938"),sQuery(id+"F3.wireOp",EDGE,"E939"),sQuery(id+"F3.wireOp",EDGE,"E940"),sQuery(id+"F3.wireOp",EDGE,"E941"),sQuery(id+"F3.wireOp",EDGE,"E942"),sQuery(id+"F3.wireOp",EDGE,"E943"),sQuery(id+"F3.wireOp",EDGE,"E944"),sQuery(id+"F3.wireOp",EDGE,"E945"),sQuery(id+"F3.wireOp",EDGE,"E946"),sQuery(id+"F3.wireOp",EDGE,"E947"),sQuery(id+"F3.wireOp",EDGE,"E948"),sQuery(id+"F3.wireOp",EDGE,"E949"),sQuery(id+"F3.wireOp",EDGE,"E950"),sQuery(id+"F3.wireOp",EDGE,"E951"),sQuery(id+"F3.wireOp",EDGE,"E952"),sQuery(id+"F3.wireOp",EDGE,"E953"),sQuery(id+"F3.wireOp",EDGE,"E954"),sQuery(id+"F3.wireOp",EDGE,"E955"),sQuery(id+"F3.wireOp",EDGE,"E956"),sQuery(id+"F3.wireOp",EDGE,"E957"),sQuery(id+"F3.wireOp",EDGE,"E958"),sQuery(id+"F3.wireOp",EDGE,"E959"),sQuery(id+"F3.wireOp",EDGE,"E960"),sQuery(id+"F3.wireOp",EDGE,"E961"),sQuery(id+"F3.wireOp",EDGE,"E962"),sQuery(id+"F3.wireOp",EDGE,"E963"),sQuery(id+"F3.wireOp",EDGE,"E964"),sQuery(id+"F3.wireOp",EDGE,"E965"),sQuery(id+"F3.wireOp",EDGE,"E966"),sQuery(id+"F3.wireOp",EDGE,"E967"),sQuery(id+"F3.wireOp",EDGE,"E968"),sQuery(id+"F3.wireOp",EDGE,"E969"),sQuery(id+"F3.wireOp",EDGE,"E970"),sQuery(id+"F3.wireOp",EDGE,"E971"),sQuery(id+"F3.wireOp",EDGE,"E972"),sQuery(id+"F3.wireOp",EDGE,"E973"),sQuery(id+"F3.wireOp",EDGE,"E974"),sQuery(id+"F3.wireOp",EDGE,"E975"),sQuery(id+"F3.wireOp",EDGE,"E976"),sQuery(id+"F3.wireOp",EDGE,"E977"),sQuery(id+"F3.wireOp",EDGE,"E978"),sQuery(id+"F3.wireOp",EDGE,"E979"),sQuery(id+"F3.wireOp",EDGE,"E980"),sQuery(id+"F3.wireOp",EDGE,"E981"),sQuery(id+"F3.wireOp",EDGE,"E982"),sQuery(id+"F3.wireOp",EDGE,"E983"),sQuery(id+"F3.wireOp",EDGE,"E984"),sQuery(id+"F3.wireOp",EDGE,"E985"),sQuery(id+"F3.wireOp",EDGE,"E986"),sQuery(id+"F3.wireOp",EDGE,"E987"),sQuery(id+"F3.wireOp",EDGE,"E988"),sQuery(id+"F3.wireOp",EDGE,"E989"),sQuery(id+"F3.wireOp",EDGE,"E990"),sQuery(id+"F3.wireOp",EDGE,"E991"),sQuery(id+"F3.wireOp",EDGE,"E992"),sQuery(id+"F3.wireOp",EDGE,"E993"),sQuery(id+"F3.wireOp",EDGE,"E994"),sQuery(id+"F3.wireOp",EDGE,"E995"),sQuery(id+"F3.wireOp",EDGE,"E996"),sQuery(id+"F3.wireOp",EDGE,"E997"),sQuery(id+"F3.wireOp",EDGE,"E998"),sQuery(id+"F3.wireOp",EDGE,"E999"),sQuery(id+"F3.wireOp",EDGE,"E1000"),sQuery(id+"F3.wireOp",EDGE,"E1001"),sQuery(id+"F3.wireOp",EDGE,"E1002"),sQuery(id+"F3.wireOp",EDGE,"E1003"),sQuery(id+"F3.wireOp",EDGE,"E1004"),sQuery(id+"F3.wireOp",EDGE,"E1005"),sQuery(id+"F3.wireOp",EDGE,"E1006"),sQuery(id+"F3.wireOp",EDGE,"E1007"),sQuery(id+"F3.wireOp",EDGE,"E1008"),sQuery(id+"F3.wireOp",EDGE,"E1009"),sQuery(id+"F3.wireOp",EDGE,"E1010"),sQuery(id+"F3.wireOp",EDGE,"E1011"),sQuery(id+"F3.wireOp",EDGE,"E1012"),sQuery(id+"F3.wireOp",EDGE,"E1013"),sQuery(id+"F3.wireOp",EDGE,"E1014"),sQuery(id+"F3.wireOp",EDGE,"E1015"),sQuery(id+"F3.wireOp",EDGE,"E1016"),sQuery(id+"F3.wireOp",EDGE,"E1017"),sQuery(id+"F3.wireOp",EDGE,"E1018"),sQuery(id+"F3.wireOp",EDGE,"E1019"),sQuery(id+"F3.wireOp",EDGE,"E1020"),sQuery(id+"F3.wireOp",EDGE,"E1021"),sQuery(id+"F3.wireOp",EDGE,"E1022"),sQuery(id+"F3.wireOp",EDGE,"E1023"),sQuery(id+"F3.wireOp",EDGE,"E1024"),sQuery(id+"F3.wireOp",EDGE,"E1025"),sQuery(id+"F3.wireOp",EDGE,"E1026"),sQuery(id+"F3.wireOp",EDGE,"E1027"),sQuery(id+"F3.wireOp",EDGE,"E1028"),sQuery(id+"F3.wireOp",EDGE,"E1029"),sQuery(id+"F3.wireOp",EDGE,"E1030"),sQuery(id+"F3.wireOp",EDGE,"E1031"),sQuery(id+"F3.wireOp",EDGE,"E1032"),sQuery(id+"F3.wireOp",EDGE,"E1033"),sQuery(id+"F3.wireOp",EDGE,"E1034"),sQuery(id+"F3.wireOp",EDGE,"E1035"),sQuery(id+"F3.wireOp",EDGE,"E1036"),sQuery(id+"F3.wireOp",EDGE,"E1037"),sQuery(id+"F3.wireOp",EDGE,"E1038"),sQuery(id+"F3.wireOp",EDGE,"E1039"),sQuery(id+"F3.wireOp",EDGE,"E1040"),sQuery(id+"F3.wireOp",EDGE,"E1041"),sQuery(id+"F3.wireOp",EDGE,"E1042"),sQuery(id+"F3.wireOp",EDGE,"E1043"),sQuery(id+"F3.wireOp",EDGE,"E1044"),sQuery(id+"F3.wireOp",EDGE,"E1045"),sQuery(id+"F3.wireOp",EDGE,"E1046"),sQuery(id+"F3.wireOp",EDGE,"E1047"),sQuery(id+"F3.wireOp",EDGE,"E1048"),sQuery(id+"F3.wireOp",EDGE,"E1049"),sQuery(id+"F3.wireOp",EDGE,"E1050"),sQuery(id+"F3.wireOp",EDGE,"E1051"),sQuery(id+"F3.wireOp",EDGE,"E1052"),sQuery(id+"F3.wireOp",EDGE,"E1053"),sQuery(id+"F3.wireOp",EDGE,"E1054"),sQuery(id+"F3.wireOp",EDGE,"E1055"),sQuery(id+"F3.wireOp",EDGE,"E1056"),sQuery(id+"F3.wireOp",EDGE,"E1057"),sQuery(id+"F3.wireOp",EDGE,"E1058"),sQuery(id+"F3.wireOp",EDGE,"E1059"),sQuery(id+"F3.wireOp",EDGE,"E1060"),sQuery(id+"F3.wireOp",EDGE,"E1061"),sQuery(id+"F3.wireOp",EDGE,"E1062"),sQuery(id+"F3.wireOp",EDGE,"E1063"),sQuery(id+"F3.wireOp",EDGE,"E1064"),sQuery(id+"F3.wireOp",EDGE,"E1065"),sQuery(id+"F3.wireOp",EDGE,"E1066"),sQuery(id+"F3.wireOp",EDGE,"E1067"),sQuery(id+"F3.wireOp",EDGE,"E1068"),sQuery(id+"F3.wireOp",EDGE,"E1069"),sQuery(id+"F3.wireOp",EDGE,"E1070"),sQuery(id+"F3.wireOp",EDGE,"E1071"),sQuery(id+"F3.wireOp",EDGE,"E1072"),sQuery(id+"F3.wireOp",EDGE,"E1073"),sQuery(id+"F3.wireOp",EDGE,"E1074"),sQuery(id+"F3.wireOp",EDGE,"E1075"),sQuery(id+"F3.wireOp",EDGE,"E1076"),sQuery(id+"F3.wireOp",EDGE,"E1077"),sQuery(id+"F3.wireOp",EDGE,"E1078"),sQuery(id+"F3.wireOp",EDGE,"E1079"),sQuery(id+"F3.wireOp",EDGE,"E1080"),sQuery(id+"F3.wireOp",EDGE,"E1081"),sQuery(id+"F3.wireOp",EDGE,"E1082"),sQuery(id+"F3.wireOp",EDGE,"E1083"),sQuery(id+"F3.wireOp",EDGE,"E1084"),sQuery(id+"F3.wireOp",EDGE,"E1085"),sQuery(id+"F3.wireOp",EDGE,"E1086"),sQuery(id+"F3.wireOp",EDGE,"E1087"),sQuery(id+"F3.wireOp",EDGE,"E1088"),sQuery(id+"F3.wireOp",EDGE,"E1089"),sQuery(id+"F3.wireOp",EDGE,"E1090"),sQuery(id+"F3.wireOp",EDGE,"E1091"),sQuery(id+"F3.wireOp",EDGE,"E1092"),sQuery(id+"F3.wireOp",EDGE,"E1093"),sQuery(id+"F3.wireOp",EDGE,"E1094"),sQuery(id+"F3.wireOp",EDGE,"E1095"),sQuery(id+"F3.wireOp",EDGE,"E1096"),sQuery(id+"F3.wireOp",EDGE,"E1097"),sQuery(id+"F3.wireOp",EDGE,"E1098"),sQuery(id+"F3.wireOp",EDGE,"E1099"),sQuery(id+"F3.wireOp",EDGE,"E1100"),sQuery(id+"F3.wireOp",EDGE,"E1101"),sQuery(id+"F3.wireOp",EDGE,"E1102"),sQuery(id+"F3.wireOp",EDGE,"E1103"),sQuery(id+"F3.wireOp",EDGE,"E1104"),sQuery(id+"F3.wireOp",EDGE,"E1105"),sQuery(id+"F3.wireOp",EDGE,"E1106"),sQuery(id+"F3.wireOp",EDGE,"E1107"),sQuery(id+"F3.wireOp",EDGE,"E1108"),sQuery(id+"F3.wireOp",EDGE,"E1109"),sQuery(id+"F3.wireOp",EDGE,"E1110"),sQuery(id+"F3.wireOp",EDGE,"E1111"),sQuery(id+"F3.wireOp",EDGE,"E1112"),sQuery(id+"F3.wireOp",EDGE,"E1113"),sQuery(id+"F3.wireOp",EDGE,"E1114"),sQuery(id+"F3.wireOp",EDGE,"E1115"),sQuery(id+"F3.wireOp",EDGE,"E1116"),sQuery(id+"F3.wireOp",EDGE,"E1117"),sQuery(id+"F3.wireOp",EDGE,"E1118"),sQuery(id+"F3.wireOp",EDGE,"E1119"),sQuery(id+"F3.wireOp",EDGE,"E1120"),sQuery(id+"F3.wireOp",EDGE,"E1121"),sQuery(id+"F3.wireOp",EDGE,"E1122"),sQuery(id+"F3.wireOp",EDGE,"E1123"),sQuery(id+"F3.wireOp",EDGE,"E1124"),sQuery(id+"F3.wireOp",EDGE,"E1125"),sQuery(id+"F3.wireOp",EDGE,"E1126"),sQuery(id+"F3.wireOp",EDGE,"E1127"),sQuery(id+"F3.wireOp",EDGE,"E1128"),sQuery(id+"F3.wireOp",EDGE,"E1129"),sQuery(id+"F3.wireOp",EDGE,"E1130"),sQuery(id+"F3.wireOp",EDGE,"E1131"),sQuery(id+"F3.wireOp",EDGE,"E1132"),sQuery(id+"F3.wireOp",EDGE,"E1133"),sQuery(id+"F3.wireOp",EDGE,"E1134"),sQuery(id+"F3.wireOp",EDGE,"E1135"),sQuery(id+"F3.wireOp",EDGE,"E1136"),sQuery(id+"F3.wireOp",EDGE,"E1137"),sQuery(id+"F3.wireOp",EDGE,"E1138"),sQuery(id+"F3.wireOp",EDGE,"E1139"),sQuery(id+"F3.wireOp",EDGE,"E1140"),sQuery(id+"F3.wireOp",EDGE,"E1141"),sQuery(id+"F3.wireOp",EDGE,"E1142"),sQuery(id+"F3.wireOp",EDGE,"E1143"),sQuery(id+"F3.wireOp",EDGE,"E1144"),sQuery(id+"F3.wireOp",EDGE,"E1145"),sQuery(id+"F3.wireOp",EDGE,"E1146"),sQuery(id+"F3.wireOp",EDGE,"E1147"),sQuery(id+"F3.wireOp",EDGE,"E1148"),sQuery(id+"F3.wireOp",EDGE,"E1149"),sQuery(id+"F3.wireOp",EDGE,"E1150"),sQuery(id+"F3.wireOp",EDGE,"E1151"),sQuery(id+"F3.wireOp",EDGE,"E1152"),sQuery(id+"F3.wireOp",EDGE,"E1153"),sQuery(id+"F3.wireOp",EDGE,"E1154"),sQuery(id+"F3.wireOp",EDGE,"E1155"),sQuery(id+"F3.wireOp",EDGE,"E1156"),sQuery(id+"F3.wireOp",EDGE,"E1157"),sQuery(id+"F3.wireOp",EDGE,"E1158"),sQuery(id+"F3.wireOp",EDGE,"E1159"),sQuery(id+"F3.wireOp",EDGE,"E1160"),sQuery(id+"F3.wireOp",EDGE,"E1161"),sQuery(id+"F3.wireOp",EDGE,"E1162"),sQuery(id+"F3.wireOp",EDGE,"E1163"),sQuery(id+"F3.wireOp",EDGE,"E1164"),sQuery(id+"F3.wireOp",EDGE,"E1165"),sQuery(id+"F3.wireOp",EDGE,"E1166"),sQuery(id+"F3.wireOp",EDGE,"E1167"),sQuery(id+"F3.wireOp",EDGE,"E1168"),sQuery(id+"F3.wireOp",EDGE,"E1169"),sQuery(id+"F3.wireOp",EDGE,"E1170"),sQuery(id+"F3.wireOp",EDGE,"E1171"),sQuery(id+"F3.wireOp",EDGE,"E1172"),sQuery(id+"F3.wireOp",EDGE,"E1173"),sQuery(id+"F3.wireOp",EDGE,"E1174"),sQuery(id+"F3.wireOp",EDGE,"E1175"),sQuery(id+"F3.wireOp",EDGE,"E1176"),sQuery(id+"F3.wireOp",EDGE,"E1177"),sQuery(id+"F3.wireOp",EDGE,"E1178"),sQuery(id+"F3.wireOp",EDGE,"E1179"),sQuery(id+"F3.wireOp",EDGE,"E1180"),sQuery(id+"F3.wireOp",EDGE,"E1181"),sQuery(id+"F3.wireOp",EDGE,"E1182"),sQuery(id+"F3.wireOp",EDGE,"E1183"),sQuery(id+"F3.wireOp",EDGE,"E1184"),sQuery(id+"F3.wireOp",EDGE,"E1185"),sQuery(id+"F3.wireOp",EDGE,"E1186"),sQuery(id+"F3.wireOp",EDGE,"E1187"),sQuery(id+"F3.wireOp",EDGE,"E1188"),sQuery(id+"F3.wireOp",EDGE,"E1189"),sQuery(id+"F3.wireOp",EDGE,"E1190"),sQuery(id+"F3.wireOp",EDGE,"E1191"),sQuery(id+"F3.wireOp",EDGE,"E1192"),sQuery(id+"F3.wireOp",EDGE,"E1193"),sQuery(id+"F3.wireOp",EDGE,"E1194"),sQuery(id+"F3.wireOp",EDGE,"E1195"),sQuery(id+"F3.wireOp",EDGE,"E1196"),sQuery(id+"F3.wireOp",EDGE,"E1197"),sQuery(id+"F3.wireOp",EDGE,"E1198"),sQuery(id+"F3.wireOp",EDGE,"E1199"),sQuery(id+"F3.wireOp",EDGE,"E1200"),sQuery(id+"F3.wireOp",EDGE,"E1201"),sQuery(id+"F3.wireOp",EDGE,"E1202"),sQuery(id+"F3.wireOp",EDGE,"E1203"),sQuery(id+"F3.wireOp",EDGE,"E1204"),sQuery(id+"F3.wireOp",EDGE,"E1205"),sQuery(id+"F3.wireOp",EDGE,"E1206"),sQuery(id+"F3.wireOp",EDGE,"E1207"),sQuery(id+"F3.wireOp",EDGE,"E1208"),sQuery(id+"F3.wireOp",EDGE,"E1209"),sQuery(id+"F3.wireOp",EDGE,"E1210"),sQuery(id+"F3.wireOp",EDGE,"E1211"),sQuery(id+"F3.wireOp",EDGE,"E1212"),sQuery(id+"F3.wireOp",EDGE,"E1213"),sQuery(id+"F3.wireOp",EDGE,"E1214"),sQuery(id+"F3.wireOp",EDGE,"E1215"),sQuery(id+"F3.wireOp",EDGE,"E1216"),sQuery(id+"F3.wireOp",EDGE,"E1217"),sQuery(id+"F3.wireOp",EDGE,"E1218"),sQuery(id+"F3.wireOp",EDGE,"E1219"),sQuery(id+"F3.wireOp",EDGE,"E1220"),sQuery(id+"F3.wireOp",EDGE,"E1221"),sQuery(id+"F3.wireOp",EDGE,"E1222"),sQuery(id+"F3.wireOp",EDGE,"E1223"),sQuery(id+"F3.wireOp",EDGE,"E1224"),sQuery(id+"F3.wireOp",EDGE,"E1225"),sQuery(id+"F3.wireOp",EDGE,"E1226"),sQuery(id+"F3.wireOp",EDGE,"E1227"),sQuery(id+"F3.wireOp",EDGE,"E1228"),sQuery(id+"F3.wireOp",EDGE,"E1229"),sQuery(id+"F3.wireOp",EDGE,"E1230"),sQuery(id+"F3.wireOp",EDGE,"E1231"),sQuery(id+"F3.wireOp",EDGE,"E1232"),sQuery(id+"F3.wireOp",EDGE,"E1233"),sQuery(id+"F3.wireOp",EDGE,"E1234"),sQuery(id+"F3.wireOp",EDGE,"E1235"),sQuery(id+"F3.wireOp",EDGE,"E1236"),sQuery(id+"F3.wireOp",EDGE,"E1237"),sQuery(id+"F3.wireOp",EDGE,"E1238"),sQuery(id+"F3.wireOp",EDGE,"E1239"),sQuery(id+"F3.wireOp",EDGE,"E1240"),sQuery(id+"F3.wireOp",EDGE,"E1241"),sQuery(id+"F3.wireOp",EDGE,"E1242"),sQuery(id+"F3.wireOp",EDGE,"E1243"),sQuery(id+"F3.wireOp",EDGE,"E1244"),sQuery(id+"F3.wireOp",EDGE,"E1245"),sQuery(id+"F3.wireOp",EDGE,"E1246"),sQuery(id+"F3.wireOp",EDGE,"E1247"),sQuery(id+"F3.wireOp",EDGE,"E1248"),sQuery(id+"F3.wireOp",EDGE,"E1249"),sQuery(id+"F3.wireOp",EDGE,"E1250"),sQuery(id+"F3.wireOp",EDGE,"E1251"),sQuery(id+"F3.wireOp",EDGE,"E1252"),sQuery(id+"F3.wireOp",EDGE,"E1253"),sQuery(id+"F3.wireOp",EDGE,"E1254"),sQuery(id+"F3.wireOp",EDGE,"E1255"),sQuery(id+"F3.wireOp",EDGE,"E1256"),sQuery(id+"F3.wireOp",EDGE,"E1257"),sQuery(id+"F3.wireOp",EDGE,"E1258"),sQuery(id+"F3.wireOp",EDGE,"E1259"),sQuery(id+"F3.wireOp",EDGE,"E1260"),sQuery(id+"F3.wireOp",EDGE,"E1261"),sQuery(id+"F3.wireOp",EDGE,"E1262"),sQuery(id+"F3.wireOp",EDGE,"E1263"),sQuery(id+"F3.wireOp",EDGE,"E1264"),sQuery(id+"F3.wireOp",EDGE,"E1265"),sQuery(id+"F3.wireOp",EDGE,"E1266"),sQuery(id+"F3.wireOp",EDGE,"E1267"),sQuery(id+"F3.wireOp",EDGE,"E1268"),sQuery(id+"F3.wireOp",EDGE,"E1269"),sQuery(id+"F3.wireOp",EDGE,"E1270"),sQuery(id+"F3.wireOp",EDGE,"E1271"),sQuery(id+"F3.wireOp",EDGE,"E1272"),sQuery(id+"F3.wireOp",EDGE,"E1273"),sQuery(id+"F3.wireOp",EDGE,"E1274"),sQuery(id+"F3.wireOp",EDGE,"E1275"),sQuery(id+"F3.wireOp",EDGE,"E1276"),sQuery(id+"F3.wireOp",EDGE,"E1277"),sQuery(id+"F3.wireOp",EDGE,"E1278"),sQuery(id+"F3.wireOp",EDGE,"E1279"),sQuery(id+"F3.wireOp",EDGE,"E1280"),sQuery(id+"F3.wireOp",EDGE,"E1281"),sQuery(id+"F3.wireOp",EDGE,"E1282"),sQuery(id+"F3.wireOp",EDGE,"E1283"),sQuery(id+"F3.wireOp",EDGE,"E1284"),sQuery(id+"F3.wireOp",EDGE,"E1285"),sQuery(id+"F3.wireOp",EDGE,"E1286"),sQuery(id+"F3.wireOp",EDGE,"E1287"),sQuery(id+"F3.wireOp",EDGE,"E1288"),sQuery(id+"F3.wireOp",EDGE,"E1289"),sQuery(id+"F3.wireOp",EDGE,"E1290"),sQuery(id+"F3.wireOp",EDGE,"E1291"),sQuery(id+"F3.wireOp",EDGE,"E1292"),sQuery(id+"F3.wireOp",EDGE,"E1293"),sQuery(id+"F3.wireOp",EDGE,"E1294"),sQuery(id+"F3.wireOp",EDGE,"E1295"),sQuery(id+"F3.wireOp",EDGE,"E1296"),sQuery(id+"F3.wireOp",EDGE,"E1297"),sQuery(id+"F3.wireOp",EDGE,"E1298"),sQuery(id+"F3.wireOp",EDGE,"E1299"),sQuery(id+"F3.wireOp",EDGE,"E1300"),sQuery(id+"F3.wireOp",EDGE,"E1301"),sQuery(id+"F3.wireOp",EDGE,"E1302"),sQuery(id+"F3.wireOp",EDGE,"E1303"),sQuery(id+"F3.wireOp",EDGE,"E1304"),sQuery(id+"F3.wireOp",EDGE,"E1305"),sQuery(id+"F3.wireOp",EDGE,"E1306"),sQuery(id+"F3.wireOp",EDGE,"E1307"),sQuery(id+"F3.wireOp",EDGE,"E1308"),sQuery(id+"F3.wireOp",EDGE,"E1309"),sQuery(id+"F3.wireOp",EDGE,"E1310"),sQuery(id+"F3.wireOp",EDGE,"E1311"),sQuery(id+"F3.wireOp",EDGE,"E1312"),sQuery(id+"F3.wireOp",EDGE,"E1313"),sQuery(id+"F3.wireOp",EDGE,"E1314"),sQuery(id+"F3.wireOp",EDGE,"E1315"),sQuery(id+"F3.wireOp",EDGE,"E1316"),sQuery(id+"F3.wireOp",EDGE,"E1317"),sQuery(id+"F3.wireOp",EDGE,"E1318"),sQuery(id+"F3.wireOp",EDGE,"E1319"),sQuery(id+"F3.wireOp",EDGE,"E1320"),sQuery(id+"F3.wireOp",EDGE,"E1321"),sQuery(id+"F3.wireOp",EDGE,"E1322"),sQuery(id+"F3.wireOp",EDGE,"E1323"),sQuery(id+"F3.wireOp",EDGE,"E1324"),sQuery(id+"F3.wireOp",EDGE,"E1325"),sQuery(id+"F3.wireOp",EDGE,"E1326"),sQuery(id+"F3.wireOp",EDGE,"E1327"),sQuery(id+"F3.wireOp",EDGE,"E1328"),sQuery(id+"F3.wireOp",EDGE,"E1329"),sQuery(id+"F3.wireOp",EDGE,"E1330"),sQuery(id+"F3.wireOp",EDGE,"E1331"),sQuery(id+"F3.wireOp",EDGE,"E1332"),sQuery(id+"F3.wireOp",EDGE,"E1333"),sQuery(id+"F3.wireOp",EDGE,"E1334"),sQuery(id+"F3.wireOp",EDGE,"E1335"),sQuery(id+"F3.wireOp",EDGE,"E1336"),sQuery(id+"F3.wireOp",EDGE,"E1337"),sQuery(id+"F3.wireOp",EDGE,"E1338"),sQuery(id+"F3.wireOp",EDGE,"E1339"),sQuery(id+"F3.wireOp",EDGE,"E1340"),sQuery(id+"F3.wireOp",EDGE,"E1341"),sQuery(id+"F3.wireOp",EDGE,"E1342"),sQuery(id+"F3.wireOp",EDGE,"E1343"),sQuery(id+"F3.wireOp",EDGE,"E1344"),sQuery(id+"F3.wireOp",EDGE,"E1345"),sQuery(id+"F3.wireOp",EDGE,"E1346"),sQuery(id+"F3.wireOp",EDGE,"E1347"),sQuery(id+"F3.wireOp",EDGE,"E1348"),sQuery(id+"F3.wireOp",EDGE,"E1349"),sQuery(id+"F3.wireOp",EDGE,"E1350"),sQuery(id+"F3.wireOp",EDGE,"E1351"),sQuery(id+"F3.wireOp",EDGE,"E1352"),sQuery(id+"F3.wireOp",EDGE,"E1353"),sQuery(id+"F3.wireOp",EDGE,"E1354"),sQuery(id+"F3.wireOp",EDGE,"E1355"),sQuery(id+"F3.wireOp",EDGE,"E1356"),sQuery(id+"F3.wireOp",EDGE,"E1357"),sQuery(id+"F3.wireOp",EDGE,"E1358"),sQuery(id+"F3.wireOp",EDGE,"E1359"),sQuery(id+"F3.wireOp",EDGE,"E1360"),sQuery(id+"F3.wireOp",EDGE,"E1361"),sQuery(id+"F3.wireOp",EDGE,"E1362"),sQuery(id+"F3.wireOp",EDGE,"E1363"),sQuery(id+"F3.wireOp",EDGE,"E1364"),sQuery(id+"F3.wireOp",EDGE,"E1365"),sQuery(id+"F3.wireOp",EDGE,"E1366"),sQuery(id+"F3.wireOp",EDGE,"E1367"),sQuery(id+"F3.wireOp",EDGE,"E1368"),sQuery(id+"F3.wireOp",EDGE,"E1369"),sQuery(id+"F3.wireOp",EDGE,"E1370"),sQuery(id+"F3.wireOp",EDGE,"E1371"),sQuery(id+"F3.wireOp",EDGE,"E1372"),sQuery(id+"F3.wireOp",EDGE,"E1373"),sQuery(id+"F3.wireOp",EDGE,"E1374"),sQuery(id+"F3.wireOp",EDGE,"E1375"),sQuery(id+"F3.wireOp",EDGE,"E1376"),sQuery(id+"F3.wireOp",EDGE,"E1377"),sQuery(id+"F3.wireOp",EDGE,"E1378"),sQuery(id+"F3.wireOp",EDGE,"E1379"),sQuery(id+"F3.wireOp",EDGE,"E1380"),sQuery(id+"F3.wireOp",EDGE,"E1381"),sQuery(id+"F3.wireOp",EDGE,"E1382"),sQuery(id+"F3.wireOp",EDGE,"E1383"),sQuery(id+"F3.wireOp",EDGE,"E1384"),sQuery(id+"F3.wireOp",EDGE,"E1385"),sQuery(id+"F3.wireOp",EDGE,"E1386"),sQuery(id+"F3.wireOp",EDGE,"E1387"),sQuery(id+"F3.wireOp",EDGE,"E1388"),sQuery(id+"F3.wireOp",EDGE,"E1389"),sQuery(id+"F3.wireOp",EDGE,"E1390"),sQuery(id+"F3.wireOp",EDGE,"E1391"),sQuery(id+"F3.wireOp",EDGE,"E1392"),sQuery(id+"F3.wireOp",EDGE,"E1393"),sQuery(id+"F3.wireOp",EDGE,"E1394"),sQuery(id+"F3.wireOp",EDGE,"E1395"),sQuery(id+"F3.wireOp",EDGE,"E1396"),sQuery(id+"F3.wireOp",EDGE,"E1397"),sQuery(id+"F3.wireOp",EDGE,"E1398"),sQuery(id+"F3.wireOp",EDGE,"E1399"),sQuery(id+"F3.wireOp",EDGE,"E1400"),sQuery(id+"F3.wireOp",EDGE,"E1401"),sQuery(id+"F3.wireOp",EDGE,"E1402"),sQuery(id+"F3.wireOp",EDGE,"E1403"),sQuery(id+"F3.wireOp",EDGE,"E1404"),sQuery(id+"F3.wireOp",EDGE,"E1405"),sQuery(id+"F3.wireOp",EDGE,"E1406"),sQuery(id+"F3.wireOp",EDGE,"E1407"),sQuery(id+"F3.wireOp",EDGE,"E1408"),sQuery(id+"F3.wireOp",EDGE,"E1409"),sQuery(id+"F3.wireOp",EDGE,"E1410"),sQuery(id+"F3.wireOp",EDGE,"E1411"),sQuery(id+"F3.wireOp",EDGE,"E1412"),sQuery(id+"F3.wireOp",EDGE,"E1413"),sQuery(id+"F3.wireOp",EDGE,"E1414"),sQuery(id+"F3.wireOp",EDGE,"E1415"),sQuery(id+"F3.wireOp",EDGE,"E1416"),sQuery(id+"F3.wireOp",EDGE,"E1417"),sQuery(id+"F3.wireOp",EDGE,"E1418"),sQuery(id+"F3.wireOp",EDGE,"E1419"),sQuery(id+"F3.wireOp",EDGE,"E1420"),sQuery(id+"F3.wireOp",EDGE,"E1421"),sQuery(id+"F3.wireOp",EDGE,"E1422"),sQuery(id+"F3.wireOp",EDGE,"E1423"),sQuery(id+"F3.wireOp",EDGE,"E1424"),sQuery(id+"F3.wireOp",EDGE,"E1425"),sQuery(id+"F3.wireOp",EDGE,"E1426"),sQuery(id+"F3.wireOp",EDGE,"E1427"),sQuery(id+"F3.wireOp",EDGE,"E1428"),sQuery(id+"F3.wireOp",EDGE,"E1429"),sQuery(id+"F3.wireOp",EDGE,"E1430"),sQuery(id+"F3.wireOp",EDGE,"E1431"),sQuery(id+"F3.wireOp",EDGE,"E1432"),sQuery(id+"F3.wireOp",EDGE,"E1433"),sQuery(id+"F3.wireOp",EDGE,"E1434"),sQuery(id+"F3.wireOp",EDGE,"E1435"),sQuery(id+"F3.wireOp",EDGE,"E1436"),sQuery(id+"F3.wireOp",EDGE,"E1437"),sQuery(id+"F3.wireOp",EDGE,"E1438"),sQuery(id+"F3.wireOp",EDGE,"E1439"),sQuery(id+"F3.wireOp",EDGE,"E1440"),sQuery(id+"F3.wireOp",EDGE,"E1441"),sQuery(id+"F3.wireOp",EDGE,"E1442"),sQuery(id+"F3.wireOp",EDGE,"E1443"),sQuery(id+"F3.wireOp",EDGE,"E1444"),sQuery(id+"F3.wireOp",EDGE,"E1445"),sQuery(id+"F3.wireOp",EDGE,"E1446"),sQuery(id+"F3.wireOp",EDGE,"E1447"),sQuery(id+"F3.wireOp",EDGE,"E1448"),sQuery(id+"F3.wireOp",EDGE,"E1449"),sQuery(id+"F3.wireOp",EDGE,"E1450"),sQuery(id+"F3.wireOp",EDGE,"E1451"),sQuery(id+"F3.wireOp",EDGE,"E1452"),sQuery(id+"F3.wireOp",EDGE,"E1453"),sQuery(id+"F3.wireOp",EDGE,"E1454"),sQuery(id+"F3.wireOp",EDGE,"E1455"),sQuery(id+"F3.wireOp",EDGE,"E1456"),sQuery(id+"F3.wireOp",EDGE,"E1457"),sQuery(id+"F3.wireOp",EDGE,"E1458"),sQuery(id+"F3.wireOp",EDGE,"E1459"),sQuery(id+"F3.wireOp",EDGE,"E1460"),sQuery(id+"F3.wireOp",EDGE,"E1461"),sQuery(id+"F3.wireOp",EDGE,"E1462"),sQuery(id+"F3.wireOp",EDGE,"E1463"),sQuery(id+"F3.wireOp",EDGE,"E1464"),sQuery(id+"F3.wireOp",EDGE,"E1465"),sQuery(id+"F3.wireOp",EDGE,"E1466"),sQuery(id+"F3.wireOp",EDGE,"E1467"),sQuery(id+"F3.wireOp",EDGE,"E1468"),sQuery(id+"F3.wireOp",EDGE,"E1469"),sQuery(id+"F3.wireOp",EDGE,"E1470"),sQuery(id+"F3.wireOp",EDGE,"E1471"),sQuery(id+"F3.wireOp",EDGE,"E1472"),sQuery(id+"F3.wireOp",EDGE,"E1473"),sQuery(id+"F3.wireOp",EDGE,"E1474"),sQuery(id+"F3.wireOp",EDGE,"E1475"),sQuery(id+"F3.wireOp",EDGE,"E1476"),sQuery(id+"F3.wireOp",EDGE,"E1477"),sQuery(id+"F3.wireOp",EDGE,"E1478"),sQuery(id+"F3.wireOp",EDGE,"E1479"),sQuery(id+"F3.wireOp",EDGE,"E1480"),sQuery(id+"F3.wireOp",EDGE,"E1481"),sQuery(id+"F3.wireOp",EDGE,"E1482"),sQuery(id+"F3.wireOp",EDGE,"E1483"),sQuery(id+"F3.wireOp",EDGE,"E1484"),sQuery(id+"F3.wireOp",EDGE,"E1485"),sQuery(id+"F3.wireOp",EDGE,"E1486"),sQuery(id+"F3.wireOp",EDGE,"E1487"),sQuery(id+"F3.wireOp",EDGE,"E1488"),sQuery(id+"F3.wireOp",EDGE,"E1489"),sQuery(id+"F3.wireOp",EDGE,"E1490"),sQuery(id+"F3.wireOp",EDGE,"E1491"),sQuery(id+"F3.wireOp",EDGE,"E1492"),sQuery(id+"F3.wireOp",EDGE,"E1493"),sQuery(id+"F3.wireOp",EDGE,"E1494"),sQuery(id+"F3.wireOp",EDGE,"E1495"),sQuery(id+"F3.wireOp",EDGE,"E1496"),sQuery(id+"F3.wireOp",EDGE,"E1497"),sQuery(id+"F3.wireOp",EDGE,"E1498"),sQuery(id+"F3.wireOp",EDGE,"E1499"),sQuery(id+"F3.wireOp",EDGE,"E1500"),sQuery(id+"F3.wireOp",EDGE,"E1501"),sQuery(id+"F3.wireOp",EDGE,"E1502"),sQuery(id+"F3.wireOp",EDGE,"E1503"),sQuery(id+"F3.wireOp",EDGE,"E1504"),sQuery(id+"F3.wireOp",EDGE,"E1505"),sQuery(id+"F3.wireOp",EDGE,"E1506"),sQuery(id+"F3.wireOp",EDGE,"E1507"),sQuery(id+"F3.wireOp",EDGE,"E1508"),sQuery(id+"F3.wireOp",EDGE,"E1509"),sQuery(id+"F3.wireOp",EDGE,"E1510"),sQuery(id+"F3.wireOp",EDGE,"E1511"),sQuery(id+"F3.wireOp",EDGE,"E1512"),sQuery(id+"F3.wireOp",EDGE,"E1513"),sQuery(id+"F3.wireOp",EDGE,"E1514"),sQuery(id+"F3.wireOp",EDGE,"E1515"),sQuery(id+"F3.wireOp",EDGE,"E1516"),sQuery(id+"F3.wireOp",EDGE,"E1517"),sQuery(id+"F3.wireOp",EDGE,"E1518"),sQuery(id+"F3.wireOp",EDGE,"E1519"),sQuery(id+"F3.wireOp",EDGE,"E1520"),sQuery(id+"F3.wireOp",EDGE,"E1521"),sQuery(id+"F3.wireOp",EDGE,"E1522"),sQuery(id+"F3.wireOp",EDGE,"E1523"),sQuery(id+"F3.wireOp",EDGE,"E1524"),sQuery(id+"F3.wireOp",EDGE,"E1525"),sQuery(id+"F3.wireOp",EDGE,"E1526"),sQuery(id+"F3.wireOp",EDGE,"E1527"),sQuery(id+"F3.wireOp",EDGE,"E1528"),sQuery(id+"F3.wireOp",EDGE,"E1529"),sQuery(id+"F3.wireOp",EDGE,"E1530"),sQuery(id+"F3.wireOp",EDGE,"E1531"),sQuery(id+"F3.wireOp",EDGE,"E1532"),sQuery(id+"F3.wireOp",EDGE,"E1533"),sQuery(id+"F3.wireOp",EDGE,"E1534"),sQuery(id+"F3.wireOp",EDGE,"E1535"),sQuery(id+"F3.wireOp",EDGE,"E1536"),sQuery(id+"F3.wireOp",EDGE,"E1537"),sQuery(id+"F3.wireOp",EDGE,"E1538"),sQuery(id+"F3.wireOp",EDGE,"E1539"),sQuery(id+"F3.wireOp",EDGE,"E1540"),sQuery(id+"F3.wireOp",EDGE,"E1541"),sQuery(id+"F3.wireOp",EDGE,"E1542"),sQuery(id+"F3.wireOp",EDGE,"E1543"),sQuery(id+"F3.wireOp",EDGE,"E1544"),sQuery(id+"F3.wireOp",EDGE,"E1545"),sQuery(id+"F3.wireOp",EDGE,"E1546"),sQuery(id+"F3.wireOp",EDGE,"E1547"),sQuery(id+"F3.wireOp",EDGE,"E1548"),sQuery(id+"F3.wireOp",EDGE,"E1549"),sQuery(id+"F3.wireOp",EDGE,"E1550"),sQuery(id+"F3.wireOp",EDGE,"E1551"),sQuery(id+"F3.wireOp",EDGE,"E1552"),sQuery(id+"F3.wireOp",EDGE,"E1553"),sQuery(id+"F3.wireOp",EDGE,"E1554"),sQuery(id+"F3.wireOp",EDGE,"E1555"),sQuery(id+"F3.wireOp",EDGE,"E1556"),sQuery(id+"F3.wireOp",EDGE,"E1557"),sQuery(id+"F3.wireOp",EDGE,"E1558"),sQuery(id+"F3.wireOp",EDGE,"E1559"),sQuery(id+"F3.wireOp",EDGE,"E1560"),sQuery(id+"F3.wireOp",EDGE,"E1561"),sQuery(id+"F3.wireOp",EDGE,"E1562"),sQuery(id+"F3.wireOp",EDGE,"E1563"),sQuery(id+"F3.wireOp",EDGE,"E1564"),sQuery(id+"F3.wireOp",EDGE,"E1565"),sQuery(id+"F3.wireOp",EDGE,"E1566"),sQuery(id+"F3.wireOp",EDGE,"E1567"),sQuery(id+"F3.wireOp",EDGE,"E1568"),sQuery(id+"F3.wireOp",EDGE,"E1569"),sQuery(id+"F3.wireOp",EDGE,"E1570"),sQuery(id+"F3.wireOp",EDGE,"E1571"),sQuery(id+"F3.wireOp",EDGE,"E1572"),sQuery(id+"F3.wireOp",EDGE,"E1573"),sQuery(id+"F3.wireOp",EDGE,"E1574"),sQuery(id+"F3.wireOp",EDGE,"E1575"),sQuery(id+"F3.wireOp",EDGE,"E1576"),sQuery(id+"F3.wireOp",EDGE,"E1577"),sQuery(id+"F3.wireOp",EDGE,"E1578"),sQuery(id+"F3.wireOp",EDGE,"E1579"),sQuery(id+"F3.wireOp",EDGE,"E1580"),sQuery(id+"F3.wireOp",EDGE,"E1581"),sQuery(id+"F3.wireOp",EDGE,"E1582"),sQuery(id+"F3.wireOp",EDGE,"E1583"),sQuery(id+"F3.wireOp",EDGE,"E1584"),sQuery(id+"F3.wireOp",EDGE,"E1585"),sQuery(id+"F3.wireOp",EDGE,"E1586"),sQuery(id+"F3.wireOp",EDGE,"E1587"),sQuery(id+"F3.wireOp",EDGE,"E1588"),sQuery(id+"F3.wireOp",EDGE,"E1589"),sQuery(id+"F3.wireOp",EDGE,"E1590"),sQuery(id+"F3.wireOp",EDGE,"E1591"),sQuery(id+"F3.wireOp",EDGE,"E1592"),sQuery(id+"F3.wireOp",EDGE,"E1593"),sQuery(id+"F3.wireOp",EDGE,"E1594"),sQuery(id+"F3.wireOp",EDGE,"E1595"),sQuery(id+"F3.wireOp",EDGE,"E1596"),sQuery(id+"F3.wireOp",EDGE,"E1597"),sQuery(id+"F3.wireOp",EDGE,"E1598"),sQuery(id+"F3.wireOp",EDGE,"E1599"),sQuery(id+"F3.wireOp",EDGE,"E1600"),sQuery(id+"F3.wireOp",EDGE,"E1601"),sQuery(id+"F3.wireOp",EDGE,"E1602"),sQuery(id+"F3.wireOp",EDGE,"E1603"),sQuery(id+"F3.wireOp",EDGE,"E1604"),sQuery(id+"F3.wireOp",EDGE,"E1605"),sQuery(id+"F3.wireOp",EDGE,"E1606"),sQuery(id+"F3.wireOp",EDGE,"E1607"),sQuery(id+"F3.wireOp",EDGE,"E1608"),sQuery(id+"F3.wireOp",EDGE,"E1609"),sQuery(id+"F3.wireOp",EDGE,"E1610"),sQuery(id+"F3.wireOp",EDGE,"E1611"),sQuery(id+"F3.wireOp",EDGE,"E1612"),sQuery(id+"F3.wireOp",EDGE,"E1613"),sQuery(id+"F3.wireOp",EDGE,"E1614"),sQuery(id+"F3.wireOp",EDGE,"E1615"),sQuery(id+"F3.wireOp",EDGE,"E1616"),sQuery(id+"F3.wireOp",EDGE,"E1617"),sQuery(id+"F3.wireOp",EDGE,"E1618"),sQuery(id+"F3.wireOp",EDGE,"E1619"),sQuery(id+"F3.wireOp",EDGE,"E1620"),sQuery(id+"F3.wireOp",EDGE,"E1621"),sQuery(id+"F3.wireOp",EDGE,"E1622"),sQuery(id+"F3.wireOp",EDGE,"E1623"),sQuery(id+"F3.wireOp",EDGE,"E1624"),sQuery(id+"F3.wireOp",EDGE,"E1625"),sQuery(id+"F3.wireOp",EDGE,"E1626"),sQuery(id+"F3.wireOp",EDGE,"E1627"),sQuery(id+"F3.wireOp",EDGE,"E1628"),sQuery(id+"F3.wireOp",EDGE,"E1629"),sQuery(id+"F3.wireOp",EDGE,"E1630"),sQuery(id+"F3.wireOp",EDGE,"E1631"),sQuery(id+"F3.wireOp",EDGE,"E1632"),sQuery(id+"F3.wireOp",EDGE,"E1633"),sQuery(id+"F3.wireOp",EDGE,"E1634"),sQuery(id+"F3.wireOp",EDGE,"E1635"),sQuery(id+"F3.wireOp",EDGE,"E1636"),sQuery(id+"F3.wireOp",EDGE,"E1637"),sQuery(id+"F3.wireOp",EDGE,"E1638"),sQuery(id+"F3.wireOp",EDGE,"E1639"),sQuery(id+"F3.wireOp",EDGE,"E1640"),sQuery(id+"F3.wireOp",EDGE,"E1641"),sQuery(id+"F3.wireOp",EDGE,"E1642"),sQuery(id+"F3.wireOp",EDGE,"E1643"),sQuery(id+"F3.wireOp",EDGE,"E1644"),sQuery(id+"F3.wireOp",EDGE,"E1645"),sQuery(id+"F3.wireOp",EDGE,"E1646"),sQuery(id+"F3.wireOp",EDGE,"E1647"),sQuery(id+"F3.wireOp",EDGE,"E1648"),sQuery(id+"F3.wireOp",EDGE,"E1649"),sQuery(id+"F3.wireOp",EDGE,"E1650"),sQuery(id+"F3.wireOp",EDGE,"E1651"),sQuery(id+"F3.wireOp",EDGE,"E1652"),sQuery(id+"F3.wireOp",EDGE,"E1653"),sQuery(id+"F3.wireOp",EDGE,"E1654"),sQuery(id+"F3.wireOp",EDGE,"E1655"),sQuery(id+"F3.wireOp",EDGE,"E1656"),sQuery(id+"F3.wireOp",EDGE,"E1657"),sQuery(id+"F3.wireOp",EDGE,"E1658"),sQuery(id+"F3.wireOp",EDGE,"E1659"),sQuery(id+"F3.wireOp",EDGE,"E1660"),sQuery(id+"F3.wireOp",EDGE,"E1661"),sQuery(id+"F3.wireOp",EDGE,"E1662"),sQuery(id+"F3.wireOp",EDGE,"E1663"),sQuery(id+"F3.wireOp",EDGE,"E1664"),sQuery(id+"F3.wireOp",EDGE,"E1665"),sQuery(id+"F3.wireOp",EDGE,"E1666"),sQuery(id+"F3.wireOp",EDGE,"E1667"),sQuery(id+"F3.wireOp",EDGE,"E1668"),sQuery(id+"F3.wireOp",EDGE,"E1669"),sQuery(id+"F3.wireOp",EDGE,"E1670"),sQuery(id+"F3.wireOp",EDGE,"E1671"),sQuery(id+"F3.wireOp",EDGE,"E1672"),sQuery(id+"F3.wireOp",EDGE,"E1673"),sQuery(id+"F3.wireOp",EDGE,"E1674"),sQuery(id+"F3.wireOp",EDGE,"E1675"),sQuery(id+"F3.wireOp",EDGE,"E1676"),sQuery(id+"F3.wireOp",EDGE,"E1677"),sQuery(id+"F3.wireOp",EDGE,"E1678"),sQuery(id+"F3.wireOp",EDGE,"E1679"),sQuery(id+"F3.wireOp",EDGE,"E1680"),sQuery(id+"F3.wireOp",EDGE,"E1681"),sQuery(id+"F3.wireOp",EDGE,"E1682"),sQuery(id+"F3.wireOp",EDGE,"E1683"),sQuery(id+"F3.wireOp",EDGE,"E1684"),sQuery(id+"F3.wireOp",EDGE,"E1685"),sQuery(id+"F3.wireOp",EDGE,"E1686"),sQuery(id+"F3.wireOp",EDGE,"E1687"),sQuery(id+"F3.wireOp",EDGE,"E1688"),sQuery(id+"F3.wireOp",EDGE,"E1689"),sQuery(id+"F3.wireOp",EDGE,"E1690"),sQuery(id+"F3.wireOp",EDGE,"E1691"),sQuery(id+"F3.wireOp",EDGE,"E1692"),sQuery(id+"F3.wireOp",EDGE,"E1693"),sQuery(id+"F3.wireOp",EDGE,"E1694"),sQuery(id+"F3.wireOp",EDGE,"E1695"),sQuery(id+"F3.wireOp",EDGE,"E1696"),sQuery(id+"F3.wireOp",EDGE,"E1697"),sQuery(id+"F3.wireOp",EDGE,"E1698"),sQuery(id+"F3.wireOp",EDGE,"E1699"),sQuery(id+"F3.wireOp",EDGE,"E1700"),sQuery(id+"F3.wireOp",EDGE,"E1701"),sQuery(id+"F3.wireOp",EDGE,"E1702"),sQuery(id+"F3.wireOp",EDGE,"E1703"),sQuery(id+"F3.wireOp",EDGE,"E1704"),sQuery(id+"F3.wireOp",EDGE,"E1705"),sQuery(id+"F3.wireOp",EDGE,"E1706"),sQuery(id+"F3.wireOp",EDGE,"E1707"),sQuery(id+"F3.wireOp",EDGE,"E1708"),sQuery(id+"F3.wireOp",EDGE,"E1709"),sQuery(id+"F3.wireOp",EDGE,"E1710"),sQuery(id+"F3.wireOp",EDGE,"E1711"),sQuery(id+"F3.wireOp",EDGE,"E1712"),sQuery(id+"F3.wireOp",EDGE,"E1713"),sQuery(id+"F3.wireOp",EDGE,"E1714"),sQuery(id+"F3.wireOp",EDGE,"E1715"),sQuery(id+"F3.wireOp",EDGE,"E1716"),sQuery(id+"F3.wireOp",EDGE,"E1717"),sQuery(id+"F3.wireOp",EDGE,"E1718"),sQuery(id+"F3.wireOp",EDGE,"E1719"),sQuery(id+"F3.wireOp",EDGE,"E1720"),sQuery(id+"F3.wireOp",EDGE,"E1721"),sQuery(id+"F3.wireOp",EDGE,"E1722"),sQuery(id+"F3.wireOp",EDGE,"E1723"),sQuery(id+"F3.wireOp",EDGE,"E1724"),sQuery(id+"F3.wireOp",EDGE,"E1725"),sQuery(id+"F3.wireOp",EDGE,"E1726"),sQuery(id+"F3.wireOp",EDGE,"E1727"),sQuery(id+"F3.wireOp",EDGE,"E1728"),sQuery(id+"F3.wireOp",EDGE,"E1729"),sQuery(id+"F3.wireOp",EDGE,"E1730"),sQuery(id+"F3.wireOp",EDGE,"E1731"),sQuery(id+"F3.wireOp",EDGE,"E1732"),sQuery(id+"F3.wireOp",EDGE,"E1733"),sQuery(id+"F3.wireOp",EDGE,"E1734"),sQuery(id+"F3.wireOp",EDGE,"E1735"),sQuery(id+"F3.wireOp",EDGE,"E1736"),sQuery(id+"F3.wireOp",EDGE,"E1737"),sQuery(id+"F3.wireOp",EDGE,"E1738"),sQuery(id+"F3.wireOp",EDGE,"E1739"),sQuery(id+"F3.wireOp",EDGE,"E1740"),sQuery(id+"F3.wireOp",EDGE,"E1741"),sQuery(id+"F3.wireOp",EDGE,"E1742"),sQuery(id+"F3.wireOp",EDGE,"E1743"),sQuery(id+"F3.wireOp",EDGE,"E1744"),sQuery(id+"F3.wireOp",EDGE,"E1745"),sQuery(id+"F3.wireOp",EDGE,"E1746"),sQuery(id+"F3.wireOp",EDGE,"E1747"),sQuery(id+"F3.wireOp",EDGE,"E1748"),sQuery(id+"F3.wireOp",EDGE,"E1749"),sQuery(id+"F3.wireOp",EDGE,"E1750"),sQuery(id+"F3.wireOp",EDGE,"E1751"),sQuery(id+"F3.wireOp",EDGE,"E1752"),sQuery(id+"F3.wireOp",EDGE,"E1753"),sQuery(id+"F3.wireOp",EDGE,"E1754"),sQuery(id+"F3.wireOp",EDGE,"E1755"),sQuery(id+"F3.wireOp",EDGE,"E1756"),sQuery(id+"F3.wireOp",EDGE,"E1757"),sQuery(id+"F3.wireOp",EDGE,"E1758"),sQuery(id+"F3.wireOp",EDGE,"E1759"),sQuery(id+"F3.wireOp",EDGE,"E1760"),sQuery(id+"F3.wireOp",EDGE,"E1761"),sQuery(id+"F3.wireOp",EDGE,"E1762"),sQuery(id+"F3.wireOp",EDGE,"E1763"),sQuery(id+"F3.wireOp",EDGE,"E1764"),sQuery(id+"F3.wireOp",EDGE,"E1765"),sQuery(id+"F3.wireOp",EDGE,"E1766"),sQuery(id+"F3.wireOp",EDGE,"E1767"),sQuery(id+"F3.wireOp",EDGE,"E1768"),sQuery(id+"F3.wireOp",EDGE,"E1769"),sQuery(id+"F3.wireOp",EDGE,"E1770"),sQuery(id+"F3.wireOp",EDGE,"E1771"),sQuery(id+"F3.wireOp",EDGE,"E1772"),sQuery(id+"F3.wireOp",EDGE,"E1773"),sQuery(id+"F3.wireOp",EDGE,"E1774"),sQuery(id+"F3.wireOp",EDGE,"E1775"),sQuery(id+"F3.wireOp",EDGE,"E1776"),sQuery(id+"F3.wireOp",EDGE,"E1777"),sQuery(id+"F3.wireOp",EDGE,"E1778"),sQuery(id+"F3.wireOp",EDGE,"E1779"),sQuery(id+"F3.wireOp",EDGE,"E1780"),sQuery(id+"F3.wireOp",EDGE,"E1781"),sQuery(id+"F3.wireOp",EDGE,"E1782"),sQuery(id+"F3.wireOp",EDGE,"E1783"),sQuery(id+"F3.wireOp",EDGE,"E1784"),sQuery(id+"F3.wireOp",EDGE,"E1785"),sQuery(id+"F3.wireOp",EDGE,"E1786"),sQuery(id+"F3.wireOp",EDGE,"E1787"),sQuery(id+"F3.wireOp",EDGE,"E1788"),sQuery(id+"F3.wireOp",EDGE,"E1789"),sQuery(id+"F3.wireOp",EDGE,"E1790"),sQuery(id+"F3.wireOp",EDGE,"E1791"),sQuery(id+"F3.wireOp",EDGE,"E1792"),sQuery(id+"F3.wireOp",EDGE,"E1793"),sQuery(id+"F3.wireOp",EDGE,"E1794"),sQuery(id+"F3.wireOp",EDGE,"E1795"),sQuery(id+"F3.wireOp",EDGE,"E1796"),sQuery(id+"F3.wireOp",EDGE,"E1797"),sQuery(id+"F3.wireOp",EDGE,"E1798"),sQuery(id+"F3.wireOp",EDGE,"E1799"),sQuery(id+"F3.wireOp",EDGE,"E1800"),sQuery(id+"F3.wireOp",EDGE,"E1801"),sQuery(id+"F3.wireOp",EDGE,"E1802"),sQuery(id+"F3.wireOp",EDGE,"E1803"),sQuery(id+"F3.wireOp",EDGE,"E1824.0.0"),sQuery(id+"F3.wireOp",EDGE,"E1824.0.1"),sQuery(id+"F3.wireOp",EDGE,"E1824.0.2"),sQuery(id+"F3.wireOp",EDGE,"E1824.0.3"),sQuery(id+"F3.wireOp",EDGE,"E1824.0.4"),sQuery(id+"F3.wireOp",EDGE,"E1824.0.5"),sQuery(id+"F3.wireOp",EDGE,"E1824.0.6"),sQuery(id+"F3.wireOp",EDGE,"E1824.0.7"),sQuery(id+"F3.wireOp",EDGE,"E1824.0.8"),sQuery(id+"F3.wireOp",EDGE,"E1824.0.9"),sQuery(id+"F3.wireOp",EDGE,"E1824.0.10"),sQuery(id+"F3.wireOp",EDGE,"E1824.0.11"),sQuery(id+"F3.wireOp",EDGE,"E1824.0.12"),sQuery(id+"F3.wireOp",EDGE,"E1824.0.13"),sQuery(id+"F3.wireOp",EDGE,"E1824.0.14"),sQuery(id+"F3.wireOp",EDGE,"E1824.0.15"),sQuery(id+"F3.wireOp",EDGE,"E1824.0.16"),sQuery(id+"F3.wireOp",EDGE,"E1824.0.17"),sQuery(id+"F3.wireOp",EDGE,"E1824.0.18"),sQuery(id+"F3.wireOp",EDGE,"E1824.0.19"),sQuery(id+"F3.wireOp",EDGE,"E1824.0.20"),sQuery(id+"F3.wireOp",EDGE,"E1824.0.21"),sQuery(id+"F3.wireOp",EDGE,"E1824.0.22"),sQuery(id+"F3.wireOp",EDGE,"E1824.0.23"),sQuery(id+"F3.wireOp",EDGE,"E1824.0.24"),sQuery(id+"F3.wireOp",EDGE,"E1824.0.25"),sQuery(id+"F3.wireOp",EDGE,"E1824.0.26"),sQuery(id+"F3.wireOp",EDGE,"E1824.0.27"),sQuery(id+"F3.wireOp",EDGE,"E1824.0.28"),sQuery(id+"F3.wireOp",EDGE,"E1824.0.29"),sQuery(id+"F3.wireOp",EDGE,"E1824.0.30"),sQuery(id+"F3.wireOp",EDGE,"E1824.0.31"),sQuery(id+"F3.wireOp",EDGE,"E1824.0.32"),sQuery(id+"F3.wireOp",EDGE,"E1824.0.33"),sQuery(id+"F3.wireOp",EDGE,"E1824.0.34"),sQuery(id+"F3.wireOp",EDGE,"E1824.0.35"),sQuery(id+"F3.wireOp",EDGE,"E1824.0.36"),sQuery(id+"F3.wireOp",EDGE,"E1824.0.37"),sQuery(id+"F3.wireOp",EDGE,"E1824.0.38"),sQuery(id+"F3.wireOp",EDGE,"E1824.0.39"),sQuery(id+"F3.wireOp",EDGE,"E1824.0.40"),sQuery(id+"F3.wireOp",EDGE,"E1824.0.41"),sQuery(id+"F3.wireOp",EDGE,"E1824.0.42"),sQuery(id+"F3.wireOp",EDGE,"E1824.0.43"),sQuery(id+"F3.wireOp",EDGE,"E1824.0.44"),sQuery(id+"F3.wireOp",EDGE,"E1824.0.45"),sQuery(id+"F3.wireOp",EDGE,"E1824.0.46"),sQuery(id+"F3.wireOp",EDGE,"E1824.0.47"),sQuery(id+"F3.wireOp",EDGE,"E1824.0.48"),sQuery(id+"F3.wireOp",EDGE,"E1824.0.49"),sQuery(id+"F3.wireOp",EDGE,"E1824.0.50"),sQuery(id+"F3.wireOp",EDGE,"E1824.0.51"),sQuery(id+"F3.wireOp",EDGE,"E1824.0.52"),sQuery(id+"F3.wireOp",EDGE,"E1824.0.53"),sQuery(id+"F3.wireOp",EDGE,"E1824.0.54"),sQuery(id+"F3.wireOp",EDGE,"E1824.0.55")])],"isStart":false});
            var sketch = newSketch(context, id + "F5", { "sketchPlane" : qUnion([Q0])});
            skCircle(sketch, "E1825", {"center": v(0, 0) * mm, "radius": 35.15 * mm});
            skCircle(sketch, "E1826", {"center": v(0, 0) * mm, "radius": 28.15 * mm});
            skSolve(sketch);
        }
        {
            var Q0;
            Q0=qSketchRegion(id+"F5",true);
            extrude(context, id + "F6", {"entities" : qUnion([Q0]), "operationType" : NewBodyOperationType.ADD, "oppositeDirection" : true, "depth" : (getVariable(context, 'idlerThick')) * mm, "offsetDistance" : 25 * mm});
        }
        {
            var Q0;
            Q0=makeQuery(id+"F4.opExtrude","CAP_FACE",FACE,{"disambiguationData":[OSD([sQuery(id+"F3.wireOp",EDGE,"E0"),sQuery(id+"F3.wireOp",EDGE,"E1"),sQuery(id+"F3.wireOp",EDGE,"E2"),sQuery(id+"F3.wireOp",EDGE,"E3"),sQuery(id+"F3.wireOp",EDGE,"E4"),sQuery(id+"F3.wireOp",EDGE,"E5"),sQuery(id+"F3.wireOp",EDGE,"E6"),sQuery(id+"F3.wireOp",EDGE,"E7"),sQuery(id+"F3.wireOp",EDGE,"E8"),sQuery(id+"F3.wireOp",EDGE,"E9"),sQuery(id+"F3.wireOp",EDGE,"E10"),sQuery(id+"F3.wireOp",EDGE,"E11"),sQuery(id+"F3.wireOp",EDGE,"E12"),sQuery(id+"F3.wireOp",EDGE,"E13"),sQuery(id+"F3.wireOp",EDGE,"E14"),sQuery(id+"F3.wireOp",EDGE,"E15"),sQuery(id+"F3.wireOp",EDGE,"E16"),sQuery(id+"F3.wireOp",EDGE,"E17"),sQuery(id+"F3.wireOp",EDGE,"E18"),sQuery(id+"F3.wireOp",EDGE,"E19"),sQuery(id+"F3.wireOp",EDGE,"E20"),sQuery(id+"F3.wireOp",EDGE,"E21"),sQuery(id+"F3.wireOp",EDGE,"E22"),sQuery(id+"F3.wireOp",EDGE,"E23"),sQuery(id+"F3.wireOp",EDGE,"E24"),sQuery(id+"F3.wireOp",EDGE,"E25"),sQuery(id+"F3.wireOp",EDGE,"E26"),sQuery(id+"F3.wireOp",EDGE,"E27"),sQuery(id+"F3.wireOp",EDGE,"E28"),sQuery(id+"F3.wireOp",EDGE,"E29"),sQuery(id+"F3.wireOp",EDGE,"E30"),sQuery(id+"F3.wireOp",EDGE,"E31"),sQuery(id+"F3.wireOp",EDGE,"E32"),sQuery(id+"F3.wireOp",EDGE,"E33"),sQuery(id+"F3.wireOp",EDGE,"E34"),sQuery(id+"F3.wireOp",EDGE,"E35"),sQuery(id+"F3.wireOp",EDGE,"E36"),sQuery(id+"F3.wireOp",EDGE,"E37"),sQuery(id+"F3.wireOp",EDGE,"E38"),sQuery(id+"F3.wireOp",EDGE,"E39"),sQuery(id+"F3.wireOp",EDGE,"E40"),sQuery(id+"F3.wireOp",EDGE,"E41"),sQuery(id+"F3.wireOp",EDGE,"E42"),sQuery(id+"F3.wireOp",EDGE,"E43"),sQuery(id+"F3.wireOp",EDGE,"E44"),sQuery(id+"F3.wireOp",EDGE,"E45"),sQuery(id+"F3.wireOp",EDGE,"E46"),sQuery(id+"F3.wireOp",EDGE,"E47"),sQuery(id+"F3.wireOp",EDGE,"E48"),sQuery(id+"F3.wireOp",EDGE,"E49"),sQuery(id+"F3.wireOp",EDGE,"E50"),sQuery(id+"F3.wireOp",EDGE,"E51"),sQuery(id+"F3.wireOp",EDGE,"E52"),sQuery(id+"F3.wireOp",EDGE,"E53"),sQuery(id+"F3.wireOp",EDGE,"E54"),sQuery(id+"F3.wireOp",EDGE,"E55"),sQuery(id+"F3.wireOp",EDGE,"E56"),sQuery(id+"F3.wireOp",EDGE,"E57"),sQuery(id+"F3.wireOp",EDGE,"E58"),sQuery(id+"F3.wireOp",EDGE,"E59"),sQuery(id+"F3.wireOp",EDGE,"E60"),sQuery(id+"F3.wireOp",EDGE,"E61"),sQuery(id+"F3.wireOp",EDGE,"E62"),sQuery(id+"F3.wireOp",EDGE,"E63"),sQuery(id+"F3.wireOp",EDGE,"E64"),sQuery(id+"F3.wireOp",EDGE,"E65"),sQuery(id+"F3.wireOp",EDGE,"E66"),sQuery(id+"F3.wireOp",EDGE,"E67"),sQuery(id+"F3.wireOp",EDGE,"E68"),sQuery(id+"F3.wireOp",EDGE,"E69"),sQuery(id+"F3.wireOp",EDGE,"E70"),sQuery(id+"F3.wireOp",EDGE,"E71"),sQuery(id+"F3.wireOp",EDGE,"E72"),sQuery(id+"F3.wireOp",EDGE,"E73"),sQuery(id+"F3.wireOp",EDGE,"E74"),sQuery(id+"F3.wireOp",EDGE,"E75"),sQuery(id+"F3.wireOp",EDGE,"E76"),sQuery(id+"F3.wireOp",EDGE,"E77"),sQuery(id+"F3.wireOp",EDGE,"E78"),sQuery(id+"F3.wireOp",EDGE,"E79"),sQuery(id+"F3.wireOp",EDGE,"E80"),sQuery(id+"F3.wireOp",EDGE,"E81"),sQuery(id+"F3.wireOp",EDGE,"E82"),sQuery(id+"F3.wireOp",EDGE,"E83"),sQuery(id+"F3.wireOp",EDGE,"E84"),sQuery(id+"F3.wireOp",EDGE,"E85"),sQuery(id+"F3.wireOp",EDGE,"E86"),sQuery(id+"F3.wireOp",EDGE,"E87"),sQuery(id+"F3.wireOp",EDGE,"E88"),sQuery(id+"F3.wireOp",EDGE,"E89"),sQuery(id+"F3.wireOp",EDGE,"E90"),sQuery(id+"F3.wireOp",EDGE,"E91"),sQuery(id+"F3.wireOp",EDGE,"E92"),sQuery(id+"F3.wireOp",EDGE,"E93"),sQuery(id+"F3.wireOp",EDGE,"E94"),sQuery(id+"F3.wireOp",EDGE,"E95"),sQuery(id+"F3.wireOp",EDGE,"E96"),sQuery(id+"F3.wireOp",EDGE,"E97"),sQuery(id+"F3.wireOp",EDGE,"E98"),sQuery(id+"F3.wireOp",EDGE,"E99"),sQuery(id+"F3.wireOp",EDGE,"E100"),sQuery(id+"F3.wireOp",EDGE,"E101"),sQuery(id+"F3.wireOp",EDGE,"E102"),sQuery(id+"F3.wireOp",EDGE,"E103"),sQuery(id+"F3.wireOp",EDGE,"E104"),sQuery(id+"F3.wireOp",EDGE,"E105"),sQuery(id+"F3.wireOp",EDGE,"E106"),sQuery(id+"F3.wireOp",EDGE,"E107"),sQuery(id+"F3.wireOp",EDGE,"E108"),sQuery(id+"F3.wireOp",EDGE,"E109"),sQuery(id+"F3.wireOp",EDGE,"E110"),sQuery(id+"F3.wireOp",EDGE,"E111"),sQuery(id+"F3.wireOp",EDGE,"E112"),sQuery(id+"F3.wireOp",EDGE,"E113"),sQuery(id+"F3.wireOp",EDGE,"E114"),sQuery(id+"F3.wireOp",EDGE,"E115"),sQuery(id+"F3.wireOp",EDGE,"E116"),sQuery(id+"F3.wireOp",EDGE,"E117"),sQuery(id+"F3.wireOp",EDGE,"E118"),sQuery(id+"F3.wireOp",EDGE,"E119"),sQuery(id+"F3.wireOp",EDGE,"E120"),sQuery(id+"F3.wireOp",EDGE,"E121"),sQuery(id+"F3.wireOp",EDGE,"E122"),sQuery(id+"F3.wireOp",EDGE,"E123"),sQuery(id+"F3.wireOp",EDGE,"E124"),sQuery(id+"F3.wireOp",EDGE,"E125"),sQuery(id+"F3.wireOp",EDGE,"E126"),sQuery(id+"F3.wireOp",EDGE,"E127"),sQuery(id+"F3.wireOp",EDGE,"E128"),sQuery(id+"F3.wireOp",EDGE,"E129"),sQuery(id+"F3.wireOp",EDGE,"E130"),sQuery(id+"F3.wireOp",EDGE,"E131"),sQuery(id+"F3.wireOp",EDGE,"E132"),sQuery(id+"F3.wireOp",EDGE,"E133"),sQuery(id+"F3.wireOp",EDGE,"E134"),sQuery(id+"F3.wireOp",EDGE,"E135"),sQuery(id+"F3.wireOp",EDGE,"E136"),sQuery(id+"F3.wireOp",EDGE,"E137"),sQuery(id+"F3.wireOp",EDGE,"E138"),sQuery(id+"F3.wireOp",EDGE,"E139"),sQuery(id+"F3.wireOp",EDGE,"E140"),sQuery(id+"F3.wireOp",EDGE,"E141"),sQuery(id+"F3.wireOp",EDGE,"E142"),sQuery(id+"F3.wireOp",EDGE,"E143"),sQuery(id+"F3.wireOp",EDGE,"E144"),sQuery(id+"F3.wireOp",EDGE,"E145"),sQuery(id+"F3.wireOp",EDGE,"E146"),sQuery(id+"F3.wireOp",EDGE,"E147"),sQuery(id+"F3.wireOp",EDGE,"E148"),sQuery(id+"F3.wireOp",EDGE,"E149"),sQuery(id+"F3.wireOp",EDGE,"E150"),sQuery(id+"F3.wireOp",EDGE,"E151"),sQuery(id+"F3.wireOp",EDGE,"E152"),sQuery(id+"F3.wireOp",EDGE,"E153"),sQuery(id+"F3.wireOp",EDGE,"E154"),sQuery(id+"F3.wireOp",EDGE,"E155"),sQuery(id+"F3.wireOp",EDGE,"E156"),sQuery(id+"F3.wireOp",EDGE,"E157"),sQuery(id+"F3.wireOp",EDGE,"E158"),sQuery(id+"F3.wireOp",EDGE,"E159"),sQuery(id+"F3.wireOp",EDGE,"E160"),sQuery(id+"F3.wireOp",EDGE,"E161"),sQuery(id+"F3.wireOp",EDGE,"E162"),sQuery(id+"F3.wireOp",EDGE,"E163"),sQuery(id+"F3.wireOp",EDGE,"E164"),sQuery(id+"F3.wireOp",EDGE,"E165"),sQuery(id+"F3.wireOp",EDGE,"E166"),sQuery(id+"F3.wireOp",EDGE,"E167"),sQuery(id+"F3.wireOp",EDGE,"E168"),sQuery(id+"F3.wireOp",EDGE,"E169"),sQuery(id+"F3.wireOp",EDGE,"E170"),sQuery(id+"F3.wireOp",EDGE,"E171"),sQuery(id+"F3.wireOp",EDGE,"E172"),sQuery(id+"F3.wireOp",EDGE,"E173"),sQuery(id+"F3.wireOp",EDGE,"E174"),sQuery(id+"F3.wireOp",EDGE,"E175"),sQuery(id+"F3.wireOp",EDGE,"E176"),sQuery(id+"F3.wireOp",EDGE,"E177"),sQuery(id+"F3.wireOp",EDGE,"E178"),sQuery(id+"F3.wireOp",EDGE,"E179"),sQuery(id+"F3.wireOp",EDGE,"E180"),sQuery(id+"F3.wireOp",EDGE,"E181"),sQuery(id+"F3.wireOp",EDGE,"E182"),sQuery(id+"F3.wireOp",EDGE,"E183"),sQuery(id+"F3.wireOp",EDGE,"E184"),sQuery(id+"F3.wireOp",EDGE,"E185"),sQuery(id+"F3.wireOp",EDGE,"E186"),sQuery(id+"F3.wireOp",EDGE,"E187"),sQuery(id+"F3.wireOp",EDGE,"E188"),sQuery(id+"F3.wireOp",EDGE,"E189"),sQuery(id+"F3.wireOp",EDGE,"E190"),sQuery(id+"F3.wireOp",EDGE,"E191"),sQuery(id+"F3.wireOp",EDGE,"E192"),sQuery(id+"F3.wireOp",EDGE,"E193"),sQuery(id+"F3.wireOp",EDGE,"E194"),sQuery(id+"F3.wireOp",EDGE,"E195"),sQuery(id+"F3.wireOp",EDGE,"E196"),sQuery(id+"F3.wireOp",EDGE,"E197"),sQuery(id+"F3.wireOp",EDGE,"E198"),sQuery(id+"F3.wireOp",EDGE,"E199"),sQuery(id+"F3.wireOp",EDGE,"E200"),sQuery(id+"F3.wireOp",EDGE,"E201"),sQuery(id+"F3.wireOp",EDGE,"E202"),sQuery(id+"F3.wireOp",EDGE,"E203"),sQuery(id+"F3.wireOp",EDGE,"E204"),sQuery(id+"F3.wireOp",EDGE,"E205"),sQuery(id+"F3.wireOp",EDGE,"E206"),sQuery(id+"F3.wireOp",EDGE,"E207"),sQuery(id+"F3.wireOp",EDGE,"E208"),sQuery(id+"F3.wireOp",EDGE,"E209"),sQuery(id+"F3.wireOp",EDGE,"E210"),sQuery(id+"F3.wireOp",EDGE,"E211"),sQuery(id+"F3.wireOp",EDGE,"E212"),sQuery(id+"F3.wireOp",EDGE,"E213"),sQuery(id+"F3.wireOp",EDGE,"E214"),sQuery(id+"F3.wireOp",EDGE,"E215"),sQuery(id+"F3.wireOp",EDGE,"E216"),sQuery(id+"F3.wireOp",EDGE,"E217"),sQuery(id+"F3.wireOp",EDGE,"E218"),sQuery(id+"F3.wireOp",EDGE,"E219"),sQuery(id+"F3.wireOp",EDGE,"E220"),sQuery(id+"F3.wireOp",EDGE,"E221"),sQuery(id+"F3.wireOp",EDGE,"E222"),sQuery(id+"F3.wireOp",EDGE,"E223"),sQuery(id+"F3.wireOp",EDGE,"E224"),sQuery(id+"F3.wireOp",EDGE,"E225"),sQuery(id+"F3.wireOp",EDGE,"E226"),sQuery(id+"F3.wireOp",EDGE,"E227"),sQuery(id+"F3.wireOp",EDGE,"E228"),sQuery(id+"F3.wireOp",EDGE,"E229"),sQuery(id+"F3.wireOp",EDGE,"E230"),sQuery(id+"F3.wireOp",EDGE,"E231"),sQuery(id+"F3.wireOp",EDGE,"E232"),sQuery(id+"F3.wireOp",EDGE,"E233"),sQuery(id+"F3.wireOp",EDGE,"E234"),sQuery(id+"F3.wireOp",EDGE,"E235"),sQuery(id+"F3.wireOp",EDGE,"E236"),sQuery(id+"F3.wireOp",EDGE,"E237"),sQuery(id+"F3.wireOp",EDGE,"E238"),sQuery(id+"F3.wireOp",EDGE,"E239"),sQuery(id+"F3.wireOp",EDGE,"E240"),sQuery(id+"F3.wireOp",EDGE,"E241"),sQuery(id+"F3.wireOp",EDGE,"E242"),sQuery(id+"F3.wireOp",EDGE,"E243"),sQuery(id+"F3.wireOp",EDGE,"E244"),sQuery(id+"F3.wireOp",EDGE,"E245"),sQuery(id+"F3.wireOp",EDGE,"E246"),sQuery(id+"F3.wireOp",EDGE,"E247"),sQuery(id+"F3.wireOp",EDGE,"E248"),sQuery(id+"F3.wireOp",EDGE,"E249"),sQuery(id+"F3.wireOp",EDGE,"E250"),sQuery(id+"F3.wireOp",EDGE,"E251"),sQuery(id+"F3.wireOp",EDGE,"E252"),sQuery(id+"F3.wireOp",EDGE,"E253"),sQuery(id+"F3.wireOp",EDGE,"E254"),sQuery(id+"F3.wireOp",EDGE,"E255"),sQuery(id+"F3.wireOp",EDGE,"E256"),sQuery(id+"F3.wireOp",EDGE,"E257"),sQuery(id+"F3.wireOp",EDGE,"E258"),sQuery(id+"F3.wireOp",EDGE,"E259"),sQuery(id+"F3.wireOp",EDGE,"E260"),sQuery(id+"F3.wireOp",EDGE,"E261"),sQuery(id+"F3.wireOp",EDGE,"E262"),sQuery(id+"F3.wireOp",EDGE,"E263"),sQuery(id+"F3.wireOp",EDGE,"E264"),sQuery(id+"F3.wireOp",EDGE,"E265"),sQuery(id+"F3.wireOp",EDGE,"E266"),sQuery(id+"F3.wireOp",EDGE,"E267"),sQuery(id+"F3.wireOp",EDGE,"E268"),sQuery(id+"F3.wireOp",EDGE,"E269"),sQuery(id+"F3.wireOp",EDGE,"E270"),sQuery(id+"F3.wireOp",EDGE,"E271"),sQuery(id+"F3.wireOp",EDGE,"E272"),sQuery(id+"F3.wireOp",EDGE,"E273"),sQuery(id+"F3.wireOp",EDGE,"E274"),sQuery(id+"F3.wireOp",EDGE,"E275"),sQuery(id+"F3.wireOp",EDGE,"E276"),sQuery(id+"F3.wireOp",EDGE,"E277"),sQuery(id+"F3.wireOp",EDGE,"E278"),sQuery(id+"F3.wireOp",EDGE,"E279"),sQuery(id+"F3.wireOp",EDGE,"E280"),sQuery(id+"F3.wireOp",EDGE,"E281"),sQuery(id+"F3.wireOp",EDGE,"E282"),sQuery(id+"F3.wireOp",EDGE,"E283"),sQuery(id+"F3.wireOp",EDGE,"E284"),sQuery(id+"F3.wireOp",EDGE,"E285"),sQuery(id+"F3.wireOp",EDGE,"E286"),sQuery(id+"F3.wireOp",EDGE,"E287"),sQuery(id+"F3.wireOp",EDGE,"E288"),sQuery(id+"F3.wireOp",EDGE,"E289"),sQuery(id+"F3.wireOp",EDGE,"E290"),sQuery(id+"F3.wireOp",EDGE,"E291"),sQuery(id+"F3.wireOp",EDGE,"E292"),sQuery(id+"F3.wireOp",EDGE,"E293"),sQuery(id+"F3.wireOp",EDGE,"E294"),sQuery(id+"F3.wireOp",EDGE,"E295"),sQuery(id+"F3.wireOp",EDGE,"E296"),sQuery(id+"F3.wireOp",EDGE,"E297"),sQuery(id+"F3.wireOp",EDGE,"E298"),sQuery(id+"F3.wireOp",EDGE,"E299"),sQuery(id+"F3.wireOp",EDGE,"E300"),sQuery(id+"F3.wireOp",EDGE,"E301"),sQuery(id+"F3.wireOp",EDGE,"E302"),sQuery(id+"F3.wireOp",EDGE,"E303"),sQuery(id+"F3.wireOp",EDGE,"E304"),sQuery(id+"F3.wireOp",EDGE,"E305"),sQuery(id+"F3.wireOp",EDGE,"E306"),sQuery(id+"F3.wireOp",EDGE,"E307"),sQuery(id+"F3.wireOp",EDGE,"E308"),sQuery(id+"F3.wireOp",EDGE,"E309"),sQuery(id+"F3.wireOp",EDGE,"E310"),sQuery(id+"F3.wireOp",EDGE,"E311"),sQuery(id+"F3.wireOp",EDGE,"E312"),sQuery(id+"F3.wireOp",EDGE,"E313"),sQuery(id+"F3.wireOp",EDGE,"E314"),sQuery(id+"F3.wireOp",EDGE,"E315"),sQuery(id+"F3.wireOp",EDGE,"E316"),sQuery(id+"F3.wireOp",EDGE,"E317"),sQuery(id+"F3.wireOp",EDGE,"E318"),sQuery(id+"F3.wireOp",EDGE,"E319"),sQuery(id+"F3.wireOp",EDGE,"E320"),sQuery(id+"F3.wireOp",EDGE,"E321"),sQuery(id+"F3.wireOp",EDGE,"E322"),sQuery(id+"F3.wireOp",EDGE,"E323"),sQuery(id+"F3.wireOp",EDGE,"E324"),sQuery(id+"F3.wireOp",EDGE,"E325"),sQuery(id+"F3.wireOp",EDGE,"E326"),sQuery(id+"F3.wireOp",EDGE,"E327"),sQuery(id+"F3.wireOp",EDGE,"E328"),sQuery(id+"F3.wireOp",EDGE,"E329"),sQuery(id+"F3.wireOp",EDGE,"E330"),sQuery(id+"F3.wireOp",EDGE,"E331"),sQuery(id+"F3.wireOp",EDGE,"E332"),sQuery(id+"F3.wireOp",EDGE,"E333"),sQuery(id+"F3.wireOp",EDGE,"E334"),sQuery(id+"F3.wireOp",EDGE,"E335"),sQuery(id+"F3.wireOp",EDGE,"E336"),sQuery(id+"F3.wireOp",EDGE,"E337"),sQuery(id+"F3.wireOp",EDGE,"E338"),sQuery(id+"F3.wireOp",EDGE,"E339"),sQuery(id+"F3.wireOp",EDGE,"E340"),sQuery(id+"F3.wireOp",EDGE,"E341"),sQuery(id+"F3.wireOp",EDGE,"E342"),sQuery(id+"F3.wireOp",EDGE,"E343"),sQuery(id+"F3.wireOp",EDGE,"E344"),sQuery(id+"F3.wireOp",EDGE,"E345"),sQuery(id+"F3.wireOp",EDGE,"E346"),sQuery(id+"F3.wireOp",EDGE,"E347"),sQuery(id+"F3.wireOp",EDGE,"E348"),sQuery(id+"F3.wireOp",EDGE,"E349"),sQuery(id+"F3.wireOp",EDGE,"E350"),sQuery(id+"F3.wireOp",EDGE,"E351"),sQuery(id+"F3.wireOp",EDGE,"E352"),sQuery(id+"F3.wireOp",EDGE,"E353"),sQuery(id+"F3.wireOp",EDGE,"E354"),sQuery(id+"F3.wireOp",EDGE,"E355"),sQuery(id+"F3.wireOp",EDGE,"E356"),sQuery(id+"F3.wireOp",EDGE,"E357"),sQuery(id+"F3.wireOp",EDGE,"E358"),sQuery(id+"F3.wireOp",EDGE,"E359"),sQuery(id+"F3.wireOp",EDGE,"E360"),sQuery(id+"F3.wireOp",EDGE,"E361"),sQuery(id+"F3.wireOp",EDGE,"E362"),sQuery(id+"F3.wireOp",EDGE,"E363"),sQuery(id+"F3.wireOp",EDGE,"E364"),sQuery(id+"F3.wireOp",EDGE,"E365"),sQuery(id+"F3.wireOp",EDGE,"E366"),sQuery(id+"F3.wireOp",EDGE,"E367"),sQuery(id+"F3.wireOp",EDGE,"E368"),sQuery(id+"F3.wireOp",EDGE,"E369"),sQuery(id+"F3.wireOp",EDGE,"E370"),sQuery(id+"F3.wireOp",EDGE,"E371"),sQuery(id+"F3.wireOp",EDGE,"E372"),sQuery(id+"F3.wireOp",EDGE,"E373"),sQuery(id+"F3.wireOp",EDGE,"E374"),sQuery(id+"F3.wireOp",EDGE,"E375"),sQuery(id+"F3.wireOp",EDGE,"E376"),sQuery(id+"F3.wireOp",EDGE,"E377"),sQuery(id+"F3.wireOp",EDGE,"E378"),sQuery(id+"F3.wireOp",EDGE,"E379"),sQuery(id+"F3.wireOp",EDGE,"E380"),sQuery(id+"F3.wireOp",EDGE,"E381"),sQuery(id+"F3.wireOp",EDGE,"E382"),sQuery(id+"F3.wireOp",EDGE,"E383"),sQuery(id+"F3.wireOp",EDGE,"E384"),sQuery(id+"F3.wireOp",EDGE,"E385"),sQuery(id+"F3.wireOp",EDGE,"E386"),sQuery(id+"F3.wireOp",EDGE,"E387"),sQuery(id+"F3.wireOp",EDGE,"E388"),sQuery(id+"F3.wireOp",EDGE,"E389"),sQuery(id+"F3.wireOp",EDGE,"E390"),sQuery(id+"F3.wireOp",EDGE,"E391"),sQuery(id+"F3.wireOp",EDGE,"E392"),sQuery(id+"F3.wireOp",EDGE,"E393"),sQuery(id+"F3.wireOp",EDGE,"E394"),sQuery(id+"F3.wireOp",EDGE,"E395"),sQuery(id+"F3.wireOp",EDGE,"E396"),sQuery(id+"F3.wireOp",EDGE,"E397"),sQuery(id+"F3.wireOp",EDGE,"E398"),sQuery(id+"F3.wireOp",EDGE,"E399"),sQuery(id+"F3.wireOp",EDGE,"E400"),sQuery(id+"F3.wireOp",EDGE,"E401"),sQuery(id+"F3.wireOp",EDGE,"E402"),sQuery(id+"F3.wireOp",EDGE,"E403"),sQuery(id+"F3.wireOp",EDGE,"E404"),sQuery(id+"F3.wireOp",EDGE,"E405"),sQuery(id+"F3.wireOp",EDGE,"E406"),sQuery(id+"F3.wireOp",EDGE,"E407"),sQuery(id+"F3.wireOp",EDGE,"E408"),sQuery(id+"F3.wireOp",EDGE,"E409"),sQuery(id+"F3.wireOp",EDGE,"E410"),sQuery(id+"F3.wireOp",EDGE,"E411"),sQuery(id+"F3.wireOp",EDGE,"E412"),sQuery(id+"F3.wireOp",EDGE,"E413"),sQuery(id+"F3.wireOp",EDGE,"E414"),sQuery(id+"F3.wireOp",EDGE,"E415"),sQuery(id+"F3.wireOp",EDGE,"E416"),sQuery(id+"F3.wireOp",EDGE,"E417"),sQuery(id+"F3.wireOp",EDGE,"E418"),sQuery(id+"F3.wireOp",EDGE,"E419"),sQuery(id+"F3.wireOp",EDGE,"E420"),sQuery(id+"F3.wireOp",EDGE,"E421"),sQuery(id+"F3.wireOp",EDGE,"E422"),sQuery(id+"F3.wireOp",EDGE,"E423"),sQuery(id+"F3.wireOp",EDGE,"E424"),sQuery(id+"F3.wireOp",EDGE,"E425"),sQuery(id+"F3.wireOp",EDGE,"E426"),sQuery(id+"F3.wireOp",EDGE,"E427"),sQuery(id+"F3.wireOp",EDGE,"E428"),sQuery(id+"F3.wireOp",EDGE,"E429"),sQuery(id+"F3.wireOp",EDGE,"E430"),sQuery(id+"F3.wireOp",EDGE,"E431"),sQuery(id+"F3.wireOp",EDGE,"E432"),sQuery(id+"F3.wireOp",EDGE,"E433"),sQuery(id+"F3.wireOp",EDGE,"E434"),sQuery(id+"F3.wireOp",EDGE,"E435"),sQuery(id+"F3.wireOp",EDGE,"E436"),sQuery(id+"F3.wireOp",EDGE,"E437"),sQuery(id+"F3.wireOp",EDGE,"E438"),sQuery(id+"F3.wireOp",EDGE,"E439"),sQuery(id+"F3.wireOp",EDGE,"E440"),sQuery(id+"F3.wireOp",EDGE,"E441"),sQuery(id+"F3.wireOp",EDGE,"E442"),sQuery(id+"F3.wireOp",EDGE,"E443"),sQuery(id+"F3.wireOp",EDGE,"E444"),sQuery(id+"F3.wireOp",EDGE,"E445"),sQuery(id+"F3.wireOp",EDGE,"E446"),sQuery(id+"F3.wireOp",EDGE,"E447"),sQuery(id+"F3.wireOp",EDGE,"E448"),sQuery(id+"F3.wireOp",EDGE,"E449"),sQuery(id+"F3.wireOp",EDGE,"E450"),sQuery(id+"F3.wireOp",EDGE,"E451"),sQuery(id+"F3.wireOp",EDGE,"E452"),sQuery(id+"F3.wireOp",EDGE,"E453"),sQuery(id+"F3.wireOp",EDGE,"E454"),sQuery(id+"F3.wireOp",EDGE,"E455"),sQuery(id+"F3.wireOp",EDGE,"E456"),sQuery(id+"F3.wireOp",EDGE,"E457"),sQuery(id+"F3.wireOp",EDGE,"E458"),sQuery(id+"F3.wireOp",EDGE,"E459"),sQuery(id+"F3.wireOp",EDGE,"E460"),sQuery(id+"F3.wireOp",EDGE,"E461"),sQuery(id+"F3.wireOp",EDGE,"E462"),sQuery(id+"F3.wireOp",EDGE,"E463"),sQuery(id+"F3.wireOp",EDGE,"E464"),sQuery(id+"F3.wireOp",EDGE,"E465"),sQuery(id+"F3.wireOp",EDGE,"E466"),sQuery(id+"F3.wireOp",EDGE,"E467"),sQuery(id+"F3.wireOp",EDGE,"E468"),sQuery(id+"F3.wireOp",EDGE,"E469"),sQuery(id+"F3.wireOp",EDGE,"E470"),sQuery(id+"F3.wireOp",EDGE,"E471"),sQuery(id+"F3.wireOp",EDGE,"E472"),sQuery(id+"F3.wireOp",EDGE,"E473"),sQuery(id+"F3.wireOp",EDGE,"E474"),sQuery(id+"F3.wireOp",EDGE,"E475"),sQuery(id+"F3.wireOp",EDGE,"E476"),sQuery(id+"F3.wireOp",EDGE,"E477"),sQuery(id+"F3.wireOp",EDGE,"E478"),sQuery(id+"F3.wireOp",EDGE,"E479"),sQuery(id+"F3.wireOp",EDGE,"E480"),sQuery(id+"F3.wireOp",EDGE,"E481"),sQuery(id+"F3.wireOp",EDGE,"E482"),sQuery(id+"F3.wireOp",EDGE,"E483"),sQuery(id+"F3.wireOp",EDGE,"E484"),sQuery(id+"F3.wireOp",EDGE,"E485"),sQuery(id+"F3.wireOp",EDGE,"E486"),sQuery(id+"F3.wireOp",EDGE,"E487"),sQuery(id+"F3.wireOp",EDGE,"E488"),sQuery(id+"F3.wireOp",EDGE,"E489"),sQuery(id+"F3.wireOp",EDGE,"E490"),sQuery(id+"F3.wireOp",EDGE,"E491"),sQuery(id+"F3.wireOp",EDGE,"E492"),sQuery(id+"F3.wireOp",EDGE,"E493"),sQuery(id+"F3.wireOp",EDGE,"E494"),sQuery(id+"F3.wireOp",EDGE,"E495"),sQuery(id+"F3.wireOp",EDGE,"E496"),sQuery(id+"F3.wireOp",EDGE,"E497"),sQuery(id+"F3.wireOp",EDGE,"E498"),sQuery(id+"F3.wireOp",EDGE,"E499"),sQuery(id+"F3.wireOp",EDGE,"E500"),sQuery(id+"F3.wireOp",EDGE,"E501"),sQuery(id+"F3.wireOp",EDGE,"E502"),sQuery(id+"F3.wireOp",EDGE,"E503"),sQuery(id+"F3.wireOp",EDGE,"E504"),sQuery(id+"F3.wireOp",EDGE,"E505"),sQuery(id+"F3.wireOp",EDGE,"E506"),sQuery(id+"F3.wireOp",EDGE,"E507"),sQuery(id+"F3.wireOp",EDGE,"E508"),sQuery(id+"F3.wireOp",EDGE,"E509"),sQuery(id+"F3.wireOp",EDGE,"E510"),sQuery(id+"F3.wireOp",EDGE,"E511"),sQuery(id+"F3.wireOp",EDGE,"E512"),sQuery(id+"F3.wireOp",EDGE,"E513"),sQuery(id+"F3.wireOp",EDGE,"E514"),sQuery(id+"F3.wireOp",EDGE,"E515"),sQuery(id+"F3.wireOp",EDGE,"E516"),sQuery(id+"F3.wireOp",EDGE,"E517"),sQuery(id+"F3.wireOp",EDGE,"E518"),sQuery(id+"F3.wireOp",EDGE,"E519"),sQuery(id+"F3.wireOp",EDGE,"E520"),sQuery(id+"F3.wireOp",EDGE,"E521"),sQuery(id+"F3.wireOp",EDGE,"E522"),sQuery(id+"F3.wireOp",EDGE,"E523"),sQuery(id+"F3.wireOp",EDGE,"E524"),sQuery(id+"F3.wireOp",EDGE,"E525"),sQuery(id+"F3.wireOp",EDGE,"E526"),sQuery(id+"F3.wireOp",EDGE,"E527"),sQuery(id+"F3.wireOp",EDGE,"E528"),sQuery(id+"F3.wireOp",EDGE,"E529"),sQuery(id+"F3.wireOp",EDGE,"E530"),sQuery(id+"F3.wireOp",EDGE,"E531"),sQuery(id+"F3.wireOp",EDGE,"E532"),sQuery(id+"F3.wireOp",EDGE,"E533"),sQuery(id+"F3.wireOp",EDGE,"E534"),sQuery(id+"F3.wireOp",EDGE,"E535"),sQuery(id+"F3.wireOp",EDGE,"E536"),sQuery(id+"F3.wireOp",EDGE,"E537"),sQuery(id+"F3.wireOp",EDGE,"E538"),sQuery(id+"F3.wireOp",EDGE,"E539"),sQuery(id+"F3.wireOp",EDGE,"E540"),sQuery(id+"F3.wireOp",EDGE,"E541"),sQuery(id+"F3.wireOp",EDGE,"E542"),sQuery(id+"F3.wireOp",EDGE,"E543"),sQuery(id+"F3.wireOp",EDGE,"E544"),sQuery(id+"F3.wireOp",EDGE,"E545"),sQuery(id+"F3.wireOp",EDGE,"E546"),sQuery(id+"F3.wireOp",EDGE,"E547"),sQuery(id+"F3.wireOp",EDGE,"E548"),sQuery(id+"F3.wireOp",EDGE,"E549"),sQuery(id+"F3.wireOp",EDGE,"E550"),sQuery(id+"F3.wireOp",EDGE,"E551"),sQuery(id+"F3.wireOp",EDGE,"E552"),sQuery(id+"F3.wireOp",EDGE,"E553"),sQuery(id+"F3.wireOp",EDGE,"E554"),sQuery(id+"F3.wireOp",EDGE,"E555"),sQuery(id+"F3.wireOp",EDGE,"E556"),sQuery(id+"F3.wireOp",EDGE,"E557"),sQuery(id+"F3.wireOp",EDGE,"E558"),sQuery(id+"F3.wireOp",EDGE,"E559"),sQuery(id+"F3.wireOp",EDGE,"E560"),sQuery(id+"F3.wireOp",EDGE,"E561"),sQuery(id+"F3.wireOp",EDGE,"E562"),sQuery(id+"F3.wireOp",EDGE,"E563"),sQuery(id+"F3.wireOp",EDGE,"E564"),sQuery(id+"F3.wireOp",EDGE,"E565"),sQuery(id+"F3.wireOp",EDGE,"E566"),sQuery(id+"F3.wireOp",EDGE,"E567"),sQuery(id+"F3.wireOp",EDGE,"E568"),sQuery(id+"F3.wireOp",EDGE,"E569"),sQuery(id+"F3.wireOp",EDGE,"E570"),sQuery(id+"F3.wireOp",EDGE,"E571"),sQuery(id+"F3.wireOp",EDGE,"E572"),sQuery(id+"F3.wireOp",EDGE,"E573"),sQuery(id+"F3.wireOp",EDGE,"E574"),sQuery(id+"F3.wireOp",EDGE,"E575"),sQuery(id+"F3.wireOp",EDGE,"E576"),sQuery(id+"F3.wireOp",EDGE,"E577"),sQuery(id+"F3.wireOp",EDGE,"E578"),sQuery(id+"F3.wireOp",EDGE,"E579"),sQuery(id+"F3.wireOp",EDGE,"E580"),sQuery(id+"F3.wireOp",EDGE,"E581"),sQuery(id+"F3.wireOp",EDGE,"E582"),sQuery(id+"F3.wireOp",EDGE,"E583"),sQuery(id+"F3.wireOp",EDGE,"E584"),sQuery(id+"F3.wireOp",EDGE,"E585"),sQuery(id+"F3.wireOp",EDGE,"E586"),sQuery(id+"F3.wireOp",EDGE,"E587"),sQuery(id+"F3.wireOp",EDGE,"E588"),sQuery(id+"F3.wireOp",EDGE,"E589"),sQuery(id+"F3.wireOp",EDGE,"E590"),sQuery(id+"F3.wireOp",EDGE,"E591"),sQuery(id+"F3.wireOp",EDGE,"E592"),sQuery(id+"F3.wireOp",EDGE,"E593"),sQuery(id+"F3.wireOp",EDGE,"E594"),sQuery(id+"F3.wireOp",EDGE,"E595"),sQuery(id+"F3.wireOp",EDGE,"E596"),sQuery(id+"F3.wireOp",EDGE,"E597"),sQuery(id+"F3.wireOp",EDGE,"E598"),sQuery(id+"F3.wireOp",EDGE,"E599"),sQuery(id+"F3.wireOp",EDGE,"E600"),sQuery(id+"F3.wireOp",EDGE,"E601"),sQuery(id+"F3.wireOp",EDGE,"E602"),sQuery(id+"F3.wireOp",EDGE,"E603"),sQuery(id+"F3.wireOp",EDGE,"E604"),sQuery(id+"F3.wireOp",EDGE,"E605"),sQuery(id+"F3.wireOp",EDGE,"E606"),sQuery(id+"F3.wireOp",EDGE,"E607"),sQuery(id+"F3.wireOp",EDGE,"E608"),sQuery(id+"F3.wireOp",EDGE,"E609"),sQuery(id+"F3.wireOp",EDGE,"E610"),sQuery(id+"F3.wireOp",EDGE,"E611"),sQuery(id+"F3.wireOp",EDGE,"E612"),sQuery(id+"F3.wireOp",EDGE,"E613"),sQuery(id+"F3.wireOp",EDGE,"E614"),sQuery(id+"F3.wireOp",EDGE,"E615"),sQuery(id+"F3.wireOp",EDGE,"E616"),sQuery(id+"F3.wireOp",EDGE,"E617"),sQuery(id+"F3.wireOp",EDGE,"E618"),sQuery(id+"F3.wireOp",EDGE,"E619"),sQuery(id+"F3.wireOp",EDGE,"E620"),sQuery(id+"F3.wireOp",EDGE,"E621"),sQuery(id+"F3.wireOp",EDGE,"E622"),sQuery(id+"F3.wireOp",EDGE,"E623"),sQuery(id+"F3.wireOp",EDGE,"E624"),sQuery(id+"F3.wireOp",EDGE,"E625"),sQuery(id+"F3.wireOp",EDGE,"E626"),sQuery(id+"F3.wireOp",EDGE,"E627"),sQuery(id+"F3.wireOp",EDGE,"E628"),sQuery(id+"F3.wireOp",EDGE,"E629"),sQuery(id+"F3.wireOp",EDGE,"E630"),sQuery(id+"F3.wireOp",EDGE,"E631"),sQuery(id+"F3.wireOp",EDGE,"E632"),sQuery(id+"F3.wireOp",EDGE,"E633"),sQuery(id+"F3.wireOp",EDGE,"E634"),sQuery(id+"F3.wireOp",EDGE,"E635"),sQuery(id+"F3.wireOp",EDGE,"E636"),sQuery(id+"F3.wireOp",EDGE,"E637"),sQuery(id+"F3.wireOp",EDGE,"E638"),sQuery(id+"F3.wireOp",EDGE,"E639"),sQuery(id+"F3.wireOp",EDGE,"E640"),sQuery(id+"F3.wireOp",EDGE,"E641"),sQuery(id+"F3.wireOp",EDGE,"E642"),sQuery(id+"F3.wireOp",EDGE,"E643"),sQuery(id+"F3.wireOp",EDGE,"E644"),sQuery(id+"F3.wireOp",EDGE,"E645"),sQuery(id+"F3.wireOp",EDGE,"E646"),sQuery(id+"F3.wireOp",EDGE,"E647"),sQuery(id+"F3.wireOp",EDGE,"E648"),sQuery(id+"F3.wireOp",EDGE,"E649"),sQuery(id+"F3.wireOp",EDGE,"E650"),sQuery(id+"F3.wireOp",EDGE,"E651"),sQuery(id+"F3.wireOp",EDGE,"E652"),sQuery(id+"F3.wireOp",EDGE,"E653"),sQuery(id+"F3.wireOp",EDGE,"E654"),sQuery(id+"F3.wireOp",EDGE,"E655"),sQuery(id+"F3.wireOp",EDGE,"E656"),sQuery(id+"F3.wireOp",EDGE,"E657"),sQuery(id+"F3.wireOp",EDGE,"E658"),sQuery(id+"F3.wireOp",EDGE,"E659"),sQuery(id+"F3.wireOp",EDGE,"E660"),sQuery(id+"F3.wireOp",EDGE,"E661"),sQuery(id+"F3.wireOp",EDGE,"E662"),sQuery(id+"F3.wireOp",EDGE,"E663"),sQuery(id+"F3.wireOp",EDGE,"E664"),sQuery(id+"F3.wireOp",EDGE,"E665"),sQuery(id+"F3.wireOp",EDGE,"E666"),sQuery(id+"F3.wireOp",EDGE,"E667"),sQuery(id+"F3.wireOp",EDGE,"E668"),sQuery(id+"F3.wireOp",EDGE,"E669"),sQuery(id+"F3.wireOp",EDGE,"E670"),sQuery(id+"F3.wireOp",EDGE,"E671"),sQuery(id+"F3.wireOp",EDGE,"E672"),sQuery(id+"F3.wireOp",EDGE,"E673"),sQuery(id+"F3.wireOp",EDGE,"E674"),sQuery(id+"F3.wireOp",EDGE,"E675"),sQuery(id+"F3.wireOp",EDGE,"E676"),sQuery(id+"F3.wireOp",EDGE,"E677"),sQuery(id+"F3.wireOp",EDGE,"E678"),sQuery(id+"F3.wireOp",EDGE,"E679"),sQuery(id+"F3.wireOp",EDGE,"E680"),sQuery(id+"F3.wireOp",EDGE,"E681"),sQuery(id+"F3.wireOp",EDGE,"E682"),sQuery(id+"F3.wireOp",EDGE,"E683"),sQuery(id+"F3.wireOp",EDGE,"E684"),sQuery(id+"F3.wireOp",EDGE,"E685"),sQuery(id+"F3.wireOp",EDGE,"E686"),sQuery(id+"F3.wireOp",EDGE,"E687"),sQuery(id+"F3.wireOp",EDGE,"E688"),sQuery(id+"F3.wireOp",EDGE,"E689"),sQuery(id+"F3.wireOp",EDGE,"E690"),sQuery(id+"F3.wireOp",EDGE,"E691"),sQuery(id+"F3.wireOp",EDGE,"E692"),sQuery(id+"F3.wireOp",EDGE,"E693"),sQuery(id+"F3.wireOp",EDGE,"E694"),sQuery(id+"F3.wireOp",EDGE,"E695"),sQuery(id+"F3.wireOp",EDGE,"E696"),sQuery(id+"F3.wireOp",EDGE,"E697"),sQuery(id+"F3.wireOp",EDGE,"E698"),sQuery(id+"F3.wireOp",EDGE,"E699"),sQuery(id+"F3.wireOp",EDGE,"E700"),sQuery(id+"F3.wireOp",EDGE,"E701"),sQuery(id+"F3.wireOp",EDGE,"E702"),sQuery(id+"F3.wireOp",EDGE,"E703"),sQuery(id+"F3.wireOp",EDGE,"E704"),sQuery(id+"F3.wireOp",EDGE,"E705"),sQuery(id+"F3.wireOp",EDGE,"E706"),sQuery(id+"F3.wireOp",EDGE,"E707"),sQuery(id+"F3.wireOp",EDGE,"E708"),sQuery(id+"F3.wireOp",EDGE,"E709"),sQuery(id+"F3.wireOp",EDGE,"E710"),sQuery(id+"F3.wireOp",EDGE,"E711"),sQuery(id+"F3.wireOp",EDGE,"E712"),sQuery(id+"F3.wireOp",EDGE,"E713"),sQuery(id+"F3.wireOp",EDGE,"E714"),sQuery(id+"F3.wireOp",EDGE,"E715"),sQuery(id+"F3.wireOp",EDGE,"E716"),sQuery(id+"F3.wireOp",EDGE,"E717"),sQuery(id+"F3.wireOp",EDGE,"E718"),sQuery(id+"F3.wireOp",EDGE,"E719"),sQuery(id+"F3.wireOp",EDGE,"E720"),sQuery(id+"F3.wireOp",EDGE,"E721"),sQuery(id+"F3.wireOp",EDGE,"E722"),sQuery(id+"F3.wireOp",EDGE,"E723"),sQuery(id+"F3.wireOp",EDGE,"E724"),sQuery(id+"F3.wireOp",EDGE,"E725"),sQuery(id+"F3.wireOp",EDGE,"E726"),sQuery(id+"F3.wireOp",EDGE,"E727"),sQuery(id+"F3.wireOp",EDGE,"E728"),sQuery(id+"F3.wireOp",EDGE,"E729"),sQuery(id+"F3.wireOp",EDGE,"E730"),sQuery(id+"F3.wireOp",EDGE,"E731"),sQuery(id+"F3.wireOp",EDGE,"E732"),sQuery(id+"F3.wireOp",EDGE,"E733"),sQuery(id+"F3.wireOp",EDGE,"E734"),sQuery(id+"F3.wireOp",EDGE,"E735"),sQuery(id+"F3.wireOp",EDGE,"E736"),sQuery(id+"F3.wireOp",EDGE,"E737"),sQuery(id+"F3.wireOp",EDGE,"E738"),sQuery(id+"F3.wireOp",EDGE,"E739"),sQuery(id+"F3.wireOp",EDGE,"E740"),sQuery(id+"F3.wireOp",EDGE,"E741"),sQuery(id+"F3.wireOp",EDGE,"E742"),sQuery(id+"F3.wireOp",EDGE,"E743"),sQuery(id+"F3.wireOp",EDGE,"E744"),sQuery(id+"F3.wireOp",EDGE,"E745"),sQuery(id+"F3.wireOp",EDGE,"E746"),sQuery(id+"F3.wireOp",EDGE,"E747"),sQuery(id+"F3.wireOp",EDGE,"E748"),sQuery(id+"F3.wireOp",EDGE,"E749"),sQuery(id+"F3.wireOp",EDGE,"E750"),sQuery(id+"F3.wireOp",EDGE,"E751"),sQuery(id+"F3.wireOp",EDGE,"E752"),sQuery(id+"F3.wireOp",EDGE,"E753"),sQuery(id+"F3.wireOp",EDGE,"E754"),sQuery(id+"F3.wireOp",EDGE,"E755"),sQuery(id+"F3.wireOp",EDGE,"E756"),sQuery(id+"F3.wireOp",EDGE,"E757"),sQuery(id+"F3.wireOp",EDGE,"E758"),sQuery(id+"F3.wireOp",EDGE,"E759"),sQuery(id+"F3.wireOp",EDGE,"E760"),sQuery(id+"F3.wireOp",EDGE,"E761"),sQuery(id+"F3.wireOp",EDGE,"E762"),sQuery(id+"F3.wireOp",EDGE,"E763"),sQuery(id+"F3.wireOp",EDGE,"E764"),sQuery(id+"F3.wireOp",EDGE,"E765"),sQuery(id+"F3.wireOp",EDGE,"E766"),sQuery(id+"F3.wireOp",EDGE,"E767"),sQuery(id+"F3.wireOp",EDGE,"E768"),sQuery(id+"F3.wireOp",EDGE,"E769"),sQuery(id+"F3.wireOp",EDGE,"E770"),sQuery(id+"F3.wireOp",EDGE,"E771"),sQuery(id+"F3.wireOp",EDGE,"E772"),sQuery(id+"F3.wireOp",EDGE,"E773"),sQuery(id+"F3.wireOp",EDGE,"E774"),sQuery(id+"F3.wireOp",EDGE,"E775"),sQuery(id+"F3.wireOp",EDGE,"E776"),sQuery(id+"F3.wireOp",EDGE,"E777"),sQuery(id+"F3.wireOp",EDGE,"E778"),sQuery(id+"F3.wireOp",EDGE,"E779"),sQuery(id+"F3.wireOp",EDGE,"E780"),sQuery(id+"F3.wireOp",EDGE,"E781"),sQuery(id+"F3.wireOp",EDGE,"E782"),sQuery(id+"F3.wireOp",EDGE,"E783"),sQuery(id+"F3.wireOp",EDGE,"E784"),sQuery(id+"F3.wireOp",EDGE,"E785"),sQuery(id+"F3.wireOp",EDGE,"E786"),sQuery(id+"F3.wireOp",EDGE,"E787"),sQuery(id+"F3.wireOp",EDGE,"E788"),sQuery(id+"F3.wireOp",EDGE,"E789"),sQuery(id+"F3.wireOp",EDGE,"E790"),sQuery(id+"F3.wireOp",EDGE,"E791"),sQuery(id+"F3.wireOp",EDGE,"E792"),sQuery(id+"F3.wireOp",EDGE,"E793"),sQuery(id+"F3.wireOp",EDGE,"E794"),sQuery(id+"F3.wireOp",EDGE,"E795"),sQuery(id+"F3.wireOp",EDGE,"E796"),sQuery(id+"F3.wireOp",EDGE,"E797"),sQuery(id+"F3.wireOp",EDGE,"E798"),sQuery(id+"F3.wireOp",EDGE,"E799"),sQuery(id+"F3.wireOp",EDGE,"E800"),sQuery(id+"F3.wireOp",EDGE,"E801"),sQuery(id+"F3.wireOp",EDGE,"E802"),sQuery(id+"F3.wireOp",EDGE,"E803"),sQuery(id+"F3.wireOp",EDGE,"E804"),sQuery(id+"F3.wireOp",EDGE,"E805"),sQuery(id+"F3.wireOp",EDGE,"E806"),sQuery(id+"F3.wireOp",EDGE,"E807"),sQuery(id+"F3.wireOp",EDGE,"E808"),sQuery(id+"F3.wireOp",EDGE,"E809"),sQuery(id+"F3.wireOp",EDGE,"E810"),sQuery(id+"F3.wireOp",EDGE,"E811"),sQuery(id+"F3.wireOp",EDGE,"E812"),sQuery(id+"F3.wireOp",EDGE,"E813"),sQuery(id+"F3.wireOp",EDGE,"E814"),sQuery(id+"F3.wireOp",EDGE,"E815"),sQuery(id+"F3.wireOp",EDGE,"E816"),sQuery(id+"F3.wireOp",EDGE,"E817"),sQuery(id+"F3.wireOp",EDGE,"E818"),sQuery(id+"F3.wireOp",EDGE,"E819"),sQuery(id+"F3.wireOp",EDGE,"E820"),sQuery(id+"F3.wireOp",EDGE,"E821"),sQuery(id+"F3.wireOp",EDGE,"E822"),sQuery(id+"F3.wireOp",EDGE,"E823"),sQuery(id+"F3.wireOp",EDGE,"E824"),sQuery(id+"F3.wireOp",EDGE,"E825"),sQuery(id+"F3.wireOp",EDGE,"E826"),sQuery(id+"F3.wireOp",EDGE,"E827"),sQuery(id+"F3.wireOp",EDGE,"E828"),sQuery(id+"F3.wireOp",EDGE,"E829"),sQuery(id+"F3.wireOp",EDGE,"E830"),sQuery(id+"F3.wireOp",EDGE,"E831"),sQuery(id+"F3.wireOp",EDGE,"E832"),sQuery(id+"F3.wireOp",EDGE,"E833"),sQuery(id+"F3.wireOp",EDGE,"E834"),sQuery(id+"F3.wireOp",EDGE,"E835"),sQuery(id+"F3.wireOp",EDGE,"E836"),sQuery(id+"F3.wireOp",EDGE,"E837"),sQuery(id+"F3.wireOp",EDGE,"E838"),sQuery(id+"F3.wireOp",EDGE,"E839"),sQuery(id+"F3.wireOp",EDGE,"E840"),sQuery(id+"F3.wireOp",EDGE,"E841"),sQuery(id+"F3.wireOp",EDGE,"E842"),sQuery(id+"F3.wireOp",EDGE,"E843"),sQuery(id+"F3.wireOp",EDGE,"E844"),sQuery(id+"F3.wireOp",EDGE,"E845"),sQuery(id+"F3.wireOp",EDGE,"E846"),sQuery(id+"F3.wireOp",EDGE,"E847"),sQuery(id+"F3.wireOp",EDGE,"E848"),sQuery(id+"F3.wireOp",EDGE,"E849"),sQuery(id+"F3.wireOp",EDGE,"E850"),sQuery(id+"F3.wireOp",EDGE,"E851"),sQuery(id+"F3.wireOp",EDGE,"E852"),sQuery(id+"F3.wireOp",EDGE,"E853"),sQuery(id+"F3.wireOp",EDGE,"E854"),sQuery(id+"F3.wireOp",EDGE,"E855"),sQuery(id+"F3.wireOp",EDGE,"E856"),sQuery(id+"F3.wireOp",EDGE,"E857"),sQuery(id+"F3.wireOp",EDGE,"E858"),sQuery(id+"F3.wireOp",EDGE,"E859"),sQuery(id+"F3.wireOp",EDGE,"E860"),sQuery(id+"F3.wireOp",EDGE,"E861"),sQuery(id+"F3.wireOp",EDGE,"E862"),sQuery(id+"F3.wireOp",EDGE,"E863"),sQuery(id+"F3.wireOp",EDGE,"E864"),sQuery(id+"F3.wireOp",EDGE,"E865"),sQuery(id+"F3.wireOp",EDGE,"E866"),sQuery(id+"F3.wireOp",EDGE,"E867"),sQuery(id+"F3.wireOp",EDGE,"E868"),sQuery(id+"F3.wireOp",EDGE,"E869"),sQuery(id+"F3.wireOp",EDGE,"E870"),sQuery(id+"F3.wireOp",EDGE,"E871"),sQuery(id+"F3.wireOp",EDGE,"E872"),sQuery(id+"F3.wireOp",EDGE,"E873"),sQuery(id+"F3.wireOp",EDGE,"E874"),sQuery(id+"F3.wireOp",EDGE,"E875"),sQuery(id+"F3.wireOp",EDGE,"E876"),sQuery(id+"F3.wireOp",EDGE,"E877"),sQuery(id+"F3.wireOp",EDGE,"E878"),sQuery(id+"F3.wireOp",EDGE,"E879"),sQuery(id+"F3.wireOp",EDGE,"E880"),sQuery(id+"F3.wireOp",EDGE,"E881"),sQuery(id+"F3.wireOp",EDGE,"E882"),sQuery(id+"F3.wireOp",EDGE,"E883"),sQuery(id+"F3.wireOp",EDGE,"E884"),sQuery(id+"F3.wireOp",EDGE,"E885"),sQuery(id+"F3.wireOp",EDGE,"E886"),sQuery(id+"F3.wireOp",EDGE,"E887"),sQuery(id+"F3.wireOp",EDGE,"E888"),sQuery(id+"F3.wireOp",EDGE,"E889"),sQuery(id+"F3.wireOp",EDGE,"E890"),sQuery(id+"F3.wireOp",EDGE,"E891"),sQuery(id+"F3.wireOp",EDGE,"E892"),sQuery(id+"F3.wireOp",EDGE,"E893"),sQuery(id+"F3.wireOp",EDGE,"E894"),sQuery(id+"F3.wireOp",EDGE,"E895"),sQuery(id+"F3.wireOp",EDGE,"E896"),sQuery(id+"F3.wireOp",EDGE,"E897"),sQuery(id+"F3.wireOp",EDGE,"E898"),sQuery(id+"F3.wireOp",EDGE,"E899"),sQuery(id+"F3.wireOp",EDGE,"E900"),sQuery(id+"F3.wireOp",EDGE,"E901"),sQuery(id+"F3.wireOp",EDGE,"E902"),sQuery(id+"F3.wireOp",EDGE,"E903"),sQuery(id+"F3.wireOp",EDGE,"E904"),sQuery(id+"F3.wireOp",EDGE,"E905"),sQuery(id+"F3.wireOp",EDGE,"E906"),sQuery(id+"F3.wireOp",EDGE,"E907"),sQuery(id+"F3.wireOp",EDGE,"E908"),sQuery(id+"F3.wireOp",EDGE,"E909"),sQuery(id+"F3.wireOp",EDGE,"E910"),sQuery(id+"F3.wireOp",EDGE,"E911"),sQuery(id+"F3.wireOp",EDGE,"E912"),sQuery(id+"F3.wireOp",EDGE,"E913"),sQuery(id+"F3.wireOp",EDGE,"E914"),sQuery(id+"F3.wireOp",EDGE,"E915"),sQuery(id+"F3.wireOp",EDGE,"E916"),sQuery(id+"F3.wireOp",EDGE,"E917"),sQuery(id+"F3.wireOp",EDGE,"E918"),sQuery(id+"F3.wireOp",EDGE,"E919"),sQuery(id+"F3.wireOp",EDGE,"E920"),sQuery(id+"F3.wireOp",EDGE,"E921"),sQuery(id+"F3.wireOp",EDGE,"E922"),sQuery(id+"F3.wireOp",EDGE,"E923"),sQuery(id+"F3.wireOp",EDGE,"E924"),sQuery(id+"F3.wireOp",EDGE,"E925"),sQuery(id+"F3.wireOp",EDGE,"E926"),sQuery(id+"F3.wireOp",EDGE,"E927"),sQuery(id+"F3.wireOp",EDGE,"E928"),sQuery(id+"F3.wireOp",EDGE,"E929"),sQuery(id+"F3.wireOp",EDGE,"E930"),sQuery(id+"F3.wireOp",EDGE,"E931"),sQuery(id+"F3.wireOp",EDGE,"E932"),sQuery(id+"F3.wireOp",EDGE,"E933"),sQuery(id+"F3.wireOp",EDGE,"E934"),sQuery(id+"F3.wireOp",EDGE,"E935"),sQuery(id+"F3.wireOp",EDGE,"E936"),sQuery(id+"F3.wireOp",EDGE,"E937"),sQuery(id+"F3.wireOp",EDGE,"E938"),sQuery(id+"F3.wireOp",EDGE,"E939"),sQuery(id+"F3.wireOp",EDGE,"E940"),sQuery(id+"F3.wireOp",EDGE,"E941"),sQuery(id+"F3.wireOp",EDGE,"E942"),sQuery(id+"F3.wireOp",EDGE,"E943"),sQuery(id+"F3.wireOp",EDGE,"E944"),sQuery(id+"F3.wireOp",EDGE,"E945"),sQuery(id+"F3.wireOp",EDGE,"E946"),sQuery(id+"F3.wireOp",EDGE,"E947"),sQuery(id+"F3.wireOp",EDGE,"E948"),sQuery(id+"F3.wireOp",EDGE,"E949"),sQuery(id+"F3.wireOp",EDGE,"E950"),sQuery(id+"F3.wireOp",EDGE,"E951"),sQuery(id+"F3.wireOp",EDGE,"E952"),sQuery(id+"F3.wireOp",EDGE,"E953"),sQuery(id+"F3.wireOp",EDGE,"E954"),sQuery(id+"F3.wireOp",EDGE,"E955"),sQuery(id+"F3.wireOp",EDGE,"E956"),sQuery(id+"F3.wireOp",EDGE,"E957"),sQuery(id+"F3.wireOp",EDGE,"E958"),sQuery(id+"F3.wireOp",EDGE,"E959"),sQuery(id+"F3.wireOp",EDGE,"E960"),sQuery(id+"F3.wireOp",EDGE,"E961"),sQuery(id+"F3.wireOp",EDGE,"E962"),sQuery(id+"F3.wireOp",EDGE,"E963"),sQuery(id+"F3.wireOp",EDGE,"E964"),sQuery(id+"F3.wireOp",EDGE,"E965"),sQuery(id+"F3.wireOp",EDGE,"E966"),sQuery(id+"F3.wireOp",EDGE,"E967"),sQuery(id+"F3.wireOp",EDGE,"E968"),sQuery(id+"F3.wireOp",EDGE,"E969"),sQuery(id+"F3.wireOp",EDGE,"E970"),sQuery(id+"F3.wireOp",EDGE,"E971"),sQuery(id+"F3.wireOp",EDGE,"E972"),sQuery(id+"F3.wireOp",EDGE,"E973"),sQuery(id+"F3.wireOp",EDGE,"E974"),sQuery(id+"F3.wireOp",EDGE,"E975"),sQuery(id+"F3.wireOp",EDGE,"E976"),sQuery(id+"F3.wireOp",EDGE,"E977"),sQuery(id+"F3.wireOp",EDGE,"E978"),sQuery(id+"F3.wireOp",EDGE,"E979"),sQuery(id+"F3.wireOp",EDGE,"E980"),sQuery(id+"F3.wireOp",EDGE,"E981"),sQuery(id+"F3.wireOp",EDGE,"E982"),sQuery(id+"F3.wireOp",EDGE,"E983"),sQuery(id+"F3.wireOp",EDGE,"E984"),sQuery(id+"F3.wireOp",EDGE,"E985"),sQuery(id+"F3.wireOp",EDGE,"E986"),sQuery(id+"F3.wireOp",EDGE,"E987"),sQuery(id+"F3.wireOp",EDGE,"E988"),sQuery(id+"F3.wireOp",EDGE,"E989"),sQuery(id+"F3.wireOp",EDGE,"E990"),sQuery(id+"F3.wireOp",EDGE,"E991"),sQuery(id+"F3.wireOp",EDGE,"E992"),sQuery(id+"F3.wireOp",EDGE,"E993"),sQuery(id+"F3.wireOp",EDGE,"E994"),sQuery(id+"F3.wireOp",EDGE,"E995"),sQuery(id+"F3.wireOp",EDGE,"E996"),sQuery(id+"F3.wireOp",EDGE,"E997"),sQuery(id+"F3.wireOp",EDGE,"E998"),sQuery(id+"F3.wireOp",EDGE,"E999"),sQuery(id+"F3.wireOp",EDGE,"E1000"),sQuery(id+"F3.wireOp",EDGE,"E1001"),sQuery(id+"F3.wireOp",EDGE,"E1002"),sQuery(id+"F3.wireOp",EDGE,"E1003"),sQuery(id+"F3.wireOp",EDGE,"E1004"),sQuery(id+"F3.wireOp",EDGE,"E1005"),sQuery(id+"F3.wireOp",EDGE,"E1006"),sQuery(id+"F3.wireOp",EDGE,"E1007"),sQuery(id+"F3.wireOp",EDGE,"E1008"),sQuery(id+"F3.wireOp",EDGE,"E1009"),sQuery(id+"F3.wireOp",EDGE,"E1010"),sQuery(id+"F3.wireOp",EDGE,"E1011"),sQuery(id+"F3.wireOp",EDGE,"E1012"),sQuery(id+"F3.wireOp",EDGE,"E1013"),sQuery(id+"F3.wireOp",EDGE,"E1014"),sQuery(id+"F3.wireOp",EDGE,"E1015"),sQuery(id+"F3.wireOp",EDGE,"E1016"),sQuery(id+"F3.wireOp",EDGE,"E1017"),sQuery(id+"F3.wireOp",EDGE,"E1018"),sQuery(id+"F3.wireOp",EDGE,"E1019"),sQuery(id+"F3.wireOp",EDGE,"E1020"),sQuery(id+"F3.wireOp",EDGE,"E1021"),sQuery(id+"F3.wireOp",EDGE,"E1022"),sQuery(id+"F3.wireOp",EDGE,"E1023"),sQuery(id+"F3.wireOp",EDGE,"E1024"),sQuery(id+"F3.wireOp",EDGE,"E1025"),sQuery(id+"F3.wireOp",EDGE,"E1026"),sQuery(id+"F3.wireOp",EDGE,"E1027"),sQuery(id+"F3.wireOp",EDGE,"E1028"),sQuery(id+"F3.wireOp",EDGE,"E1029"),sQuery(id+"F3.wireOp",EDGE,"E1030"),sQuery(id+"F3.wireOp",EDGE,"E1031"),sQuery(id+"F3.wireOp",EDGE,"E1032"),sQuery(id+"F3.wireOp",EDGE,"E1033"),sQuery(id+"F3.wireOp",EDGE,"E1034"),sQuery(id+"F3.wireOp",EDGE,"E1035"),sQuery(id+"F3.wireOp",EDGE,"E1036"),sQuery(id+"F3.wireOp",EDGE,"E1037"),sQuery(id+"F3.wireOp",EDGE,"E1038"),sQuery(id+"F3.wireOp",EDGE,"E1039"),sQuery(id+"F3.wireOp",EDGE,"E1040"),sQuery(id+"F3.wireOp",EDGE,"E1041"),sQuery(id+"F3.wireOp",EDGE,"E1042"),sQuery(id+"F3.wireOp",EDGE,"E1043"),sQuery(id+"F3.wireOp",EDGE,"E1044"),sQuery(id+"F3.wireOp",EDGE,"E1045"),sQuery(id+"F3.wireOp",EDGE,"E1046"),sQuery(id+"F3.wireOp",EDGE,"E1047"),sQuery(id+"F3.wireOp",EDGE,"E1048"),sQuery(id+"F3.wireOp",EDGE,"E1049"),sQuery(id+"F3.wireOp",EDGE,"E1050"),sQuery(id+"F3.wireOp",EDGE,"E1051"),sQuery(id+"F3.wireOp",EDGE,"E1052"),sQuery(id+"F3.wireOp",EDGE,"E1053"),sQuery(id+"F3.wireOp",EDGE,"E1054"),sQuery(id+"F3.wireOp",EDGE,"E1055"),sQuery(id+"F3.wireOp",EDGE,"E1056"),sQuery(id+"F3.wireOp",EDGE,"E1057"),sQuery(id+"F3.wireOp",EDGE,"E1058"),sQuery(id+"F3.wireOp",EDGE,"E1059"),sQuery(id+"F3.wireOp",EDGE,"E1060"),sQuery(id+"F3.wireOp",EDGE,"E1061"),sQuery(id+"F3.wireOp",EDGE,"E1062"),sQuery(id+"F3.wireOp",EDGE,"E1063"),sQuery(id+"F3.wireOp",EDGE,"E1064"),sQuery(id+"F3.wireOp",EDGE,"E1065"),sQuery(id+"F3.wireOp",EDGE,"E1066"),sQuery(id+"F3.wireOp",EDGE,"E1067"),sQuery(id+"F3.wireOp",EDGE,"E1068"),sQuery(id+"F3.wireOp",EDGE,"E1069"),sQuery(id+"F3.wireOp",EDGE,"E1070"),sQuery(id+"F3.wireOp",EDGE,"E1071"),sQuery(id+"F3.wireOp",EDGE,"E1072"),sQuery(id+"F3.wireOp",EDGE,"E1073"),sQuery(id+"F3.wireOp",EDGE,"E1074"),sQuery(id+"F3.wireOp",EDGE,"E1075"),sQuery(id+"F3.wireOp",EDGE,"E1076"),sQuery(id+"F3.wireOp",EDGE,"E1077"),sQuery(id+"F3.wireOp",EDGE,"E1078"),sQuery(id+"F3.wireOp",EDGE,"E1079"),sQuery(id+"F3.wireOp",EDGE,"E1080"),sQuery(id+"F3.wireOp",EDGE,"E1081"),sQuery(id+"F3.wireOp",EDGE,"E1082"),sQuery(id+"F3.wireOp",EDGE,"E1083"),sQuery(id+"F3.wireOp",EDGE,"E1084"),sQuery(id+"F3.wireOp",EDGE,"E1085"),sQuery(id+"F3.wireOp",EDGE,"E1086"),sQuery(id+"F3.wireOp",EDGE,"E1087"),sQuery(id+"F3.wireOp",EDGE,"E1088"),sQuery(id+"F3.wireOp",EDGE,"E1089"),sQuery(id+"F3.wireOp",EDGE,"E1090"),sQuery(id+"F3.wireOp",EDGE,"E1091"),sQuery(id+"F3.wireOp",EDGE,"E1092"),sQuery(id+"F3.wireOp",EDGE,"E1093"),sQuery(id+"F3.wireOp",EDGE,"E1094"),sQuery(id+"F3.wireOp",EDGE,"E1095"),sQuery(id+"F3.wireOp",EDGE,"E1096"),sQuery(id+"F3.wireOp",EDGE,"E1097"),sQuery(id+"F3.wireOp",EDGE,"E1098"),sQuery(id+"F3.wireOp",EDGE,"E1099"),sQuery(id+"F3.wireOp",EDGE,"E1100"),sQuery(id+"F3.wireOp",EDGE,"E1101"),sQuery(id+"F3.wireOp",EDGE,"E1102"),sQuery(id+"F3.wireOp",EDGE,"E1103"),sQuery(id+"F3.wireOp",EDGE,"E1104"),sQuery(id+"F3.wireOp",EDGE,"E1105"),sQuery(id+"F3.wireOp",EDGE,"E1106"),sQuery(id+"F3.wireOp",EDGE,"E1107"),sQuery(id+"F3.wireOp",EDGE,"E1108"),sQuery(id+"F3.wireOp",EDGE,"E1109"),sQuery(id+"F3.wireOp",EDGE,"E1110"),sQuery(id+"F3.wireOp",EDGE,"E1111"),sQuery(id+"F3.wireOp",EDGE,"E1112"),sQuery(id+"F3.wireOp",EDGE,"E1113"),sQuery(id+"F3.wireOp",EDGE,"E1114"),sQuery(id+"F3.wireOp",EDGE,"E1115"),sQuery(id+"F3.wireOp",EDGE,"E1116"),sQuery(id+"F3.wireOp",EDGE,"E1117"),sQuery(id+"F3.wireOp",EDGE,"E1118"),sQuery(id+"F3.wireOp",EDGE,"E1119"),sQuery(id+"F3.wireOp",EDGE,"E1120"),sQuery(id+"F3.wireOp",EDGE,"E1121"),sQuery(id+"F3.wireOp",EDGE,"E1122"),sQuery(id+"F3.wireOp",EDGE,"E1123"),sQuery(id+"F3.wireOp",EDGE,"E1124"),sQuery(id+"F3.wireOp",EDGE,"E1125"),sQuery(id+"F3.wireOp",EDGE,"E1126"),sQuery(id+"F3.wireOp",EDGE,"E1127"),sQuery(id+"F3.wireOp",EDGE,"E1128"),sQuery(id+"F3.wireOp",EDGE,"E1129"),sQuery(id+"F3.wireOp",EDGE,"E1130"),sQuery(id+"F3.wireOp",EDGE,"E1131"),sQuery(id+"F3.wireOp",EDGE,"E1132"),sQuery(id+"F3.wireOp",EDGE,"E1133"),sQuery(id+"F3.wireOp",EDGE,"E1134"),sQuery(id+"F3.wireOp",EDGE,"E1135"),sQuery(id+"F3.wireOp",EDGE,"E1136"),sQuery(id+"F3.wireOp",EDGE,"E1137"),sQuery(id+"F3.wireOp",EDGE,"E1138"),sQuery(id+"F3.wireOp",EDGE,"E1139"),sQuery(id+"F3.wireOp",EDGE,"E1140"),sQuery(id+"F3.wireOp",EDGE,"E1141"),sQuery(id+"F3.wireOp",EDGE,"E1142"),sQuery(id+"F3.wireOp",EDGE,"E1143"),sQuery(id+"F3.wireOp",EDGE,"E1144"),sQuery(id+"F3.wireOp",EDGE,"E1145"),sQuery(id+"F3.wireOp",EDGE,"E1146"),sQuery(id+"F3.wireOp",EDGE,"E1147"),sQuery(id+"F3.wireOp",EDGE,"E1148"),sQuery(id+"F3.wireOp",EDGE,"E1149"),sQuery(id+"F3.wireOp",EDGE,"E1150"),sQuery(id+"F3.wireOp",EDGE,"E1151"),sQuery(id+"F3.wireOp",EDGE,"E1152"),sQuery(id+"F3.wireOp",EDGE,"E1153"),sQuery(id+"F3.wireOp",EDGE,"E1154"),sQuery(id+"F3.wireOp",EDGE,"E1155"),sQuery(id+"F3.wireOp",EDGE,"E1156"),sQuery(id+"F3.wireOp",EDGE,"E1157"),sQuery(id+"F3.wireOp",EDGE,"E1158"),sQuery(id+"F3.wireOp",EDGE,"E1159"),sQuery(id+"F3.wireOp",EDGE,"E1160"),sQuery(id+"F3.wireOp",EDGE,"E1161"),sQuery(id+"F3.wireOp",EDGE,"E1162"),sQuery(id+"F3.wireOp",EDGE,"E1163"),sQuery(id+"F3.wireOp",EDGE,"E1164"),sQuery(id+"F3.wireOp",EDGE,"E1165"),sQuery(id+"F3.wireOp",EDGE,"E1166"),sQuery(id+"F3.wireOp",EDGE,"E1167"),sQuery(id+"F3.wireOp",EDGE,"E1168"),sQuery(id+"F3.wireOp",EDGE,"E1169"),sQuery(id+"F3.wireOp",EDGE,"E1170"),sQuery(id+"F3.wireOp",EDGE,"E1171"),sQuery(id+"F3.wireOp",EDGE,"E1172"),sQuery(id+"F3.wireOp",EDGE,"E1173"),sQuery(id+"F3.wireOp",EDGE,"E1174"),sQuery(id+"F3.wireOp",EDGE,"E1175"),sQuery(id+"F3.wireOp",EDGE,"E1176"),sQuery(id+"F3.wireOp",EDGE,"E1177"),sQuery(id+"F3.wireOp",EDGE,"E1178"),sQuery(id+"F3.wireOp",EDGE,"E1179"),sQuery(id+"F3.wireOp",EDGE,"E1180"),sQuery(id+"F3.wireOp",EDGE,"E1181"),sQuery(id+"F3.wireOp",EDGE,"E1182"),sQuery(id+"F3.wireOp",EDGE,"E1183"),sQuery(id+"F3.wireOp",EDGE,"E1184"),sQuery(id+"F3.wireOp",EDGE,"E1185"),sQuery(id+"F3.wireOp",EDGE,"E1186"),sQuery(id+"F3.wireOp",EDGE,"E1187"),sQuery(id+"F3.wireOp",EDGE,"E1188"),sQuery(id+"F3.wireOp",EDGE,"E1189"),sQuery(id+"F3.wireOp",EDGE,"E1190"),sQuery(id+"F3.wireOp",EDGE,"E1191"),sQuery(id+"F3.wireOp",EDGE,"E1192"),sQuery(id+"F3.wireOp",EDGE,"E1193"),sQuery(id+"F3.wireOp",EDGE,"E1194"),sQuery(id+"F3.wireOp",EDGE,"E1195"),sQuery(id+"F3.wireOp",EDGE,"E1196"),sQuery(id+"F3.wireOp",EDGE,"E1197"),sQuery(id+"F3.wireOp",EDGE,"E1198"),sQuery(id+"F3.wireOp",EDGE,"E1199"),sQuery(id+"F3.wireOp",EDGE,"E1200"),sQuery(id+"F3.wireOp",EDGE,"E1201"),sQuery(id+"F3.wireOp",EDGE,"E1202"),sQuery(id+"F3.wireOp",EDGE,"E1203"),sQuery(id+"F3.wireOp",EDGE,"E1204"),sQuery(id+"F3.wireOp",EDGE,"E1205"),sQuery(id+"F3.wireOp",EDGE,"E1206"),sQuery(id+"F3.wireOp",EDGE,"E1207"),sQuery(id+"F3.wireOp",EDGE,"E1208"),sQuery(id+"F3.wireOp",EDGE,"E1209"),sQuery(id+"F3.wireOp",EDGE,"E1210"),sQuery(id+"F3.wireOp",EDGE,"E1211"),sQuery(id+"F3.wireOp",EDGE,"E1212"),sQuery(id+"F3.wireOp",EDGE,"E1213"),sQuery(id+"F3.wireOp",EDGE,"E1214"),sQuery(id+"F3.wireOp",EDGE,"E1215"),sQuery(id+"F3.wireOp",EDGE,"E1216"),sQuery(id+"F3.wireOp",EDGE,"E1217"),sQuery(id+"F3.wireOp",EDGE,"E1218"),sQuery(id+"F3.wireOp",EDGE,"E1219"),sQuery(id+"F3.wireOp",EDGE,"E1220"),sQuery(id+"F3.wireOp",EDGE,"E1221"),sQuery(id+"F3.wireOp",EDGE,"E1222"),sQuery(id+"F3.wireOp",EDGE,"E1223"),sQuery(id+"F3.wireOp",EDGE,"E1224"),sQuery(id+"F3.wireOp",EDGE,"E1225"),sQuery(id+"F3.wireOp",EDGE,"E1226"),sQuery(id+"F3.wireOp",EDGE,"E1227"),sQuery(id+"F3.wireOp",EDGE,"E1228"),sQuery(id+"F3.wireOp",EDGE,"E1229"),sQuery(id+"F3.wireOp",EDGE,"E1230"),sQuery(id+"F3.wireOp",EDGE,"E1231"),sQuery(id+"F3.wireOp",EDGE,"E1232"),sQuery(id+"F3.wireOp",EDGE,"E1233"),sQuery(id+"F3.wireOp",EDGE,"E1234"),sQuery(id+"F3.wireOp",EDGE,"E1235"),sQuery(id+"F3.wireOp",EDGE,"E1236"),sQuery(id+"F3.wireOp",EDGE,"E1237"),sQuery(id+"F3.wireOp",EDGE,"E1238"),sQuery(id+"F3.wireOp",EDGE,"E1239"),sQuery(id+"F3.wireOp",EDGE,"E1240"),sQuery(id+"F3.wireOp",EDGE,"E1241"),sQuery(id+"F3.wireOp",EDGE,"E1242"),sQuery(id+"F3.wireOp",EDGE,"E1243"),sQuery(id+"F3.wireOp",EDGE,"E1244"),sQuery(id+"F3.wireOp",EDGE,"E1245"),sQuery(id+"F3.wireOp",EDGE,"E1246"),sQuery(id+"F3.wireOp",EDGE,"E1247"),sQuery(id+"F3.wireOp",EDGE,"E1248"),sQuery(id+"F3.wireOp",EDGE,"E1249"),sQuery(id+"F3.wireOp",EDGE,"E1250"),sQuery(id+"F3.wireOp",EDGE,"E1251"),sQuery(id+"F3.wireOp",EDGE,"E1252"),sQuery(id+"F3.wireOp",EDGE,"E1253"),sQuery(id+"F3.wireOp",EDGE,"E1254"),sQuery(id+"F3.wireOp",EDGE,"E1255"),sQuery(id+"F3.wireOp",EDGE,"E1256"),sQuery(id+"F3.wireOp",EDGE,"E1257"),sQuery(id+"F3.wireOp",EDGE,"E1258"),sQuery(id+"F3.wireOp",EDGE,"E1259"),sQuery(id+"F3.wireOp",EDGE,"E1260"),sQuery(id+"F3.wireOp",EDGE,"E1261"),sQuery(id+"F3.wireOp",EDGE,"E1262"),sQuery(id+"F3.wireOp",EDGE,"E1263"),sQuery(id+"F3.wireOp",EDGE,"E1264"),sQuery(id+"F3.wireOp",EDGE,"E1265"),sQuery(id+"F3.wireOp",EDGE,"E1266"),sQuery(id+"F3.wireOp",EDGE,"E1267"),sQuery(id+"F3.wireOp",EDGE,"E1268"),sQuery(id+"F3.wireOp",EDGE,"E1269"),sQuery(id+"F3.wireOp",EDGE,"E1270"),sQuery(id+"F3.wireOp",EDGE,"E1271"),sQuery(id+"F3.wireOp",EDGE,"E1272"),sQuery(id+"F3.wireOp",EDGE,"E1273"),sQuery(id+"F3.wireOp",EDGE,"E1274"),sQuery(id+"F3.wireOp",EDGE,"E1275"),sQuery(id+"F3.wireOp",EDGE,"E1276"),sQuery(id+"F3.wireOp",EDGE,"E1277"),sQuery(id+"F3.wireOp",EDGE,"E1278"),sQuery(id+"F3.wireOp",EDGE,"E1279"),sQuery(id+"F3.wireOp",EDGE,"E1280"),sQuery(id+"F3.wireOp",EDGE,"E1281"),sQuery(id+"F3.wireOp",EDGE,"E1282"),sQuery(id+"F3.wireOp",EDGE,"E1283"),sQuery(id+"F3.wireOp",EDGE,"E1284"),sQuery(id+"F3.wireOp",EDGE,"E1285"),sQuery(id+"F3.wireOp",EDGE,"E1286"),sQuery(id+"F3.wireOp",EDGE,"E1287"),sQuery(id+"F3.wireOp",EDGE,"E1288"),sQuery(id+"F3.wireOp",EDGE,"E1289"),sQuery(id+"F3.wireOp",EDGE,"E1290"),sQuery(id+"F3.wireOp",EDGE,"E1291"),sQuery(id+"F3.wireOp",EDGE,"E1292"),sQuery(id+"F3.wireOp",EDGE,"E1293"),sQuery(id+"F3.wireOp",EDGE,"E1294"),sQuery(id+"F3.wireOp",EDGE,"E1295"),sQuery(id+"F3.wireOp",EDGE,"E1296"),sQuery(id+"F3.wireOp",EDGE,"E1297"),sQuery(id+"F3.wireOp",EDGE,"E1298"),sQuery(id+"F3.wireOp",EDGE,"E1299"),sQuery(id+"F3.wireOp",EDGE,"E1300"),sQuery(id+"F3.wireOp",EDGE,"E1301"),sQuery(id+"F3.wireOp",EDGE,"E1302"),sQuery(id+"F3.wireOp",EDGE,"E1303"),sQuery(id+"F3.wireOp",EDGE,"E1304"),sQuery(id+"F3.wireOp",EDGE,"E1305"),sQuery(id+"F3.wireOp",EDGE,"E1306"),sQuery(id+"F3.wireOp",EDGE,"E1307"),sQuery(id+"F3.wireOp",EDGE,"E1308"),sQuery(id+"F3.wireOp",EDGE,"E1309"),sQuery(id+"F3.wireOp",EDGE,"E1310"),sQuery(id+"F3.wireOp",EDGE,"E1311"),sQuery(id+"F3.wireOp",EDGE,"E1312"),sQuery(id+"F3.wireOp",EDGE,"E1313"),sQuery(id+"F3.wireOp",EDGE,"E1314"),sQuery(id+"F3.wireOp",EDGE,"E1315"),sQuery(id+"F3.wireOp",EDGE,"E1316"),sQuery(id+"F3.wireOp",EDGE,"E1317"),sQuery(id+"F3.wireOp",EDGE,"E1318"),sQuery(id+"F3.wireOp",EDGE,"E1319"),sQuery(id+"F3.wireOp",EDGE,"E1320"),sQuery(id+"F3.wireOp",EDGE,"E1321"),sQuery(id+"F3.wireOp",EDGE,"E1322"),sQuery(id+"F3.wireOp",EDGE,"E1323"),sQuery(id+"F3.wireOp",EDGE,"E1324"),sQuery(id+"F3.wireOp",EDGE,"E1325"),sQuery(id+"F3.wireOp",EDGE,"E1326"),sQuery(id+"F3.wireOp",EDGE,"E1327"),sQuery(id+"F3.wireOp",EDGE,"E1328"),sQuery(id+"F3.wireOp",EDGE,"E1329"),sQuery(id+"F3.wireOp",EDGE,"E1330"),sQuery(id+"F3.wireOp",EDGE,"E1331"),sQuery(id+"F3.wireOp",EDGE,"E1332"),sQuery(id+"F3.wireOp",EDGE,"E1333"),sQuery(id+"F3.wireOp",EDGE,"E1334"),sQuery(id+"F3.wireOp",EDGE,"E1335"),sQuery(id+"F3.wireOp",EDGE,"E1336"),sQuery(id+"F3.wireOp",EDGE,"E1337"),sQuery(id+"F3.wireOp",EDGE,"E1338"),sQuery(id+"F3.wireOp",EDGE,"E1339"),sQuery(id+"F3.wireOp",EDGE,"E1340"),sQuery(id+"F3.wireOp",EDGE,"E1341"),sQuery(id+"F3.wireOp",EDGE,"E1342"),sQuery(id+"F3.wireOp",EDGE,"E1343"),sQuery(id+"F3.wireOp",EDGE,"E1344"),sQuery(id+"F3.wireOp",EDGE,"E1345"),sQuery(id+"F3.wireOp",EDGE,"E1346"),sQuery(id+"F3.wireOp",EDGE,"E1347"),sQuery(id+"F3.wireOp",EDGE,"E1348"),sQuery(id+"F3.wireOp",EDGE,"E1349"),sQuery(id+"F3.wireOp",EDGE,"E1350"),sQuery(id+"F3.wireOp",EDGE,"E1351"),sQuery(id+"F3.wireOp",EDGE,"E1352"),sQuery(id+"F3.wireOp",EDGE,"E1353"),sQuery(id+"F3.wireOp",EDGE,"E1354"),sQuery(id+"F3.wireOp",EDGE,"E1355"),sQuery(id+"F3.wireOp",EDGE,"E1356"),sQuery(id+"F3.wireOp",EDGE,"E1357"),sQuery(id+"F3.wireOp",EDGE,"E1358"),sQuery(id+"F3.wireOp",EDGE,"E1359"),sQuery(id+"F3.wireOp",EDGE,"E1360"),sQuery(id+"F3.wireOp",EDGE,"E1361"),sQuery(id+"F3.wireOp",EDGE,"E1362"),sQuery(id+"F3.wireOp",EDGE,"E1363"),sQuery(id+"F3.wireOp",EDGE,"E1364"),sQuery(id+"F3.wireOp",EDGE,"E1365"),sQuery(id+"F3.wireOp",EDGE,"E1366"),sQuery(id+"F3.wireOp",EDGE,"E1367"),sQuery(id+"F3.wireOp",EDGE,"E1368"),sQuery(id+"F3.wireOp",EDGE,"E1369"),sQuery(id+"F3.wireOp",EDGE,"E1370"),sQuery(id+"F3.wireOp",EDGE,"E1371"),sQuery(id+"F3.wireOp",EDGE,"E1372"),sQuery(id+"F3.wireOp",EDGE,"E1373"),sQuery(id+"F3.wireOp",EDGE,"E1374"),sQuery(id+"F3.wireOp",EDGE,"E1375"),sQuery(id+"F3.wireOp",EDGE,"E1376"),sQuery(id+"F3.wireOp",EDGE,"E1377"),sQuery(id+"F3.wireOp",EDGE,"E1378"),sQuery(id+"F3.wireOp",EDGE,"E1379"),sQuery(id+"F3.wireOp",EDGE,"E1380"),sQuery(id+"F3.wireOp",EDGE,"E1381"),sQuery(id+"F3.wireOp",EDGE,"E1382"),sQuery(id+"F3.wireOp",EDGE,"E1383"),sQuery(id+"F3.wireOp",EDGE,"E1384"),sQuery(id+"F3.wireOp",EDGE,"E1385"),sQuery(id+"F3.wireOp",EDGE,"E1386"),sQuery(id+"F3.wireOp",EDGE,"E1387"),sQuery(id+"F3.wireOp",EDGE,"E1388"),sQuery(id+"F3.wireOp",EDGE,"E1389"),sQuery(id+"F3.wireOp",EDGE,"E1390"),sQuery(id+"F3.wireOp",EDGE,"E1391"),sQuery(id+"F3.wireOp",EDGE,"E1392"),sQuery(id+"F3.wireOp",EDGE,"E1393"),sQuery(id+"F3.wireOp",EDGE,"E1394"),sQuery(id+"F3.wireOp",EDGE,"E1395"),sQuery(id+"F3.wireOp",EDGE,"E1396"),sQuery(id+"F3.wireOp",EDGE,"E1397"),sQuery(id+"F3.wireOp",EDGE,"E1398"),sQuery(id+"F3.wireOp",EDGE,"E1399"),sQuery(id+"F3.wireOp",EDGE,"E1400"),sQuery(id+"F3.wireOp",EDGE,"E1401"),sQuery(id+"F3.wireOp",EDGE,"E1402"),sQuery(id+"F3.wireOp",EDGE,"E1403"),sQuery(id+"F3.wireOp",EDGE,"E1404"),sQuery(id+"F3.wireOp",EDGE,"E1405"),sQuery(id+"F3.wireOp",EDGE,"E1406"),sQuery(id+"F3.wireOp",EDGE,"E1407"),sQuery(id+"F3.wireOp",EDGE,"E1408"),sQuery(id+"F3.wireOp",EDGE,"E1409"),sQuery(id+"F3.wireOp",EDGE,"E1410"),sQuery(id+"F3.wireOp",EDGE,"E1411"),sQuery(id+"F3.wireOp",EDGE,"E1412"),sQuery(id+"F3.wireOp",EDGE,"E1413"),sQuery(id+"F3.wireOp",EDGE,"E1414"),sQuery(id+"F3.wireOp",EDGE,"E1415"),sQuery(id+"F3.wireOp",EDGE,"E1416"),sQuery(id+"F3.wireOp",EDGE,"E1417"),sQuery(id+"F3.wireOp",EDGE,"E1418"),sQuery(id+"F3.wireOp",EDGE,"E1419"),sQuery(id+"F3.wireOp",EDGE,"E1420"),sQuery(id+"F3.wireOp",EDGE,"E1421"),sQuery(id+"F3.wireOp",EDGE,"E1422"),sQuery(id+"F3.wireOp",EDGE,"E1423"),sQuery(id+"F3.wireOp",EDGE,"E1424"),sQuery(id+"F3.wireOp",EDGE,"E1425"),sQuery(id+"F3.wireOp",EDGE,"E1426"),sQuery(id+"F3.wireOp",EDGE,"E1427"),sQuery(id+"F3.wireOp",EDGE,"E1428"),sQuery(id+"F3.wireOp",EDGE,"E1429"),sQuery(id+"F3.wireOp",EDGE,"E1430"),sQuery(id+"F3.wireOp",EDGE,"E1431"),sQuery(id+"F3.wireOp",EDGE,"E1432"),sQuery(id+"F3.wireOp",EDGE,"E1433"),sQuery(id+"F3.wireOp",EDGE,"E1434"),sQuery(id+"F3.wireOp",EDGE,"E1435"),sQuery(id+"F3.wireOp",EDGE,"E1436"),sQuery(id+"F3.wireOp",EDGE,"E1437"),sQuery(id+"F3.wireOp",EDGE,"E1438"),sQuery(id+"F3.wireOp",EDGE,"E1439"),sQuery(id+"F3.wireOp",EDGE,"E1440"),sQuery(id+"F3.wireOp",EDGE,"E1441"),sQuery(id+"F3.wireOp",EDGE,"E1442"),sQuery(id+"F3.wireOp",EDGE,"E1443"),sQuery(id+"F3.wireOp",EDGE,"E1444"),sQuery(id+"F3.wireOp",EDGE,"E1445"),sQuery(id+"F3.wireOp",EDGE,"E1446"),sQuery(id+"F3.wireOp",EDGE,"E1447"),sQuery(id+"F3.wireOp",EDGE,"E1448"),sQuery(id+"F3.wireOp",EDGE,"E1449"),sQuery(id+"F3.wireOp",EDGE,"E1450"),sQuery(id+"F3.wireOp",EDGE,"E1451"),sQuery(id+"F3.wireOp",EDGE,"E1452"),sQuery(id+"F3.wireOp",EDGE,"E1453"),sQuery(id+"F3.wireOp",EDGE,"E1454"),sQuery(id+"F3.wireOp",EDGE,"E1455"),sQuery(id+"F3.wireOp",EDGE,"E1456"),sQuery(id+"F3.wireOp",EDGE,"E1457"),sQuery(id+"F3.wireOp",EDGE,"E1458"),sQuery(id+"F3.wireOp",EDGE,"E1459"),sQuery(id+"F3.wireOp",EDGE,"E1460"),sQuery(id+"F3.wireOp",EDGE,"E1461"),sQuery(id+"F3.wireOp",EDGE,"E1462"),sQuery(id+"F3.wireOp",EDGE,"E1463"),sQuery(id+"F3.wireOp",EDGE,"E1464"),sQuery(id+"F3.wireOp",EDGE,"E1465"),sQuery(id+"F3.wireOp",EDGE,"E1466"),sQuery(id+"F3.wireOp",EDGE,"E1467"),sQuery(id+"F3.wireOp",EDGE,"E1468"),sQuery(id+"F3.wireOp",EDGE,"E1469"),sQuery(id+"F3.wireOp",EDGE,"E1470"),sQuery(id+"F3.wireOp",EDGE,"E1471"),sQuery(id+"F3.wireOp",EDGE,"E1472"),sQuery(id+"F3.wireOp",EDGE,"E1473"),sQuery(id+"F3.wireOp",EDGE,"E1474"),sQuery(id+"F3.wireOp",EDGE,"E1475"),sQuery(id+"F3.wireOp",EDGE,"E1476"),sQuery(id+"F3.wireOp",EDGE,"E1477"),sQuery(id+"F3.wireOp",EDGE,"E1478"),sQuery(id+"F3.wireOp",EDGE,"E1479"),sQuery(id+"F3.wireOp",EDGE,"E1480"),sQuery(id+"F3.wireOp",EDGE,"E1481"),sQuery(id+"F3.wireOp",EDGE,"E1482"),sQuery(id+"F3.wireOp",EDGE,"E1483"),sQuery(id+"F3.wireOp",EDGE,"E1484"),sQuery(id+"F3.wireOp",EDGE,"E1485"),sQuery(id+"F3.wireOp",EDGE,"E1486"),sQuery(id+"F3.wireOp",EDGE,"E1487"),sQuery(id+"F3.wireOp",EDGE,"E1488"),sQuery(id+"F3.wireOp",EDGE,"E1489"),sQuery(id+"F3.wireOp",EDGE,"E1490"),sQuery(id+"F3.wireOp",EDGE,"E1491"),sQuery(id+"F3.wireOp",EDGE,"E1492"),sQuery(id+"F3.wireOp",EDGE,"E1493"),sQuery(id+"F3.wireOp",EDGE,"E1494"),sQuery(id+"F3.wireOp",EDGE,"E1495"),sQuery(id+"F3.wireOp",EDGE,"E1496"),sQuery(id+"F3.wireOp",EDGE,"E1497"),sQuery(id+"F3.wireOp",EDGE,"E1498"),sQuery(id+"F3.wireOp",EDGE,"E1499"),sQuery(id+"F3.wireOp",EDGE,"E1500"),sQuery(id+"F3.wireOp",EDGE,"E1501"),sQuery(id+"F3.wireOp",EDGE,"E1502"),sQuery(id+"F3.wireOp",EDGE,"E1503"),sQuery(id+"F3.wireOp",EDGE,"E1504"),sQuery(id+"F3.wireOp",EDGE,"E1505"),sQuery(id+"F3.wireOp",EDGE,"E1506"),sQuery(id+"F3.wireOp",EDGE,"E1507"),sQuery(id+"F3.wireOp",EDGE,"E1508"),sQuery(id+"F3.wireOp",EDGE,"E1509"),sQuery(id+"F3.wireOp",EDGE,"E1510"),sQuery(id+"F3.wireOp",EDGE,"E1511"),sQuery(id+"F3.wireOp",EDGE,"E1512"),sQuery(id+"F3.wireOp",EDGE,"E1513"),sQuery(id+"F3.wireOp",EDGE,"E1514"),sQuery(id+"F3.wireOp",EDGE,"E1515"),sQuery(id+"F3.wireOp",EDGE,"E1516"),sQuery(id+"F3.wireOp",EDGE,"E1517"),sQuery(id+"F3.wireOp",EDGE,"E1518"),sQuery(id+"F3.wireOp",EDGE,"E1519"),sQuery(id+"F3.wireOp",EDGE,"E1520"),sQuery(id+"F3.wireOp",EDGE,"E1521"),sQuery(id+"F3.wireOp",EDGE,"E1522"),sQuery(id+"F3.wireOp",EDGE,"E1523"),sQuery(id+"F3.wireOp",EDGE,"E1524"),sQuery(id+"F3.wireOp",EDGE,"E1525"),sQuery(id+"F3.wireOp",EDGE,"E1526"),sQuery(id+"F3.wireOp",EDGE,"E1527"),sQuery(id+"F3.wireOp",EDGE,"E1528"),sQuery(id+"F3.wireOp",EDGE,"E1529"),sQuery(id+"F3.wireOp",EDGE,"E1530"),sQuery(id+"F3.wireOp",EDGE,"E1531"),sQuery(id+"F3.wireOp",EDGE,"E1532"),sQuery(id+"F3.wireOp",EDGE,"E1533"),sQuery(id+"F3.wireOp",EDGE,"E1534"),sQuery(id+"F3.wireOp",EDGE,"E1535"),sQuery(id+"F3.wireOp",EDGE,"E1536"),sQuery(id+"F3.wireOp",EDGE,"E1537"),sQuery(id+"F3.wireOp",EDGE,"E1538"),sQuery(id+"F3.wireOp",EDGE,"E1539"),sQuery(id+"F3.wireOp",EDGE,"E1540"),sQuery(id+"F3.wireOp",EDGE,"E1541"),sQuery(id+"F3.wireOp",EDGE,"E1542"),sQuery(id+"F3.wireOp",EDGE,"E1543"),sQuery(id+"F3.wireOp",EDGE,"E1544"),sQuery(id+"F3.wireOp",EDGE,"E1545"),sQuery(id+"F3.wireOp",EDGE,"E1546"),sQuery(id+"F3.wireOp",EDGE,"E1547"),sQuery(id+"F3.wireOp",EDGE,"E1548"),sQuery(id+"F3.wireOp",EDGE,"E1549"),sQuery(id+"F3.wireOp",EDGE,"E1550"),sQuery(id+"F3.wireOp",EDGE,"E1551"),sQuery(id+"F3.wireOp",EDGE,"E1552"),sQuery(id+"F3.wireOp",EDGE,"E1553"),sQuery(id+"F3.wireOp",EDGE,"E1554"),sQuery(id+"F3.wireOp",EDGE,"E1555"),sQuery(id+"F3.wireOp",EDGE,"E1556"),sQuery(id+"F3.wireOp",EDGE,"E1557"),sQuery(id+"F3.wireOp",EDGE,"E1558"),sQuery(id+"F3.wireOp",EDGE,"E1559"),sQuery(id+"F3.wireOp",EDGE,"E1560"),sQuery(id+"F3.wireOp",EDGE,"E1561"),sQuery(id+"F3.wireOp",EDGE,"E1562"),sQuery(id+"F3.wireOp",EDGE,"E1563"),sQuery(id+"F3.wireOp",EDGE,"E1564"),sQuery(id+"F3.wireOp",EDGE,"E1565"),sQuery(id+"F3.wireOp",EDGE,"E1566"),sQuery(id+"F3.wireOp",EDGE,"E1567"),sQuery(id+"F3.wireOp",EDGE,"E1568"),sQuery(id+"F3.wireOp",EDGE,"E1569"),sQuery(id+"F3.wireOp",EDGE,"E1570"),sQuery(id+"F3.wireOp",EDGE,"E1571"),sQuery(id+"F3.wireOp",EDGE,"E1572"),sQuery(id+"F3.wireOp",EDGE,"E1573"),sQuery(id+"F3.wireOp",EDGE,"E1574"),sQuery(id+"F3.wireOp",EDGE,"E1575"),sQuery(id+"F3.wireOp",EDGE,"E1576"),sQuery(id+"F3.wireOp",EDGE,"E1577"),sQuery(id+"F3.wireOp",EDGE,"E1578"),sQuery(id+"F3.wireOp",EDGE,"E1579"),sQuery(id+"F3.wireOp",EDGE,"E1580"),sQuery(id+"F3.wireOp",EDGE,"E1581"),sQuery(id+"F3.wireOp",EDGE,"E1582"),sQuery(id+"F3.wireOp",EDGE,"E1583"),sQuery(id+"F3.wireOp",EDGE,"E1584"),sQuery(id+"F3.wireOp",EDGE,"E1585"),sQuery(id+"F3.wireOp",EDGE,"E1586"),sQuery(id+"F3.wireOp",EDGE,"E1587"),sQuery(id+"F3.wireOp",EDGE,"E1588"),sQuery(id+"F3.wireOp",EDGE,"E1589"),sQuery(id+"F3.wireOp",EDGE,"E1590"),sQuery(id+"F3.wireOp",EDGE,"E1591"),sQuery(id+"F3.wireOp",EDGE,"E1592"),sQuery(id+"F3.wireOp",EDGE,"E1593"),sQuery(id+"F3.wireOp",EDGE,"E1594"),sQuery(id+"F3.wireOp",EDGE,"E1595"),sQuery(id+"F3.wireOp",EDGE,"E1596"),sQuery(id+"F3.wireOp",EDGE,"E1597"),sQuery(id+"F3.wireOp",EDGE,"E1598"),sQuery(id+"F3.wireOp",EDGE,"E1599"),sQuery(id+"F3.wireOp",EDGE,"E1600"),sQuery(id+"F3.wireOp",EDGE,"E1601"),sQuery(id+"F3.wireOp",EDGE,"E1602"),sQuery(id+"F3.wireOp",EDGE,"E1603"),sQuery(id+"F3.wireOp",EDGE,"E1604"),sQuery(id+"F3.wireOp",EDGE,"E1605"),sQuery(id+"F3.wireOp",EDGE,"E1606"),sQuery(id+"F3.wireOp",EDGE,"E1607"),sQuery(id+"F3.wireOp",EDGE,"E1608"),sQuery(id+"F3.wireOp",EDGE,"E1609"),sQuery(id+"F3.wireOp",EDGE,"E1610"),sQuery(id+"F3.wireOp",EDGE,"E1611"),sQuery(id+"F3.wireOp",EDGE,"E1612"),sQuery(id+"F3.wireOp",EDGE,"E1613"),sQuery(id+"F3.wireOp",EDGE,"E1614"),sQuery(id+"F3.wireOp",EDGE,"E1615"),sQuery(id+"F3.wireOp",EDGE,"E1616"),sQuery(id+"F3.wireOp",EDGE,"E1617"),sQuery(id+"F3.wireOp",EDGE,"E1618"),sQuery(id+"F3.wireOp",EDGE,"E1619"),sQuery(id+"F3.wireOp",EDGE,"E1620"),sQuery(id+"F3.wireOp",EDGE,"E1621"),sQuery(id+"F3.wireOp",EDGE,"E1622"),sQuery(id+"F3.wireOp",EDGE,"E1623"),sQuery(id+"F3.wireOp",EDGE,"E1624"),sQuery(id+"F3.wireOp",EDGE,"E1625"),sQuery(id+"F3.wireOp",EDGE,"E1626"),sQuery(id+"F3.wireOp",EDGE,"E1627"),sQuery(id+"F3.wireOp",EDGE,"E1628"),sQuery(id+"F3.wireOp",EDGE,"E1629"),sQuery(id+"F3.wireOp",EDGE,"E1630"),sQuery(id+"F3.wireOp",EDGE,"E1631"),sQuery(id+"F3.wireOp",EDGE,"E1632"),sQuery(id+"F3.wireOp",EDGE,"E1633"),sQuery(id+"F3.wireOp",EDGE,"E1634"),sQuery(id+"F3.wireOp",EDGE,"E1635"),sQuery(id+"F3.wireOp",EDGE,"E1636"),sQuery(id+"F3.wireOp",EDGE,"E1637"),sQuery(id+"F3.wireOp",EDGE,"E1638"),sQuery(id+"F3.wireOp",EDGE,"E1639"),sQuery(id+"F3.wireOp",EDGE,"E1640"),sQuery(id+"F3.wireOp",EDGE,"E1641"),sQuery(id+"F3.wireOp",EDGE,"E1642"),sQuery(id+"F3.wireOp",EDGE,"E1643"),sQuery(id+"F3.wireOp",EDGE,"E1644"),sQuery(id+"F3.wireOp",EDGE,"E1645"),sQuery(id+"F3.wireOp",EDGE,"E1646"),sQuery(id+"F3.wireOp",EDGE,"E1647"),sQuery(id+"F3.wireOp",EDGE,"E1648"),sQuery(id+"F3.wireOp",EDGE,"E1649"),sQuery(id+"F3.wireOp",EDGE,"E1650"),sQuery(id+"F3.wireOp",EDGE,"E1651"),sQuery(id+"F3.wireOp",EDGE,"E1652"),sQuery(id+"F3.wireOp",EDGE,"E1653"),sQuery(id+"F3.wireOp",EDGE,"E1654"),sQuery(id+"F3.wireOp",EDGE,"E1655"),sQuery(id+"F3.wireOp",EDGE,"E1656"),sQuery(id+"F3.wireOp",EDGE,"E1657"),sQuery(id+"F3.wireOp",EDGE,"E1658"),sQuery(id+"F3.wireOp",EDGE,"E1659"),sQuery(id+"F3.wireOp",EDGE,"E1660"),sQuery(id+"F3.wireOp",EDGE,"E1661"),sQuery(id+"F3.wireOp",EDGE,"E1662"),sQuery(id+"F3.wireOp",EDGE,"E1663"),sQuery(id+"F3.wireOp",EDGE,"E1664"),sQuery(id+"F3.wireOp",EDGE,"E1665"),sQuery(id+"F3.wireOp",EDGE,"E1666"),sQuery(id+"F3.wireOp",EDGE,"E1667"),sQuery(id+"F3.wireOp",EDGE,"E1668"),sQuery(id+"F3.wireOp",EDGE,"E1669"),sQuery(id+"F3.wireOp",EDGE,"E1670"),sQuery(id+"F3.wireOp",EDGE,"E1671"),sQuery(id+"F3.wireOp",EDGE,"E1672"),sQuery(id+"F3.wireOp",EDGE,"E1673"),sQuery(id+"F3.wireOp",EDGE,"E1674"),sQuery(id+"F3.wireOp",EDGE,"E1675"),sQuery(id+"F3.wireOp",EDGE,"E1676"),sQuery(id+"F3.wireOp",EDGE,"E1677"),sQuery(id+"F3.wireOp",EDGE,"E1678"),sQuery(id+"F3.wireOp",EDGE,"E1679"),sQuery(id+"F3.wireOp",EDGE,"E1680"),sQuery(id+"F3.wireOp",EDGE,"E1681"),sQuery(id+"F3.wireOp",EDGE,"E1682"),sQuery(id+"F3.wireOp",EDGE,"E1683"),sQuery(id+"F3.wireOp",EDGE,"E1684"),sQuery(id+"F3.wireOp",EDGE,"E1685"),sQuery(id+"F3.wireOp",EDGE,"E1686"),sQuery(id+"F3.wireOp",EDGE,"E1687"),sQuery(id+"F3.wireOp",EDGE,"E1688"),sQuery(id+"F3.wireOp",EDGE,"E1689"),sQuery(id+"F3.wireOp",EDGE,"E1690"),sQuery(id+"F3.wireOp",EDGE,"E1691"),sQuery(id+"F3.wireOp",EDGE,"E1692"),sQuery(id+"F3.wireOp",EDGE,"E1693"),sQuery(id+"F3.wireOp",EDGE,"E1694"),sQuery(id+"F3.wireOp",EDGE,"E1695"),sQuery(id+"F3.wireOp",EDGE,"E1696"),sQuery(id+"F3.wireOp",EDGE,"E1697"),sQuery(id+"F3.wireOp",EDGE,"E1698"),sQuery(id+"F3.wireOp",EDGE,"E1699"),sQuery(id+"F3.wireOp",EDGE,"E1700"),sQuery(id+"F3.wireOp",EDGE,"E1701"),sQuery(id+"F3.wireOp",EDGE,"E1702"),sQuery(id+"F3.wireOp",EDGE,"E1703"),sQuery(id+"F3.wireOp",EDGE,"E1704"),sQuery(id+"F3.wireOp",EDGE,"E1705"),sQuery(id+"F3.wireOp",EDGE,"E1706"),sQuery(id+"F3.wireOp",EDGE,"E1707"),sQuery(id+"F3.wireOp",EDGE,"E1708"),sQuery(id+"F3.wireOp",EDGE,"E1709"),sQuery(id+"F3.wireOp",EDGE,"E1710"),sQuery(id+"F3.wireOp",EDGE,"E1711"),sQuery(id+"F3.wireOp",EDGE,"E1712"),sQuery(id+"F3.wireOp",EDGE,"E1713"),sQuery(id+"F3.wireOp",EDGE,"E1714"),sQuery(id+"F3.wireOp",EDGE,"E1715"),sQuery(id+"F3.wireOp",EDGE,"E1716"),sQuery(id+"F3.wireOp",EDGE,"E1717"),sQuery(id+"F3.wireOp",EDGE,"E1718"),sQuery(id+"F3.wireOp",EDGE,"E1719"),sQuery(id+"F3.wireOp",EDGE,"E1720"),sQuery(id+"F3.wireOp",EDGE,"E1721"),sQuery(id+"F3.wireOp",EDGE,"E1722"),sQuery(id+"F3.wireOp",EDGE,"E1723"),sQuery(id+"F3.wireOp",EDGE,"E1724"),sQuery(id+"F3.wireOp",EDGE,"E1725"),sQuery(id+"F3.wireOp",EDGE,"E1726"),sQuery(id+"F3.wireOp",EDGE,"E1727"),sQuery(id+"F3.wireOp",EDGE,"E1728"),sQuery(id+"F3.wireOp",EDGE,"E1729"),sQuery(id+"F3.wireOp",EDGE,"E1730"),sQuery(id+"F3.wireOp",EDGE,"E1731"),sQuery(id+"F3.wireOp",EDGE,"E1732"),sQuery(id+"F3.wireOp",EDGE,"E1733"),sQuery(id+"F3.wireOp",EDGE,"E1734"),sQuery(id+"F3.wireOp",EDGE,"E1735"),sQuery(id+"F3.wireOp",EDGE,"E1736"),sQuery(id+"F3.wireOp",EDGE,"E1737"),sQuery(id+"F3.wireOp",EDGE,"E1738"),sQuery(id+"F3.wireOp",EDGE,"E1739"),sQuery(id+"F3.wireOp",EDGE,"E1740"),sQuery(id+"F3.wireOp",EDGE,"E1741"),sQuery(id+"F3.wireOp",EDGE,"E1742"),sQuery(id+"F3.wireOp",EDGE,"E1743"),sQuery(id+"F3.wireOp",EDGE,"E1744"),sQuery(id+"F3.wireOp",EDGE,"E1745"),sQuery(id+"F3.wireOp",EDGE,"E1746"),sQuery(id+"F3.wireOp",EDGE,"E1747"),sQuery(id+"F3.wireOp",EDGE,"E1748"),sQuery(id+"F3.wireOp",EDGE,"E1749"),sQuery(id+"F3.wireOp",EDGE,"E1750"),sQuery(id+"F3.wireOp",EDGE,"E1751"),sQuery(id+"F3.wireOp",EDGE,"E1752"),sQuery(id+"F3.wireOp",EDGE,"E1753"),sQuery(id+"F3.wireOp",EDGE,"E1754"),sQuery(id+"F3.wireOp",EDGE,"E1755"),sQuery(id+"F3.wireOp",EDGE,"E1756"),sQuery(id+"F3.wireOp",EDGE,"E1757"),sQuery(id+"F3.wireOp",EDGE,"E1758"),sQuery(id+"F3.wireOp",EDGE,"E1759"),sQuery(id+"F3.wireOp",EDGE,"E1760"),sQuery(id+"F3.wireOp",EDGE,"E1761"),sQuery(id+"F3.wireOp",EDGE,"E1762"),sQuery(id+"F3.wireOp",EDGE,"E1763"),sQuery(id+"F3.wireOp",EDGE,"E1764"),sQuery(id+"F3.wireOp",EDGE,"E1765"),sQuery(id+"F3.wireOp",EDGE,"E1766"),sQuery(id+"F3.wireOp",EDGE,"E1767"),sQuery(id+"F3.wireOp",EDGE,"E1768"),sQuery(id+"F3.wireOp",EDGE,"E1769"),sQuery(id+"F3.wireOp",EDGE,"E1770"),sQuery(id+"F3.wireOp",EDGE,"E1771"),sQuery(id+"F3.wireOp",EDGE,"E1772"),sQuery(id+"F3.wireOp",EDGE,"E1773"),sQuery(id+"F3.wireOp",EDGE,"E1774"),sQuery(id+"F3.wireOp",EDGE,"E1775"),sQuery(id+"F3.wireOp",EDGE,"E1776"),sQuery(id+"F3.wireOp",EDGE,"E1777"),sQuery(id+"F3.wireOp",EDGE,"E1778"),sQuery(id+"F3.wireOp",EDGE,"E1779"),sQuery(id+"F3.wireOp",EDGE,"E1780"),sQuery(id+"F3.wireOp",EDGE,"E1781"),sQuery(id+"F3.wireOp",EDGE,"E1782"),sQuery(id+"F3.wireOp",EDGE,"E1783"),sQuery(id+"F3.wireOp",EDGE,"E1784"),sQuery(id+"F3.wireOp",EDGE,"E1785"),sQuery(id+"F3.wireOp",EDGE,"E1786"),sQuery(id+"F3.wireOp",EDGE,"E1787"),sQuery(id+"F3.wireOp",EDGE,"E1788"),sQuery(id+"F3.wireOp",EDGE,"E1789"),sQuery(id+"F3.wireOp",EDGE,"E1790"),sQuery(id+"F3.wireOp",EDGE,"E1791"),sQuery(id+"F3.wireOp",EDGE,"E1792"),sQuery(id+"F3.wireOp",EDGE,"E1793"),sQuery(id+"F3.wireOp",EDGE,"E1794"),sQuery(id+"F3.wireOp",EDGE,"E1795"),sQuery(id+"F3.wireOp",EDGE,"E1796"),sQuery(id+"F3.wireOp",EDGE,"E1797"),sQuery(id+"F3.wireOp",EDGE,"E1798"),sQuery(id+"F3.wireOp",EDGE,"E1799"),sQuery(id+"F3.wireOp",EDGE,"E1800"),sQuery(id+"F3.wireOp",EDGE,"E1801"),sQuery(id+"F3.wireOp",EDGE,"E1802"),sQuery(id+"F3.wireOp",EDGE,"E1803"),sQuery(id+"F3.wireOp",EDGE,"E1824.0.0"),sQuery(id+"F3.wireOp",EDGE,"E1824.0.1"),sQuery(id+"F3.wireOp",EDGE,"E1824.0.2"),sQuery(id+"F3.wireOp",EDGE,"E1824.0.3"),sQuery(id+"F3.wireOp",EDGE,"E1824.0.4"),sQuery(id+"F3.wireOp",EDGE,"E1824.0.5"),sQuery(id+"F3.wireOp",EDGE,"E1824.0.6"),sQuery(id+"F3.wireOp",EDGE,"E1824.0.7"),sQuery(id+"F3.wireOp",EDGE,"E1824.0.8"),sQuery(id+"F3.wireOp",EDGE,"E1824.0.9"),sQuery(id+"F3.wireOp",EDGE,"E1824.0.10"),sQuery(id+"F3.wireOp",EDGE,"E1824.0.11"),sQuery(id+"F3.wireOp",EDGE,"E1824.0.12"),sQuery(id+"F3.wireOp",EDGE,"E1824.0.13"),sQuery(id+"F3.wireOp",EDGE,"E1824.0.14"),sQuery(id+"F3.wireOp",EDGE,"E1824.0.15"),sQuery(id+"F3.wireOp",EDGE,"E1824.0.16"),sQuery(id+"F3.wireOp",EDGE,"E1824.0.17"),sQuery(id+"F3.wireOp",EDGE,"E1824.0.18"),sQuery(id+"F3.wireOp",EDGE,"E1824.0.19"),sQuery(id+"F3.wireOp",EDGE,"E1824.0.20"),sQuery(id+"F3.wireOp",EDGE,"E1824.0.21"),sQuery(id+"F3.wireOp",EDGE,"E1824.0.22"),sQuery(id+"F3.wireOp",EDGE,"E1824.0.23"),sQuery(id+"F3.wireOp",EDGE,"E1824.0.24"),sQuery(id+"F3.wireOp",EDGE,"E1824.0.25"),sQuery(id+"F3.wireOp",EDGE,"E1824.0.26"),sQuery(id+"F3.wireOp",EDGE,"E1824.0.27"),sQuery(id+"F3.wireOp",EDGE,"E1824.0.28"),sQuery(id+"F3.wireOp",EDGE,"E1824.0.29"),sQuery(id+"F3.wireOp",EDGE,"E1824.0.30"),sQuery(id+"F3.wireOp",EDGE,"E1824.0.31"),sQuery(id+"F3.wireOp",EDGE,"E1824.0.32"),sQuery(id+"F3.wireOp",EDGE,"E1824.0.33"),sQuery(id+"F3.wireOp",EDGE,"E1824.0.34"),sQuery(id+"F3.wireOp",EDGE,"E1824.0.35"),sQuery(id+"F3.wireOp",EDGE,"E1824.0.36"),sQuery(id+"F3.wireOp",EDGE,"E1824.0.37"),sQuery(id+"F3.wireOp",EDGE,"E1824.0.38"),sQuery(id+"F3.wireOp",EDGE,"E1824.0.39"),sQuery(id+"F3.wireOp",EDGE,"E1824.0.40"),sQuery(id+"F3.wireOp",EDGE,"E1824.0.41"),sQuery(id+"F3.wireOp",EDGE,"E1824.0.42"),sQuery(id+"F3.wireOp",EDGE,"E1824.0.43"),sQuery(id+"F3.wireOp",EDGE,"E1824.0.44"),sQuery(id+"F3.wireOp",EDGE,"E1824.0.45"),sQuery(id+"F3.wireOp",EDGE,"E1824.0.46"),sQuery(id+"F3.wireOp",EDGE,"E1824.0.47"),sQuery(id+"F3.wireOp",EDGE,"E1824.0.48"),sQuery(id+"F3.wireOp",EDGE,"E1824.0.49"),sQuery(id+"F3.wireOp",EDGE,"E1824.0.50"),sQuery(id+"F3.wireOp",EDGE,"E1824.0.51"),sQuery(id+"F3.wireOp",EDGE,"E1824.0.52"),sQuery(id+"F3.wireOp",EDGE,"E1824.0.53"),sQuery(id+"F3.wireOp",EDGE,"E1824.0.54"),sQuery(id+"F3.wireOp",EDGE,"E1824.0.55")])],"isStart":true});
            var sketch = newSketch(context, id + "F7", { "sketchPlane" : qUnion([Q0])});
            skCircle(sketch, "E1827", {"center": v(0, 0) * mm, "radius": 35.15 * mm});
            skCircle(sketch, "E1828", {"center": v(0, 0) * mm, "radius": 28.15 * mm});
            skSolve(sketch);
        }
        {
            var Q0;
            Q0=qSketchRegion(id+"F7",true);
            extrude(context, id + "F8", {"entities" : qUnion([Q0]), "operationType" : NewBodyOperationType.ADD, "oppositeDirection" : true, "depth" : (getVariable(context, 'idlerThick')) * mm, "offsetDistance" : 25 * mm});
        }
        {
            var Q0;
            Q0=makeQuery(id+"F8.opExtrude","CAP_EDGE",EDGE,{"disambiguationData":[OSD([sQuery(id+"F7.wireOp",EDGE,"E1827")])],"isStart":false});
            var Q1;
            Q1=makeQuery(id+"F6.opExtrude","CAP_EDGE",EDGE,{"disambiguationData":[OSD([sQuery(id+"F5.wireOp",EDGE,"E1825")])],"isStart":false});
            fillet(context, id + "F9", {"entities" : qUnion([Q0, Q1]), "radius" : (getVariable(context, 'filletSize')) * mm, "tangentPropagation" : true, "allowEdgeOverflow" : false});
        }
    });
